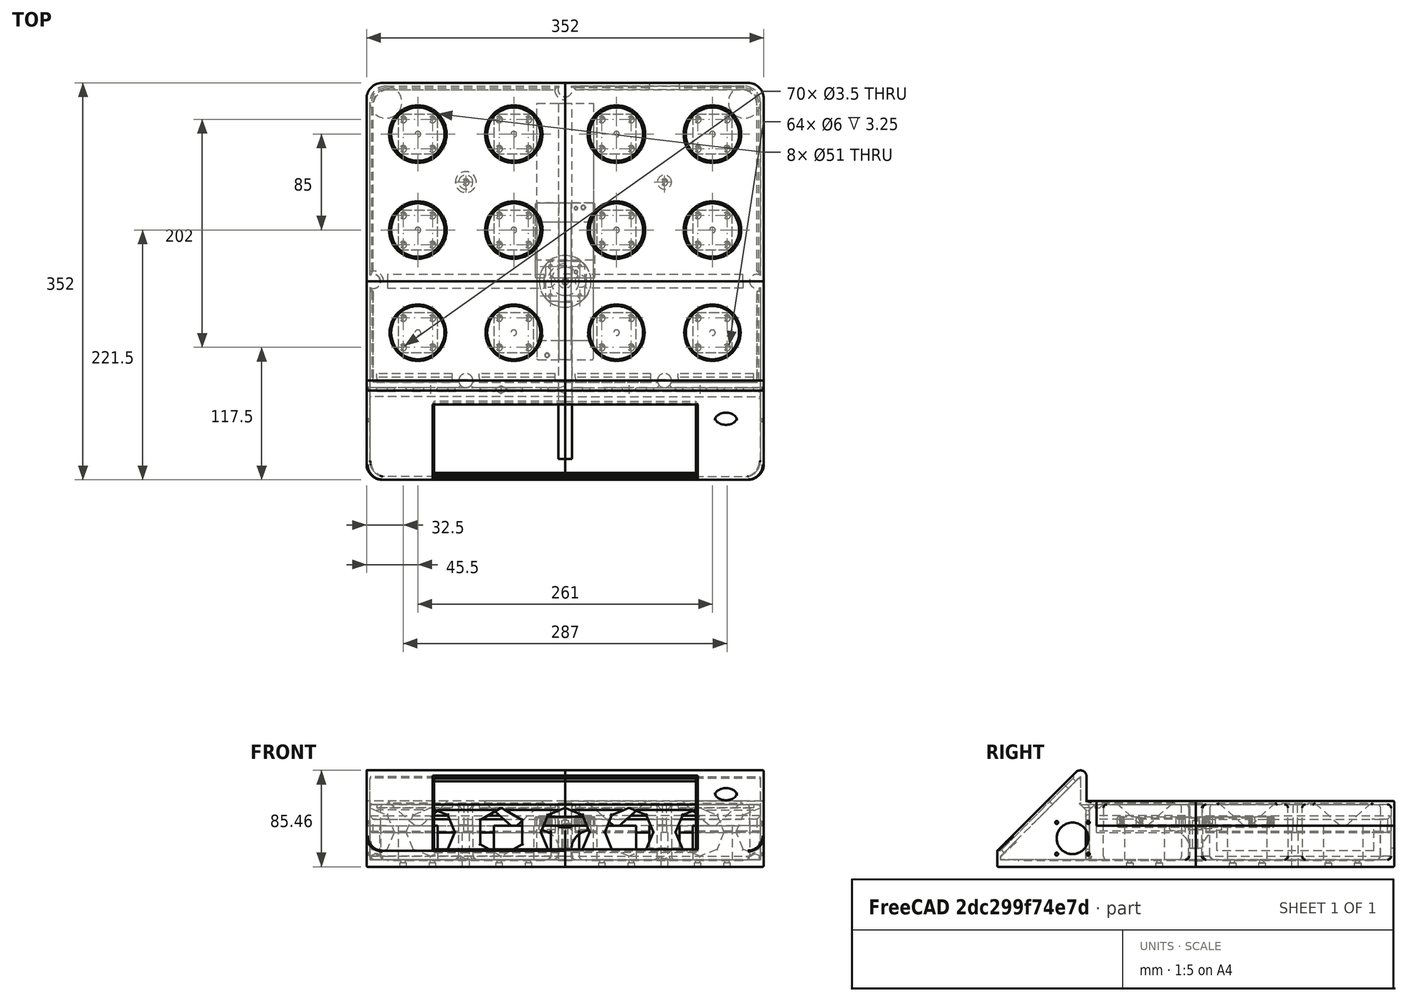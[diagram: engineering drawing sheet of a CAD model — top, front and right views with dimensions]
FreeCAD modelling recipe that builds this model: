
FCSTD DOCUMENT  (FreeCAD 2023.131R26244 +5365 (Git))
Label: Magnetic Stirrer
License: All rights reserved
LicenseURL: http://en.wikipedia.org/wiki/All_rights_reserved
objects: Sketcher::SketchObject×111, PartDesign::Pocket×58, PartDesign::Pad×49, PartDesign::Fillet×26, PartDesign::Body×19, PartDesign::Chamfer×13, PartDesign::Hole×3, Spreadsheet::Sheet×1, PartDesign::Revolution×1
note: 691 computed .brp shape members not serialized (recipe doc carries the construction recipe); baked Part::Feature solids carry a one-line shape summary decoded from their .brp

FEATURE [Spreadsheet::Sheet] Spreadsheet  label="Parameters"
  PythonMode = false
  ShowCells = 0
  TreeRank = 10
  cells = A1=Thickness; B1(thickness)=3; A2=Clearance; B2(clearance)=0.4; A3=Station Diameter; B3(station_diameter)=85; A4=Stir Bar Length; B4(stir_bar_length)=28; A5=Lap Join Thickness; B5(lap_join_thickness)=1; A7=Screw Shaft Diameter; B7(screw_shaft_diameter)=3.5; D7=M3; A8=Screw Head Diameter; B8(screw_head_diameter)=6; A9=Threaded Insert Hole Diameter; B9(insert_hole_diameter)=3.74; A11=Magnet Diameter; B11(magnet_diameter)=10; A12=Magnet Thickness; B12(magnet_thickness)=3; A14=Motor Shaft Diameter; B14(motor_shaft_diameter)=5; A15=Motor Shaft Flat Diameter; B15(motor_shaft_flat_diameter)=4.5; A16=Motor Shaft Length; B16(motor_shaft_length)=19; A17=Motor Width; B17(motor_width)=35; A18=Motor Height; B18(motor_height)=30; A19=Motor Screw Spacing; B19(motor_screw_spacing)=26; A20=Motor Screw Shaft Diameter; B20(motor_screw_shaft_diameter)=3.5; D20=M3; A21=Motor Screw Head Diameter; B21(motor_screw_head_diameter)=6; A22=Motor Screw Head Height; B22(motor_screw_head_height)=3.25; A23=Motor Shaft Mouth Diameter; B23(motor_shaft_mount_diameter)==stir_bar_length + magnet_diameter + 4 * thickness; A25=Screen Angle; B25(screen_angle)=135; A26=Screen Opening Width; B26(screen_opening_width)=232; A27=Screen Opening Height; B27(screen_opening_height)=89.5; A28=Screen Overall Width; B28(screen_overall_width)=239; A29=Screen Overall Heigth; B29(screen_overall_height)=94; A30=Screen Overall Thickness; B30(screen_overall_thickness)=12; A31=Screen Body Thickness; B31(screen_body_thickness)=5.5; A32=Screen Screen Thickness; B32(screen_screen_thickness)=1.5; A33=Screen Relief Width; B33(screen_relief_width)=1.5; A34=Screen Relief Depth; B34(screen_relief_depth)=2; A35=Screen Position; B35(screen_position)=92; A37=Power Supply Width; B37(psu_width)=50; A38=Power Supply Length; B38(psu_length)=139; A39=Power Supply Height; B39(psu_height)=22.25; A40=PSU Screw x-offset; B40(psu_screw_x_offset)==psu_width - 18; A41=PSU Screw y-offset; B41(psu_screw_y_offset)==psu_length - 8; A42=PSU Screw Length; B42(psu_screw_length)=8; A44=Power Connector Width; B44(power_connector_width)=26.8; A45=Power Connector Height; B45(power_connector_height)=19.9; A46=Power Switch Diameter; B46(power_switch_diameter)=19.5; A48=Fan Width; B48(fan_width)=29.9; A49=Fan Diameter; B49(fan_diameter)=28; A50=Fan Screw Hole Distance; B50(fan_screw_distance)=28; A51=Fan Screw Hole Diameter; B51(fan_screw_hole_diameter)=2.6; A53=PCB Board Width; B53(pcb_width)=105; A54=PCB Board Length; B54(pcb_length)=50; A55=PCB Board H Screw Distance; B55(pcb_h_screw)=97; A56=PCB Board V Screw Distance; B56(pcb_v_screw)=42
FEATURE [Sketcher::SketchObject] Sketch003
  ArcFitTolerance = 1e-06
  AttachmentSupport = -> [XY_Plane001]
  ExternalBSplineMaxDegree = 5
  ExternalBSplineTolerance = 0.0001
  FullyConstrained = true
  InternalTolerance = 1e-06
  InvalidShape = false
  MakeInternals = false
  MapMode = 5
  Support = -> [XY_Plane001]
  TreeRank = 37
  ValidateShape = true
  expr: Constraints[11] = <<Parameters>>.station_diameter
  expr: Constraints[12] = <<Parameters>>.station_diameter
  expr: Constraints[14] = <<Parameters>>.motor_shaft_mount_diameter + 1
  expr: Constraints[25] = <<Parameters>>.station_diameter / 3
  expr: Constraints[26] = <<Parameters>>.station_diameter + <<Parameters>>.thickness
  expr: Constraints[27] = (<<Parameters>>.station_diameter + <<Parameters>>.thickness) * 2
  expr: Constraints[30] = (<<Parameters>>.station_diameter + <<Parameters>>.thickness) * 2
  expr: Constraints[31] = <<Parameters>>.station_diameter + <<Parameters>>.thickness
  expr: Constraints[4] = <<Parameters>>.station_diameter
  sketch-geometry (14):
    g0: LineSegment StartX=88 StartY=88 StartZ=0 EndX=-73.8333 EndY=88 EndZ=0
    g1: LineSegment StartX=-88 StartY=73.8333 StartZ=0 EndX=-88 EndY=-88 EndZ=0
    g2: GeomPoint [constr] X=0 Y=0 Z=0
    g3: Circle [constr] CenterX=-42.5 CenterY=42.5 CenterZ=0 NormalX=0 NormalY=0 NormalZ=1 AngleXU=0 Radius=42.5
    g4: Circle [constr] CenterX=42.5 CenterY=42.5 CenterZ=0 NormalX=0 NormalY=0 NormalZ=1 AngleXU=0 Radius=42.5
    g5: Circle [constr] CenterX=-42.5 CenterY=-42.5 CenterZ=0 NormalX=0 NormalY=0 NormalZ=1 AngleXU=0 Radius=42.5
    g6: Circle [constr] CenterX=42.5 CenterY=-42.5 CenterZ=0 NormalX=0 NormalY=0 NormalZ=1 AngleXU=0 Radius=42.5
    g7: Circle CenterX=-42.5 CenterY=42.5 CenterZ=0 NormalX=0 NormalY=0 NormalZ=1 AngleXU=0 Radius=25.5
    g8: Circle CenterX=42.5 CenterY=42.5 CenterZ=0 NormalX=0 NormalY=0 NormalZ=1 AngleXU=0 Radius=25.5
    g9: Circle CenterX=42.5 CenterY=-42.5 CenterZ=0 NormalX=0 NormalY=0 NormalZ=1 AngleXU=0 Radius=25.5
    g10: Circle CenterX=-42.5 CenterY=-42.5 CenterZ=0 NormalX=0 NormalY=0 NormalZ=1 AngleXU=0 Radius=25.5
    g11: LineSegment StartX=88 StartY=-88 StartZ=0 EndX=88 EndY=88 EndZ=0
    g12: LineSegment StartX=-88 StartY=-88 StartZ=0 EndX=88 EndY=-88 EndZ=0
    g13: ArcOfCircle CenterX=-73.8333 CenterY=73.8333 CenterZ=0 NormalX=0 NormalY=0 NormalZ=1 AngleXU=0 Radius=14.1667 StartAngle=1.5708 EndAngle=3.14159
  constraints (32):
    c: Coincident(g11,g0)
    c: Horizontal(g0)
    c: Vertical(g1)
    c: Coincident(g2,g-1)
    c: Diameter(g3) = 85
    c: Equal(g3,g4)
    c: Equal(g3,g5)
    c: Equal(g3,g6)
    c: Symmetric(g3,g6,g2)
    c: Symmetric(g5,g4,g2)
    c: Symmetric(g3,g5,g-1)
    c: DistanceX(g3,g4) = 85
    c: DistanceY(g5,g3) = 85
    c: Coincident(g7,g3)
    c: Diameter(g7) = 51
    c: Coincident(g8,g4)
    c: Coincident(g9,g6)
    c: Coincident(g10,g5)
    c: Equal(g7,g8)
    c: Equal(g7,g10)
    c: Equal(g7,g9)
    c: Vertical(g11)
    c: Horizontal(g12)
    c: Coincident(g12,g1)
    c: Coincident(g11,g12)
    c: Diameter(g13) = 28.3333
    c: DistanceY(g2,g0) = 88
    c: DistanceY(g11,g0) = 176
    c: Tangent(g0,g13) = -1.5708
    c: Tangent(g1,g13) = -1.5708
    c: DistanceX(g1,g11) = 176
    c: DistanceX(g2,g0) = 88
FEATURE [PartDesign::Pad] Pad001
  AddSubType = 0
  AlongSketchNormal = false
  AutoTaperInnerAngle = true
  CheckUpToFaceLimits = true
  ClaimChildren = false
  Direction = (0,0,1)
  Fit = 0
  FitJoin = 0
  InnerFit = 0
  InnerFitJoin = 0
  InvalidShape = false
  Length = 3
  Length2 = 1
  Linearize = true
  NewSolid = false
  Profile = -> Sketch003
  Suppress = false
  TaperInnerAngle = 0
  TaperInnerAngleRev = 0
  TreeRank = 38
  Type = 0
  ValidateShape = true
  _ProfileBasedVersion = 1
  expr: Length = <<Parameters>>.thickness
  expr: Length2 = <<Parameters>>.lap_join_thickness
FEATURE [Sketcher::SketchObject] Sketch004
  ArcFitTolerance = 1e-06
  ExternalBSplineMaxDegree = 5
  ExternalBSplineTolerance = 0.0001
  FullyConstrained = true
  InternalTolerance = 1e-06
  InvalidShape = false
  MakeInternals = false
  MapMode = 2
  TreeRank = 39
  ValidateShape = true
  expr: Constraints[13] = <<Parameters>>.station_diameter + <<Parameters>>.thickness
  expr: Constraints[19] = <<Parameters>>.motor_shaft_mount_diameter / 4
  expr: Constraints[2] = <<Parameters>>.thickness
  expr: Constraints[32] = <<Parameters>>.motor_shaft_mount_diameter / 4
  expr: Constraints[33] = <<Parameters>>.motor_shaft_mount_diameter / 4
  expr: Constraints[34] = <<Parameters>>.station_diameter + <<Parameters>>.thickness
  expr: Constraints[35] = <<Parameters>>.station_diameter + <<Parameters>>.thickness
  expr: Constraints[3] = <<Parameters>>.station_diameter + <<Parameters>>.thickness
  expr: Constraints[42] = <<Parameters>>.thickness
  expr: Constraints[43] = <<Parameters>>.motor_shaft_mount_diameter / 4
  expr: Constraints[44] = <<Parameters>>.motor_shaft_mount_diameter / 4
  expr: Constraints[4] = <<Parameters>>.station_diameter + <<Parameters>>.thickness
  expr: Constraints[8] = <<Parameters>>.station_diameter / 3
  sketch-geometry (15):
    g0: LineSegment StartX=-88 StartY=-88 StartZ=0 EndX=-88 EndY=73.8333 EndZ=0
    g1: LineSegment StartX=-85 StartY=-82.6615 StartZ=0 EndX=-85 EndY=70.8333 EndZ=0
    g2: LineSegment [constr] StartX=0 StartY=0 StartZ=0 EndX=-83.8507 EndY=83.8507 EndZ=0
    g3: ArcOfCircle CenterX=-73.8333 CenterY=73.8333 CenterZ=0 NormalX=0 NormalY=0 NormalZ=1 AngleXU=0 Radius=14.1667 StartAngle=1.5708 EndAngle=3.14159
    g4: ArcOfCircle CenterX=-70.8333 CenterY=70.8333 CenterZ=0 NormalX=0 NormalY=0 NormalZ=1 AngleXU=0 Radius=14.1667 StartAngle=1.57079 EndAngle=3.14159
    g5: LineSegment StartX=-73.8333 StartY=88 StartZ=0 EndX=88 EndY=88 EndZ=0
    g6: LineSegment StartX=-70.8333 StartY=85 StartZ=0 EndX=82.6615 EndY=85 EndZ=0
    g7: ArcOfCircle CenterX=88 CenterY=81.75 CenterZ=0 NormalX=0 NormalY=0 NormalZ=1 AngleXU=0 Radius=6.25 StartAngle=2.59474 EndAngle=4.71239
    g8: ArcOfCircle CenterX=-81.75 CenterY=-88 CenterZ=0 NormalX=0 NormalY=0 NormalZ=1 AngleXU=0 Radius=6.25 StartAngle=4.1e-15 EndAngle=2.11765
    g9: LineSegment StartX=88 StartY=88 StartZ=0 EndX=88 EndY=75.5 EndZ=0
    g10: LineSegment StartX=-88 StartY=-88 StartZ=0 EndX=-75.5 EndY=-88 EndZ=0
    g11: Circle CenterX=0 CenterY=0 CenterZ=0 NormalX=0 NormalY=0 NormalZ=1 AngleXU=0 Radius=6.25
    g12: ArcOfCircle CenterX=88 CenterY=-88 CenterZ=0 NormalX=0 NormalY=0 NormalZ=1 AngleXU=0 Radius=12.5 StartAngle=1.5708 EndAngle=3.14159
    g13: LineSegment StartX=88 StartY=-88 StartZ=0 EndX=75.5 EndY=-88 EndZ=0
    g14: LineSegment StartX=88 StartY=-88 StartZ=0 EndX=88 EndY=-75.5 EndZ=0
  constraints (45):
    c: Vertical(g0)
    c: Vertical(g1)
    c: DistanceX(g0,g1) = 3
    c: DistanceX(g0,g-1) = 88
    c: DistanceY(g0,g-1) = 88
    c: Coincident(g2,g-1)
    c: Angle(g-2,g2) = 0.785398
    c: PointOnObject(g3,g2)
    c: Diameter(g3) = 28.3333
    c: PointOnObject(g4,g2)
    c: Equal(g3,g4)
    c: Horizontal(g5)
    c: Horizontal(g6)
    c: DistanceX(g2,g5) = 88
    c: PointOnObject(g2,g3)
    c: Coincident(g4,g6)
    c: Tangent(g3,g5) = 1.5708
    c: Tangent(g4,g1) = 1.5708
    c: Tangent(g3,g0) = 1.5708
    c: Diameter(g7) = 12.5
    c: Equal(g7,g8)
    c: Vertical(g9)
    c: PointOnObject(g7,g9)
    c: Horizontal(g10)
    c: PointOnObject(g8,g10)
    c: Coincident(g9,g5)
    c: Coincident(g7,g9)
    c: Coincident(g7,g6)
    c: Coincident(g10,g0)
    c: Coincident(g8,g1)
    c: Coincident(g8,g10)
    c: Coincident(g11,g2)
    c: Diameter(g11) = 12.5
    c: Radius(g12) = 12.5
    c: DistanceY(g12,g11) = 88
    c: DistanceX(g11,g12) = 88
    c: Coincident(g13,g12)
    c: Horizontal(g13)
    c: Coincident(g14,g12)
    c: Vertical(g14)
    c: Coincident(g12,g13)
    c: Coincident(g12,g14)
    c: DistanceY(g4,g3) = 3
    c: DistanceY(g7,g5) = 12.5
    c: DistanceX(g0,g8) = 12.5
FEATURE [PartDesign::Pad] Pad002
  AddSubType = 0
  AlongSketchNormal = false
  AutoTaperInnerAngle = true
  BaseFeature = -> Pad001
  CheckUpToFaceLimits = true
  ClaimChildren = false
  Direction = (0,0,1)
  Fit = 0
  FitJoin = 0
  InnerFit = 0
  InnerFitJoin = 0
  InvalidShape = false
  Length = 19
  Length2 = 100
  Linearize = true
  NewSolid = false
  Profile = -> Sketch004
  Reversed = true
  Suppress = false
  TaperInnerAngle = 0
  TaperInnerAngleRev = 0
  TreeRank = 40
  Type = 0
  ValidateShape = true
  _ProfileBasedVersion = 1
  expr: Length = <<Parameters>>.motor_shaft_length
FEATURE [Sketcher::SketchObject] Sketch005
  ArcFitTolerance = 1e-06
  ExternalBSplineMaxDegree = 5
  ExternalBSplineTolerance = 0.0001
  FullyConstrained = true
  InternalTolerance = 1e-06
  InvalidShape = false
  MakeInternals = false
  MapMode = 2
  Placement = pos=(0,0,-13) rot=(0,0,1;0rad)
  TreeRank = 41
  ValidateShape = true
  expr: Placement.Base.z = -<<Parameters>>.motor_shaft_length + 2 * <<Parameters>>.thickness
  expr: Constraints[11] = <<Parameters>>.station_diameter / 3
  expr: Constraints[20] = <<Parameters>>.station_diameter - 2 * <<Parameters>>.thickness
  expr: Constraints[5] = <<Parameters>>.thickness
  expr: Constraints[6] = <<Parameters>>.station_diameter
  expr: Constraints[7] = <<Parameters>>.station_diameter - 2 * <<Parameters>>.thickness
  sketch-geometry (9):
    g0: LineSegment StartX=-85 StartY=-79 StartZ=0 EndX=-85 EndY=70.8333 EndZ=0
    g1: LineSegment StartX=-82 StartY=-79 StartZ=0 EndX=-82 EndY=67.8333 EndZ=0
    g2: LineSegment StartX=-85 StartY=-79 StartZ=0 EndX=-82 EndY=-79 EndZ=0
    g3: LineSegment [constr] StartX=0 StartY=0 StartZ=0 EndX=-80.8507 EndY=80.8507 EndZ=0
    g4: ArcOfCircle CenterX=-70.8333 CenterY=70.8333 CenterZ=0 NormalX=0 NormalY=0 NormalZ=1 AngleXU=0 Radius=14.1667 StartAngle=1.5708 EndAngle=3.14159
    g5: ArcOfCircle CenterX=-67.8333 CenterY=67.8333 CenterZ=0 NormalX=0 NormalY=0 NormalZ=1 AngleXU=0 Radius=14.1667 StartAngle=1.5708 EndAngle=3.14159
    g6: LineSegment StartX=-70.8333 StartY=85 StartZ=0 EndX=79 EndY=85 EndZ=0
    g7: LineSegment StartX=-67.8334 StartY=82 StartZ=0 EndX=79 EndY=82 EndZ=0
    g8: LineSegment StartX=79 StartY=82 StartZ=0 EndX=79 EndY=85 EndZ=0
  constraints (26):
    c: Vertical(g0)
    c: Vertical(g1)
    c: Coincident(g2,g0)
    c: Coincident(g2,g1)
    c: Horizontal(g2)
    c: DistanceX(g0,g1) = 3
    c: DistanceX(g0,g-1) = 85
    c: DistanceY(g0,g-1) = 79
    c: Coincident(g3,g-1)
    c: Angle(g-2,g3) = 0.785398
    c: PointOnObject(g4,g3)
    c: Diameter(g4) = 28.3333
    c: PointOnObject(g5,g3)
    c: Equal(g4,g5)
    c: Horizontal(g6)
    c: Horizontal(g7)
    c: Coincident(g8,g7)
    c: Coincident(g8,g6)
    c: Vertical(g8)
    c: Equal(g2,g8)
    c: DistanceX(g3,g6) = 79
    c: PointOnObject(g3,g4)
    c: Coincident(g5,g7)
    c: Tangent(g4,g6) = 1.5708
    c: Tangent(g5,g1) = 1.5708
    c: Tangent(g4,g0) = 1.5708
FEATURE [PartDesign::Pad] Pad003
  AddSubType = 0
  AlongSketchNormal = false
  AutoTaperInnerAngle = true
  BaseFeature = -> Pad002
  CheckUpToFaceLimits = true
  ClaimChildren = false
  Direction = (0,0,1)
  Fit = 0
  FitJoin = 0
  InnerFit = 0
  InnerFitJoin = 0
  InvalidShape = false
  Length = 12
  Length2 = 100
  Linearize = true
  NewSolid = false
  Profile = -> Sketch005
  Reversed = true
  Suppress = false
  TaperInnerAngle = 0
  TaperInnerAngleRev = 0
  TreeRank = 42
  Type = 0
  ValidateShape = true
  _ProfileBasedVersion = 1
  expr: Length = <<Parameters>>.thickness * 4
FEATURE [Sketcher::SketchObject] Sketch006
  ArcFitTolerance = 1e-06
  ExternalBSplineMaxDegree = 5
  ExternalBSplineTolerance = 0.0001
  FullyConstrained = true
  InternalTolerance = 1e-06
  InvalidShape = false
  MakeInternals = false
  MapMode = 2
  TreeRank = 46
  ValidateShape = true
  expr: Constraints[14] = <<Parameters>>.thickness * 2
  expr: Constraints[16] = (<<Parameters>>.station_diameter + <<Parameters>>.thickness) * 2 - 4 * <<Parameters>>.thickness - <<Parameters>>.motor_shaft_mount_diameter / 2
  expr: Constraints[20] = <<Parameters>>.station_diameter + <<Parameters>>.thickness
  expr: Constraints[21] = <<Parameters>>.station_diameter + <<Parameters>>.thickness
  sketch-geometry (8):
    g0: LineSegment StartX=88 StartY=69.5 StartZ=0 EndX=82 EndY=69.5 EndZ=0
    g1: LineSegment StartX=82 StartY=69.5 StartZ=0 EndX=82 EndY=-69.5 EndZ=0
    g2: LineSegment StartX=82 StartY=-69.5 StartZ=0 EndX=88 EndY=-69.5 EndZ=0
    g3: LineSegment StartX=88 StartY=-69.5 StartZ=0 EndX=88 EndY=69.5 EndZ=0
    g4: LineSegment StartX=-69.5 StartY=-88 StartZ=0 EndX=69.5 EndY=-88 EndZ=0
    g5: LineSegment StartX=69.5 StartY=-88 StartZ=0 EndX=69.5 EndY=-82 EndZ=0
    g6: LineSegment StartX=69.5 StartY=-82 StartZ=0 EndX=-69.5 EndY=-82 EndZ=0
    g7: LineSegment StartX=-69.5 StartY=-82 StartZ=0 EndX=-69.5 EndY=-88 EndZ=0
  constraints (22):
    c: Coincident(g0,g1)
    c: Coincident(g1,g2)
    c: Coincident(g2,g3)
    c: Coincident(g3,g0)
    c: Horizontal(g0)
    c: Horizontal(g2)
    c: Vertical(g1)
    c: Coincident(g4,g5)
    c: Coincident(g5,g6)
    c: Coincident(g6,g7)
    c: Coincident(g7,g4)
    c: Horizontal(g6)
    c: Vertical(g5)
    c: Vertical(g7)
    c: DistanceX(g0,g0) = 6
    c: Equal(g0,g5)
    c: DistanceY(g2,g0) = 139
    c: Symmetric(g0,g2,g-1)
    c: Symmetric(g4,g4,g-2)
    c: Equal(g3,g4)
    c: DistanceX(g-1,g0) = 88
    c: DistanceY(g4,g-1) = 88
FEATURE [PartDesign::Pocket] Pocket001
  AddSubType = 1
  AutoTaperInnerAngle = true
  BaseFeature = -> Pad003
  CheckUpToFaceLimits = true
  ClaimChildren = false
  Fit = 0
  FitJoin = 0
  InnerFit = 0
  InnerFitJoin = 0
  InvalidShape = false
  Length = 1
  Length2 = 100
  Linearize = true
  NewSolid = false
  Profile = -> Sketch006
  Reversed = true
  Suppress = false
  TaperInnerAngle = 0
  TaperInnerAngleRev = 0
  TreeRank = 47
  Type = 0
  ValidateShape = true
  _ProfileBasedVersion = 1
  _Version = 1
  expr: Length = <<Parameters>>.lap_join_thickness
FEATURE [PartDesign::Chamfer] Chamfer
  AddSubType = 0
  Angle = 45
  Base = -> Pocket001 [Edge89]
  BaseFeature = -> Pocket001
  ChamferType = 0
  FlipDirection = false
  InvalidShape = false
  NewSolid = false
  Size = 2.99
  Size2 = 1
  SupportTransform = false
  Suppress = false
  TreeRank = 50
  ValidateShape = true
  expr: Size = <<Parameters>>.thickness - 0.01
FEATURE [Sketcher::SketchObject] Sketch008
  ArcFitTolerance = 1e-06
  AttachmentSupport = -> [XY_Plane002]
  ExternalBSplineMaxDegree = 5
  ExternalBSplineTolerance = 0.0001
  FullyConstrained = true
  InternalTolerance = 1e-06
  InvalidShape = false
  MakeInternals = false
  MapMode = 5
  Support = -> [XY_Plane002]
  TreeRank = 63
  ValidateShape = true
  expr: Constraints[11] = <<Parameters>>.station_diameter
  expr: Constraints[12] = <<Parameters>>.station_diameter
  expr: Constraints[17] = <<Parameters>>.station_diameter / 3
  expr: Constraints[18] = <<Parameters>>.station_diameter + <<Parameters>>.thickness
  expr: Constraints[19] = (<<Parameters>>.station_diameter + <<Parameters>>.thickness) * 2
  expr: Constraints[22] = (<<Parameters>>.station_diameter + <<Parameters>>.thickness) * 2
  expr: Constraints[23] = <<Parameters>>.station_diameter + <<Parameters>>.thickness
  expr: Constraints[4] = <<Parameters>>.station_diameter
  sketch-geometry (10):
    g0: LineSegment StartX=88 StartY=88 StartZ=0 EndX=-73.8333 EndY=88 EndZ=0
    g1: LineSegment StartX=-88 StartY=73.8333 StartZ=0 EndX=-88 EndY=-88 EndZ=0
    g2: GeomPoint [constr] X=0 Y=0 Z=0
    g3: Circle [constr] CenterX=-42.5 CenterY=42.5 CenterZ=0 NormalX=0 NormalY=0 NormalZ=1 AngleXU=0 Radius=42.5
    g4: Circle [constr] CenterX=42.5 CenterY=42.5 CenterZ=0 NormalX=0 NormalY=0 NormalZ=1 AngleXU=0 Radius=42.5
    g5: Circle [constr] CenterX=-42.5 CenterY=-42.5 CenterZ=0 NormalX=0 NormalY=0 NormalZ=1 AngleXU=0 Radius=42.5
    g6: Circle [constr] CenterX=42.5 CenterY=-42.5 CenterZ=0 NormalX=0 NormalY=0 NormalZ=1 AngleXU=0 Radius=42.5
    g7: LineSegment StartX=88 StartY=-88 StartZ=0 EndX=88 EndY=88 EndZ=0
    g8: LineSegment StartX=-88 StartY=-88 StartZ=0 EndX=88 EndY=-88 EndZ=0
    g9: ArcOfCircle CenterX=-73.8333 CenterY=73.8333 CenterZ=0 NormalX=0 NormalY=0 NormalZ=1 AngleXU=0 Radius=14.1667 StartAngle=1.5708 EndAngle=3.14159
  constraints (24):
    c: Coincident(g7,g0)
    c: Horizontal(g0)
    c: Vertical(g1)
    c: Coincident(g2,g-1)
    c: Diameter(g3) = 85
    c: Equal(g3,g4)
    c: Equal(g3,g5)
    c: Equal(g3,g6)
    c: Symmetric(g3,g6,g2)
    c: Symmetric(g5,g4,g2)
    c: Symmetric(g3,g5,g-1)
    c: DistanceX(g3,g4) = 85
    c: DistanceY(g5,g3) = 85
    c: Vertical(g7)
    c: Horizontal(g8)
    c: Coincident(g8,g1)
    c: Coincident(g7,g8)
    c: Diameter(g9) = 28.3333
    c: DistanceY(g2,g0) = 88
    c: DistanceY(g7,g0) = 176
    c: Tangent(g0,g9) = -1.5708
    c: Tangent(g1,g9) = -1.5708
    c: DistanceX(g1,g7) = 176
    c: DistanceX(g2,g0) = 88
FEATURE [PartDesign::Pad] Pad005
  AddSubType = 0
  AlongSketchNormal = false
  AutoTaperInnerAngle = true
  CheckUpToFaceLimits = true
  ClaimChildren = false
  Direction = (0,0,1)
  Fit = 0
  FitJoin = 0
  InnerFit = 0
  InnerFitJoin = 0
  InvalidShape = false
  Length = 6.25
  Length2 = 100
  Linearize = true
  NewSolid = false
  Profile = -> Sketch008
  Reversed = true
  Suppress = false
  TaperInnerAngle = 0
  TaperInnerAngleRev = 0
  TreeRank = 64
  Type = 0
  ValidateShape = true
  _ProfileBasedVersion = 1
  expr: Length = <<Parameters>>.thickness + <<Parameters>>.motor_screw_head_height
FEATURE [Sketcher::SketchObject] Sketch009
  ArcFitTolerance = 1e-06
  ExternalBSplineMaxDegree = 5
  ExternalBSplineTolerance = 0.0001
  FullyConstrained = false
  InternalTolerance = 1e-06
  InvalidShape = false
  MakeInternals = false
  MapMode = 2
  TreeRank = 65
  ValidateShape = true
  expr: Constraints[13] = <<Parameters>>.station_diameter + <<Parameters>>.thickness
  expr: Constraints[20] = <<Parameters>>.motor_shaft_mount_diameter / 4
  expr: Constraints[27] = <<Parameters>>.station_diameter + <<Parameters>>.thickness
  expr: Constraints[28] = <<Parameters>>.station_diameter + <<Parameters>>.thickness
  expr: Constraints[29] = <<Parameters>>.motor_shaft_mount_diameter / 4
  expr: Constraints[2] = <<Parameters>>.thickness
  expr: Constraints[3] = <<Parameters>>.station_diameter + <<Parameters>>.thickness
  expr: Constraints[4] = <<Parameters>>.station_diameter + <<Parameters>>.thickness
  expr: Constraints[8] = <<Parameters>>.station_diameter / 3
  sketch-geometry (15):
    g0: LineSegment StartX=-88 StartY=-88 StartZ=0 EndX=-88 EndY=73.8333 EndZ=0
    g1: LineSegment StartX=-85 StartY=-82.4087 StartZ=0 EndX=-85 EndY=70.8333 EndZ=0
    g2: LineSegment [constr] StartX=0 StartY=0 StartZ=0 EndX=-83.8507 EndY=83.8507 EndZ=0
    g3: ArcOfCircle CenterX=-73.8333 CenterY=73.8333 CenterZ=0 NormalX=0 NormalY=0 NormalZ=1 AngleXU=0 Radius=14.1667 StartAngle=1.5708 EndAngle=3.14159
    g4: ArcOfCircle CenterX=-70.8333 CenterY=70.8333 CenterZ=0 NormalX=0 NormalY=0 NormalZ=1 AngleXU=0 Radius=14.1667 StartAngle=1.57076 EndAngle=3.14159
    g5: LineSegment StartX=-73.8333 StartY=88 StartZ=0 EndX=88 EndY=88 EndZ=0
    g6: LineSegment StartX=-70.8328 StartY=85 StartZ=0 EndX=82.4428 EndY=85 EndZ=0
    g7: Circle CenterX=0 CenterY=0 CenterZ=0 NormalX=0 NormalY=0 NormalZ=1 AngleXU=0 Radius=6.25
    g8: ArcOfCircle CenterX=88 CenterY=-88 CenterZ=0 NormalX=0 NormalY=0 NormalZ=1 AngleXU=0 Radius=12.5 StartAngle=1.5708 EndAngle=3.14159
    g9: LineSegment StartX=88 StartY=-88 StartZ=0 EndX=75.5 EndY=-88 EndZ=0
    g10: LineSegment StartX=88 StartY=-88 StartZ=0 EndX=88 EndY=-75.5 EndZ=0
    g11: ArcOfCircle CenterX=88 CenterY=82.14 CenterZ=0 NormalX=0 NormalY=0 NormalZ=1 AngleXU=0 Radius=6.25 StartAngle=2.6663 EndAngle=4.71239
    g12: LineSegment StartX=88 StartY=88 StartZ=0 EndX=88 EndY=75.89 EndZ=0
    g13: ArcOfCircle CenterX=-82.2072 CenterY=-88 CenterZ=0 NormalX=0 NormalY=0 NormalZ=1 AngleXU=0 Radius=6.25 StartAngle=2.4e-15 EndAngle=2.03403
    g14: LineSegment StartX=-88 StartY=-88 StartZ=0 EndX=-75.9572 EndY=-88 EndZ=0
  constraints (42):
    c: Vertical(g0)
    c: Vertical(g1)
    c: DistanceX(g0,g1) = 3
    c: DistanceX(g0,g-1) = 88
    c: DistanceY(g0,g-1) = 88
    c: Coincident(g2,g-1)
    c: Angle(g-2,g2) = 0.785398
    c: PointOnObject(g3,g2)
    c: Diameter(g3) = 28.3333
    c: PointOnObject(g4,g2)
    c: Equal(g3,g4)
    c: Horizontal(g5)
    c: Horizontal(g6)
    c: DistanceX(g2,g5) = 88
    c: PointOnObject(g2,g3)
    c: Coincident(g4,g6)
    c: Tangent(g3,g5) = 1.5708
    c: Tangent(g4,g1) = 1.5708
    c: Tangent(g3,g0) = 1.5708
    c: Coincident(g7,g2)
    c: Diameter(g7) = 12.5
    c: Coincident(g9,g8)
    c: Coincident(g10,g8)
    c: Vertical(g10)
    c: Horizontal(g9)
    c: Coincident(g8,g9)
    c: Coincident(g8,g10)
    c: DistanceX(g7,g8) = 88
    c: DistanceY(g8,g7) = 88
    c: Radius(g8) = 12.5
    c: Equal(g7,g11)
    c: Vertical(g12)
    c: PointOnObject(g11,g12)
    c: Coincident(g12,g5)
    c: Coincident(g11,g12)
    c: Coincident(g11,g6)
    c: Equal(g7,g13)
    c: Horizontal(g14)
    c: PointOnObject(g13,g14)
    c: Coincident(g14,g0)
    c: Coincident(g13,g14)
    c: Coincident(g13,g1)
FEATURE [PartDesign::Pad] Pad006
  AddSubType = 0
  AlongSketchNormal = false
  AutoTaperInnerAngle = true
  BaseFeature = -> Pad005
  CheckUpToFaceLimits = true
  ClaimChildren = false
  Direction = (0,0,1)
  Fit = 0
  FitJoin = 0
  InnerFit = 0
  InnerFitJoin = 0
  InvalidShape = false
  Length = 30
  Length2 = 100
  Linearize = true
  NewSolid = false
  Profile = -> Sketch009
  Suppress = false
  TaperInnerAngle = 0
  TaperInnerAngleRev = 0
  TreeRank = 66
  Type = 0
  ValidateShape = true
  _ProfileBasedVersion = 1
  expr: Length = <<Parameters>>.motor_height
FEATURE [Sketcher::SketchObject] Sketch010
  ArcFitTolerance = 1e-06
  ExternalBSplineMaxDegree = 5
  ExternalBSplineTolerance = 0.0001
  FullyConstrained = true
  InternalTolerance = 1e-06
  InvalidShape = false
  MakeInternals = false
  MapMode = 2
  TreeRank = 67
  ValidateShape = true
  expr: Constraints[0] = <<Parameters>>.station_diameter
  expr: Constraints[19] = <<Parameters>>.motor_screw_spacing
  expr: Constraints[58] = <<Parameters>>.motor_screw_shaft_diameter
  expr: Constraints[7] = <<Parameters>>.station_diameter
  expr: Constraints[8] = <<Parameters>>.station_diameter
  sketch-geometry (40):
    g0: Circle [constr] CenterX=-42.5 CenterY=42.5 CenterZ=0 NormalX=0 NormalY=0 NormalZ=1 AngleXU=0 Radius=42.5
    g1: Circle [constr] CenterX=42.5 CenterY=42.5 CenterZ=0 NormalX=0 NormalY=0 NormalZ=1 AngleXU=0 Radius=42.5
    g2: Circle [constr] CenterX=-42.5 CenterY=-42.5 CenterZ=0 NormalX=0 NormalY=0 NormalZ=1 AngleXU=0 Radius=42.5
    g3: Circle [constr] CenterX=42.5 CenterY=-42.5 CenterZ=0 NormalX=0 NormalY=0 NormalZ=1 AngleXU=0 Radius=42.5
    g4: LineSegment [constr] StartX=-29.5 StartY=29.5 StartZ=0 EndX=-29.5 EndY=55.5 EndZ=0
    g5: LineSegment [constr] StartX=-29.5 StartY=55.5 StartZ=0 EndX=-55.5 EndY=55.5 EndZ=0
    g6: LineSegment [constr] StartX=-55.5 StartY=55.5 StartZ=0 EndX=-55.5 EndY=29.5 EndZ=0
    g7: LineSegment [constr] StartX=-55.5 StartY=29.5 StartZ=0 EndX=-29.5 EndY=29.5 EndZ=0
    g8: GeomPoint [constr] X=-42.5 Y=42.5 Z=0
    g9: LineSegment [constr] StartX=55.5 StartY=29.5 StartZ=0 EndX=55.5 EndY=55.5 EndZ=0
    g10: LineSegment [constr] StartX=55.5 StartY=55.5 StartZ=0 EndX=29.5 EndY=55.5 EndZ=0
    g11: LineSegment [constr] StartX=29.5 StartY=55.5 StartZ=0 EndX=29.5 EndY=29.5 EndZ=0
    g12: LineSegment [constr] StartX=29.5 StartY=29.5 StartZ=0 EndX=55.5 EndY=29.5 EndZ=0
    g13: GeomPoint [constr] X=42.5 Y=42.5 Z=0
    g14: LineSegment [constr] StartX=-29.5 StartY=-55.5 StartZ=0 EndX=-29.5 EndY=-29.5 EndZ=0
    g15: LineSegment [constr] StartX=-29.5 StartY=-29.5 StartZ=0 EndX=-55.5 EndY=-29.5 EndZ=0
    g16: LineSegment [constr] StartX=-55.5 StartY=-29.5 StartZ=0 EndX=-55.5 EndY=-55.5 EndZ=0
    g17: LineSegment [constr] StartX=-55.5 StartY=-55.5 StartZ=0 EndX=-29.5 EndY=-55.5 EndZ=0
    g18: GeomPoint [constr] X=-42.5 Y=-42.5 Z=0
    g19: LineSegment [constr] StartX=55.5 StartY=-55.5 StartZ=0 EndX=55.5 EndY=-29.5 EndZ=0
    g20: LineSegment [constr] StartX=55.5 StartY=-29.5 StartZ=0 EndX=29.5 EndY=-29.5 EndZ=0
    g21: LineSegment [constr] StartX=29.5 StartY=-29.5 StartZ=0 EndX=29.5 EndY=-55.5 EndZ=0
    g22: LineSegment [constr] StartX=29.5 StartY=-55.5 StartZ=0 EndX=55.5 EndY=-55.5 EndZ=0
    g23: GeomPoint [constr] X=42.5 Y=-42.5 Z=0
    g24: Circle CenterX=-55.5 CenterY=55.5 CenterZ=0 NormalX=0 NormalY=0 NormalZ=1 AngleXU=0 Radius=1.75
    g25: Circle CenterX=-29.5 CenterY=55.5 CenterZ=0 NormalX=0 NormalY=0 NormalZ=1 AngleXU=0 Radius=1.75
    g26: Circle CenterX=-29.5 CenterY=29.5 CenterZ=0 NormalX=0 NormalY=0 NormalZ=1 AngleXU=0 Radius=1.75
    g27: Circle CenterX=-55.5 CenterY=29.5 CenterZ=0 NormalX=0 NormalY=0 NormalZ=1 AngleXU=0 Radius=1.75
    g28: Circle CenterX=29.5 CenterY=55.5 CenterZ=0 NormalX=0 NormalY=0 NormalZ=1 AngleXU=0 Radius=1.75
    g29: Circle CenterX=55.5 CenterY=55.5 CenterZ=0 NormalX=0 NormalY=0 NormalZ=1 AngleXU=0 Radius=1.75
    g30: Circle CenterX=55.5 CenterY=29.5 CenterZ=0 NormalX=0 NormalY=0 NormalZ=1 AngleXU=0 Radius=1.75
    g31: Circle CenterX=29.5 CenterY=29.5 CenterZ=0 NormalX=0 NormalY=0 NormalZ=1 AngleXU=0 Radius=1.75
    g32: Circle CenterX=29.5 CenterY=-29.5 CenterZ=0 NormalX=0 NormalY=0 NormalZ=1 AngleXU=0 Radius=1.75
    g33: Circle CenterX=55.5 CenterY=-29.5 CenterZ=0 NormalX=0 NormalY=0 NormalZ=1 AngleXU=0 Radius=1.75
    g34: Circle CenterX=55.5 CenterY=-55.5 CenterZ=0 NormalX=0 NormalY=0 NormalZ=1 AngleXU=0 Radius=1.75
    g35: Circle CenterX=29.5 CenterY=-55.5 CenterZ=0 NormalX=0 NormalY=0 NormalZ=1 AngleXU=0 Radius=1.75
    g36: Circle CenterX=-55.5 CenterY=-29.5 CenterZ=0 NormalX=0 NormalY=0 NormalZ=1 AngleXU=0 Radius=1.75
    g37: Circle CenterX=-29.5 CenterY=-29.5 CenterZ=0 NormalX=0 NormalY=0 NormalZ=1 AngleXU=0 Radius=1.75
    g38: Circle CenterX=-29.5 CenterY=-55.5 CenterZ=0 NormalX=0 NormalY=0 NormalZ=1 AngleXU=0 Radius=1.75
    g39: Circle CenterX=-55.5 CenterY=-55.5 CenterZ=0 NormalX=0 NormalY=0 NormalZ=1 AngleXU=0 Radius=1.75
  constraints (89):
    c: Diameter(g0) = 85
    c: Equal(g0,g1)
    c: Equal(g0,g2)
    c: Equal(g0,g3)
    c: Symmetric(g0,g3,g-1)
    c: Symmetric(g1,g2,g-1)
    c: Symmetric(g0,g1,g-2)
    c: DistanceX(g0,g1) = 85
    c: DistanceY(g3,g1) = 85
    c: Coincident(g4,g5)
    c: Coincident(g5,g6)
    c: Coincident(g6,g7)
    c: Coincident(g7,g4)
    c: Horizontal(g5)
    c: Horizontal(g7)
    c: Vertical(g4)
    c: Vertical(g6)
    c: Symmetric(g5,g4,g8)
    c: Coincident(g8,g0)
    c: DistanceX(g5,g4) = 26
    c: Equal(g5,g6)
    c: Coincident(g9,g10)
    c: Coincident(g10,g11)
    c: Coincident(g11,g12)
    c: Coincident(g12,g9)
    c: Horizontal(g10)
    c: Horizontal(g12)
    c: Vertical(g9)
    c: Vertical(g11)
    c: Symmetric(g10,g9,g13)
    c: Coincident(g13,g1)
    c: Coincident(g14,g15)
    c: Coincident(g15,g16)
    c: Coincident(g16,g17)
    c: Coincident(g17,g14)
    c: Horizontal(g15)
    c: Horizontal(g17)
    c: Vertical(g14)
    c: Vertical(g16)
    c: Symmetric(g15,g14,g18)
    c: Coincident(g18,g2)
    c: Coincident(g19,g20)
    c: Coincident(g20,g21)
    c: Coincident(g21,g22)
    c: Coincident(g22,g19)
    c: Horizontal(g20)
    c: Horizontal(g22)
    c: Vertical(g19)
    c: Vertical(g21)
    c: Symmetric(g20,g19,g23)
    c: Coincident(g23,g3)
    c: Equal(g5,g10)
    c: Equal(g5,g11)
    c: Equal(g5,g20)
    c: Equal(g5,g21)
    c: Equal(g5,g15)
    c: Equal(g5,g16)
    c: Coincident(g24,g5)
    c: Diameter(g24) = 3.5
    c: Coincident(g25,g4)
    c: Coincident(g26,g4)
    c: Coincident(g27,g6)
    c: Coincident(g28,g10)
    c: Coincident(g29,g9)
    c: Coincident(g30,g9)
    c: Coincident(g31,g11)
    c: Coincident(g32,g20)
    c: Coincident(g33,g19)
    c: Coincident(g34,g19)
    c: Coincident(g35,g21)
    c: Coincident(g36,g15)
    c: Coincident(g37,g14)
    c: Coincident(g38,g14)
    c: Coincident(g39,g16)
    c: Equal(g24,g25)
    c: Equal(g24,g27)
    c: Equal(g24,g26)
    c: Equal(g24,g28)
    c: Equal(g24,g36)
    c: Equal(g24,g32)
    c: Equal(g28,g29)
    c: Equal(g28,g31)
    c: Equal(g28,g30)
    c: Equal(g32,g33)
    c: Equal(g32,g35)
    c: Equal(g32,g34)
    c: Equal(g36,g37)
    c: Equal(g36,g39)
    c: Equal(g36,g38)
FEATURE [PartDesign::Pocket] Pocket002
  AddSubType = 1
  AutoTaperInnerAngle = true
  BaseFeature = -> Pad006
  CheckUpToFaceLimits = true
  ClaimChildren = false
  Fit = 0
  FitJoin = 0
  InnerFit = 0
  InnerFitJoin = 0
  InvalidShape = false
  Length = 100
  Length2 = 100
  Linearize = true
  NewSolid = false
  Profile = -> Sketch010
  Suppress = false
  TaperInnerAngle = 0
  TaperInnerAngleRev = 0
  TreeRank = 68
  Type = 4
  ValidateShape = true
  _ProfileBasedVersion = 1
  _Version = 1
FEATURE [Sketcher::SketchObject] Sketch011
  ArcFitTolerance = 1e-06
  ExternalBSplineMaxDegree = 5
  ExternalBSplineTolerance = 0.0001
  FullyConstrained = true
  InternalTolerance = 1e-06
  InvalidShape = false
  MakeInternals = false
  MapMode = 2
  Placement = pos=(0,0,-6.25) rot=(0,0,1;0rad)
  TreeRank = 69
  ValidateShape = true
  expr: Placement.Base.z = -(<<Parameters>>.thickness + <<Parameters>>.motor_screw_head_height)
  expr: Constraints[0] = <<Parameters>>.station_diameter
  expr: Constraints[19] = <<Parameters>>.motor_screw_spacing
  expr: Constraints[58] = <<Parameters>>.motor_screw_head_diameter
  expr: Constraints[7] = <<Parameters>>.station_diameter
  expr: Constraints[8] = <<Parameters>>.station_diameter
  sketch-geometry (40):
    g0: Circle [constr] CenterX=-42.5 CenterY=42.5 CenterZ=0 NormalX=0 NormalY=0 NormalZ=1 AngleXU=0 Radius=42.5
    g1: Circle [constr] CenterX=42.5 CenterY=42.5 CenterZ=0 NormalX=0 NormalY=0 NormalZ=1 AngleXU=0 Radius=42.5
    g2: Circle [constr] CenterX=-42.5 CenterY=-42.5 CenterZ=0 NormalX=0 NormalY=0 NormalZ=1 AngleXU=0 Radius=42.5
    g3: Circle [constr] CenterX=42.5 CenterY=-42.5 CenterZ=0 NormalX=0 NormalY=0 NormalZ=1 AngleXU=0 Radius=42.5
    g4: LineSegment [constr] StartX=-29.5 StartY=29.5 StartZ=0 EndX=-29.5 EndY=55.5 EndZ=0
    g5: LineSegment [constr] StartX=-29.5 StartY=55.5 StartZ=0 EndX=-55.5 EndY=55.5 EndZ=0
    g6: LineSegment [constr] StartX=-55.5 StartY=55.5 StartZ=0 EndX=-55.5 EndY=29.5 EndZ=0
    g7: LineSegment [constr] StartX=-55.5 StartY=29.5 StartZ=0 EndX=-29.5 EndY=29.5 EndZ=0
    g8: GeomPoint [constr] X=-42.5 Y=42.5 Z=0
    g9: LineSegment [constr] StartX=55.5 StartY=29.5 StartZ=0 EndX=55.5 EndY=55.5 EndZ=0
    g10: LineSegment [constr] StartX=55.5 StartY=55.5 StartZ=0 EndX=29.5 EndY=55.5 EndZ=0
    g11: LineSegment [constr] StartX=29.5 StartY=55.5 StartZ=0 EndX=29.5 EndY=29.5 EndZ=0
    g12: LineSegment [constr] StartX=29.5 StartY=29.5 StartZ=0 EndX=55.5 EndY=29.5 EndZ=0
    g13: GeomPoint [constr] X=42.5 Y=42.5 Z=0
    g14: LineSegment [constr] StartX=-29.5 StartY=-55.5 StartZ=0 EndX=-29.5 EndY=-29.5 EndZ=0
    g15: LineSegment [constr] StartX=-29.5 StartY=-29.5 StartZ=0 EndX=-55.5 EndY=-29.5 EndZ=0
    g16: LineSegment [constr] StartX=-55.5 StartY=-29.5 StartZ=0 EndX=-55.5 EndY=-55.5 EndZ=0
    g17: LineSegment [constr] StartX=-55.5 StartY=-55.5 StartZ=0 EndX=-29.5 EndY=-55.5 EndZ=0
    g18: GeomPoint [constr] X=-42.5 Y=-42.5 Z=0
    g19: LineSegment [constr] StartX=55.5 StartY=-55.5 StartZ=0 EndX=55.5 EndY=-29.5 EndZ=0
    g20: LineSegment [constr] StartX=55.5 StartY=-29.5 StartZ=0 EndX=29.5 EndY=-29.5 EndZ=0
    g21: LineSegment [constr] StartX=29.5 StartY=-29.5 StartZ=0 EndX=29.5 EndY=-55.5 EndZ=0
    g22: LineSegment [constr] StartX=29.5 StartY=-55.5 StartZ=0 EndX=55.5 EndY=-55.5 EndZ=0
    g23: GeomPoint [constr] X=42.5 Y=-42.5 Z=0
    g24: Circle CenterX=-55.5 CenterY=55.5 CenterZ=0 NormalX=0 NormalY=0 NormalZ=1 AngleXU=0 Radius=3
    g25: Circle CenterX=-29.5 CenterY=55.5 CenterZ=0 NormalX=0 NormalY=0 NormalZ=1 AngleXU=0 Radius=3
    g26: Circle CenterX=-29.5 CenterY=29.5 CenterZ=0 NormalX=0 NormalY=0 NormalZ=1 AngleXU=0 Radius=3
    g27: Circle CenterX=-55.5 CenterY=29.5 CenterZ=0 NormalX=0 NormalY=0 NormalZ=1 AngleXU=0 Radius=3
    g28: Circle CenterX=29.5 CenterY=55.5 CenterZ=0 NormalX=0 NormalY=0 NormalZ=1 AngleXU=0 Radius=3
    g29: Circle CenterX=55.5 CenterY=55.5 CenterZ=0 NormalX=0 NormalY=0 NormalZ=1 AngleXU=0 Radius=3
    g30: Circle CenterX=55.5 CenterY=29.5 CenterZ=0 NormalX=0 NormalY=0 NormalZ=1 AngleXU=0 Radius=3
    g31: Circle CenterX=29.5 CenterY=29.5 CenterZ=0 NormalX=0 NormalY=0 NormalZ=1 AngleXU=0 Radius=3
    g32: Circle CenterX=29.5 CenterY=-29.5 CenterZ=0 NormalX=0 NormalY=0 NormalZ=1 AngleXU=0 Radius=3
    g33: Circle CenterX=55.5 CenterY=-29.5 CenterZ=0 NormalX=0 NormalY=0 NormalZ=1 AngleXU=0 Radius=3
    g34: Circle CenterX=55.5 CenterY=-55.5 CenterZ=0 NormalX=0 NormalY=0 NormalZ=1 AngleXU=0 Radius=3
    g35: Circle CenterX=29.5 CenterY=-55.5 CenterZ=0 NormalX=0 NormalY=0 NormalZ=1 AngleXU=0 Radius=3
    g36: Circle CenterX=-55.5 CenterY=-29.5 CenterZ=0 NormalX=0 NormalY=0 NormalZ=1 AngleXU=0 Radius=3
    g37: Circle CenterX=-29.5 CenterY=-29.5 CenterZ=0 NormalX=0 NormalY=0 NormalZ=1 AngleXU=0 Radius=3
    g38: Circle CenterX=-29.5 CenterY=-55.5 CenterZ=0 NormalX=0 NormalY=0 NormalZ=1 AngleXU=0 Radius=3
    g39: Circle CenterX=-55.5 CenterY=-55.5 CenterZ=0 NormalX=0 NormalY=0 NormalZ=1 AngleXU=0 Radius=3
  constraints (89):
    c: Diameter(g0) = 85
    c: Equal(g0,g1)
    c: Equal(g0,g2)
    c: Equal(g0,g3)
    c: Symmetric(g0,g3,g-1)
    c: Symmetric(g1,g2,g-1)
    c: Symmetric(g0,g1,g-2)
    c: DistanceX(g0,g1) = 85
    c: DistanceY(g3,g1) = 85
    c: Coincident(g4,g5)
    c: Coincident(g5,g6)
    c: Coincident(g6,g7)
    c: Coincident(g7,g4)
    c: Horizontal(g5)
    c: Horizontal(g7)
    c: Vertical(g4)
    c: Vertical(g6)
    c: Symmetric(g5,g4,g8)
    c: Coincident(g8,g0)
    c: DistanceX(g5,g4) = 26
    c: Equal(g5,g6)
    c: Coincident(g9,g10)
    c: Coincident(g10,g11)
    c: Coincident(g11,g12)
    c: Coincident(g12,g9)
    c: Horizontal(g10)
    c: Horizontal(g12)
    c: Vertical(g9)
    c: Vertical(g11)
    c: Symmetric(g10,g9,g13)
    c: Coincident(g13,g1)
    c: Coincident(g14,g15)
    c: Coincident(g15,g16)
    c: Coincident(g16,g17)
    c: Coincident(g17,g14)
    c: Horizontal(g15)
    c: Horizontal(g17)
    c: Vertical(g14)
    c: Vertical(g16)
    c: Symmetric(g15,g14,g18)
    c: Coincident(g18,g2)
    c: Coincident(g19,g20)
    c: Coincident(g20,g21)
    c: Coincident(g21,g22)
    c: Coincident(g22,g19)
    c: Horizontal(g20)
    c: Horizontal(g22)
    c: Vertical(g19)
    c: Vertical(g21)
    c: Symmetric(g20,g19,g23)
    c: Coincident(g23,g3)
    c: Equal(g5,g10)
    c: Equal(g5,g11)
    c: Equal(g5,g20)
    c: Equal(g5,g21)
    c: Equal(g5,g15)
    c: Equal(g5,g16)
    c: Coincident(g24,g5)
    c: Diameter(g24) = 6
    c: Coincident(g25,g4)
    c: Coincident(g26,g4)
    c: Coincident(g27,g6)
    c: Coincident(g28,g10)
    c: Coincident(g29,g9)
    c: Coincident(g30,g9)
    c: Coincident(g31,g11)
    c: Coincident(g32,g20)
    c: Coincident(g33,g19)
    c: Coincident(g34,g19)
    c: Coincident(g35,g21)
    c: Coincident(g36,g15)
    c: Coincident(g37,g14)
    c: Coincident(g38,g14)
    c: Coincident(g39,g16)
    c: Equal(g24,g25)
    c: Equal(g24,g27)
    c: Equal(g24,g26)
    c: Equal(g24,g28)
    c: Equal(g24,g36)
    c: Equal(g24,g32)
    c: Equal(g28,g29)
    c: Equal(g28,g31)
    c: Equal(g28,g30)
    c: Equal(g32,g33)
    c: Equal(g32,g35)
    c: Equal(g32,g34)
    c: Equal(g36,g37)
    c: Equal(g36,g39)
    c: Equal(g36,g38)
FEATURE [PartDesign::Pocket] Pocket003
  AddSubType = 1
  AutoTaperInnerAngle = true
  BaseFeature = -> Pocket002
  CheckUpToFaceLimits = true
  ClaimChildren = false
  Fit = 0
  FitJoin = 0
  InnerFit = 0
  InnerFitJoin = 0
  InvalidShape = false
  Length = 3.25
  Length2 = 100
  Linearize = true
  NewSolid = false
  Profile = -> Sketch011
  Reversed = true
  Suppress = false
  TaperInnerAngle = 0
  TaperInnerAngleRev = 0
  TreeRank = 70
  Type = 0
  ValidateShape = true
  _ProfileBasedVersion = 1
  _Version = 1
  expr: Length = <<Parameters>>.motor_screw_head_height
FEATURE [PartDesign::Chamfer] Chamfer003
  AddSubType = 0
  Angle = 45
  Base = -> Pocket003 [Edge59,Edge41,Edge42,Edge44,Edge43]
  BaseFeature = -> Pocket003
  ChamferType = 0
  FlipDirection = false
  InvalidShape = false
  NewSolid = false
  Size = 3
  Size2 = 1
  SupportTransform = false
  Suppress = false
  TreeRank = 71
  ValidateShape = true
  expr: Size = <<Parameters>>.thickness
FEATURE [PartDesign::Fillet] Fillet003
  AddSubType = 0
  Base = -> Chamfer003 [Edge51]
  BaseFeature = -> Chamfer003
  InvalidShape = false
  NewSolid = false
  Radius = 1
  SupportTransform = false
  Suppress = false
  TreeRank = 72
  ValidateShape = true
FEATURE [Sketcher::SketchObject] Sketch012
  ArcFitTolerance = 1e-06
  ExternalBSplineMaxDegree = 5
  ExternalBSplineTolerance = 0.0001
  FullyConstrained = true
  InternalTolerance = 1e-06
  InvalidShape = false
  MakeInternals = false
  MapMode = 2
  TreeRank = 75
  ValidateShape = true
  expr: Constraints[14] = <<Parameters>>.thickness * 2
  expr: Constraints[16] = (<<Parameters>>.station_diameter + <<Parameters>>.thickness) * 2 - 4 * <<Parameters>>.thickness - <<Parameters>>.motor_shaft_mount_diameter / 2
  expr: Constraints[20] = <<Parameters>>.station_diameter + <<Parameters>>.thickness
  expr: Constraints[21] = <<Parameters>>.station_diameter + <<Parameters>>.thickness
  sketch-geometry (8):
    g0: LineSegment StartX=88 StartY=69.5 StartZ=0 EndX=82 EndY=69.5 EndZ=0
    g1: LineSegment StartX=82 StartY=69.5 StartZ=0 EndX=82 EndY=-69.5 EndZ=0
    g2: LineSegment StartX=82 StartY=-69.5 StartZ=0 EndX=88 EndY=-69.5 EndZ=0
    g3: LineSegment StartX=88 StartY=-69.5 StartZ=0 EndX=88 EndY=69.5 EndZ=0
    g4: LineSegment StartX=-69.5 StartY=-88 StartZ=0 EndX=69.5 EndY=-88 EndZ=0
    g5: LineSegment StartX=69.5 StartY=-88 StartZ=0 EndX=69.5 EndY=-82 EndZ=0
    g6: LineSegment StartX=69.5 StartY=-82 StartZ=0 EndX=-69.5 EndY=-82 EndZ=0
    g7: LineSegment StartX=-69.5 StartY=-82 StartZ=0 EndX=-69.5 EndY=-88 EndZ=0
  constraints (22):
    c: Coincident(g0,g1)
    c: Coincident(g1,g2)
    c: Coincident(g2,g3)
    c: Coincident(g3,g0)
    c: Horizontal(g0)
    c: Horizontal(g2)
    c: Vertical(g1)
    c: Coincident(g4,g5)
    c: Coincident(g5,g6)
    c: Coincident(g6,g7)
    c: Coincident(g7,g4)
    c: Horizontal(g6)
    c: Vertical(g5)
    c: Vertical(g7)
    c: DistanceX(g0,g0) = 6
    c: Equal(g0,g5)
    c: DistanceY(g2,g0) = 139
    c: Symmetric(g0,g2,g-1)
    c: Symmetric(g4,g4,g-2)
    c: Equal(g3,g4)
    c: DistanceX(g-1,g0) = 88
    c: DistanceY(g4,g-1) = 88
FEATURE [PartDesign::Pocket] Pocket004
  AddSubType = 1
  AutoTaperInnerAngle = true
  BaseFeature = -> Fillet003
  CheckUpToFaceLimits = true
  ClaimChildren = false
  Fit = 0
  FitJoin = 0
  InnerFit = 0
  InnerFitJoin = 0
  InvalidShape = false
  Length = 1
  Length2 = 100
  Linearize = true
  NewSolid = false
  Profile = -> Sketch012
  Suppress = false
  TaperInnerAngle = 0
  TaperInnerAngleRev = 0
  TreeRank = 76
  Type = 0
  ValidateShape = true
  _ProfileBasedVersion = 1
  _Version = 1
  expr: Length = <<Parameters>>.lap_join_thickness
FEATURE [Sketcher::SketchObject] Sketch013
  ArcFitTolerance = 1e-06
  AttachmentSupport = -> [XY_Plane003]
  ExternalBSplineMaxDegree = 5
  ExternalBSplineTolerance = 0.0001
  FullyConstrained = true
  InternalTolerance = 1e-06
  InvalidShape = false
  MakeInternals = false
  MapMode = 5
  Support = -> [XY_Plane003]
  TreeRank = 91
  ValidateShape = true
  expr: Constraints[10] = <<Parameters>>.station_diameter
  expr: Constraints[11] = <<Parameters>>.station_diameter
  expr: Constraints[13] = <<Parameters>>.motor_shaft_mount_diameter + 1
  expr: Constraints[24] = (<<Parameters>>.station_diameter + <<Parameters>>.thickness) * 2
  expr: Constraints[26] = <<Parameters>>.station_diameter + <<Parameters>>.thickness
  expr: Constraints[27] = <<Parameters>>.station_diameter + <<Parameters>>.thickness
  expr: Constraints[28] = <<Parameters>>.station_diameter + <<Parameters>>.thickness
  expr: Constraints[29] = <<Parameters>>.station_diameter / 3
  expr: Constraints[3] = <<Parameters>>.station_diameter
  sketch-geometry (14):
    g0: LineSegment StartX=73.8333 StartY=88 StartZ=0 EndX=-88 EndY=88 EndZ=0
    g1: LineSegment StartX=-88 StartY=88 StartZ=0 EndX=-88 EndY=-88 EndZ=0
    g2: GeomPoint [constr] X=0 Y=0 Z=0
    g3: Circle [constr] CenterX=-42.5 CenterY=42.5 CenterZ=0 NormalX=0 NormalY=0 NormalZ=1 AngleXU=0 Radius=42.5
    g4: Circle [constr] CenterX=42.5 CenterY=42.5 CenterZ=0 NormalX=0 NormalY=0 NormalZ=1 AngleXU=0 Radius=42.5
    g5: Circle [constr] CenterX=-42.5 CenterY=-42.5 CenterZ=0 NormalX=0 NormalY=0 NormalZ=1 AngleXU=0 Radius=42.5
    g6: Circle [constr] CenterX=42.5 CenterY=-42.5 CenterZ=0 NormalX=0 NormalY=0 NormalZ=1 AngleXU=0 Radius=42.5
    g7: Circle CenterX=-42.5 CenterY=42.5 CenterZ=0 NormalX=0 NormalY=0 NormalZ=1 AngleXU=0 Radius=25.5
    g8: Circle CenterX=42.5 CenterY=42.5 CenterZ=0 NormalX=0 NormalY=0 NormalZ=1 AngleXU=0 Radius=25.5
    g9: Circle CenterX=42.5 CenterY=-42.5 CenterZ=0 NormalX=0 NormalY=0 NormalZ=1 AngleXU=0 Radius=25.5
    g10: Circle CenterX=-42.5 CenterY=-42.5 CenterZ=0 NormalX=0 NormalY=0 NormalZ=1 AngleXU=0 Radius=25.5
    g11: LineSegment StartX=88 StartY=-88 StartZ=0 EndX=88 EndY=73.8333 EndZ=0
    g12: LineSegment StartX=-88 StartY=-88 StartZ=0 EndX=88 EndY=-88 EndZ=0
    g13: ArcOfCircle CenterX=73.8333 CenterY=73.8333 CenterZ=0 NormalX=0 NormalY=0 NormalZ=1 AngleXU=0 Radius=14.1667 StartAngle=0 EndAngle=1.5708
  constraints (32):
    c: Horizontal(g0)
    c: Vertical(g1)
    c: Coincident(g2,g-1)
    c: Diameter(g3) = 85
    c: Equal(g3,g4)
    c: Equal(g3,g5)
    c: Equal(g3,g6)
    c: Symmetric(g3,g6,g2)
    c: Symmetric(g5,g4,g2)
    c: Symmetric(g3,g5,g-1)
    c: DistanceX(g3,g4) = 85
    c: DistanceY(g5,g3) = 85
    c: Coincident(g7,g3)
    c: Diameter(g7) = 51
    c: Coincident(g8,g4)
    c: Coincident(g9,g6)
    c: Coincident(g10,g5)
    c: Equal(g7,g8)
    c: Equal(g7,g10)
    c: Equal(g7,g9)
    c: Vertical(g11)
    c: Horizontal(g12)
    c: Coincident(g12,g1)
    c: Coincident(g11,g12)
    c: DistanceX(g1,g11) = 176
    c: Coincident(g0,g1)
    c: DistanceY(g2,g0) = 88
    c: DistanceX(g2,g11) = 88
    c: DistanceY(g11,g2) = 88
    c: Diameter(g13) = 28.3333
    c: Tangent(g13,g11) = -1.5708
    c: Tangent(g13,g0) = -1.5708
FEATURE [PartDesign::Pad] Pad007
  AddSubType = 0
  AlongSketchNormal = false
  AutoTaperInnerAngle = true
  CheckUpToFaceLimits = true
  ClaimChildren = false
  Direction = (0,0,1)
  Fit = 0
  FitJoin = 0
  InnerFit = 0
  InnerFitJoin = 0
  InvalidShape = false
  Length = 3
  Length2 = 100
  Linearize = true
  NewSolid = false
  Profile = -> Sketch013
  Suppress = false
  TaperInnerAngle = 0
  TaperInnerAngleRev = 0
  TreeRank = 92
  Type = 0
  ValidateShape = true
  _ProfileBasedVersion = 1
  expr: Length = <<Parameters>>.thickness
FEATURE [Sketcher::SketchObject] Sketch014
  ArcFitTolerance = 1e-06
  BaseAttacherType = Attacher::AttachEngine3D
  BaseMapMode = 2
  BaseMapPathParameter = 0
  BaseMapReversed = true
  ExternalBSplineMaxDegree = 5
  ExternalBSplineTolerance = 0.0001
  FullyConstrained = true
  InternalTolerance = 1e-06
  InvalidShape = false
  MakeInternals = false
  MapMode = 2
  TreeRank = 93
  ValidateShape = true
  expr: Constraints[10] = <<Parameters>>.station_diameter + <<Parameters>>.thickness
  expr: Constraints[11] = <<Parameters>>.motor_shaft_mount_diameter / 4
  expr: Constraints[18] = <<Parameters>>.motor_shaft_mount_diameter / 4
  expr: Constraints[21] = <<Parameters>>.station_diameter + <<Parameters>>.thickness
  expr: Constraints[22] = <<Parameters>>.station_diameter + <<Parameters>>.thickness
  expr: Constraints[26] = <<Parameters>>.thickness
  expr: Constraints[29] = <<Parameters>>.motor_shaft_mount_diameter / 4
  expr: Constraints[35] = <<Parameters>>.motor_shaft_mount_diameter / 4
  expr: Constraints[36] = <<Parameters>>.motor_shaft_mount_diameter / 4
  expr: Constraints[43] = <<Parameters>>.station_diameter + <<Parameters>>.thickness
  expr: Constraints[44] = <<Parameters>>.station_diameter + <<Parameters>>.thickness
  expr: Constraints[5] = <<Parameters>>.station_diameter / 3
  expr: Constraints[8] = <<Parameters>>.thickness
  expr: Constraints[9] = <<Parameters>>.station_diameter + <<Parameters>>.thickness
  sketch-geometry (15):
    g0: ArcOfCircle CenterX=73.8333 CenterY=73.8333 CenterZ=0 NormalX=0 NormalY=0 NormalZ=1 AngleXU=0 Radius=14.1667 StartAngle=6.28318 EndAngle=7.85398
    g1: ArcOfCircle CenterX=70.8333 CenterY=70.8333 CenterZ=0 NormalX=0 NormalY=0 NormalZ=1 AngleXU=0 Radius=14.1667 StartAngle=0 EndAngle=1.5708
    g2: LineSegment [constr] StartX=0 StartY=0 StartZ=0 EndX=73.8333 EndY=73.8333 EndZ=0
    g3: LineSegment StartX=73.8333 StartY=88 StartZ=0 EndX=-88 EndY=88 EndZ=0
    g4: LineSegment StartX=-82.6615 StartY=85 StartZ=0 EndX=70.8333 EndY=85 EndZ=0
    g5: ArcOfCircle CenterX=-88 CenterY=81.75 CenterZ=0 NormalX=0 NormalY=0 NormalZ=1 AngleXU=0 Radius=6.25 StartAngle=4.71239 EndAngle=6.83004
    g6: ArcOfCircle CenterX=81.75 CenterY=-88 CenterZ=0 NormalX=0 NormalY=0 NormalZ=1 AngleXU=0 Radius=6.25 StartAngle=1.02395 EndAngle=3.14159
    g7: LineSegment StartX=-88 StartY=88 StartZ=0 EndX=-88 EndY=75.5 EndZ=0
    g8: LineSegment StartX=75.5 StartY=-88 StartZ=0 EndX=88 EndY=-88 EndZ=0
    g9: LineSegment StartX=88 StartY=-88 StartZ=0 EndX=88 EndY=73.8333 EndZ=0
    g10: LineSegment StartX=85 StartY=-82.6615 StartZ=0 EndX=85 EndY=70.8333 EndZ=0
    g11: Circle CenterX=0 CenterY=0 CenterZ=0 NormalX=0 NormalY=0 NormalZ=1 AngleXU=0 Radius=6.25
    g12: ArcOfCircle CenterX=-88 CenterY=-88 CenterZ=0 NormalX=0 NormalY=0 NormalZ=1 AngleXU=0 Radius=12.5 StartAngle=0 EndAngle=1.5708
    g13: LineSegment StartX=-88 StartY=-88 StartZ=0 EndX=-88 EndY=-75.5 EndZ=0
    g14: LineSegment StartX=-88 StartY=-88 StartZ=0 EndX=-75.5 EndY=-88 EndZ=0
  constraints (45):
    c: Equal(g1,g0)
    c: Coincident(g2,g-1)
    c: Coincident(g2,g0)
    c: PointOnObject(g1,g2)
    c: Angle(g-1,g2) = 0.785398
    c: Diameter(g0) = 28.3333
    c: Horizontal(g3)
    c: Horizontal(g4)
    c: DistanceY(g4,g3) = 3
    c: DistanceX(g3,g2) = 88
    c: DistanceY(g2,g3) = 88
    c: Diameter(g5) = 12.5
    c: Equal(g5,g6)
    c: Vertical(g7)
    c: PointOnObject(g5,g7)
    c: Coincident(g7,g3)
    c: Coincident(g5,g4)
    c: Coincident(g5,g7)
    c: DistanceY(g5,g3) = 12.5
    c: Horizontal(g8)
    c: PointOnObject(g6,g8)
    c: DistanceX(g2,g8) = 88
    c: DistanceY(g8,g2) = 88
    c: Coincident(g9,g8)
    c: Vertical(g9)
    c: Vertical(g10)
    c: DistanceX(g10,g8) = 3
    c: Coincident(g6,g8)
    c: Coincident(g6,g10)
    c: DistanceX(g6,g8) = 12.5
    c: Coincident(g0,g9)
    c: Coincident(g1,g4)
    c: Tangent(g0,g3) = -1.5708
    c: Tangent(g1,g10) = -1.5708
    c: Coincident(g11,g2)
    c: Diameter(g11) = 12.5
    c: Radius(g12) = 12.5
    c: Coincident(g13,g12)
    c: Vertical(g13)
    c: Coincident(g14,g12)
    c: Horizontal(g14)
    c: Coincident(g12,g13)
    c: Coincident(g12,g14)
    c: DistanceY(g12,g11) = 88
    c: DistanceX(g12,g11) = 88
FEATURE [PartDesign::Pad] Pad008
  AddSubType = 0
  AlongSketchNormal = false
  AutoTaperInnerAngle = true
  BaseFeature = -> Pad007
  CheckUpToFaceLimits = true
  ClaimChildren = false
  Direction = (0,0,1)
  Fit = 0
  FitJoin = 0
  InnerFit = 0
  InnerFitJoin = 0
  InvalidShape = false
  Length = 19
  Length2 = 100
  Linearize = true
  NewSolid = false
  Profile = -> Sketch014
  Reversed = true
  Suppress = false
  TaperInnerAngle = 0
  TaperInnerAngleRev = 0
  TreeRank = 94
  Type = 0
  ValidateShape = true
  _ProfileBasedVersion = 1
  expr: Length = <<Parameters>>.motor_shaft_length
FEATURE [Sketcher::SketchObject] Sketch015
  ArcFitTolerance = 1e-06
  BaseAttacherType = Attacher::AttachEngine3D
  BaseMapMode = 2
  BaseMapPathParameter = 0
  BaseMapReversed = true
  ExternalBSplineMaxDegree = 5
  ExternalBSplineTolerance = 0.0001
  FullyConstrained = true
  InternalTolerance = 1e-06
  InvalidShape = false
  MakeInternals = false
  MapMode = 2
  Placement = pos=(0,0,-13) rot=(0,0,1;0rad)
  TreeRank = 95
  ValidateShape = true
  expr: Placement.Base.z = -<<Parameters>>.motor_shaft_length + 2 * <<Parameters>>.thickness
  expr: Constraints[10] = <<Parameters>>.station_diameter
  expr: Constraints[11] = <<Parameters>>.station_diameter
  expr: Constraints[14] = <<Parameters>>.thickness
  expr: Constraints[22] = <<Parameters>>.station_diameter - 2 * <<Parameters>>.thickness
  expr: Constraints[5] = <<Parameters>>.station_diameter / 3
  expr: Constraints[8] = <<Parameters>>.thickness
  expr: Constraints[9] = <<Parameters>>.station_diameter - 2 * <<Parameters>>.thickness
  sketch-geometry (9):
    g0: ArcOfCircle CenterX=70.8333 CenterY=70.8333 CenterZ=0 NormalX=0 NormalY=0 NormalZ=1 AngleXU=0 Radius=14.1667 StartAngle=1.28227e-08 EndAngle=1.5708
    g1: ArcOfCircle CenterX=67.8333 CenterY=67.8333 CenterZ=0 NormalX=0 NormalY=0 NormalZ=1 AngleXU=0 Radius=14.1667 StartAngle=0 EndAngle=1.5708
    g2: LineSegment [constr] StartX=0 StartY=0 StartZ=0 EndX=70.8333 EndY=70.8333 EndZ=0
    g3: LineSegment StartX=70.8333 StartY=85 StartZ=0 EndX=-79 EndY=85 EndZ=0
    g4: LineSegment StartX=-79 StartY=82 StartZ=0 EndX=67.8333 EndY=82 EndZ=0
    g5: LineSegment StartX=85 StartY=-79 StartZ=0 EndX=85 EndY=70.8333 EndZ=0
    g6: LineSegment StartX=82 StartY=-79 StartZ=0 EndX=82 EndY=67.8333 EndZ=0
    g7: LineSegment StartX=82 StartY=-79 StartZ=0 EndX=85 EndY=-79 EndZ=0
    g8: LineSegment StartX=-79 StartY=85 StartZ=0 EndX=-79 EndY=82 EndZ=0
  constraints (26):
    c: Equal(g1,g0)
    c: Coincident(g2,g-1)
    c: Coincident(g2,g0)
    c: PointOnObject(g1,g2)
    c: Angle(g-1,g2) = 0.785398
    c: Diameter(g0) = 28.3333
    c: Horizontal(g3)
    c: Horizontal(g4)
    c: DistanceY(g4,g3) = 3
    c: DistanceX(g3,g2) = 79
    c: DistanceY(g2,g3) = 85
    c: DistanceX(g2,g5) = 85
    c: Vertical(g5)
    c: Vertical(g6)
    c: DistanceX(g6,g5) = 3
    c: Coincident(g0,g5)
    c: Coincident(g1,g4)
    c: Tangent(g0,g3) = -1.5708
    c: Tangent(g1,g6) = -1.5708
    c: Coincident(g7,g6)
    c: Coincident(g7,g5)
    c: Horizontal(g7)
    c: DistanceY(g5,g2) = 79
    c: Coincident(g8,g3)
    c: Coincident(g8,g4)
    c: Vertical(g8)
FEATURE [PartDesign::Pad] Pad009
  AddSubType = 0
  AlongSketchNormal = false
  AutoTaperInnerAngle = true
  BaseFeature = -> Pad008
  CheckUpToFaceLimits = true
  ClaimChildren = false
  Direction = (0,0,1)
  Fit = 0
  FitJoin = 0
  InnerFit = 0
  InnerFitJoin = 0
  InvalidShape = false
  Length = 12
  Length2 = 100
  Linearize = true
  NewSolid = false
  Profile = -> Sketch015
  Reversed = true
  Suppress = false
  TaperInnerAngle = 0
  TaperInnerAngleRev = 0
  TreeRank = 96
  Type = 0
  ValidateShape = true
  _ProfileBasedVersion = 1
  expr: Length = <<Parameters>>.thickness * 4
FEATURE [Sketcher::SketchObject] Sketch016
  ArcFitTolerance = 1e-06
  ExternalBSplineMaxDegree = 5
  ExternalBSplineTolerance = 0.0001
  FullyConstrained = true
  InternalTolerance = 1e-06
  InvalidShape = false
  MakeInternals = false
  MapMode = 2
  TreeRank = 97
  ValidateShape = true
  expr: Constraints[14] = <<Parameters>>.thickness * 2
  expr: Constraints[16] = (<<Parameters>>.station_diameter + <<Parameters>>.thickness) * 2 - 4 * <<Parameters>>.thickness - <<Parameters>>.motor_shaft_mount_diameter / 2
  expr: Constraints[20] = <<Parameters>>.station_diameter + <<Parameters>>.thickness
  expr: Constraints[21] = <<Parameters>>.station_diameter + <<Parameters>>.thickness
  sketch-geometry (8):
    g0: LineSegment StartX=-82 StartY=69.5 StartZ=0 EndX=-88 EndY=69.5 EndZ=0
    g1: LineSegment StartX=-88 StartY=69.5 StartZ=0 EndX=-88 EndY=-69.5 EndZ=0
    g2: LineSegment StartX=-88 StartY=-69.5 StartZ=0 EndX=-82 EndY=-69.5 EndZ=0
    g3: LineSegment StartX=-82 StartY=-69.5 StartZ=0 EndX=-82 EndY=69.5 EndZ=0
    g4: LineSegment StartX=-69.5 StartY=-88 StartZ=0 EndX=69.5 EndY=-88 EndZ=0
    g5: LineSegment StartX=69.5 StartY=-88 StartZ=0 EndX=69.5 EndY=-82 EndZ=0
    g6: LineSegment StartX=69.5 StartY=-82 StartZ=0 EndX=-69.5 EndY=-82 EndZ=0
    g7: LineSegment StartX=-69.5 StartY=-82 StartZ=0 EndX=-69.5 EndY=-88 EndZ=0
  constraints (22):
    c: Coincident(g0,g1)
    c: Coincident(g1,g2)
    c: Coincident(g2,g3)
    c: Coincident(g3,g0)
    c: Horizontal(g0)
    c: Horizontal(g2)
    c: Vertical(g1)
    c: Coincident(g4,g5)
    c: Coincident(g5,g6)
    c: Coincident(g6,g7)
    c: Coincident(g7,g4)
    c: Horizontal(g6)
    c: Vertical(g5)
    c: Vertical(g7)
    c: DistanceX(g0,g0) = 6
    c: Equal(g0,g5)
    c: DistanceY(g2,g0) = 139
    c: Symmetric(g0,g2,g-1)
    c: Symmetric(g4,g4,g-2)
    c: Equal(g3,g4)
    c: DistanceY(g4,g-1) = 88
    c: DistanceX(g0,g-1) = 88
FEATURE [PartDesign::Pocket] Pocket005
  AddSubType = 1
  AutoTaperInnerAngle = true
  BaseFeature = -> Pad009
  CheckUpToFaceLimits = true
  ClaimChildren = false
  Fit = 0
  FitJoin = 0
  InnerFit = 0
  InnerFitJoin = 0
  InvalidShape = false
  Length = 1
  Length2 = 100
  Linearize = true
  NewSolid = false
  Profile = -> Sketch016
  Reversed = true
  Suppress = false
  TaperInnerAngle = 0
  TaperInnerAngleRev = 0
  TreeRank = 98
  Type = 0
  ValidateShape = true
  _ProfileBasedVersion = 1
  _Version = 1
  expr: Length = <<Parameters>>.lap_join_thickness
FEATURE [PartDesign::Chamfer] Chamfer004
  AddSubType = 0
  Angle = 45
  Base = -> Pocket005 [Edge87]
  BaseFeature = -> Pocket005
  ChamferType = 0
  FlipDirection = false
  InvalidShape = false
  NewSolid = false
  Size = 2.99
  Size2 = 1
  SupportTransform = false
  Suppress = false
  TreeRank = 99
  ValidateShape = true
  expr: Size = <<Parameters>>.thickness - 0.01
FEATURE [PartDesign::Chamfer] Chamfer005
  AddSubType = 0
  Angle = 45
  Base = -> Chamfer [Edge102]
  BaseFeature = -> Chamfer
  ChamferType = 0
  FlipDirection = false
  InvalidShape = false
  NewSolid = false
  Size = 1.5
  Size2 = 1
  SupportTransform = false
  Suppress = false
  TreeRank = 100
  ValidateShape = true
  expr: Size = <<Parameters>>.thickness / 2
FEATURE [PartDesign::Chamfer] Chamfer006
  AddSubType = 0
  Angle = 45
  Base = -> Chamfer004 [Edge103]
  BaseFeature = -> Chamfer004
  ChamferType = 0
  FlipDirection = false
  InvalidShape = false
  NewSolid = false
  Size = 1.5
  Size2 = 1
  SupportTransform = false
  Suppress = false
  TreeRank = 101
  ValidateShape = true
  expr: Size = <<Parameters>>.thickness / 2
FEATURE [PartDesign::Fillet] Fillet004
  AddSubType = 0
  Base = -> Chamfer006 [Edge77,Edge63,Edge69,Edge61,Edge31]
  BaseFeature = -> Chamfer006
  InvalidShape = false
  NewSolid = false
  Radius = 3
  SupportTransform = false
  Suppress = false
  TreeRank = 102
  ValidateShape = true
  expr: Radius = <<Parameters>>.thickness
FEATURE [PartDesign::Fillet] Fillet005
  AddSubType = 0
  Base = -> Chamfer005 [Edge76,Edge67,Edge61,Edge69,Edge68]
  BaseFeature = -> Chamfer005
  InvalidShape = false
  NewSolid = false
  Radius = 3
  SupportTransform = false
  Suppress = false
  TreeRank = 103
  ValidateShape = true
  expr: Radius = <<Parameters>>.thickness
FEATURE [PartDesign::Fillet] Fillet006
  AddSubType = 0
  Base = -> Fillet005 [Face40,Face39,Face42,Face41,Edge147]
  BaseFeature = -> Fillet005
  InvalidShape = false
  NewSolid = false
  Radius = 1
  SupportTransform = false
  Suppress = false
  TreeRank = 104
  ValidateShape = true
FEATURE [PartDesign::Fillet] Fillet007
  AddSubType = 0
  Base = -> Fillet004 [Face42,Face41,Face39,Face40,Edge145]
  BaseFeature = -> Fillet004
  InvalidShape = false
  NewSolid = false
  Radius = 1
  SupportTransform = false
  Suppress = false
  TreeRank = 105
  ValidateShape = true
FEATURE [Sketcher::SketchObject] Sketch017
  ArcFitTolerance = 1e-06
  ExternalBSplineMaxDegree = 5
  ExternalBSplineTolerance = 0.0001
  FullyConstrained = true
  InternalTolerance = 1e-06
  InvalidShape = false
  MakeInternals = false
  MapMode = 2
  Placement = pos=(0,0,-19) rot=(0,0,1;0rad)
  TreeRank = 106
  ValidateShape = true
  expr: Placement.Base.z = -<<Parameters>>.motor_shaft_length
  expr: Constraints[1] = <<Parameters>>.insert_hole_diameter
  sketch-geometry (1):
    g0: Circle CenterX=0 CenterY=0 CenterZ=0 NormalX=0 NormalY=0 NormalZ=1 AngleXU=0 Radius=1.87
  constraints (2):
    c: Coincident(g0,g-1)
    c: Diameter(g0) = 3.74
FEATURE [PartDesign::Pocket] Pocket006
  AddSubType = 1
  AutoTaperInnerAngle = true
  BaseFeature = -> Fillet006
  CheckUpToFaceLimits = true
  ClaimChildren = false
  Fit = 0
  FitJoin = 0
  InnerFit = 0
  InnerFitJoin = 0
  InvalidShape = false
  Length = 19
  Length2 = 100
  Linearize = true
  NewSolid = false
  Profile = -> Sketch017
  Reversed = true
  Suppress = false
  TaperInnerAngle = 0
  TaperInnerAngleRev = 0
  TreeRank = 107
  Type = 0
  ValidateShape = true
  _ProfileBasedVersion = 1
  _Version = 1
  expr: Length = <<Parameters>>.motor_shaft_length
FEATURE [PartDesign::Body] Body001  label="Top-Back-Left"
  AutoGroupSolids = false
  ClaimAllChildren = false
  ExportMode = 0
  Group = -> [Sketch003,Pad001,Sketch004,Pad002,Sketch005,Pad003,Pocket001,Chamfer,Chamfer005,Fillet005,Fillet006,Sketch006,Sketch017,Pocket006]
  InvalidShape = false
  Origin = -> Origin001
  Placement = pos=(-88,88,19) rot=(0.57735,0.57735,0.57735;0rad)
  Tip = -> Pocket006
  TreeRank = 36
  ValidateShape = true
  _ExportChildren = -> [Pad001,Pad002,Pad003,Pocket001,Chamfer,Chamfer005,Fillet005,Fillet006,Pocket006]
  _GroupVersion = 1
  expr: Placement.Base.x = -(<<Parameters>>.station_diameter + <<Parameters>>.thickness)
  expr: Placement.Base.y = <<Parameters>>.station_diameter + <<Parameters>>.thickness
  expr: Placement.Base.z = <<Parameters>>.motor_shaft_length
FEATURE [Sketcher::SketchObject] Sketch018
  ArcFitTolerance = 1e-06
  ExternalBSplineMaxDegree = 5
  ExternalBSplineTolerance = 0.0001
  FullyConstrained = true
  InternalTolerance = 1e-06
  InvalidShape = false
  MakeInternals = false
  MapMode = 2
  Placement = pos=(0,0,-19) rot=(0,0,1;0rad)
  TreeRank = 106
  ValidateShape = true
  expr: Placement.Base.z = -<<Parameters>>.motor_shaft_length
  expr: Constraints[1] = <<Parameters>>.insert_hole_diameter
  sketch-geometry (1):
    g0: Circle CenterX=0 CenterY=0 CenterZ=0 NormalX=0 NormalY=0 NormalZ=1 AngleXU=0 Radius=1.87
  constraints (2):
    c: Coincident(g0,g-1)
    c: Diameter(g0) = 3.74
FEATURE [PartDesign::Pocket] Pocket007
  AddSubType = 1
  AutoTaperInnerAngle = true
  BaseFeature = -> Fillet007
  CheckUpToFaceLimits = true
  ClaimChildren = false
  Fit = 0
  FitJoin = 0
  InnerFit = 0
  InnerFitJoin = 0
  InvalidShape = false
  Length = 19
  Length2 = 100
  Linearize = true
  NewSolid = false
  Profile = -> Sketch018
  Reversed = true
  Suppress = false
  TaperInnerAngle = 0
  TaperInnerAngleRev = 0
  TreeRank = 107
  Type = 0
  ValidateShape = true
  _ProfileBasedVersion = 1
  _Version = 1
  expr: Length = <<Parameters>>.motor_shaft_length
FEATURE [Sketcher::SketchObject] Sketch019
  ArcFitTolerance = 1e-06
  ExternalBSplineMaxDegree = 5
  ExternalBSplineTolerance = 0.0001
  FullyConstrained = true
  InternalTolerance = 1e-06
  InvalidShape = false
  MakeInternals = false
  MapMode = 2
  TreeRank = 108
  ValidateShape = true
  expr: Constraints[1] = <<Parameters>>.screw_head_diameter
  sketch-geometry (1):
    g0: Circle CenterX=0 CenterY=0 CenterZ=0 NormalX=0 NormalY=0 NormalZ=1 AngleXU=0 Radius=3
  constraints (2):
    c: Coincident(g0,g-1)
    c: Diameter(g0) = 6
FEATURE [PartDesign::Pocket] Pocket008
  AddSubType = 1
  AutoTaperInnerAngle = true
  BaseFeature = -> Pocket004
  CheckUpToFaceLimits = true
  ClaimChildren = false
  Fit = 0
  FitJoin = 0
  InnerFit = 0
  InnerFitJoin = 0
  InvalidShape = false
  Length = 100
  Length2 = 24
  Linearize = true
  NewSolid = false
  Profile = -> Sketch019
  Suppress = false
  TaperInnerAngle = 0
  TaperInnerAngleRev = 0
  TreeRank = 109
  Type = 4
  ValidateShape = true
  _ProfileBasedVersion = 1
  _Version = 1
  expr: Length2 = <<Parameters>>.motor_height - 2 * <<Parameters>>.thickness
FEATURE [Sketcher::SketchObject] Sketch020
  ArcFitTolerance = 1e-06
  ExternalBSplineMaxDegree = 5
  ExternalBSplineTolerance = 0.0001
  FullyConstrained = true
  InternalTolerance = 1e-06
  InvalidShape = false
  MakeInternals = false
  MapMode = 2
  TreeRank = 110
  ValidateShape = true
  expr: Constraints[1] = <<Parameters>>.screw_shaft_diameter
  sketch-geometry (1):
    g0: Circle CenterX=0 CenterY=0 CenterZ=0 NormalX=0 NormalY=0 NormalZ=1 AngleXU=0 Radius=1.75
  constraints (2):
    c: Coincident(g0,g-1)
    c: Diameter(g0) = 3.5
FEATURE [PartDesign::Pocket] Pocket009
  AddSubType = 1
  AutoTaperInnerAngle = true
  BaseFeature = -> Pocket008
  CheckUpToFaceLimits = true
  ClaimChildren = false
  Fit = 0
  FitJoin = 0
  InnerFit = 0
  InnerFitJoin = 0
  InvalidShape = false
  Length = 100
  Length2 = 100
  Linearize = true
  NewSolid = false
  Profile = -> Sketch020
  Suppress = false
  TaperInnerAngle = 0
  TaperInnerAngleRev = 0
  TreeRank = 111
  Type = 4
  ValidateShape = true
  _ProfileBasedVersion = 1
  _Version = 1
FEATURE [PartDesign::Body] Body002  label="Bottom-Back-Left"
  AutoGroupSolids = false
  ClaimAllChildren = false
  ExportMode = 0
  FixShape = 1
  Group = -> [Sketch008,Pad005,Sketch009,Pad006,Sketch010,Pocket002,Sketch011,Pocket003,Chamfer003,Fillet003,Sketch012,Pocket004,Sketch019,Pocket008,Sketch020,Pocket009]
  InvalidShape = false
  Origin = -> Origin002
  Placement = pos=(-88,88,-30) rot=(0.57735,0.57735,0.57735;0rad)
  Tip = -> Pocket009
  TreeRank = 89
  ValidateShape = true
  _ExportChildren = -> [Pad005,Pad006,Pocket002,Pocket003,Chamfer003,Fillet003,Pocket004,Pocket008,Pocket009]
  _GroupVersion = 1
  expr: Placement.Base.x = -(<<Parameters>>.station_diameter + <<Parameters>>.thickness)
  expr: Placement.Base.y = <<Parameters>>.station_diameter + <<Parameters>>.thickness
  expr: Placement.Base.z = -<<Parameters>>.motor_height
FEATURE [Sketcher::SketchObject] Sketch021
  ArcFitTolerance = 1e-06
  AttachmentSupport = -> [XY_Plane004]
  ExternalBSplineMaxDegree = 5
  ExternalBSplineTolerance = 0.0001
  FullyConstrained = true
  InternalTolerance = 1e-06
  InvalidShape = false
  MakeInternals = false
  MapMode = 5
  Support = -> [XY_Plane004]
  TreeRank = 122
  ValidateShape = true
  expr: Constraints[10] = <<Parameters>>.station_diameter
  expr: Constraints[11] = <<Parameters>>.station_diameter
  expr: Constraints[16] = (<<Parameters>>.station_diameter + <<Parameters>>.thickness) * 2
  expr: Constraints[18] = <<Parameters>>.station_diameter + <<Parameters>>.thickness
  expr: Constraints[19] = <<Parameters>>.station_diameter + <<Parameters>>.thickness
  expr: Constraints[20] = <<Parameters>>.station_diameter + <<Parameters>>.thickness
  expr: Constraints[21] = <<Parameters>>.station_diameter / 3
  expr: Constraints[3] = <<Parameters>>.station_diameter
  sketch-geometry (10):
    g0: LineSegment StartX=73.8333 StartY=88 StartZ=0 EndX=-88 EndY=88 EndZ=0
    g1: LineSegment StartX=-88 StartY=88 StartZ=0 EndX=-88 EndY=-88 EndZ=0
    g2: GeomPoint [constr] X=0 Y=0 Z=0
    g3: Circle [constr] CenterX=-42.5 CenterY=42.5 CenterZ=0 NormalX=0 NormalY=0 NormalZ=1 AngleXU=0 Radius=42.5
    g4: Circle [constr] CenterX=42.5 CenterY=42.5 CenterZ=0 NormalX=0 NormalY=0 NormalZ=1 AngleXU=0 Radius=42.5
    g5: Circle [constr] CenterX=-42.5 CenterY=-42.5 CenterZ=0 NormalX=0 NormalY=0 NormalZ=1 AngleXU=0 Radius=42.5
    g6: Circle [constr] CenterX=42.5 CenterY=-42.5 CenterZ=0 NormalX=0 NormalY=0 NormalZ=1 AngleXU=0 Radius=42.5
    g7: LineSegment StartX=88 StartY=-88 StartZ=0 EndX=88 EndY=73.8333 EndZ=0
    g8: LineSegment StartX=-88 StartY=-88 StartZ=0 EndX=88 EndY=-88 EndZ=0
    g9: ArcOfCircle CenterX=73.8333 CenterY=73.8333 CenterZ=0 NormalX=0 NormalY=0 NormalZ=1 AngleXU=0 Radius=14.1667 StartAngle=0 EndAngle=1.5708
  constraints (24):
    c: Horizontal(g0)
    c: Vertical(g1)
    c: Coincident(g2,g-1)
    c: Diameter(g3) = 85
    c: Equal(g3,g4)
    c: Equal(g3,g5)
    c: Equal(g3,g6)
    c: Symmetric(g3,g6,g2)
    c: Symmetric(g5,g4,g2)
    c: Symmetric(g3,g5,g-1)
    c: DistanceX(g3,g4) = 85
    c: DistanceY(g5,g3) = 85
    c: Vertical(g7)
    c: Horizontal(g8)
    c: Coincident(g8,g1)
    c: Coincident(g7,g8)
    c: DistanceX(g1,g7) = 176
    c: Coincident(g0,g1)
    c: DistanceY(g2,g0) = 88
    c: DistanceX(g2,g7) = 88
    c: DistanceY(g7,g2) = 88
    c: Diameter(g9) = 28.3333
    c: Tangent(g9,g7) = -1.5708
    c: Tangent(g9,g0) = -1.5708
FEATURE [PartDesign::Pad] Pad010
  AddSubType = 0
  AlongSketchNormal = false
  AutoTaperInnerAngle = true
  CheckUpToFaceLimits = true
  ClaimChildren = false
  Direction = (0,0,1)
  Fit = 0
  FitJoin = 0
  InnerFit = 0
  InnerFitJoin = 0
  InvalidShape = false
  Length = 6.25
  Length2 = 100
  Linearize = true
  NewSolid = false
  Profile = -> Sketch021
  Reversed = true
  Suppress = false
  TaperInnerAngle = 0
  TaperInnerAngleRev = 0
  TreeRank = 123
  Type = 0
  ValidateShape = true
  _ProfileBasedVersion = 1
  expr: Length = <<Parameters>>.thickness + <<Parameters>>.motor_screw_head_height
FEATURE [Sketcher::SketchObject] Sketch022
  ArcFitTolerance = 1e-06
  BaseAttacherType = Attacher::AttachEngine3D
  BaseMapMode = 2
  BaseMapPathParameter = 0
  BaseMapReversed = true
  ExternalBSplineMaxDegree = 5
  ExternalBSplineTolerance = 0.0001
  FullyConstrained = true
  InternalTolerance = 1e-06
  InvalidShape = false
  MakeInternals = false
  MapMode = 2
  TreeRank = 124
  ValidateShape = true
  expr: Constraints[10] = <<Parameters>>.station_diameter + <<Parameters>>.thickness
  expr: Constraints[11] = <<Parameters>>.motor_shaft_mount_diameter / 4
  expr: Constraints[18] = <<Parameters>>.motor_shaft_mount_diameter / 4
  expr: Constraints[21] = <<Parameters>>.station_diameter + <<Parameters>>.thickness
  expr: Constraints[22] = <<Parameters>>.station_diameter + <<Parameters>>.thickness
  expr: Constraints[26] = <<Parameters>>.thickness
  expr: Constraints[29] = <<Parameters>>.motor_shaft_mount_diameter / 4
  expr: Constraints[35] = <<Parameters>>.motor_shaft_mount_diameter / 4
  expr: Constraints[36] = <<Parameters>>.motor_shaft_mount_diameter / 4
  expr: Constraints[43] = <<Parameters>>.station_diameter + <<Parameters>>.thickness
  expr: Constraints[44] = <<Parameters>>.station_diameter + <<Parameters>>.thickness
  expr: Constraints[5] = <<Parameters>>.station_diameter / 3
  expr: Constraints[8] = <<Parameters>>.thickness
  expr: Constraints[9] = <<Parameters>>.station_diameter + <<Parameters>>.thickness
  sketch-geometry (15):
    g0: ArcOfCircle CenterX=73.8333 CenterY=73.8333 CenterZ=0 NormalX=0 NormalY=0 NormalZ=1 AngleXU=0 Radius=14.1667 StartAngle=6.28318 EndAngle=7.85398
    g1: ArcOfCircle CenterX=70.8333 CenterY=70.8333 CenterZ=0 NormalX=0 NormalY=0 NormalZ=1 AngleXU=0 Radius=14.1667 StartAngle=0 EndAngle=1.5708
    g2: LineSegment [constr] StartX=0 StartY=0 StartZ=0 EndX=73.8333 EndY=73.8333 EndZ=0
    g3: LineSegment StartX=73.8333 StartY=88 StartZ=0 EndX=-88 EndY=88 EndZ=0
    g4: LineSegment StartX=-82.6615 StartY=85 StartZ=0 EndX=70.8333 EndY=85 EndZ=0
    g5: ArcOfCircle CenterX=-88 CenterY=81.75 CenterZ=0 NormalX=0 NormalY=0 NormalZ=1 AngleXU=0 Radius=6.25 StartAngle=4.71239 EndAngle=6.83004
    g6: ArcOfCircle CenterX=81.75 CenterY=-88 CenterZ=0 NormalX=0 NormalY=0 NormalZ=1 AngleXU=0 Radius=6.25 StartAngle=1.02395 EndAngle=3.14159
    g7: LineSegment StartX=-88 StartY=88 StartZ=0 EndX=-88 EndY=75.5 EndZ=0
    g8: LineSegment StartX=75.5 StartY=-88 StartZ=0 EndX=88 EndY=-88 EndZ=0
    g9: LineSegment StartX=88 StartY=-88 StartZ=0 EndX=88 EndY=73.8333 EndZ=0
    g10: LineSegment StartX=85 StartY=-82.6615 StartZ=0 EndX=85 EndY=70.8333 EndZ=0
    g11: Circle CenterX=0 CenterY=0 CenterZ=0 NormalX=0 NormalY=0 NormalZ=1 AngleXU=0 Radius=6.25
    g12: ArcOfCircle CenterX=-88 CenterY=-88 CenterZ=0 NormalX=0 NormalY=0 NormalZ=1 AngleXU=0 Radius=12.5 StartAngle=0 EndAngle=1.5708
    g13: LineSegment StartX=-88 StartY=-88 StartZ=0 EndX=-88 EndY=-75.5 EndZ=0
    g14: LineSegment StartX=-88 StartY=-88 StartZ=0 EndX=-75.5 EndY=-88 EndZ=0
  constraints (45):
    c: Equal(g1,g0)
    c: Coincident(g2,g-1)
    c: Coincident(g2,g0)
    c: PointOnObject(g1,g2)
    c: Angle(g-1,g2) = 0.785398
    c: Diameter(g0) = 28.3333
    c: Horizontal(g3)
    c: Horizontal(g4)
    c: DistanceY(g4,g3) = 3
    c: DistanceX(g3,g2) = 88
    c: DistanceY(g2,g3) = 88
    c: Diameter(g5) = 12.5
    c: Equal(g5,g6)
    c: Vertical(g7)
    c: PointOnObject(g5,g7)
    c: Coincident(g7,g3)
    c: Coincident(g5,g4)
    c: Coincident(g5,g7)
    c: DistanceY(g5,g3) = 12.5
    c: Horizontal(g8)
    c: PointOnObject(g6,g8)
    c: DistanceX(g2,g8) = 88
    c: DistanceY(g8,g2) = 88
    c: Coincident(g9,g8)
    c: Vertical(g9)
    c: Vertical(g10)
    c: DistanceX(g10,g8) = 3
    c: Coincident(g6,g8)
    c: Coincident(g6,g10)
    c: DistanceX(g6,g8) = 12.5
    c: Coincident(g0,g9)
    c: Coincident(g1,g4)
    c: Tangent(g0,g3) = -1.5708
    c: Tangent(g1,g10) = -1.5708
    c: Coincident(g11,g2)
    c: Diameter(g11) = 12.5
    c: Radius(g12) = 12.5
    c: Coincident(g13,g12)
    c: Vertical(g13)
    c: Coincident(g14,g12)
    c: Horizontal(g14)
    c: Coincident(g12,g13)
    c: Coincident(g12,g14)
    c: DistanceY(g12,g11) = 88
    c: DistanceX(g12,g11) = 88
FEATURE [PartDesign::Pad] Pad011
  AddSubType = 0
  AlongSketchNormal = false
  AutoTaperInnerAngle = true
  BaseFeature = -> Pad010
  CheckUpToFaceLimits = true
  ClaimChildren = false
  Direction = (0,0,1)
  Fit = 0
  FitJoin = 0
  InnerFit = 0
  InnerFitJoin = 0
  InvalidShape = false
  Length = 30
  Length2 = 100
  Linearize = true
  NewSolid = false
  Profile = -> Sketch022
  Suppress = false
  TaperInnerAngle = 0
  TaperInnerAngleRev = 0
  TreeRank = 125
  Type = 0
  ValidateShape = true
  _ProfileBasedVersion = 1
  expr: Length = <<Parameters>>.motor_height
FEATURE [Sketcher::SketchObject] Sketch023
  ArcFitTolerance = 1e-06
  ExternalBSplineMaxDegree = 5
  ExternalBSplineTolerance = 0.0001
  FullyConstrained = true
  InternalTolerance = 1e-06
  InvalidShape = false
  MakeInternals = false
  MapMode = 2
  TreeRank = 126
  ValidateShape = true
  expr: Constraints[0] = <<Parameters>>.station_diameter
  expr: Constraints[19] = <<Parameters>>.motor_screw_spacing
  expr: Constraints[58] = <<Parameters>>.motor_screw_shaft_diameter
  expr: Constraints[7] = <<Parameters>>.station_diameter
  expr: Constraints[8] = <<Parameters>>.station_diameter
  sketch-geometry (40):
    g0: Circle [constr] CenterX=-42.5 CenterY=42.5 CenterZ=0 NormalX=0 NormalY=0 NormalZ=1 AngleXU=0 Radius=42.5
    g1: Circle [constr] CenterX=42.5 CenterY=42.5 CenterZ=0 NormalX=0 NormalY=0 NormalZ=1 AngleXU=0 Radius=42.5
    g2: Circle [constr] CenterX=-42.5 CenterY=-42.5 CenterZ=0 NormalX=0 NormalY=0 NormalZ=1 AngleXU=0 Radius=42.5
    g3: Circle [constr] CenterX=42.5 CenterY=-42.5 CenterZ=0 NormalX=0 NormalY=0 NormalZ=1 AngleXU=0 Radius=42.5
    g4: LineSegment [constr] StartX=-29.5 StartY=29.5 StartZ=0 EndX=-29.5 EndY=55.5 EndZ=0
    g5: LineSegment [constr] StartX=-29.5 StartY=55.5 StartZ=0 EndX=-55.5 EndY=55.5 EndZ=0
    g6: LineSegment [constr] StartX=-55.5 StartY=55.5 StartZ=0 EndX=-55.5 EndY=29.5 EndZ=0
    g7: LineSegment [constr] StartX=-55.5 StartY=29.5 StartZ=0 EndX=-29.5 EndY=29.5 EndZ=0
    g8: GeomPoint [constr] X=-42.5 Y=42.5 Z=0
    g9: LineSegment [constr] StartX=55.5 StartY=29.5 StartZ=0 EndX=55.5 EndY=55.5 EndZ=0
    g10: LineSegment [constr] StartX=55.5 StartY=55.5 StartZ=0 EndX=29.5 EndY=55.5 EndZ=0
    g11: LineSegment [constr] StartX=29.5 StartY=55.5 StartZ=0 EndX=29.5 EndY=29.5 EndZ=0
    g12: LineSegment [constr] StartX=29.5 StartY=29.5 StartZ=0 EndX=55.5 EndY=29.5 EndZ=0
    g13: GeomPoint [constr] X=42.5 Y=42.5 Z=0
    g14: LineSegment [constr] StartX=-29.5 StartY=-55.5 StartZ=0 EndX=-29.5 EndY=-29.5 EndZ=0
    g15: LineSegment [constr] StartX=-29.5 StartY=-29.5 StartZ=0 EndX=-55.5 EndY=-29.5 EndZ=0
    g16: LineSegment [constr] StartX=-55.5 StartY=-29.5 StartZ=0 EndX=-55.5 EndY=-55.5 EndZ=0
    g17: LineSegment [constr] StartX=-55.5 StartY=-55.5 StartZ=0 EndX=-29.5 EndY=-55.5 EndZ=0
    g18: GeomPoint [constr] X=-42.5 Y=-42.5 Z=0
    g19: LineSegment [constr] StartX=55.5 StartY=-55.5 StartZ=0 EndX=55.5 EndY=-29.5 EndZ=0
    g20: LineSegment [constr] StartX=55.5 StartY=-29.5 StartZ=0 EndX=29.5 EndY=-29.5 EndZ=0
    g21: LineSegment [constr] StartX=29.5 StartY=-29.5 StartZ=0 EndX=29.5 EndY=-55.5 EndZ=0
    g22: LineSegment [constr] StartX=29.5 StartY=-55.5 StartZ=0 EndX=55.5 EndY=-55.5 EndZ=0
    g23: GeomPoint [constr] X=42.5 Y=-42.5 Z=0
    g24: Circle CenterX=-55.5 CenterY=55.5 CenterZ=0 NormalX=0 NormalY=0 NormalZ=1 AngleXU=0 Radius=1.75
    g25: Circle CenterX=-29.5 CenterY=55.5 CenterZ=0 NormalX=0 NormalY=0 NormalZ=1 AngleXU=0 Radius=1.75
    g26: Circle CenterX=-29.5 CenterY=29.5 CenterZ=0 NormalX=0 NormalY=0 NormalZ=1 AngleXU=0 Radius=1.75
    g27: Circle CenterX=-55.5 CenterY=29.5 CenterZ=0 NormalX=0 NormalY=0 NormalZ=1 AngleXU=0 Radius=1.75
    g28: Circle CenterX=29.5 CenterY=55.5 CenterZ=0 NormalX=0 NormalY=0 NormalZ=1 AngleXU=0 Radius=1.75
    g29: Circle CenterX=55.5 CenterY=55.5 CenterZ=0 NormalX=0 NormalY=0 NormalZ=1 AngleXU=0 Radius=1.75
    g30: Circle CenterX=55.5 CenterY=29.5 CenterZ=0 NormalX=0 NormalY=0 NormalZ=1 AngleXU=0 Radius=1.75
    g31: Circle CenterX=29.5 CenterY=29.5 CenterZ=0 NormalX=0 NormalY=0 NormalZ=1 AngleXU=0 Radius=1.75
    g32: Circle CenterX=29.5 CenterY=-29.5 CenterZ=0 NormalX=0 NormalY=0 NormalZ=1 AngleXU=0 Radius=1.75
    g33: Circle CenterX=55.5 CenterY=-29.5 CenterZ=0 NormalX=0 NormalY=0 NormalZ=1 AngleXU=0 Radius=1.75
    g34: Circle CenterX=55.5 CenterY=-55.5 CenterZ=0 NormalX=0 NormalY=0 NormalZ=1 AngleXU=0 Radius=1.75
    g35: Circle CenterX=29.5 CenterY=-55.5 CenterZ=0 NormalX=0 NormalY=0 NormalZ=1 AngleXU=0 Radius=1.75
    g36: Circle CenterX=-55.5 CenterY=-29.5 CenterZ=0 NormalX=0 NormalY=0 NormalZ=1 AngleXU=0 Radius=1.75
    g37: Circle CenterX=-29.5 CenterY=-29.5 CenterZ=0 NormalX=0 NormalY=0 NormalZ=1 AngleXU=0 Radius=1.75
    g38: Circle CenterX=-29.5 CenterY=-55.5 CenterZ=0 NormalX=0 NormalY=0 NormalZ=1 AngleXU=0 Radius=1.75
    g39: Circle CenterX=-55.5 CenterY=-55.5 CenterZ=0 NormalX=0 NormalY=0 NormalZ=1 AngleXU=0 Radius=1.75
  constraints (89):
    c: Diameter(g0) = 85
    c: Equal(g0,g1)
    c: Equal(g0,g2)
    c: Equal(g0,g3)
    c: Symmetric(g0,g3,g-1)
    c: Symmetric(g1,g2,g-1)
    c: Symmetric(g0,g1,g-2)
    c: DistanceX(g0,g1) = 85
    c: DistanceY(g3,g1) = 85
    c: Coincident(g4,g5)
    c: Coincident(g5,g6)
    c: Coincident(g6,g7)
    c: Coincident(g7,g4)
    c: Horizontal(g5)
    c: Horizontal(g7)
    c: Vertical(g4)
    c: Vertical(g6)
    c: Symmetric(g5,g4,g8)
    c: Coincident(g8,g0)
    c: DistanceX(g5,g4) = 26
    c: Equal(g5,g6)
    c: Coincident(g9,g10)
    c: Coincident(g10,g11)
    c: Coincident(g11,g12)
    c: Coincident(g12,g9)
    c: Horizontal(g10)
    c: Horizontal(g12)
    c: Vertical(g9)
    c: Vertical(g11)
    c: Symmetric(g10,g9,g13)
    c: Coincident(g13,g1)
    c: Coincident(g14,g15)
    c: Coincident(g15,g16)
    c: Coincident(g16,g17)
    c: Coincident(g17,g14)
    c: Horizontal(g15)
    c: Horizontal(g17)
    c: Vertical(g14)
    c: Vertical(g16)
    c: Symmetric(g15,g14,g18)
    c: Coincident(g18,g2)
    c: Coincident(g19,g20)
    c: Coincident(g20,g21)
    c: Coincident(g21,g22)
    c: Coincident(g22,g19)
    c: Horizontal(g20)
    c: Horizontal(g22)
    c: Vertical(g19)
    c: Vertical(g21)
    c: Symmetric(g20,g19,g23)
    c: Coincident(g23,g3)
    c: Equal(g5,g10)
    c: Equal(g5,g11)
    c: Equal(g5,g20)
    c: Equal(g5,g21)
    c: Equal(g5,g15)
    c: Equal(g5,g16)
    c: Coincident(g24,g5)
    c: Diameter(g24) = 3.5
    c: Coincident(g25,g4)
    c: Coincident(g26,g4)
    c: Coincident(g27,g6)
    c: Coincident(g28,g10)
    c: Coincident(g29,g9)
    c: Coincident(g30,g9)
    c: Coincident(g31,g11)
    c: Coincident(g32,g20)
    c: Coincident(g33,g19)
    c: Coincident(g34,g19)
    c: Coincident(g35,g21)
    c: Coincident(g36,g15)
    c: Coincident(g37,g14)
    c: Coincident(g38,g14)
    c: Coincident(g39,g16)
    c: Equal(g24,g25)
    c: Equal(g24,g27)
    c: Equal(g24,g26)
    c: Equal(g24,g28)
    c: Equal(g24,g36)
    c: Equal(g24,g32)
    c: Equal(g28,g29)
    c: Equal(g28,g31)
    c: Equal(g28,g30)
    c: Equal(g32,g33)
    c: Equal(g32,g35)
    c: Equal(g32,g34)
    c: Equal(g36,g37)
    c: Equal(g36,g39)
    c: Equal(g36,g38)
FEATURE [PartDesign::Pocket] Pocket010
  AddSubType = 1
  AutoTaperInnerAngle = true
  BaseFeature = -> Pad011
  CheckUpToFaceLimits = true
  ClaimChildren = false
  Fit = 0
  FitJoin = 0
  InnerFit = 0
  InnerFitJoin = 0
  InvalidShape = false
  Length = 100
  Length2 = 100
  Linearize = true
  NewSolid = false
  Profile = -> Sketch023
  Suppress = false
  TaperInnerAngle = 0
  TaperInnerAngleRev = 0
  TreeRank = 127
  Type = 4
  ValidateShape = true
  _ProfileBasedVersion = 1
  _Version = 1
FEATURE [Sketcher::SketchObject] Sketch024
  ArcFitTolerance = 1e-06
  ExternalBSplineMaxDegree = 5
  ExternalBSplineTolerance = 0.0001
  FullyConstrained = true
  InternalTolerance = 1e-06
  InvalidShape = false
  MakeInternals = false
  MapMode = 2
  Placement = pos=(0,0,-6.25) rot=(0,0,1;0rad)
  TreeRank = 128
  ValidateShape = true
  expr: Placement.Base.z = -(<<Parameters>>.thickness + <<Parameters>>.motor_screw_head_height)
  expr: Constraints[0] = <<Parameters>>.station_diameter
  expr: Constraints[19] = <<Parameters>>.motor_screw_spacing
  expr: Constraints[58] = <<Parameters>>.motor_screw_head_diameter
  expr: Constraints[7] = <<Parameters>>.station_diameter
  expr: Constraints[8] = <<Parameters>>.station_diameter
  sketch-geometry (40):
    g0: Circle [constr] CenterX=-42.5 CenterY=42.5 CenterZ=0 NormalX=0 NormalY=0 NormalZ=1 AngleXU=0 Radius=42.5
    g1: Circle [constr] CenterX=42.5 CenterY=42.5 CenterZ=0 NormalX=0 NormalY=0 NormalZ=1 AngleXU=0 Radius=42.5
    g2: Circle [constr] CenterX=-42.5 CenterY=-42.5 CenterZ=0 NormalX=0 NormalY=0 NormalZ=1 AngleXU=0 Radius=42.5
    g3: Circle [constr] CenterX=42.5 CenterY=-42.5 CenterZ=0 NormalX=0 NormalY=0 NormalZ=1 AngleXU=0 Radius=42.5
    g4: LineSegment [constr] StartX=-29.5 StartY=29.5 StartZ=0 EndX=-29.5 EndY=55.5 EndZ=0
    g5: LineSegment [constr] StartX=-29.5 StartY=55.5 StartZ=0 EndX=-55.5 EndY=55.5 EndZ=0
    g6: LineSegment [constr] StartX=-55.5 StartY=55.5 StartZ=0 EndX=-55.5 EndY=29.5 EndZ=0
    g7: LineSegment [constr] StartX=-55.5 StartY=29.5 StartZ=0 EndX=-29.5 EndY=29.5 EndZ=0
    g8: GeomPoint [constr] X=-42.5 Y=42.5 Z=0
    g9: LineSegment [constr] StartX=55.5 StartY=29.5 StartZ=0 EndX=55.5 EndY=55.5 EndZ=0
    g10: LineSegment [constr] StartX=55.5 StartY=55.5 StartZ=0 EndX=29.5 EndY=55.5 EndZ=0
    g11: LineSegment [constr] StartX=29.5 StartY=55.5 StartZ=0 EndX=29.5 EndY=29.5 EndZ=0
    g12: LineSegment [constr] StartX=29.5 StartY=29.5 StartZ=0 EndX=55.5 EndY=29.5 EndZ=0
    g13: GeomPoint [constr] X=42.5 Y=42.5 Z=0
    g14: LineSegment [constr] StartX=-29.5 StartY=-55.5 StartZ=0 EndX=-29.5 EndY=-29.5 EndZ=0
    g15: LineSegment [constr] StartX=-29.5 StartY=-29.5 StartZ=0 EndX=-55.5 EndY=-29.5 EndZ=0
    g16: LineSegment [constr] StartX=-55.5 StartY=-29.5 StartZ=0 EndX=-55.5 EndY=-55.5 EndZ=0
    g17: LineSegment [constr] StartX=-55.5 StartY=-55.5 StartZ=0 EndX=-29.5 EndY=-55.5 EndZ=0
    g18: GeomPoint [constr] X=-42.5 Y=-42.5 Z=0
    g19: LineSegment [constr] StartX=55.5 StartY=-55.5 StartZ=0 EndX=55.5 EndY=-29.5 EndZ=0
    g20: LineSegment [constr] StartX=55.5 StartY=-29.5 StartZ=0 EndX=29.5 EndY=-29.5 EndZ=0
    g21: LineSegment [constr] StartX=29.5 StartY=-29.5 StartZ=0 EndX=29.5 EndY=-55.5 EndZ=0
    g22: LineSegment [constr] StartX=29.5 StartY=-55.5 StartZ=0 EndX=55.5 EndY=-55.5 EndZ=0
    g23: GeomPoint [constr] X=42.5 Y=-42.5 Z=0
    g24: Circle CenterX=-55.5 CenterY=55.5 CenterZ=0 NormalX=0 NormalY=0 NormalZ=1 AngleXU=0 Radius=3
    g25: Circle CenterX=-29.5 CenterY=55.5 CenterZ=0 NormalX=0 NormalY=0 NormalZ=1 AngleXU=0 Radius=3
    g26: Circle CenterX=-29.5 CenterY=29.5 CenterZ=0 NormalX=0 NormalY=0 NormalZ=1 AngleXU=0 Radius=3
    g27: Circle CenterX=-55.5 CenterY=29.5 CenterZ=0 NormalX=0 NormalY=0 NormalZ=1 AngleXU=0 Radius=3
    g28: Circle CenterX=29.5 CenterY=55.5 CenterZ=0 NormalX=0 NormalY=0 NormalZ=1 AngleXU=0 Radius=3
    g29: Circle CenterX=55.5 CenterY=55.5 CenterZ=0 NormalX=0 NormalY=0 NormalZ=1 AngleXU=0 Radius=3
    g30: Circle CenterX=55.5 CenterY=29.5 CenterZ=0 NormalX=0 NormalY=0 NormalZ=1 AngleXU=0 Radius=3
    g31: Circle CenterX=29.5 CenterY=29.5 CenterZ=0 NormalX=0 NormalY=0 NormalZ=1 AngleXU=0 Radius=3
    g32: Circle CenterX=29.5 CenterY=-29.5 CenterZ=0 NormalX=0 NormalY=0 NormalZ=1 AngleXU=0 Radius=3
    g33: Circle CenterX=55.5 CenterY=-29.5 CenterZ=0 NormalX=0 NormalY=0 NormalZ=1 AngleXU=0 Radius=3
    g34: Circle CenterX=55.5 CenterY=-55.5 CenterZ=0 NormalX=0 NormalY=0 NormalZ=1 AngleXU=0 Radius=3
    g35: Circle CenterX=29.5 CenterY=-55.5 CenterZ=0 NormalX=0 NormalY=0 NormalZ=1 AngleXU=0 Radius=3
    g36: Circle CenterX=-55.5 CenterY=-29.5 CenterZ=0 NormalX=0 NormalY=0 NormalZ=1 AngleXU=0 Radius=3
    g37: Circle CenterX=-29.5 CenterY=-29.5 CenterZ=0 NormalX=0 NormalY=0 NormalZ=1 AngleXU=0 Radius=3
    g38: Circle CenterX=-29.5 CenterY=-55.5 CenterZ=0 NormalX=0 NormalY=0 NormalZ=1 AngleXU=0 Radius=3
    g39: Circle CenterX=-55.5 CenterY=-55.5 CenterZ=0 NormalX=0 NormalY=0 NormalZ=1 AngleXU=0 Radius=3
  constraints (89):
    c: Diameter(g0) = 85
    c: Equal(g0,g1)
    c: Equal(g0,g2)
    c: Equal(g0,g3)
    c: Symmetric(g0,g3,g-1)
    c: Symmetric(g1,g2,g-1)
    c: Symmetric(g0,g1,g-2)
    c: DistanceX(g0,g1) = 85
    c: DistanceY(g3,g1) = 85
    c: Coincident(g4,g5)
    c: Coincident(g5,g6)
    c: Coincident(g6,g7)
    c: Coincident(g7,g4)
    c: Horizontal(g5)
    c: Horizontal(g7)
    c: Vertical(g4)
    c: Vertical(g6)
    c: Symmetric(g5,g4,g8)
    c: Coincident(g8,g0)
    c: DistanceX(g5,g4) = 26
    c: Equal(g5,g6)
    c: Coincident(g9,g10)
    c: Coincident(g10,g11)
    c: Coincident(g11,g12)
    c: Coincident(g12,g9)
    c: Horizontal(g10)
    c: Horizontal(g12)
    c: Vertical(g9)
    c: Vertical(g11)
    c: Symmetric(g10,g9,g13)
    c: Coincident(g13,g1)
    c: Coincident(g14,g15)
    c: Coincident(g15,g16)
    c: Coincident(g16,g17)
    c: Coincident(g17,g14)
    c: Horizontal(g15)
    c: Horizontal(g17)
    c: Vertical(g14)
    c: Vertical(g16)
    c: Symmetric(g15,g14,g18)
    c: Coincident(g18,g2)
    c: Coincident(g19,g20)
    c: Coincident(g20,g21)
    c: Coincident(g21,g22)
    c: Coincident(g22,g19)
    c: Horizontal(g20)
    c: Horizontal(g22)
    c: Vertical(g19)
    c: Vertical(g21)
    c: Symmetric(g20,g19,g23)
    c: Coincident(g23,g3)
    c: Equal(g5,g10)
    c: Equal(g5,g11)
    c: Equal(g5,g20)
    c: Equal(g5,g21)
    c: Equal(g5,g15)
    c: Equal(g5,g16)
    c: Coincident(g24,g5)
    c: Diameter(g24) = 6
    c: Coincident(g25,g4)
    c: Coincident(g26,g4)
    c: Coincident(g27,g6)
    c: Coincident(g28,g10)
    c: Coincident(g29,g9)
    c: Coincident(g30,g9)
    c: Coincident(g31,g11)
    c: Coincident(g32,g20)
    c: Coincident(g33,g19)
    c: Coincident(g34,g19)
    c: Coincident(g35,g21)
    c: Coincident(g36,g15)
    c: Coincident(g37,g14)
    c: Coincident(g38,g14)
    c: Coincident(g39,g16)
    c: Equal(g24,g25)
    c: Equal(g24,g27)
    c: Equal(g24,g26)
    c: Equal(g24,g28)
    c: Equal(g24,g36)
    c: Equal(g24,g32)
    c: Equal(g28,g29)
    c: Equal(g28,g31)
    c: Equal(g28,g30)
    c: Equal(g32,g33)
    c: Equal(g32,g35)
    c: Equal(g32,g34)
    c: Equal(g36,g37)
    c: Equal(g36,g39)
    c: Equal(g36,g38)
FEATURE [PartDesign::Pocket] Pocket011
  AddSubType = 1
  AutoTaperInnerAngle = true
  BaseFeature = -> Pocket010
  CheckUpToFaceLimits = true
  ClaimChildren = false
  Fit = 0
  FitJoin = 0
  InnerFit = 0
  InnerFitJoin = 0
  InvalidShape = false
  Length = 3.25
  Length2 = 100
  Linearize = true
  NewSolid = false
  Profile = -> Sketch024
  Reversed = true
  Suppress = false
  TaperInnerAngle = 0
  TaperInnerAngleRev = 0
  TreeRank = 129
  Type = 0
  ValidateShape = true
  _ProfileBasedVersion = 1
  _Version = 1
  expr: Length = <<Parameters>>.motor_screw_head_height
FEATURE [PartDesign::Fillet] Fillet008
  AddSubType = 0
  Base = -> Pocket011 [Edge62,Edge44,Edge49,Edge46,Edge45]
  BaseFeature = -> Pocket011
  InvalidShape = false
  NewSolid = false
  Radius = 3
  SupportTransform = false
  Suppress = false
  TreeRank = 130
  ValidateShape = true
  expr: Radius = <<Parameters>>.thickness
FEATURE [PartDesign::Fillet] Fillet009
  AddSubType = 0
  Base = -> Fillet008 [Edge43]
  BaseFeature = -> Fillet008
  InvalidShape = false
  NewSolid = false
  Radius = 1
  SupportTransform = false
  Suppress = false
  TreeRank = 131
  ValidateShape = true
FEATURE [Sketcher::SketchObject] Sketch025
  ArcFitTolerance = 1e-06
  ExternalBSplineMaxDegree = 5
  ExternalBSplineTolerance = 0.0001
  FullyConstrained = true
  InternalTolerance = 1e-06
  InvalidShape = false
  MakeInternals = false
  MapMode = 2
  TreeRank = 75
  ValidateShape = true
  expr: Constraints[14] = <<Parameters>>.thickness * 2
  expr: Constraints[16] = (<<Parameters>>.station_diameter + <<Parameters>>.thickness) * 2 - 4 * <<Parameters>>.thickness - <<Parameters>>.motor_shaft_mount_diameter / 2
  expr: Constraints[20] = <<Parameters>>.station_diameter + <<Parameters>>.thickness
  expr: Constraints[21] = <<Parameters>>.station_diameter + <<Parameters>>.thickness
  sketch-geometry (8):
    g0: LineSegment StartX=-82 StartY=69.5 StartZ=0 EndX=-88 EndY=69.5 EndZ=0
    g1: LineSegment StartX=-88 StartY=69.5 StartZ=0 EndX=-88 EndY=-69.5 EndZ=0
    g2: LineSegment StartX=-88 StartY=-69.5 StartZ=0 EndX=-82 EndY=-69.5 EndZ=0
    g3: LineSegment StartX=-82 StartY=-69.5 StartZ=0 EndX=-82 EndY=69.5 EndZ=0
    g4: LineSegment StartX=-69.5 StartY=-88 StartZ=0 EndX=69.5 EndY=-88 EndZ=0
    g5: LineSegment StartX=69.5 StartY=-88 StartZ=0 EndX=69.5 EndY=-82 EndZ=0
    g6: LineSegment StartX=69.5 StartY=-82 StartZ=0 EndX=-69.5 EndY=-82 EndZ=0
    g7: LineSegment StartX=-69.5 StartY=-82 StartZ=0 EndX=-69.5 EndY=-88 EndZ=0
  constraints (22):
    c: Coincident(g0,g1)
    c: Coincident(g1,g2)
    c: Coincident(g2,g3)
    c: Coincident(g3,g0)
    c: Horizontal(g0)
    c: Horizontal(g2)
    c: Vertical(g1)
    c: Coincident(g4,g5)
    c: Coincident(g5,g6)
    c: Coincident(g6,g7)
    c: Coincident(g7,g4)
    c: Horizontal(g6)
    c: Vertical(g5)
    c: Vertical(g7)
    c: DistanceX(g0,g0) = 6
    c: Equal(g0,g5)
    c: DistanceY(g2,g0) = 139
    c: Symmetric(g0,g2,g-1)
    c: Symmetric(g4,g4,g-2)
    c: Equal(g3,g4)
    c: DistanceY(g4,g-1) = 88
    c: DistanceX(g0,g-1) = 88
FEATURE [PartDesign::Pocket] Pocket012
  AddSubType = 1
  AutoTaperInnerAngle = true
  BaseFeature = -> Fillet009
  CheckUpToFaceLimits = true
  ClaimChildren = false
  Fit = 0
  FitJoin = 0
  InnerFit = 0
  InnerFitJoin = 0
  InvalidShape = false
  Length = 1
  Length2 = 100
  Linearize = true
  NewSolid = false
  Profile = -> Sketch025
  Suppress = false
  TaperInnerAngle = 0
  TaperInnerAngleRev = 0
  TreeRank = 132
  Type = 0
  ValidateShape = true
  _ProfileBasedVersion = 1
  _Version = 1
  expr: Length = <<Parameters>>.lap_join_thickness
FEATURE [Sketcher::SketchObject] Sketch026
  ArcFitTolerance = 1e-06
  ExternalBSplineMaxDegree = 5
  ExternalBSplineTolerance = 0.0001
  FullyConstrained = true
  InternalTolerance = 1e-06
  InvalidShape = false
  MakeInternals = false
  MapMode = 2
  TreeRank = 108
  ValidateShape = true
  expr: Constraints[1] = <<Parameters>>.screw_head_diameter
  sketch-geometry (1):
    g0: Circle CenterX=0 CenterY=0 CenterZ=0 NormalX=0 NormalY=0 NormalZ=1 AngleXU=0 Radius=3
  constraints (2):
    c: Coincident(g0,g-1)
    c: Diameter(g0) = 6
FEATURE [PartDesign::Pocket] Pocket013
  AddSubType = 1
  AutoTaperInnerAngle = true
  BaseFeature = -> Pocket012
  CheckUpToFaceLimits = true
  ClaimChildren = false
  Fit = 0
  FitJoin = 0
  InnerFit = 0
  InnerFitJoin = 0
  InvalidShape = false
  Length = 100
  Length2 = 24
  Linearize = true
  NewSolid = false
  Profile = -> Sketch026
  Suppress = false
  TaperInnerAngle = 0
  TaperInnerAngleRev = 0
  TreeRank = 133
  Type = 4
  ValidateShape = true
  _ProfileBasedVersion = 1
  _Version = 1
  expr: Length2 = <<Parameters>>.motor_height - 2 * <<Parameters>>.thickness
FEATURE [Sketcher::SketchObject] Sketch027
  ArcFitTolerance = 1e-06
  ExternalBSplineMaxDegree = 5
  ExternalBSplineTolerance = 0.0001
  FullyConstrained = true
  InternalTolerance = 1e-06
  InvalidShape = false
  MakeInternals = false
  MapMode = 2
  TreeRank = 110
  ValidateShape = true
  expr: Constraints[1] = <<Parameters>>.screw_shaft_diameter
  sketch-geometry (1):
    g0: Circle CenterX=0 CenterY=0 CenterZ=0 NormalX=0 NormalY=0 NormalZ=1 AngleXU=0 Radius=1.75
  constraints (2):
    c: Coincident(g0,g-1)
    c: Diameter(g0) = 3.5
FEATURE [PartDesign::Pocket] Pocket014
  AddSubType = 1
  AutoTaperInnerAngle = true
  BaseFeature = -> Pocket013
  CheckUpToFaceLimits = true
  ClaimChildren = false
  Fit = 0
  FitJoin = 0
  InnerFit = 0
  InnerFitJoin = 0
  InvalidShape = false
  Length = 100
  Length2 = 100
  Linearize = true
  NewSolid = false
  Profile = -> Sketch027
  Suppress = false
  TaperInnerAngle = 0
  TaperInnerAngleRev = 0
  TreeRank = 134
  Type = 4
  ValidateShape = true
  _ProfileBasedVersion = 1
  _Version = 1
FEATURE [Sketcher::SketchObject] Sketch028
  ArcFitTolerance = 1e-06
  AttachmentSupport = -> [YZ_Plane005]
  ExternalBSplineMaxDegree = 5
  ExternalBSplineTolerance = 0.0001
  FullyConstrained = true
  InternalTolerance = 1e-06
  InvalidShape = false
  MakeInternals = false
  MapMode = 5
  Placement = pos=(0,0,0) rot=(0.57735,0.57735,0.57735;2.0944rad)
  Support = -> [YZ_Plane005]
  TreeRank = 144
  ValidateShape = true
  expr: Constraints[2] = <<Parameters>>.station_diameter + <<Parameters>>.thickness
  expr: Constraints[3] = <<Parameters>>.motor_shaft_length
  expr: Constraints[8] = <<Parameters>>.thickness
  sketch-geometry (4):
    g0: LineSegment StartX=0 StartY=19 StartZ=0 EndX=-88 EndY=19 EndZ=0
    g1: LineSegment StartX=0 StartY=22 StartZ=0 EndX=-88 EndY=22 EndZ=0
    g2: LineSegment StartX=0 StartY=22 StartZ=0 EndX=0 EndY=19 EndZ=0
    g3: LineSegment StartX=-88 StartY=22 StartZ=0 EndX=-88 EndY=19 EndZ=0
  constraints (12):
    c: PointOnObject(g0,g-2)
    c: Horizontal(g0)
    c: DistanceX(g0,g0) = 88
    c: DistanceY(g-1,g0) = 19
    c: PointOnObject(g1,g-2)
    c: Horizontal(g1)
    c: Coincident(g2,g1)
    c: Coincident(g2,g0)
    c: DistanceY(g0,g1) = 3
    c: Coincident(g3,g1)
    c: Coincident(g3,g0)
    c: Vertical(g3)
FEATURE [PartDesign::Pad] Pad012
  AddSubType = 0
  AlongSketchNormal = false
  AutoTaperInnerAngle = true
  CheckUpToFaceLimits = true
  ClaimChildren = false
  Direction = (1,-2e-16,3e-16)
  Fit = 0
  FitJoin = 0
  InnerFit = 0
  InnerFitJoin = 0
  InvalidShape = false
  Length = 176
  Length2 = 100
  Linearize = true
  NewSolid = false
  Profile = -> Sketch028
  Reversed = true
  Suppress = false
  TaperInnerAngle = 0
  TaperInnerAngleRev = 0
  TreeRank = 145
  Type = 0
  ValidateShape = true
  _ProfileBasedVersion = 1
  expr: Length = 2 * (<<Parameters>>.station_diameter + <<Parameters>>.thickness)
FEATURE [Sketcher::SketchObject] Sketch029
  ArcFitTolerance = 1e-06
  AttachmentSupport = -> [XY_Plane005]
  ExternalBSplineMaxDegree = 5
  ExternalBSplineTolerance = 0.0001
  FullyConstrained = true
  InternalTolerance = 1e-06
  InvalidShape = false
  MakeInternals = false
  MapMode = 5
  Support = -> [XY_Plane005]
  TreeRank = 146
  ValidateShape = true
  expr: Constraints[0] = <<Parameters>>.station_diameter
  expr: Constraints[2] = <<Parameters>>.station_diameter
  expr: Constraints[3] = <<Parameters>>.station_diameter / 2 + <<Parameters>>.thickness
  expr: Constraints[4] = <<Parameters>>.station_diameter / 2 + <<Parameters>>.thickness
  expr: Constraints[8] = <<Parameters>>.motor_shaft_mount_diameter
  sketch-geometry (4):
    g0: Circle [constr] CenterX=-130.5 CenterY=-45.5 CenterZ=0 NormalX=0 NormalY=0 NormalZ=1 AngleXU=0 Radius=42.5
    g1: Circle [constr] CenterX=-45.5 CenterY=-45.5 CenterZ=0 NormalX=0 NormalY=0 NormalZ=1 AngleXU=0 Radius=42.5
    g2: Circle CenterX=-130.5 CenterY=-45.5 CenterZ=0 NormalX=0 NormalY=0 NormalZ=1 AngleXU=0 Radius=25
    g3: Circle CenterX=-45.5 CenterY=-45.5 CenterZ=0 NormalX=0 NormalY=0 NormalZ=1 AngleXU=0 Radius=25
  constraints (10):
    c: Diameter(g0) = 85
    c: Equal(g0,g1)
    c: DistanceX(g0,g1) = 85
    c: DistanceY(g1,g-1) = 45.5
    c: DistanceX(g1,g-1) = 45.5
    c: DistanceY(g1,g0) = 0
    c: Coincident(g2,g0)
    c: Coincident(g3,g1)
    c: Diameter(g2) = 50
    c: Equal(g2,g3)
FEATURE [PartDesign::Pocket] Pocket015
  AddSubType = 1
  AutoTaperInnerAngle = true
  BaseFeature = -> Pad012
  CheckUpToFaceLimits = true
  ClaimChildren = false
  Fit = 0
  FitJoin = 0
  InnerFit = 0
  InnerFitJoin = 0
  InvalidShape = false
  Length = 100
  Length2 = 100
  Linearize = true
  NewSolid = false
  Profile = -> Sketch029
  Suppress = false
  TaperInnerAngle = 0
  TaperInnerAngleRev = 0
  TreeRank = 147
  Type = 4
  ValidateShape = true
  _ProfileBasedVersion = 1
  _Version = 1
FEATURE [Sketcher::SketchObject] Sketch030
  ArcFitTolerance = 1e-06
  AttachmentSupport = -> [XY_Plane006]
  ExternalBSplineMaxDegree = 5
  ExternalBSplineTolerance = 0.0001
  FullyConstrained = true
  InternalTolerance = 1e-06
  InvalidShape = false
  MakeInternals = false
  MapMode = 5
  Support = -> [XY_Plane006]
  TreeRank = 157
  ValidateShape = true
  expr: Constraints[10] = (<<Parameters>>.station_diameter + <<Parameters>>.thickness) * 2 - 4 * <<Parameters>>.thickness - <<Parameters>>.motor_shaft_mount_diameter / 2 - 2 * <<Parameters>>.clearance
  expr: Constraints[11] = <<Parameters>>.thickness * 4 - 2 * <<Parameters>>.clearance
  sketch-geometry (5):
    g0: LineSegment StartX=5.6 StartY=-69.1 StartZ=0 EndX=5.6 EndY=69.1 EndZ=0
    g1: LineSegment StartX=5.6 StartY=69.1 StartZ=0 EndX=-5.6 EndY=69.1 EndZ=0
    g2: LineSegment StartX=-5.6 StartY=69.1 StartZ=0 EndX=-5.6 EndY=-69.1 EndZ=0
    g3: LineSegment StartX=-5.6 StartY=-69.1 StartZ=0 EndX=5.6 EndY=-69.1 EndZ=0
    g4: GeomPoint [constr] X=0 Y=0 Z=0
  constraints (12):
    c: Coincident(g0,g1)
    c: Coincident(g1,g2)
    c: Coincident(g2,g3)
    c: Coincident(g3,g0)
    c: Horizontal(g1)
    c: Horizontal(g3)
    c: Vertical(g0)
    c: Vertical(g2)
    c: Symmetric(g1,g0,g4)
    c: Coincident(g4,g-1)
    c: DistanceY(g0,g0) = 138.2
    c: DistanceX(g1,g0) = 11.2
FEATURE [PartDesign::Pad] Pad013
  AddSubType = 0
  AlongSketchNormal = false
  AutoTaperInnerAngle = true
  CheckUpToFaceLimits = true
  ClaimChildren = false
  Direction = (0,0,1)
  Fit = 0
  FitJoin = 0
  InnerFit = 0
  InnerFitJoin = 0
  InvalidShape = false
  Length = 1
  Length2 = 100
  Linearize = true
  NewSolid = false
  Profile = -> Sketch030
  Suppress = false
  TaperInnerAngle = 0
  TaperInnerAngleRev = 0
  TreeRank = 158
  Type = 0
  ValidateShape = true
  _ProfileBasedVersion = 1
  expr: Length = <<Parameters>>.lap_join_thickness
FEATURE [PartDesign::Fillet] Fillet010
  AddSubType = 0
  Base = -> Pad013 [Edge5,Edge2,Edge8,Edge1]
  BaseFeature = -> Pad013
  InvalidShape = false
  NewSolid = false
  Radius = 1
  SupportTransform = false
  Suppress = false
  TreeRank = 159
  ValidateShape = true
FEATURE [PartDesign::Body] Body006  label="Glue-in Support"
  AutoGroupSolids = false
  ClaimAllChildren = false
  ExportMode = 0
  Group = -> [Sketch030,Pad013,Fillet010]
  InvalidShape = false
  Origin = -> Origin006
  Tip = -> Fillet010
  TreeRank = 31
  ValidateShape = true
  _ExportChildren = -> [Pad013,Fillet010]
  _GroupVersion = 1
FEATURE [Sketcher::SketchObject] Sketch031
  ArcFitTolerance = 1e-06
  AttachmentSupport = -> [XY_Plane005]
  ExternalBSplineMaxDegree = 5
  ExternalBSplineTolerance = 0.0001
  FullyConstrained = true
  InternalTolerance = 1e-06
  InvalidShape = false
  MakeInternals = false
  MapMode = 5
  Support = -> [XY_Plane005]
  TreeRank = 160
  ValidateShape = true
  expr: Constraints[13] = (<<Parameters>>.station_diameter + <<Parameters>>.thickness) * 2
  expr: Constraints[16] = <<Parameters>>.station_diameter + <<Parameters>>.thickness
  expr: Constraints[17] = <<Parameters>>.station_diameter + <<Parameters>>.thickness
  expr: Constraints[6] = <<Parameters>>.motor_shaft_mount_diameter / 4
  expr: Constraints[8] = <<Parameters>>.motor_shaft_mount_diameter / 4
  sketch-geometry (7):
    g0: ArcOfCircle CenterX=0 CenterY=0 CenterZ=0 NormalX=0 NormalY=0 NormalZ=1 AngleXU=0 Radius=12.5 StartAngle=3.14159 EndAngle=4.71239
    g1: LineSegment StartX=-12.5 StartY=0 StartZ=0 EndX=0 EndY=0 EndZ=0
    g2: LineSegment StartX=0 StartY=0 StartZ=0 EndX=0 EndY=-12.5 EndZ=0
    g3: ArcOfCircle CenterX=-169.75 CenterY=0 CenterZ=0 NormalX=0 NormalY=0 NormalZ=1 AngleXU=0 Radius=6.25 StartAngle=3.14159 EndAngle=6.28319
    g4: LineSegment StartX=-176 StartY=0 StartZ=0 EndX=-163.5 EndY=0 EndZ=0
    g5: ArcOfCircle CenterX=-88 CenterY=-88 CenterZ=0 NormalX=0 NormalY=0 NormalZ=1 AngleXU=0 Radius=6.25 StartAngle=-2.93e-14 EndAngle=3.14159
    g6: LineSegment StartX=-94.25 StartY=-88 StartZ=0 EndX=-81.75 EndY=-88 EndZ=0
  constraints (22):
    c: Coincident(g0,g-1)
    c: Coincident(g1,g0)
    c: Horizontal(g1)
    c: Coincident(g2,g0)
    c: Coincident(g0,g2)
    c: Coincident(g0,g1)
    c: Radius(g0) = 12.5
    c: PointOnObject(g3,g-1)
    c: Diameter(g3) = 12.5
    c: Horizontal(g4)
    c: PointOnObject(g3,g4)
    c: Coincident(g3,g4)
    c: Coincident(g3,g4)
    c: DistanceX(g3,g0) = 176
    c: Vertical(g2)
    c: Equal(g3,g5)
    c: DistanceY(g5,g0) = 88
    c: DistanceX(g5,g0) = 88
    c: Horizontal(g6)
    c: PointOnObject(g5,g6)
    c: Coincident(g5,g6)
    c: Coincident(g5,g6)
FEATURE [PartDesign::Pad] Pad014
  AddSubType = 0
  AlongSketchNormal = false
  AutoTaperInnerAngle = true
  BaseFeature = -> Pocket015
  CheckUpToFaceLimits = true
  ClaimChildren = false
  Direction = (0,0,1)
  Fit = 0
  FitJoin = 0
  InnerFit = 0
  InnerFitJoin = 0
  InvalidShape = false
  Length = 19
  Length2 = 100
  Linearize = true
  NewSolid = false
  Profile = -> Sketch031
  Suppress = false
  TaperInnerAngle = 0
  TaperInnerAngleRev = 0
  TreeRank = 161
  Type = 0
  ValidateShape = true
  _ProfileBasedVersion = 1
  expr: Length = <<Parameters>>.motor_shaft_length
FEATURE [Sketcher::SketchObject] Sketch032
  ArcFitTolerance = 1e-06
  AttachmentSupport = -> [XY_Plane005]
  ExternalBSplineMaxDegree = 5
  ExternalBSplineTolerance = 0.0001
  FullyConstrained = true
  InternalTolerance = 1e-06
  InvalidShape = false
  MakeInternals = false
  MapMode = 5
  Support = -> [XY_Plane005]
  TreeRank = 162
  ValidateShape = true
  expr: Constraints[10] = (<<Parameters>>.station_diameter + <<Parameters>>.thickness) * 2 - 4 * <<Parameters>>.thickness - <<Parameters>>.motor_shaft_mount_diameter / 2
  expr: Constraints[11] = (2 * (<<Parameters>>.station_diameter + <<Parameters>>.thickness) - ((<<Parameters>>.station_diameter + <<Parameters>>.thickness) * 2 - 4 * <<Parameters>>.thickness - <<Parameters>>.motor_shaft_mount_diameter / 2)) / 2
  expr: Constraints[21] = (2 * (<<Parameters>>.station_diameter + <<Parameters>>.thickness) - ((<<Parameters>>.station_diameter + <<Parameters>>.thickness) * 2 - 4 * <<Parameters>>.thickness - <<Parameters>>.motor_shaft_mount_diameter / 2)) / 2
  expr: Constraints[22] = <<Parameters>>.thickness * 2
  expr: Constraints[23] = <<Parameters>>.station_diameter + <<Parameters>>.thickness - 2 * <<Parameters>>.thickness - <<Parameters>>.motor_shaft_mount_diameter / 4
  expr: Constraints[9] = <<Parameters>>.thickness * 2
  sketch-geometry (8):
    g0: LineSegment StartX=-18.5 StartY=0 StartZ=0 EndX=-157.5 EndY=0 EndZ=0
    g1: LineSegment StartX=-157.5 StartY=0 StartZ=0 EndX=-157.5 EndY=-6 EndZ=0
    g2: LineSegment StartX=-157.5 StartY=-6 StartZ=0 EndX=-18.5 EndY=-6 EndZ=0
    g3: LineSegment StartX=-18.5 StartY=-6 StartZ=0 EndX=-18.5 EndY=0 EndZ=0
    g4: LineSegment StartX=-6 StartY=-18.5 StartZ=0 EndX=0 EndY=-18.5 EndZ=0
    g5: LineSegment StartX=0 StartY=-18.5 StartZ=0 EndX=0 EndY=-88 EndZ=0
    g6: LineSegment StartX=0 StartY=-88 StartZ=0 EndX=-6 EndY=-88 EndZ=0
    g7: LineSegment StartX=-6 StartY=-88 StartZ=0 EndX=-6 EndY=-18.5 EndZ=0
  constraints (24):
    c: Coincident(g0,g1)
    c: Coincident(g1,g2)
    c: Coincident(g2,g3)
    c: Coincident(g3,g0)
    c: Horizontal(g0)
    c: Horizontal(g2)
    c: Vertical(g1)
    c: Vertical(g3)
    c: PointOnObject(g0,g-1)
    c: DistanceY(g2,g0) = 6
    c: DistanceX(g1,g2) = 139
    c: DistanceX(g0,g-1) = 18.5
    c: Coincident(g4,g5)
    c: Coincident(g5,g6)
    c: Coincident(g6,g7)
    c: Coincident(g7,g4)
    c: Horizontal(g4)
    c: Horizontal(g6)
    c: Vertical(g5)
    c: Vertical(g7)
    c: PointOnObject(g5,g-2)
    c: DistanceY(g4,g-1) = 18.5
    c: DistanceX(g4,g4) = 6
    c: DistanceY(g6,g4) = 69.5
FEATURE [PartDesign::Pocket] Pocket016
  AddSubType = 1
  AutoTaperInnerAngle = true
  BaseFeature = -> Pad014
  CheckUpToFaceLimits = true
  ClaimChildren = false
  Fit = 0
  FitJoin = 0
  InnerFit = 0
  InnerFitJoin = 0
  InvalidShape = false
  Length = 20
  Length2 = 100
  Linearize = true
  NewSolid = false
  Profile = -> Sketch032
  Reversed = true
  Suppress = false
  TaperInnerAngle = 0
  TaperInnerAngleRev = 0
  TreeRank = 163
  Type = 0
  ValidateShape = true
  _ProfileBasedVersion = 1
  _Version = 1
  expr: Length = <<Parameters>>.motor_shaft_length + <<Parameters>>.lap_join_thickness
FEATURE [Sketcher::SketchObject] Sketch034
  ArcFitTolerance = 1e-06
  AttachmentSupport = -> [YZ_Plane007]
  ExternalBSplineMaxDegree = 5
  ExternalBSplineTolerance = 0.0001
  FullyConstrained = false
  InternalTolerance = 1e-06
  InvalidShape = false
  MakeInternals = false
  MapMode = 5
  Placement = pos=(0,0,0) rot=(0.57735,0.57735,0.57735;2.0944rad)
  Support = -> [YZ_Plane007]
  TreeRank = 176
  ValidateShape = true
  expr: Constraints[12] = <<Parameters>>.thickness + <<Parameters>>.motor_screw_head_height
  expr: Constraints[13] = <<Parameters>>.motor_height
  expr: Constraints[14] = <<Parameters>>.thickness
  expr: Constraints[18] = <<Parameters>>.screen_body_thickness
  expr: Constraints[19] = (<<Parameters>>.station_diameter + <<Parameters>>.thickness) * 2
  expr: Constraints[20] = <<Parameters>>.screen_angle
  expr: Constraints[21] = <<Parameters>>.thickness
  expr: Constraints[25] = <<Parameters>>.thickness
  expr: Constraints[26] = <<Parameters>>.motor_shaft_length
  expr: Constraints[27] = <<Parameters>>.station_diameter + <<Parameters>>.thickness
  expr: Constraints[31] = <<Parameters>>.screen_overall_height + 2 * <<Parameters>>.thickness
  sketch-geometry (14):
    g0: LineSegment StartX=0 StartY=-36.25 StartZ=0 EndX=-176 EndY=-36.25 EndZ=0
    g1: LineSegment StartX=0 StartY=-36.25 StartZ=0 EndX=0 EndY=-30 EndZ=0
    g2: LineSegment StartX=0 StartY=-30 StartZ=0 EndX=-173 EndY=-30 EndZ=0
    g3: LineSegment StartX=-176 StartY=-36.25 StartZ=0 EndX=-176 EndY=-22.2218 EndZ=0
    g4: LineSegment StartX=-176 StartY=-22.2218 StartZ=0 EndX=-106.178 EndY=47.5998 EndZ=0
    g5: LineSegment StartX=-173 StartY=-30 StartZ=0 EndX=-173 EndY=-27 EndZ=0
    g6: LineSegment StartX=-173 StartY=-27 StartZ=0 EndX=-102.289 EndY=43.7107 EndZ=0
    g7: LineSegment [constr] StartX=-145.835 StartY=0.164981 StartZ=0 EndX=-149.724 EndY=4.05407 EndZ=0
    g8: LineSegment StartX=-88 StartY=22 StartZ=0 EndX=-96.7893 EndY=22 EndZ=0
    g9: LineSegment StartX=-88 StartY=22 StartZ=0 EndX=-88 EndY=19 EndZ=0
    g10: LineSegment StartX=-102.289 StartY=19 StartZ=0 EndX=-88 EndY=19 EndZ=0
    g11: LineSegment StartX=-102.289 StartY=43.7107 StartZ=0 EndX=-102.289 EndY=19 EndZ=0
    g12: LineSegment StartX=-96.7893 StartY=43.7107 StartZ=0 EndX=-96.7893 EndY=22 EndZ=0
    g13: ArcOfCircle CenterX=-102.289 CenterY=43.7107 CenterZ=0 NormalX=0 NormalY=0 NormalZ=1 AngleXU=0 Radius=5.5 StartAngle=-7.319e-13 EndAngle=2.35619
  constraints (40):
    c: PointOnObject(g0,g-2)
    c: Horizontal(g0)
    c: Coincident(g1,g0)
    c: PointOnObject(g1,g-2)
    c: Coincident(g2,g1)
    c: Horizontal(g2)
    c: Coincident(g3,g0)
    c: Vertical(g3)
    c: Coincident(g4,g3)
    c: Coincident(g5,g2)
    c: Vertical(g5)
    c: Coincident(g6,g5)
    c: DistanceY(g0,g1) = 6.25
    c: DistanceY(g1,g-1) = 30
    c: DistanceX(g0,g2) = 3
    c: Parallel(g6,g4)
    c: PointOnObject(g7,g6)
    c: Perpendicular(g4,g7)
    c: Distance(g7,g7) = 5.5
    c: DistanceX(g0,g-1) = 176
    c: Angle(g5,g6) = 2.35619
    c: DistanceY(g2,g5) = 3
    c: Horizontal(g8)
    c: Coincident(g9,g8)
    c: Vertical(g9)
    c: DistanceY(g9,g8) = 3
    c: DistanceY(g-1,g9) = 19
    c: DistanceX(g9,g-1) = 88
    c: PointOnObject(g7,g4)
    c: Coincident(g10,g9)
    c: Horizontal(g10)
    c: Distance(g6,g5) = 100
    c: Coincident(g11,g6)
    c: Coincident(g11,g10)
    c: Vertical(g11)
    c: Coincident(g12,g8)
    c: Vertical(g12)
    c: Tangent(g4,g13) = 1.5708
    c: Tangent(g12,g13) = 1.5708
    c: Coincident(g13,g6)
FEATURE [PartDesign::Pad] Pad015
  AddSubType = 0
  AlongSketchNormal = false
  AutoTaperInnerAngle = true
  CheckUpToFaceLimits = true
  ClaimChildren = false
  Direction = (1,-2e-16,3e-16)
  Fit = 0
  FitJoin = 0
  InnerFit = 0
  InnerFitJoin = 0
  InvalidShape = false
  Length = 176
  Length2 = 100
  Linearize = true
  NewSolid = false
  Profile = -> Sketch034
  Reversed = true
  Suppress = false
  TaperInnerAngle = 0
  TaperInnerAngleRev = 0
  TreeRank = 177
  Type = 0
  ValidateShape = true
  _ProfileBasedVersion = 1
  expr: Length = (<<Parameters>>.station_diameter + <<Parameters>>.thickness) * 2
FEATURE [Sketcher::SketchObject] Sketch035
  ArcFitTolerance = 1e-06
  AttachmentSupport = -> [XY_Plane007]
  ExternalBSplineMaxDegree = 5
  ExternalBSplineTolerance = 0.0001
  FullyConstrained = true
  InternalTolerance = 1e-06
  InvalidShape = false
  MakeInternals = false
  MapMode = 5
  Support = -> [XY_Plane007]
  TreeRank = 178
  ValidateShape = true
  expr: Constraints[15] = (<<Parameters>>.station_diameter + <<Parameters>>.thickness) * 2
  expr: Constraints[1] = <<Parameters>>.motor_shaft_mount_diameter / 4
  expr: Constraints[21] = (<<Parameters>>.station_diameter + <<Parameters>>.thickness) * 2
  expr: Constraints[22] = <<Parameters>>.station_diameter / 3
  expr: Constraints[26] = <<Parameters>>.thickness
  expr: Constraints[2] = <<Parameters>>.motor_shaft_mount_diameter / 4
  expr: Constraints[30] = <<Parameters>>.thickness
  expr: Constraints[31] = <<Parameters>>.station_diameter / 3 / 2
  expr: Constraints[32] = <<Parameters>>.motor_shaft_mount_diameter / 4
  expr: Constraints[4] = <<Parameters>>.station_diameter + <<Parameters>>.thickness
  expr: Constraints[5] = <<Parameters>>.station_diameter + <<Parameters>>.thickness
  sketch-geometry (11):
    g0: Circle CenterX=-88 CenterY=-88 CenterZ=0 NormalX=0 NormalY=0 NormalZ=1 AngleXU=0 Radius=6.25
    g1: ArcOfCircle CenterX=-169.75 CenterY=0 CenterZ=0 NormalX=0 NormalY=0 NormalZ=1 AngleXU=0 Radius=6.25 StartAngle=4.16554 EndAngle=6.28319
    g2: ArcOfCircle CenterX=0 CenterY=0 CenterZ=0 NormalX=0 NormalY=0 NormalZ=1 AngleXU=0 Radius=12.5 StartAngle=3.14159 EndAngle=4.71239
    g3: LineSegment StartX=-12.5 StartY=0 StartZ=0 EndX=0 EndY=0 EndZ=0
    g4: LineSegment StartX=0 StartY=0 StartZ=0 EndX=0 EndY=-12.5 EndZ=0
    g5: LineSegment StartX=-176 StartY=0 StartZ=0 EndX=-163.5 EndY=0 EndZ=0
    g6: LineSegment StartX=-176 StartY=0 StartZ=0 EndX=-176 EndY=-176 EndZ=0
    g7: LineSegment StartX=-173 StartY=-5.33854 StartZ=0 EndX=-173 EndY=-159.155 EndZ=0
    g8: ArcOfCircle CenterX=-158.833 CenterY=-159.155 CenterZ=0 NormalX=0 NormalY=0 NormalZ=1 AngleXU=0 Radius=14.1667 StartAngle=3.14159 EndAngle=4.49901
    g9: LineSegment StartX=-176 StartY=-176 StartZ=0 EndX=-161.833 EndY=-176 EndZ=0
    g10: LineSegment StartX=-161.833 StartY=-176 StartZ=0 EndX=-161.833 EndY=-173 EndZ=0
  constraints (33):
    c: Coincident(g2,g-1)
    c: Diameter(g1) = 12.5
    c: Radius(g2) = 12.5
    c: Equal(g1,g0)
    c: DistanceX(g0,g2) = 88
    c: DistanceY(g0,g2) = 88
    c: PointOnObject(g1,g-1)
    c: Coincident(g3,g2)
    c: Coincident(g4,g2)
    c: Vertical(g4)
    c: Horizontal(g3)
    c: Coincident(g2,g4)
    c: Coincident(g2,g3)
    c: Horizontal(g5)
    c: PointOnObject(g1,g5)
    c: DistanceX(g5,g2) = 176
    c: Coincident(g1,g5)
    c: Coincident(g6,g5)
    c: Vertical(g6)
    c: Vertical(g7)
    c: Coincident(g1,g7)
    c: DistanceY(g6,g2) = 176
    c: Diameter(g8) = 28.3333
    c: Coincident(g9,g6)
    c: Horizontal(g9)
    c: Tangent(g7,g8) = -1.5708
    c: DistanceX(g6,g7) = 3
    c: Coincident(g10,g9)
    c: Coincident(g10,g8)
    c: Vertical(g10)
    c: DistanceY(g9,g8) = 3
    c: DistanceX(g6,g9) = 14.1667
    c: DistanceX(g5,g1) = 12.5
FEATURE [PartDesign::Pad] Pad016
  AddSubType = 0
  AlongSketchNormal = false
  AutoTaperInnerAngle = true
  BaseFeature = -> Pad015
  CheckUpToFaceLimits = true
  ClaimChildren = false
  Direction = (0,0,1)
  Fit = 0
  FitJoin = 0
  InnerFit = 0
  InnerFitJoin = 0
  InvalidShape = false
  Length = 30
  Length2 = 100
  Linearize = true
  NewSolid = false
  Profile = -> Sketch035
  Reversed = true
  Suppress = false
  TaperInnerAngle = 0
  TaperInnerAngleRev = 0
  TreeRank = 179
  Type = 0
  ValidateShape = true
  _ProfileBasedVersion = 1
  expr: Length = <<Parameters>>.motor_height
FEATURE [Sketcher::SketchObject] Sketch036
  ArcFitTolerance = 1e-06
  AttachmentSupport = -> [XY_Plane007]
  ExternalBSplineMaxDegree = 5
  ExternalBSplineTolerance = 0.0001
  FullyConstrained = true
  InternalTolerance = 1e-06
  InvalidShape = false
  MakeInternals = false
  MapMode = 5
  Support = -> [XY_Plane007]
  TreeRank = 180
  ValidateShape = true
  expr: Constraints[0] = <<Parameters>>.station_diameter + <<Parameters>>.thickness
  expr: Constraints[1] = <<Parameters>>.station_diameter + <<Parameters>>.thickness
  expr: Constraints[2] = <<Parameters>>.motor_shaft_mount_diameter / 4
  sketch-geometry (2):
    g0: ArcOfCircle CenterX=-88 CenterY=-88 CenterZ=0 NormalX=0 NormalY=0 NormalZ=1 AngleXU=0 Radius=6.25 StartAngle=3.14159 EndAngle=6.28319
    g1: LineSegment StartX=-94.25 StartY=-88 StartZ=0 EndX=-81.75 EndY=-88 EndZ=0
  constraints (7):
    c: DistanceX(g0,g-1) = 88
    c: DistanceY(g0,g-1) = 88
    c: Diameter(g0) = 12.5
    c: Horizontal(g1)
    c: PointOnObject(g0,g1)
    c: Coincident(g0,g1)
    c: Coincident(g0,g1)
FEATURE [PartDesign::Pad] Pad017
  AddSubType = 0
  AlongSketchNormal = false
  AutoTaperInnerAngle = true
  BaseFeature = -> Pad016
  CheckUpToFaceLimits = true
  ClaimChildren = false
  Direction = (0,0,1)
  Fit = 0
  FitJoin = 0
  InnerFit = 0
  InnerFitJoin = 0
  InvalidShape = false
  Length = 19
  Length2 = 100
  Linearize = true
  NewSolid = false
  Profile = -> Sketch036
  Suppress = false
  TaperInnerAngle = 0
  TaperInnerAngleRev = 0
  TreeRank = 181
  Type = 0
  ValidateShape = true
  _ProfileBasedVersion = 1
  expr: Length = <<Parameters>>.motor_shaft_length
FEATURE [Sketcher::SketchObject] Sketch037
  ArcFitTolerance = 1e-06
  AttachmentOffset = pos=(0,0,-176) rot=(0,0,1;0rad)
  AttachmentSupport = -> [YZ_Plane007]
  ExternalBSplineMaxDegree = 5
  ExternalBSplineTolerance = 0.0001
  FullyConstrained = false
  InternalTolerance = 1e-06
  InvalidShape = false
  MakeInternals = false
  MapMode = 5
  Placement = pos=(-176,3.91e-14,-3.91e-14) rot=(0.57735,0.57735,0.57735;2.0944rad)
  Support = -> [YZ_Plane007]
  TreeRank = 182
  ValidateShape = true
  expr: AttachmentOffset.Base.z = -(<<Parameters>>.station_diameter + <<Parameters>>.thickness) * 2
  expr: Constraints[12] = <<Parameters>>.thickness + <<Parameters>>.motor_screw_head_height
  expr: Constraints[13] = <<Parameters>>.motor_height
  expr: Constraints[14] = <<Parameters>>.thickness
  expr: Constraints[15] = <<Parameters>>.thickness
  expr: Constraints[16] = (<<Parameters>>.station_diameter + <<Parameters>>.thickness) * 2
  expr: Constraints[17] = <<Parameters>>.thickness
  expr: Constraints[21] = <<Parameters>>.thickness
  expr: Constraints[22] = <<Parameters>>.motor_shaft_length
  expr: Constraints[23] = <<Parameters>>.station_diameter + <<Parameters>>.thickness
  expr: Constraints[26] = <<Parameters>>.screen_overall_height + 2 * <<Parameters>>.thickness
  expr: Constraints[47] = 180 - <<Parameters>>.screen_angle
  sketch-geometry (19):
    g0: LineSegment [constr] StartX=0 StartY=-36.25 StartZ=0 EndX=-176 EndY=-36.25 EndZ=0
    g1: LineSegment [constr] StartX=0 StartY=-36.25 StartZ=0 EndX=0 EndY=-30 EndZ=0
    g2: LineSegment [constr] StartX=0 StartY=-30 StartZ=0 EndX=-173 EndY=-30 EndZ=0
    g3: LineSegment [constr] StartX=-176 StartY=-36.25 StartZ=0 EndX=-176 EndY=-25.7574 EndZ=0
    g4: LineSegment [constr] StartX=-173 StartY=-30 StartZ=0 EndX=-173 EndY=-27 EndZ=0
    g5: LineSegment [constr] StartX=-145.194 StartY=0.805848 StartZ=0 EndX=-147.315 EndY=2.92717 EndZ=0
    g6: LineSegment StartX=-88 StartY=22 StartZ=0 EndX=-99.2893 EndY=22 EndZ=0
    g7: LineSegment StartX=-88 StartY=22 StartZ=0 EndX=-88 EndY=19 EndZ=0
    g8: LineSegment [constr] StartX=-102.289 StartY=19 StartZ=0 EndX=-88 EndY=19 EndZ=0
    g9: LineSegment [constr] StartX=-102.289 StartY=43.7107 StartZ=0 EndX=-102.289 EndY=19 EndZ=0
    g10: LineSegment StartX=-99.2893 StartY=43.7107 StartZ=0 EndX=-99.2893 EndY=22 EndZ=0
    g11: ArcOfCircle CenterX=-102.289 CenterY=43.7107 CenterZ=0 NormalX=0 NormalY=0 NormalZ=1 AngleXU=0 Radius=3 StartAngle=1e-16 EndAngle=2.35619
    g12: LineSegment [constr] StartX=-176 StartY=-25.7574 StartZ=0 EndX=-150.243 EndY=0 EndZ=0
    g13: LineSegment StartX=-150.243 StartY=0 StartZ=0 EndX=-104.411 EndY=45.832 EndZ=0
    g14: LineSegment [constr] StartX=-173 StartY=-27 StartZ=0 EndX=-146 EndY=0 EndZ=0
    g15: LineSegment [constr] StartX=-146 StartY=0 StartZ=0 EndX=-102.289 EndY=43.7107 EndZ=0
    g16: LineSegment StartX=-150.243 StartY=0 StartZ=0 EndX=-146 EndY=0 EndZ=0
    g17: LineSegment StartX=-146 StartY=0 StartZ=0 EndX=-88 EndY=0 EndZ=0
    g18: LineSegment StartX=-88 StartY=0 StartZ=0 EndX=-88 EndY=19 EndZ=0
  constraints (53):
    c: PointOnObject(g0,g-2)
    c: Horizontal(g0)
    c: Coincident(g1,g0)
    c: PointOnObject(g1,g-2)
    c: Coincident(g2,g1)
    c: Horizontal(g2)
    c: Coincident(g3,g0)
    c: Vertical(g3)
    c: Coincident(g12,g3)
    c: Coincident(g4,g2)
    c: Vertical(g4)
    c: Coincident(g14,g4)
    c: DistanceY(g0,g1) = 6.25
    c: DistanceY(g1,g-1) = 30
    c: DistanceX(g0,g2) = 3
    c: Distance(g5,g5) = 3
    c: DistanceX(g0,g-1) = 176
    c: DistanceY(g2,g4) = 3
    c: Horizontal(g6)
    c: Coincident(g7,g6)
    c: Vertical(g7)
    c: DistanceY(g7,g6) = 3
    c: DistanceY(g-1,g7) = 19
    c: DistanceX(g7,g-1) = 88
    c: Coincident(g8,g7)
    c: Horizontal(g8)
    c: Distance(g15,g4) = 100
    c: Coincident(g9,g15)
    c: Coincident(g9,g8)
    c: Vertical(g9)
    c: Coincident(g10,g6)
    c: Vertical(g10)
    c: Tangent(g13,g11) = 1.5708
    c: Tangent(g10,g11) = 1.5708
    c: Coincident(g11,g15)
    c: Coincident(g12,g13)
    c: Perpendicular(g12,g5)
    c: PointOnObject(g5,g13)
    c: Coincident(g14,g15)
    c: PointOnObject(g5,g14)
    c: Parallel(g14,g12)
    c: Parallel(g15,g12)
    c: Parallel(g14,g13)
    c: Coincident(g16,g12)
    c: Coincident(g16,g14)
    c: Horizontal(g16)
    c: PointOnObject(g12,g-1)
    c: Angle(g-1,g13) = 0.785398
    c: Coincident(g17,g15)
    c: PointOnObject(g17,g-1)
    c: Coincident(g18,g17)
    c: Coincident(g18,g7)
    c: Vertical(g18)
FEATURE [PartDesign::Pad] Pad018
  AddSubType = 0
  AlongSketchNormal = false
  AutoTaperInnerAngle = true
  BaseFeature = -> Pad017
  CheckUpToFaceLimits = true
  ClaimChildren = false
  Direction = (1,-3e-16,3e-16)
  Fit = 0
  FitJoin = 0
  InnerFit = 0
  InnerFitJoin = 0
  InvalidShape = false
  Length = 3
  Length2 = 100
  Linearize = true
  NewSolid = false
  Profile = -> Sketch037
  Suppress = false
  TaperInnerAngle = 0
  TaperInnerAngleRev = 0
  TreeRank = 183
  Type = 0
  ValidateShape = true
  _ProfileBasedVersion = 1
  expr: Length = <<Parameters>>.thickness
FEATURE [Sketcher::SketchObject] Sketch038
  ArcFitTolerance = 1e-06
  ExternalBSplineMaxDegree = 5
  ExternalBSplineTolerance = 0.0001
  FullyConstrained = false
  InternalTolerance = 1e-06
  InvalidShape = false
  MakeInternals = false
  MapMode = 2
  Placement = pos=(-88,-88,0) rot=(0.57735,0.57735,0.57735;0rad)
  TreeRank = 184
  ValidateShape = true
  expr: Placement.Base.x = -(<<Parameters>>.station_diameter + <<Parameters>>.thickness)
  expr: Placement.Base.y = -(<<Parameters>>.station_diameter + <<Parameters>>.thickness)
  expr: Constraints[0] = <<Parameters>>.station_diameter
  expr: Constraints[14] = <<Parameters>>.motor_screw_spacing
  expr: Constraints[29] = <<Parameters>>.motor_screw_shaft_diameter
  expr: Constraints[3] = <<Parameters>>.station_diameter
  sketch-geometry (20):
    g0: Circle [constr] CenterX=-42.5 CenterY=42.5 CenterZ=0 NormalX=0 NormalY=0 NormalZ=1 AngleXU=0 Radius=42.5
    g1: Circle [constr] CenterX=42.5 CenterY=42.5 CenterZ=0 NormalX=0 NormalY=0 NormalZ=1 AngleXU=0 Radius=42.5
    g2: LineSegment [constr] StartX=-29.5 StartY=29.5 StartZ=0 EndX=-29.5 EndY=55.5 EndZ=0
    g3: LineSegment [constr] StartX=-29.5 StartY=55.5 StartZ=0 EndX=-55.5 EndY=55.5 EndZ=0
    g4: LineSegment [constr] StartX=-55.5 StartY=55.5 StartZ=0 EndX=-55.5 EndY=29.5 EndZ=0
    g5: LineSegment [constr] StartX=-55.5 StartY=29.5 StartZ=0 EndX=-29.5 EndY=29.5 EndZ=0
    g6: GeomPoint [constr] X=-42.5 Y=42.5 Z=0
    g7: LineSegment [constr] StartX=55.5 StartY=29.5 StartZ=0 EndX=55.5 EndY=55.5 EndZ=0
    g8: LineSegment [constr] StartX=55.5 StartY=55.5 StartZ=0 EndX=29.5 EndY=55.5 EndZ=0
    g9: LineSegment [constr] StartX=29.5 StartY=55.5 StartZ=0 EndX=29.5 EndY=29.5 EndZ=0
    g10: LineSegment [constr] StartX=29.5 StartY=29.5 StartZ=0 EndX=55.5 EndY=29.5 EndZ=0
    g11: GeomPoint [constr] X=42.5 Y=42.5 Z=0
    g12: Circle CenterX=-55.5 CenterY=55.5 CenterZ=0 NormalX=0 NormalY=0 NormalZ=1 AngleXU=0 Radius=1.75
    g13: Circle CenterX=-29.5 CenterY=55.5 CenterZ=0 NormalX=0 NormalY=0 NormalZ=1 AngleXU=0 Radius=1.75
    g14: Circle CenterX=-29.5 CenterY=29.5 CenterZ=0 NormalX=0 NormalY=0 NormalZ=1 AngleXU=0 Radius=1.75
    g15: Circle CenterX=-55.5 CenterY=29.5 CenterZ=0 NormalX=0 NormalY=0 NormalZ=1 AngleXU=0 Radius=1.75
    g16: Circle CenterX=29.5 CenterY=55.5 CenterZ=0 NormalX=0 NormalY=0 NormalZ=1 AngleXU=0 Radius=1.75
    g17: Circle CenterX=55.5 CenterY=55.5 CenterZ=0 NormalX=0 NormalY=0 NormalZ=1 AngleXU=0 Radius=1.75
    g18: Circle CenterX=55.5 CenterY=29.5 CenterZ=0 NormalX=0 NormalY=0 NormalZ=1 AngleXU=0 Radius=1.75
    g19: Circle CenterX=29.5 CenterY=29.5 CenterZ=0 NormalX=0 NormalY=0 NormalZ=1 AngleXU=0 Radius=1.75
  constraints (44):
    c: Diameter(g0) = 85
    c: Equal(g0,g1)
    c: Symmetric(g0,g1,g-2)
    c: DistanceX(g0,g1) = 85
    c: Coincident(g2,g3)
    c: Coincident(g3,g4)
    c: Coincident(g4,g5)
    c: Coincident(g5,g2)
    c: Horizontal(g3)
    c: Horizontal(g5)
    c: Vertical(g2)
    c: Vertical(g4)
    c: Symmetric(g3,g2,g6)
    c: Coincident(g6,g0)
    c: DistanceX(g3,g2) = 26
    c: Equal(g3,g4)
    c: Coincident(g7,g8)
    c: Coincident(g8,g9)
    c: Coincident(g9,g10)
    c: Coincident(g10,g7)
    c: Horizontal(g8)
    c: Horizontal(g10)
    c: Vertical(g7)
    c: Vertical(g9)
    c: Symmetric(g8,g7,g11)
    c: Coincident(g11,g1)
    c: Equal(g3,g8)
    c: Equal(g3,g9)
    c: Coincident(g12,g3)
    c: Diameter(g12) = 3.5
    c: Coincident(g13,g2)
    c: Coincident(g14,g2)
    c: Coincident(g15,g4)
    c: Coincident(g16,g8)
    c: Coincident(g17,g7)
    c: Coincident(g18,g7)
    c: Coincident(g19,g9)
    c: Equal(g12,g13)
    c: Equal(g12,g15)
    c: Equal(g12,g14)
    c: Equal(g12,g16)
    c: Equal(g16,g17)
    c: Equal(g16,g19)
    c: Equal(g16,g18)
FEATURE [PartDesign::Pocket] Pocket018
  AddSubType = 1
  AutoTaperInnerAngle = true
  BaseFeature = -> Pad018
  CheckUpToFaceLimits = true
  ClaimChildren = false
  Fit = 0
  FitJoin = 0
  InnerFit = 0
  InnerFitJoin = 0
  InvalidShape = false
  Length = 100
  Length2 = 100
  Linearize = true
  NewSolid = false
  Profile = -> Sketch038
  Suppress = false
  TaperInnerAngle = 0
  TaperInnerAngleRev = 0
  TreeRank = 185
  Type = 0
  ValidateShape = true
  _ProfileBasedVersion = 1
  _Version = 1
FEATURE [Sketcher::SketchObject] Sketch039
  ArcFitTolerance = 1e-06
  ExternalBSplineMaxDegree = 5
  ExternalBSplineTolerance = 0.0001
  FullyConstrained = false
  InternalTolerance = 1e-06
  InvalidShape = false
  MakeInternals = false
  MapMode = 2
  Placement = pos=(-88,-88,-36.25) rot=(0.57735,0.57735,0.57735;0rad)
  TreeRank = 186
  ValidateShape = true
  expr: Placement.Base.x = -(<<Parameters>>.station_diameter + <<Parameters>>.thickness)
  expr: Placement.Base.y = -(<<Parameters>>.station_diameter + <<Parameters>>.thickness)
  expr: Placement.Base.z = -(<<Parameters>>.motor_height + <<Parameters>>.thickness + <<Parameters>>.motor_screw_head_height)
  expr: Constraints[0] = <<Parameters>>.station_diameter
  expr: Constraints[14] = <<Parameters>>.motor_screw_spacing
  expr: Constraints[29] = <<Parameters>>.motor_screw_head_diameter
  expr: Constraints[3] = <<Parameters>>.station_diameter
  sketch-geometry (20):
    g0: Circle [constr] CenterX=-42.5 CenterY=42.5 CenterZ=0 NormalX=0 NormalY=0 NormalZ=1 AngleXU=0 Radius=42.5
    g1: Circle [constr] CenterX=42.5 CenterY=42.5 CenterZ=0 NormalX=0 NormalY=0 NormalZ=1 AngleXU=0 Radius=42.5
    g2: LineSegment [constr] StartX=-29.5 StartY=29.5 StartZ=0 EndX=-29.5 EndY=55.5 EndZ=0
    g3: LineSegment [constr] StartX=-29.5 StartY=55.5 StartZ=0 EndX=-55.5 EndY=55.5 EndZ=0
    g4: LineSegment [constr] StartX=-55.5 StartY=55.5 StartZ=0 EndX=-55.5 EndY=29.5 EndZ=0
    g5: LineSegment [constr] StartX=-55.5 StartY=29.5 StartZ=0 EndX=-29.5 EndY=29.5 EndZ=0
    g6: GeomPoint [constr] X=-42.5 Y=42.5 Z=0
    g7: LineSegment [constr] StartX=55.5 StartY=29.5 StartZ=0 EndX=55.5 EndY=55.5 EndZ=0
    g8: LineSegment [constr] StartX=55.5 StartY=55.5 StartZ=0 EndX=29.5 EndY=55.5 EndZ=0
    g9: LineSegment [constr] StartX=29.5 StartY=55.5 StartZ=0 EndX=29.5 EndY=29.5 EndZ=0
    g10: LineSegment [constr] StartX=29.5 StartY=29.5 StartZ=0 EndX=55.5 EndY=29.5 EndZ=0
    g11: GeomPoint [constr] X=42.5 Y=42.5 Z=0
    g12: Circle CenterX=-55.5 CenterY=55.5 CenterZ=0 NormalX=0 NormalY=0 NormalZ=1 AngleXU=0 Radius=3
    g13: Circle CenterX=-29.5 CenterY=55.5 CenterZ=0 NormalX=0 NormalY=0 NormalZ=1 AngleXU=0 Radius=3
    g14: Circle CenterX=-29.5 CenterY=29.5 CenterZ=0 NormalX=0 NormalY=0 NormalZ=1 AngleXU=0 Radius=3
    g15: Circle CenterX=-55.5 CenterY=29.5 CenterZ=0 NormalX=0 NormalY=0 NormalZ=1 AngleXU=0 Radius=3
    g16: Circle CenterX=29.5 CenterY=55.5 CenterZ=0 NormalX=0 NormalY=0 NormalZ=1 AngleXU=0 Radius=3
    g17: Circle CenterX=55.5 CenterY=55.5 CenterZ=0 NormalX=0 NormalY=0 NormalZ=1 AngleXU=0 Radius=3
    g18: Circle CenterX=55.5 CenterY=29.5 CenterZ=0 NormalX=0 NormalY=0 NormalZ=1 AngleXU=0 Radius=3
    g19: Circle CenterX=29.5 CenterY=29.5 CenterZ=0 NormalX=0 NormalY=0 NormalZ=1 AngleXU=0 Radius=3
  constraints (44):
    c: Diameter(g0) = 85
    c: Equal(g0,g1)
    c: Symmetric(g0,g1,g-2)
    c: DistanceX(g0,g1) = 85
    c: Coincident(g2,g3)
    c: Coincident(g3,g4)
    c: Coincident(g4,g5)
    c: Coincident(g5,g2)
    c: Horizontal(g3)
    c: Horizontal(g5)
    c: Vertical(g2)
    c: Vertical(g4)
    c: Symmetric(g3,g2,g6)
    c: Coincident(g6,g0)
    c: DistanceX(g3,g2) = 26
    c: Equal(g3,g4)
    c: Coincident(g7,g8)
    c: Coincident(g8,g9)
    c: Coincident(g9,g10)
    c: Coincident(g10,g7)
    c: Horizontal(g8)
    c: Horizontal(g10)
    c: Vertical(g7)
    c: Vertical(g9)
    c: Symmetric(g8,g7,g11)
    c: Coincident(g11,g1)
    c: Equal(g3,g8)
    c: Equal(g3,g9)
    c: Coincident(g12,g3)
    c: Diameter(g12) = 6
    c: Coincident(g13,g2)
    c: Coincident(g14,g2)
    c: Coincident(g15,g4)
    c: Coincident(g16,g8)
    c: Coincident(g17,g7)
    c: Coincident(g18,g7)
    c: Coincident(g19,g9)
    c: Equal(g12,g13)
    c: Equal(g12,g15)
    c: Equal(g12,g14)
    c: Equal(g12,g16)
    c: Equal(g16,g17)
    c: Equal(g16,g19)
    c: Equal(g16,g18)
FEATURE [PartDesign::Pocket] Pocket019
  AddSubType = 1
  AutoTaperInnerAngle = true
  BaseFeature = -> Pocket018
  CheckUpToFaceLimits = true
  ClaimChildren = false
  Fit = 0
  FitJoin = 0
  InnerFit = 0
  InnerFitJoin = 0
  InvalidShape = false
  Length = 3.25
  Length2 = 100
  Linearize = true
  NewSolid = false
  Profile = -> Sketch039
  Reversed = true
  Suppress = false
  TaperInnerAngle = 0
  TaperInnerAngleRev = 0
  TreeRank = 187
  Type = 0
  ValidateShape = true
  _ProfileBasedVersion = 1
  _Version = 1
  expr: Length = <<Parameters>>.motor_screw_head_height
FEATURE [Sketcher::SketchObject] Sketch040
  ArcFitTolerance = 1e-06
  ExternalBSplineMaxDegree = 5
  ExternalBSplineTolerance = 0.0001
  FullyConstrained = true
  InternalTolerance = 1e-06
  InvalidShape = false
  MakeInternals = false
  MapMode = 2
  Placement = pos=(-88,-88,-30) rot=(0.57735,0.57735,0.57735;0rad)
  TreeRank = 188
  ValidateShape = true
  expr: Placement.Base.x = -(<<Parameters>>.station_diameter + <<Parameters>>.thickness)
  expr: Placement.Base.y = -(<<Parameters>>.station_diameter + <<Parameters>>.thickness)
  expr: Placement.Base.z = -<<Parameters>>.motor_height
  expr: Constraints[14] = <<Parameters>>.thickness * 2
  expr: Constraints[17] = <<Parameters>>.station_diameter + <<Parameters>>.thickness
  expr: Constraints[18] = <<Parameters>>.station_diameter + <<Parameters>>.thickness
  expr: Constraints[19] = (<<Parameters>>.station_diameter + <<Parameters>>.thickness) * 2 - 4 * <<Parameters>>.thickness - <<Parameters>>.motor_shaft_mount_diameter / 2
  sketch-geometry (8):
    g0: LineSegment StartX=88 StartY=69.5 StartZ=0 EndX=82 EndY=69.5 EndZ=0
    g1: LineSegment StartX=82 StartY=69.5 StartZ=0 EndX=82 EndY=-69.5 EndZ=0
    g2: LineSegment StartX=82 StartY=-69.5 StartZ=0 EndX=88 EndY=-69.5 EndZ=0
    g3: LineSegment StartX=88 StartY=-69.5 StartZ=0 EndX=88 EndY=69.5 EndZ=0
    g4: LineSegment StartX=-69.5 StartY=82 StartZ=0 EndX=69.5 EndY=82 EndZ=0
    g5: LineSegment StartX=69.5 StartY=82 StartZ=0 EndX=69.5 EndY=88 EndZ=0
    g6: LineSegment StartX=69.5 StartY=88 StartZ=0 EndX=-69.5 EndY=88 EndZ=0
    g7: LineSegment StartX=-69.5 StartY=88 StartZ=0 EndX=-69.5 EndY=82 EndZ=0
  constraints (22):
    c: Coincident(g0,g1)
    c: Coincident(g1,g2)
    c: Coincident(g2,g3)
    c: Coincident(g3,g0)
    c: Horizontal(g0)
    c: Horizontal(g2)
    c: Vertical(g1)
    c: Coincident(g4,g5)
    c: Coincident(g5,g6)
    c: Coincident(g6,g7)
    c: Coincident(g7,g4)
    c: Horizontal(g6)
    c: Vertical(g5)
    c: Vertical(g7)
    c: DistanceX(g0,g0) = 6
    c: Equal(g0,g5)
    c: Symmetric(g4,g4,g-2)
    c: DistanceX(g-1,g0) = 88
    c: DistanceY(g-1,g6) = 88
    c: DistanceX(g6,g5) = 139
    c: Equal(g6,g3)
    c: Symmetric(g0,g2,g-1)
FEATURE [PartDesign::Pocket] Pocket020
  AddSubType = 1
  AutoTaperInnerAngle = true
  BaseFeature = -> Pocket019
  CheckUpToFaceLimits = true
  ClaimChildren = false
  Fit = 0
  FitJoin = 0
  InnerFit = 0
  InnerFitJoin = 0
  InvalidShape = false
  Length = 1
  Length2 = 100
  Linearize = true
  NewSolid = false
  Profile = -> Sketch040
  Suppress = false
  TaperInnerAngle = 0
  TaperInnerAngleRev = 0
  TreeRank = 189
  Type = 0
  ValidateShape = true
  _ProfileBasedVersion = 1
  _Version = 1
  expr: Length = <<Parameters>>.lap_join_thickness
FEATURE [Sketcher::SketchObject] Sketch041
  ArcFitTolerance = 1e-06
  AttachmentSupport = -> [XY_Plane007]
  ExternalBSplineMaxDegree = 5
  ExternalBSplineTolerance = 0.0001
  FullyConstrained = true
  InternalTolerance = 1e-06
  InvalidShape = false
  MakeInternals = false
  MapMode = 5
  Support = -> [XY_Plane007]
  TreeRank = 190
  ValidateShape = true
  expr: Constraints[15] = <<Parameters>>.station_diameter / 3
  expr: Constraints[16] = (<<Parameters>>.station_diameter + <<Parameters>>.thickness) * 2
  expr: Constraints[21] = (<<Parameters>>.station_diameter + <<Parameters>>.thickness) * 2 * 2
  sketch-geometry (10):
    g0: LineSegment StartX=0 StartY=-176 StartZ=0 EndX=-161.833 EndY=-176 EndZ=0
    g1: LineSegment StartX=-176 StartY=-161.833 StartZ=0 EndX=-176 EndY=0 EndZ=0
    g2: LineSegment StartX=-176 StartY=0 StartZ=0 EndX=0 EndY=0 EndZ=0
    g3: LineSegment StartX=0 StartY=0 StartZ=0 EndX=0 EndY=-176 EndZ=0
    g4: LineSegment StartX=-264 StartY=88 StartZ=0 EndX=88 EndY=88 EndZ=0
    g5: LineSegment StartX=88 StartY=88 StartZ=0 EndX=88 EndY=-264 EndZ=0
    g6: LineSegment StartX=88 StartY=-264 StartZ=0 EndX=-264 EndY=-264 EndZ=0
    g7: LineSegment StartX=-264 StartY=-264 StartZ=0 EndX=-264 EndY=88 EndZ=0
    g8: ArcOfCircle CenterX=-161.833 CenterY=-161.833 CenterZ=0 NormalX=0 NormalY=0 NormalZ=1 AngleXU=0 Radius=14.1667 StartAngle=3.14159 EndAngle=4.71239
    g9: GeomPoint [constr] X=-88 Y=-88 Z=0
  constraints (25):
    c: Coincident(g1,g2)
    c: Coincident(g2,g3)
    c: Coincident(g3,g0)
    c: Horizontal(g0)
    c: Horizontal(g2)
    c: Vertical(g1)
    c: Vertical(g3)
    c: Coincident(g4,g5)
    c: Coincident(g5,g6)
    c: Coincident(g6,g7)
    c: Coincident(g7,g4)
    c: Horizontal(g4)
    c: Horizontal(g6)
    c: Vertical(g5)
    c: Vertical(g7)
    c: Diameter(g8) = 28.3333
    c: DistanceX(g1,g2) = 176
    c: Equal(g2,g3)
    c: Coincident(g2,g-1)
    c: Tangent(g8,g0) = 1.5708
    c: Tangent(g8,g1) = 1.5708
    c: DistanceX(g4,g4) = 352
    c: Equal(g4,g5)
    c: Symmetric(g1,g0,g9)
    c: Symmetric(g5,g4,g9)
FEATURE [PartDesign::Pocket] Pocket021
  AddSubType = 1
  AutoTaperInnerAngle = true
  BaseFeature = -> Pocket020
  CheckUpToFaceLimits = true
  ClaimChildren = false
  Fit = 0
  FitJoin = 0
  InnerFit = 0
  InnerFitJoin = 0
  InvalidShape = false
  Length = 100
  Length2 = 100
  Linearize = true
  NewSolid = false
  Profile = -> Sketch041
  Suppress = false
  TaperInnerAngle = 0
  TaperInnerAngleRev = 0
  TreeRank = 191
  Type = 4
  ValidateShape = true
  _ProfileBasedVersion = 1
  _Version = 1
FEATURE [Sketcher::SketchObject] Sketch042
  ArcFitTolerance = 1e-06
  AttachmentSupport = -> [YZ_Plane007]
  ExternalBSplineMaxDegree = 5
  ExternalBSplineTolerance = 0.0001
  FullyConstrained = false
  InternalTolerance = 1e-06
  InvalidShape = false
  MakeInternals = false
  MapMode = 5
  Placement = pos=(0,0,0) rot=(0.57735,0.57735,0.57735;2.0944rad)
  Support = -> [YZ_Plane007]
  TreeRank = 192
  ValidateShape = true
  expr: Constraints[12] = <<Parameters>>.thickness + <<Parameters>>.motor_screw_head_height
  expr: Constraints[13] = <<Parameters>>.motor_height
  expr: Constraints[14] = <<Parameters>>.thickness
  expr: Constraints[18] = <<Parameters>>.screen_body_thickness
  expr: Constraints[19] = (<<Parameters>>.station_diameter + <<Parameters>>.thickness) * 2
  expr: Constraints[20] = <<Parameters>>.screen_angle
  expr: Constraints[21] = <<Parameters>>.thickness
  expr: Constraints[25] = <<Parameters>>.thickness
  expr: Constraints[26] = <<Parameters>>.motor_shaft_length
  expr: Constraints[27] = <<Parameters>>.station_diameter + <<Parameters>>.thickness
  expr: Constraints[31] = <<Parameters>>.screen_overall_height + 2 * <<Parameters>>.thickness
  expr: Constraints[47] = 10 * <<Parameters>>.thickness
  sketch-geometry (17):
    g0: LineSegment [constr] StartX=0 StartY=-36.25 StartZ=0 EndX=-176 EndY=-36.25 EndZ=0
    g1: LineSegment [constr] StartX=0 StartY=-36.25 StartZ=0 EndX=0 EndY=-30 EndZ=0
    g2: LineSegment [constr] StartX=0 StartY=-30 StartZ=0 EndX=-173 EndY=-30 EndZ=0
    g3: LineSegment [constr] StartX=-176 StartY=-36.25 StartZ=0 EndX=-176 EndY=-22.2218 EndZ=0
    g4: LineSegment StartX=-176 StartY=-22.2218 StartZ=0 EndX=-106.178 EndY=47.5998 EndZ=0
    g5: LineSegment [constr] StartX=-173 StartY=-30 StartZ=0 EndX=-173 EndY=-27 EndZ=0
    g6: LineSegment [constr] StartX=-173 StartY=-27 StartZ=0 EndX=-102.289 EndY=43.7107 EndZ=0
    g7: LineSegment [constr] StartX=-145.874 StartY=0.12624 StartZ=0 EndX=-149.763 EndY=4.01533 EndZ=0
    g8: LineSegment [constr] StartX=-88 StartY=22 StartZ=0 EndX=-96.7893 EndY=22 EndZ=0
    g9: LineSegment [constr] StartX=-88 StartY=22 StartZ=0 EndX=-88 EndY=19 EndZ=0
    g10: LineSegment [constr] StartX=-102.289 StartY=19 StartZ=0 EndX=-88 EndY=19 EndZ=0
    g11: LineSegment [constr] StartX=-102.289 StartY=43.7107 StartZ=0 EndX=-102.289 EndY=19 EndZ=0
    g12: LineSegment [constr] StartX=-96.7893 StartY=43.7107 StartZ=0 EndX=-96.7893 EndY=22 EndZ=0
    g13: ArcOfCircle [constr] CenterX=-102.289 CenterY=43.7107 CenterZ=0 NormalX=0 NormalY=0 NormalZ=1 AngleXU=0 Radius=5.5 StartAngle=-1.4149e-12 EndAngle=2.35619
    g14: LineSegment StartX=-176 StartY=-22.2218 StartZ=0 EndX=-197.213 EndY=-1.00862 EndZ=0
    g15: LineSegment StartX=-106.178 StartY=47.5998 StartZ=0 EndX=-127.392 EndY=68.813 EndZ=0
    g16: LineSegment StartX=-127.392 StartY=68.813 StartZ=0 EndX=-197.213 EndY=-1.00862 EndZ=0
  constraints (48):
    c: PointOnObject(g0,g-2)
    c: Horizontal(g0)
    c: Coincident(g1,g0)
    c: PointOnObject(g1,g-2)
    c: Coincident(g2,g1)
    c: Horizontal(g2)
    c: Coincident(g3,g0)
    c: Vertical(g3)
    c: Coincident(g4,g3)
    c: Coincident(g5,g2)
    c: Vertical(g5)
    c: Coincident(g6,g5)
    c: DistanceY(g0,g1) = 6.25
    c: DistanceY(g1,g-1) = 30
    c: DistanceX(g0,g2) = 3
    c: Parallel(g6,g4)
    c: PointOnObject(g7,g6)
    c: Perpendicular(g4,g7)
    c: Distance(g7,g7) = 5.5
    c: DistanceX(g0,g-1) = 176
    c: Angle(g5,g6) = 2.35619
    c: DistanceY(g2,g5) = 3
    c: Horizontal(g8)
    c: Coincident(g9,g8)
    c: Vertical(g9)
    c: DistanceY(g9,g8) = 3
    c: DistanceY(g-1,g9) = 19
    c: DistanceX(g9,g-1) = 88
    c: PointOnObject(g7,g4)
    c: Coincident(g10,g9)
    c: Horizontal(g10)
    c: Distance(g6,g5) = 100
    c: Coincident(g11,g6)
    c: Coincident(g11,g10)
    c: Vertical(g11)
    c: Coincident(g12,g8)
    c: Vertical(g12)
    c: Tangent(g4,g13) = 1.5708
    c: Tangent(g12,g13) = 1.5708
    c: Coincident(g13,g6)
    c: Coincident(g14,g3)
    c: Coincident(g15,g4)
    c: Coincident(g16,g14)
    c: Parallel(g15,g14)
    c: Parallel(g4,g16)
    c: Coincident(g15,g16)
    c: Perpendicular(g14,g4)
    c: Distance(g4,g14) = 30
FEATURE [PartDesign::Pocket] Pocket022
  AddSubType = 1
  AutoTaperInnerAngle = true
  BaseFeature = -> Pocket021
  CheckUpToFaceLimits = true
  ClaimChildren = false
  Fit = 0
  FitJoin = 0
  InnerFit = 0
  InnerFitJoin = 0
  InvalidShape = false
  Length = 500
  Length2 = 100
  Linearize = true
  NewSolid = false
  Profile = -> Sketch042
  Suppress = false
  TaperInnerAngle = 0
  TaperInnerAngleRev = 0
  TreeRank = 193
  Type = 0
  ValidateShape = true
  _ProfileBasedVersion = 1
  _Version = 1
FEATURE [PartDesign::Fillet] Fillet011
  AddSubType = 0
  Base = -> Pocket022 [Edge40,Edge34,Edge54,Edge23]
  BaseFeature = -> Pocket022
  InvalidShape = false
  NewSolid = false
  Radius = 3
  SupportTransform = false
  Suppress = false
  TreeRank = 194
  ValidateShape = true
  expr: Radius = <<Parameters>>.thickness
FEATURE [Sketcher::SketchObject] Sketch043
  ArcFitTolerance = 1e-06
  AttachmentSupport = -> [XY_Plane005]
  ExternalBSplineMaxDegree = 5
  ExternalBSplineTolerance = 0.0001
  FullyConstrained = true
  InternalTolerance = 1e-06
  InvalidShape = false
  MakeInternals = false
  MapMode = 5
  Support = -> [XY_Plane005]
  TreeRank = 195
  ValidateShape = true
  expr: Constraints[11] = 2 * (<<Parameters>>.station_diameter + <<Parameters>>.thickness)
  expr: Constraints[8] = <<Parameters>>.thickness
  expr: Constraints[9] = <<Parameters>>.station_diameter + <<Parameters>>.thickness
  sketch-geometry (4):
    g0: LineSegment StartX=-176 StartY=0 StartZ=0 EndX=-173 EndY=0 EndZ=0
    g1: LineSegment StartX=-173 StartY=0 StartZ=0 EndX=-173 EndY=-88 EndZ=0
    g2: LineSegment StartX=-173 StartY=-88 StartZ=0 EndX=-176 EndY=-88 EndZ=0
    g3: LineSegment StartX=-176 StartY=-88 StartZ=0 EndX=-176 EndY=0 EndZ=0
  constraints (12):
    c: Coincident(g0,g1)
    c: Coincident(g1,g2)
    c: Coincident(g2,g3)
    c: Coincident(g3,g0)
    c: Horizontal(g0)
    c: Horizontal(g2)
    c: Vertical(g1)
    c: Vertical(g3)
    c: DistanceX(g2,g1) = 3
    c: DistanceY(g2,g-1) = 88
    c: PointOnObject(g0,g-1)
    c: DistanceX(g0,g-1) = 176
FEATURE [PartDesign::Pad] Pad019
  AddSubType = 0
  AlongSketchNormal = false
  AutoTaperInnerAngle = true
  BaseFeature = -> Pocket016
  CheckUpToFaceLimits = true
  ClaimChildren = false
  Direction = (0,0,1)
  Fit = 0
  FitJoin = 0
  InnerFit = 0
  InnerFitJoin = 0
  InvalidShape = false
  Length = 19
  Length2 = 100
  Linearize = true
  NewSolid = false
  Profile = -> Sketch043
  Suppress = false
  TaperInnerAngle = 0
  TaperInnerAngleRev = 0
  TreeRank = 196
  Type = 0
  ValidateShape = true
  _ProfileBasedVersion = 1
  expr: Length = <<Parameters>>.motor_shaft_length
FEATURE [Sketcher::SketchObject] Sketch044
  ArcFitTolerance = 1e-06
  AttachmentSupport = -> [XY_Plane005]
  ExternalBSplineMaxDegree = 5
  ExternalBSplineTolerance = 0.0001
  FullyConstrained = true
  InternalTolerance = 1e-06
  InvalidShape = false
  MakeInternals = false
  MapMode = 5
  Support = -> [XY_Plane005]
  TreeRank = 197
  ValidateShape = true
  expr: Constraints[10] = 2 * <<Parameters>>.station_diameter + <<Parameters>>.thickness
  expr: Constraints[11] = <<Parameters>>.station_diameter - 2 * <<Parameters>>.thickness
  expr: Constraints[8] = <<Parameters>>.thickness
  expr: Constraints[9] = <<Parameters>>.station_diameter + <<Parameters>>.thickness
  sketch-geometry (4):
    g0: LineSegment StartX=-173 StartY=-88 StartZ=0 EndX=-170 EndY=-88 EndZ=0
    g1: LineSegment StartX=-170 StartY=-88 StartZ=0 EndX=-170 EndY=-9 EndZ=0
    g2: LineSegment StartX=-170 StartY=-9 StartZ=0 EndX=-173 EndY=-9 EndZ=0
    g3: LineSegment StartX=-173 StartY=-9 StartZ=0 EndX=-173 EndY=-88 EndZ=0
  constraints (12):
    c: Coincident(g0,g1)
    c: Coincident(g1,g2)
    c: Coincident(g2,g3)
    c: Coincident(g3,g0)
    c: Horizontal(g0)
    c: Horizontal(g2)
    c: Vertical(g1)
    c: Vertical(g3)
    c: DistanceX(g0,g0) = 3
    c: DistanceY(g0,g-1) = 88
    c: DistanceX(g2,g-1) = 173
    c: DistanceY(g0,g2) = 79
FEATURE [PartDesign::Pad] Pad020
  AddSubType = 0
  AlongSketchNormal = false
  AutoTaperInnerAngle = true
  BaseFeature = -> Pad019
  CheckUpToFaceLimits = true
  ClaimChildren = false
  Direction = (0,0,1)
  Fit = 0
  FitJoin = 0
  InnerFit = 0
  InnerFitJoin = 0
  InvalidShape = false
  Length = 6
  Length2 = 6
  Linearize = true
  NewSolid = false
  Profile = -> Sketch044
  Suppress = false
  TaperInnerAngle = 0
  TaperInnerAngleRev = 0
  TreeRank = 198
  Type = 4
  ValidateShape = true
  _ProfileBasedVersion = 1
  expr: Length = <<Parameters>>.thickness * 2
  expr: Length2 = <<Parameters>>.thickness * 2
FEATURE [PartDesign::Chamfer] Chamfer007
  AddSubType = 0
  Angle = 45
  Base = -> Pad020 [Edge65]
  BaseFeature = -> Pad020
  ChamferType = 0
  FlipDirection = false
  InvalidShape = false
  NewSolid = false
  Size = 2.99
  Size2 = 1
  SupportTransform = false
  Suppress = false
  TreeRank = 199
  ValidateShape = true
  expr: Size = <<Parameters>>.thickness - 0.01
FEATURE [PartDesign::Chamfer] Chamfer008
  AddSubType = 0
  Angle = 45
  Base = -> Chamfer007 [Edge85]
  BaseFeature = -> Chamfer007
  ChamferType = 0
  FlipDirection = false
  InvalidShape = false
  NewSolid = false
  Size = 1.5
  Size2 = 1
  SupportTransform = false
  Suppress = false
  TreeRank = 200
  ValidateShape = true
  expr: Size = <<Parameters>>.thickness / 2
FEATURE [PartDesign::Fillet] Fillet012
  AddSubType = 0
  Base = -> Chamfer008 [Edge40,Edge38,Edge33,Edge22]
  BaseFeature = -> Chamfer008
  InvalidShape = false
  NewSolid = false
  Radius = 3
  SupportTransform = false
  Suppress = false
  TreeRank = 201
  ValidateShape = true
  expr: Radius = <<Parameters>>.thickness
FEATURE [PartDesign::Fillet] Fillet013
  AddSubType = 0
  Base = -> Fillet012 [Face35,Face36,Edge87]
  BaseFeature = -> Fillet012
  InvalidShape = false
  NewSolid = false
  Radius = 1
  SupportTransform = false
  Suppress = false
  TreeRank = 202
  ValidateShape = true
FEATURE [Sketcher::SketchObject] Sketch045
  ArcFitTolerance = 1e-06
  AttachmentSupport = -> [XY_Plane008]
  ExternalBSplineMaxDegree = 5
  ExternalBSplineTolerance = 0.0001
  FullyConstrained = true
  InternalTolerance = 1e-06
  InvalidShape = false
  MakeInternals = false
  MapMode = 5
  Support = -> [XY_Plane008]
  TreeRank = 216
  ValidateShape = true
  expr: Constraints[0] = <<Parameters>>.station_diameter
  expr: Constraints[12] = <<Parameters>>.station_diameter + 2 * <<Parameters>>.thickness
  expr: Constraints[13] = <<Parameters>>.station_diameter
  expr: Constraints[14] = <<Parameters>>.station_diameter
  expr: Constraints[15] = <<Parameters>>.station_diameter
  expr: Constraints[16] = <<Parameters>>.station_diameter + 2 * <<Parameters>>.thickness
  expr: Constraints[17] = <<Parameters>>.station_diameter
  expr: Constraints[18] = <<Parameters>>.station_diameter
  expr: Constraints[19] = <<Parameters>>.station_diameter + 2 * <<Parameters>>.thickness
  expr: Constraints[20] = <<Parameters>>.station_diameter
  expr: Constraints[21] = <<Parameters>>.station_diameter
  expr: Constraints[22] = <<Parameters>>.station_diameter + 2 * <<Parameters>>.thickness
  expr: Constraints[51] = <<Parameters>>.motor_width
  sketch-geometry (75):
    g0: Circle [constr] CenterX=-130.5 CenterY=130.5 CenterZ=0 NormalX=0 NormalY=0 NormalZ=1 AngleXU=0 Radius=42.5
    g1: Circle [constr] CenterX=-130.5 CenterY=45.5 CenterZ=0 NormalX=0 NormalY=0 NormalZ=1 AngleXU=0 Radius=42.5
    g2: Circle [constr] CenterX=-45.5 CenterY=45.5 CenterZ=0 NormalX=0 NormalY=0 NormalZ=1 AngleXU=0 Radius=42.5
    g3: Circle [constr] CenterX=-45.5 CenterY=130.5 CenterZ=0 NormalX=0 NormalY=0 NormalZ=1 AngleXU=0 Radius=42.5
    g4: Circle [constr] CenterX=45.5 CenterY=130.5 CenterZ=0 NormalX=0 NormalY=0 NormalZ=1 AngleXU=0 Radius=42.5
    g5: Circle [constr] CenterX=130.5 CenterY=130.5 CenterZ=0 NormalX=0 NormalY=0 NormalZ=1 AngleXU=0 Radius=42.5
    g6: Circle [constr] CenterX=45.5 CenterY=45.5 CenterZ=0 NormalX=0 NormalY=0 NormalZ=1 AngleXU=0 Radius=42.5
    g7: Circle [constr] CenterX=130.5 CenterY=45.5 CenterZ=0 NormalX=0 NormalY=0 NormalZ=1 AngleXU=0 Radius=42.5
    g8: Circle [constr] CenterX=-130.5 CenterY=-45.5 CenterZ=0 NormalX=0 NormalY=0 NormalZ=1 AngleXU=0 Radius=42.5
    g9: Circle [constr] CenterX=-45.5 CenterY=-45.5 CenterZ=0 NormalX=0 NormalY=0 NormalZ=1 AngleXU=0 Radius=42.5
    g10: Circle [constr] CenterX=45.5 CenterY=-45.5 CenterZ=0 NormalX=0 NormalY=0 NormalZ=1 AngleXU=0 Radius=42.5
    g11: Circle [constr] CenterX=130.5 CenterY=-45.5 CenterZ=0 NormalX=0 NormalY=0 NormalZ=1 AngleXU=0 Radius=42.5
    g12: LineSegment [constr] StartX=-130.5 StartY=130.5 StartZ=0 EndX=130.5 EndY=130.5 EndZ=0
    g13: LineSegment [constr] StartX=-130.5 StartY=45.5 StartZ=0 EndX=130.5 EndY=45.5 EndZ=0
    g14: LineSegment [constr] StartX=-130.5 StartY=-45.5 StartZ=0 EndX=130.5 EndY=-45.5 EndZ=0
    g15: LineSegment StartX=-113 StartY=113 StartZ=0 EndX=-113 EndY=148 EndZ=0
    g16: LineSegment StartX=-113 StartY=148 StartZ=0 EndX=-148 EndY=148 EndZ=0
    g17: LineSegment StartX=-148 StartY=148 StartZ=0 EndX=-148 EndY=113 EndZ=0
    g18: LineSegment StartX=-148 StartY=113 StartZ=0 EndX=-113 EndY=113 EndZ=0
    g19: GeomPoint [constr] X=-130.5 Y=130.5 Z=0
    g20: LineSegment StartX=-28 StartY=113 StartZ=0 EndX=-28 EndY=148 EndZ=0
    g21: LineSegment StartX=-28 StartY=148 StartZ=0 EndX=-63 EndY=148 EndZ=0
    g22: LineSegment StartX=-63 StartY=148 StartZ=0 EndX=-63 EndY=113 EndZ=0
    g23: LineSegment StartX=-63 StartY=113 StartZ=0 EndX=-28 EndY=113 EndZ=0
    g24: GeomPoint [constr] X=-45.5 Y=130.5 Z=0
    g25: LineSegment StartX=63 StartY=113 StartZ=0 EndX=63 EndY=148 EndZ=0
    g26: LineSegment StartX=63 StartY=148 StartZ=0 EndX=28 EndY=148 EndZ=0
    g27: LineSegment StartX=28 StartY=148 StartZ=0 EndX=28 EndY=113 EndZ=0
    g28: LineSegment StartX=28 StartY=113 StartZ=0 EndX=63 EndY=113 EndZ=0
    g29: GeomPoint [constr] X=45.5 Y=130.5 Z=0
    g30: LineSegment StartX=148 StartY=113 StartZ=0 EndX=148 EndY=148 EndZ=0
    g31: LineSegment StartX=148 StartY=148 StartZ=0 EndX=113 EndY=148 EndZ=0
    g32: LineSegment StartX=113 StartY=148 StartZ=0 EndX=113 EndY=113 EndZ=0
    g33: LineSegment StartX=113 StartY=113 StartZ=0 EndX=148 EndY=113 EndZ=0
    g34: GeomPoint [constr] X=130.5 Y=130.5 Z=0
    g35: LineSegment StartX=-113 StartY=28 StartZ=0 EndX=-113 EndY=63 EndZ=0
    g36: LineSegment StartX=-113 StartY=63 StartZ=0 EndX=-148 EndY=63 EndZ=0
    g37: LineSegment StartX=-148 StartY=63 StartZ=0 EndX=-148 EndY=28 EndZ=0
    g38: LineSegment StartX=-148 StartY=28 StartZ=0 EndX=-113 EndY=28 EndZ=0
    g39: GeomPoint [constr] X=-130.5 Y=45.5 Z=0
    g40: LineSegment StartX=-28 StartY=28 StartZ=0 EndX=-28 EndY=63 EndZ=0
    g41: LineSegment StartX=-28 StartY=63 StartZ=0 EndX=-63 EndY=63 EndZ=0
    g42: LineSegment StartX=-63 StartY=63 StartZ=0 EndX=-63 EndY=28 EndZ=0
    g43: LineSegment StartX=-63 StartY=28 StartZ=0 EndX=-28 EndY=28 EndZ=0
    g44: GeomPoint [constr] X=-45.5 Y=45.5 Z=0
    g45: LineSegment StartX=63 StartY=28 StartZ=0 EndX=63 EndY=63 EndZ=0
    g46: LineSegment StartX=63 StartY=63 StartZ=0 EndX=28 EndY=63 EndZ=0
    g47: LineSegment StartX=28 StartY=63 StartZ=0 EndX=28 EndY=28 EndZ=0
    g48: LineSegment StartX=28 StartY=28 StartZ=0 EndX=63 EndY=28 EndZ=0
    g49: GeomPoint [constr] X=45.5 Y=45.5 Z=0
    g50: LineSegment StartX=148 StartY=28 StartZ=0 EndX=148 EndY=63 EndZ=0
    g51: LineSegment StartX=148 StartY=63 StartZ=0 EndX=113 EndY=63 EndZ=0
    g52: LineSegment StartX=113 StartY=63 StartZ=0 EndX=113 EndY=28 EndZ=0
    g53: LineSegment StartX=113 StartY=28 StartZ=0 EndX=148 EndY=28 EndZ=0
    g54: GeomPoint [constr] X=130.5 Y=45.5 Z=0
    g55: LineSegment StartX=-113 StartY=-63 StartZ=0 EndX=-113 EndY=-28 EndZ=0
    g56: LineSegment StartX=-113 StartY=-28 StartZ=0 EndX=-148 EndY=-28 EndZ=0
    g57: LineSegment StartX=-148 StartY=-28 StartZ=0 EndX=-148 EndY=-63 EndZ=0
    g58: LineSegment StartX=-148 StartY=-63 StartZ=0 EndX=-113 EndY=-63 EndZ=0
    g59: GeomPoint [constr] X=-130.5 Y=-45.5 Z=0
    g60: LineSegment StartX=-28 StartY=-63 StartZ=0 EndX=-28 EndY=-28 EndZ=0
    g61: LineSegment StartX=-28 StartY=-28 StartZ=0 EndX=-63 EndY=-28 EndZ=0
    g62: LineSegment StartX=-63 StartY=-28 StartZ=0 EndX=-63 EndY=-63 EndZ=0
    g63: LineSegment StartX=-63 StartY=-63 StartZ=0 EndX=-28 EndY=-63 EndZ=0
    g64: GeomPoint [constr] X=-45.5 Y=-45.5 Z=0
    g65: LineSegment StartX=63 StartY=-63 StartZ=0 EndX=63 EndY=-28 EndZ=0
    g66: LineSegment StartX=63 StartY=-28 StartZ=0 EndX=28 EndY=-28 EndZ=0
    g67: LineSegment StartX=28 StartY=-28 StartZ=0 EndX=28 EndY=-63 EndZ=0
    g68: LineSegment StartX=28 StartY=-63 StartZ=0 EndX=63 EndY=-63 EndZ=0
    g69: GeomPoint [constr] X=45.5 Y=-45.5 Z=0
    g70: LineSegment StartX=148 StartY=-63 StartZ=0 EndX=148 EndY=-28 EndZ=0
    g71: LineSegment StartX=148 StartY=-28 StartZ=0 EndX=113 EndY=-28 EndZ=0
    g72: LineSegment StartX=113 StartY=-28 StartZ=0 EndX=113 EndY=-63 EndZ=0
    g73: LineSegment StartX=113 StartY=-63 StartZ=0 EndX=148 EndY=-63 EndZ=0
    g74: GeomPoint [constr] X=130.5 Y=-45.5 Z=0
  constraints (180):
    c: Diameter(g0) = 85
    c: Equal(g0,g3)
    c: Equal(g0,g4)
    c: Equal(g0,g5)
    c: Equal(g0,g1)
    c: Equal(g0,g2)
    c: Equal(g0, g6-g11) x6
    c: DistanceX(g3,g4) = 91
    c: DistanceX(g0,g3) = 85
    c: DistanceX(g4,g5) = 85
    c: DistanceX(g1,g2) = 85
    c: DistanceX(g2,g6) = 91
    c: DistanceX(g6,g7) = 85
    c: DistanceX(g8,g9) = 85
    c: DistanceX(g9,g10) = 91
    c: DistanceX(g10,g11) = 85
    c: DistanceY(g1,g0) = 85
    c: DistanceY(g8,g1) = 91
    c: Coincident(g12,g0)
    c: Coincident(g12,g5)
    c: Horizontal(g12)
    c: PointOnObject(g3,g12)
    c: PointOnObject(g4,g12)
    c: Coincident(g13,g1)
    c: Coincident(g13,g7)
    c: Horizontal(g13)
    c: PointOnObject(g2,g13)
    c: PointOnObject(g6,g13)
    c: Coincident(g14,g8)
    c: Coincident(g14,g11)
    c: PointOnObject(g9,g14)
    c: PointOnObject(g10,g14)
    c: Horizontal(g14)
    c: DistanceX(g1,g0) = 0
    c: DistanceX(g1,g8) = 0
    c: Symmetric(g2,g10,g-1)
    c: Coincident(g15,g16)
    c: Coincident(g16,g17)
    c: Coincident(g17,g18)
    c: Coincident(g18,g15)
    c: Horizontal(g16)
    c: Horizontal(g18)
    c: Vertical(g15)
    c: Vertical(g17)
    c: Symmetric(g16,g15,g19)
    c: Coincident(g19,g0)
    c: DistanceX(g16,g15) = 35
    c: Equal(g16,g15)
    c: Coincident(g20,g21)
    c: Coincident(g21,g22)
    c: Coincident(g22,g23)
    c: Coincident(g23,g20)
    c: Horizontal(g21)
    c: Horizontal(g23)
    c: Vertical(g20)
    c: Vertical(g22)
    c: Symmetric(g21,g20,g24)
    c: Coincident(g24,g3)
    c: Coincident(g25,g26)
    c: Coincident(g26,g27)
    c: Coincident(g27,g28)
    c: Coincident(g28,g25)
    c: Horizontal(g26)
    c: Horizontal(g28)
    c: Vertical(g25)
    c: Vertical(g27)
    c: Symmetric(g26,g25,g29)
    c: Coincident(g29,g4)
    c: Coincident(g30,g31)
    c: Coincident(g31,g32)
    c: Coincident(g32,g33)
    c: Coincident(g33,g30)
    c: Horizontal(g31)
    c: Horizontal(g33)
    c: Vertical(g30)
    c: Vertical(g32)
    c: Symmetric(g31,g30,g34)
    c: Coincident(g34,g5)
    c: Coincident(g35,g36)
    c: Coincident(g36,g37)
    c: Coincident(g37,g38)
    c: Coincident(g38,g35)
    c: Horizontal(g36)
    c: Horizontal(g38)
    c: Vertical(g35)
    c: Vertical(g37)
    c: Symmetric(g36,g35,g39)
    c: Coincident(g39,g1)
    c: Coincident(g40,g41)
    c: Coincident(g41,g42)
    c: Coincident(g42,g43)
    c: Coincident(g43,g40)
    c: Horizontal(g41)
    c: Horizontal(g43)
    c: Vertical(g40)
    c: Vertical(g42)
    c: Symmetric(g41,g40,g44)
    c: Coincident(g44,g2)
    c: Coincident(g45,g46)
    c: Coincident(g46,g47)
    c: Coincident(g47,g48)
    c: Coincident(g48,g45)
    c: Horizontal(g46)
    c: Horizontal(g48)
    c: Vertical(g45)
    c: Vertical(g47)
    c: Symmetric(g46,g45,g49)
    c: Coincident(g49,g6)
    c: Coincident(g50,g51)
    c: Coincident(g51,g52)
    c: Coincident(g52,g53)
    c: Coincident(g53,g50)
    c: Horizontal(g51)
    c: Horizontal(g53)
    c: Vertical(g50)
    c: Vertical(g52)
    c: Symmetric(g51,g50,g54)
    c: Coincident(g54,g7)
    c: Coincident(g55,g56)
    c: Coincident(g56,g57)
    c: Coincident(g57,g58)
    c: Coincident(g58,g55)
    c: Horizontal(g56)
    c: Horizontal(g58)
    c: Vertical(g55)
    c: Vertical(g57)
    c: Symmetric(g56,g55,g59)
    c: Coincident(g59,g8)
    c: Coincident(g60,g61)
    c: Coincident(g61,g62)
    c: Coincident(g62,g63)
    c: Coincident(g63,g60)
    c: Horizontal(g61)
    c: Horizontal(g63)
    c: Vertical(g60)
    c: Vertical(g62)
    c: Symmetric(g61,g60,g64)
    c: Coincident(g64,g9)
    c: Coincident(g65,g66)
    c: Coincident(g66,g67)
    c: Coincident(g67,g68)
    c: Coincident(g68,g65)
    c: Horizontal(g66)
    c: Horizontal(g68)
    c: Vertical(g65)
    c: Vertical(g67)
    c: Symmetric(g66,g65,g69)
    c: Coincident(g69,g10)
    c: Coincident(g70,g71)
    c: Coincident(g71,g72)
    c: Coincident(g72,g73)
    c: Coincident(g73,g70)
    c: Horizontal(g71)
    c: Horizontal(g73)
    c: Vertical(g70)
    c: Vertical(g72)
    c: Symmetric(g71,g70,g74)
    c: Coincident(g74,g11)
    c: Equal(g16,g21)
    c: Equal(g16,g20)
    c: Equal(g16,g26)
    c: Equal(g16,g25)
    c: Equal(g16,g31)
    c: Equal(g16,g30)
    c: Equal(g16,g36)
    c: Equal(g16,g35)
    c: Equal(g16,g41)
    c: Equal(g16,g40)
    c: Equal(g16,g46)
    c: Equal(g16,g45)
    c: Equal(g16,g51)
    c: Equal(g16,g50)
    c: Equal(g16,g56)
    c: Equal(g16,g55)
    c: Equal(g16,g61)
    c: Equal(g16,g60)
    c: Equal(g16,g66)
    c: Equal(g16,g65)
    c: Equal(g16,g71)
    c: Equal(g16,g70)
FEATURE [PartDesign::Pad] Pad021
  AddSubType = 0
  AlongSketchNormal = false
  AutoTaperInnerAngle = true
  CheckUpToFaceLimits = true
  ClaimChildren = false
  Direction = (0,0,1)
  Fit = 0
  FitJoin = 0
  InnerFit = 0
  InnerFitJoin = 0
  InvalidShape = false
  Length = 30
  Length2 = 100
  Linearize = true
  NewSolid = false
  Profile = -> Sketch045
  Reversed = true
  Suppress = false
  TaperInnerAngle = 0
  TaperInnerAngleRev = 0
  TreeRank = 217
  Type = 0
  ValidateShape = true
  _ProfileBasedVersion = 1
  expr: Length = <<Parameters>>.motor_height
FEATURE [Sketcher::SketchObject] Sketch046
  ArcFitTolerance = 1e-06
  AttachmentSupport = -> [XY_Plane008]
  ExternalBSplineMaxDegree = 5
  ExternalBSplineTolerance = 0.0001
  FullyConstrained = true
  InternalTolerance = 1e-06
  InvalidShape = false
  MakeInternals = false
  MapMode = 5
  Support = -> [XY_Plane008]
  TreeRank = 218
  ValidateShape = true
  expr: Constraints[0] = <<Parameters>>.station_diameter
  expr: Constraints[12] = <<Parameters>>.station_diameter + 2 * <<Parameters>>.thickness
  expr: Constraints[13] = <<Parameters>>.station_diameter
  expr: Constraints[14] = <<Parameters>>.station_diameter
  expr: Constraints[15] = <<Parameters>>.station_diameter
  expr: Constraints[16] = <<Parameters>>.station_diameter + 2 * <<Parameters>>.thickness
  expr: Constraints[17] = <<Parameters>>.station_diameter
  expr: Constraints[18] = <<Parameters>>.station_diameter
  expr: Constraints[19] = <<Parameters>>.station_diameter + 2 * <<Parameters>>.thickness
  expr: Constraints[20] = <<Parameters>>.station_diameter
  expr: Constraints[21] = <<Parameters>>.station_diameter
  expr: Constraints[22] = <<Parameters>>.station_diameter + 2 * <<Parameters>>.thickness
  expr: Constraints[64] = <<Parameters>>.motor_shaft_diameter
  sketch-geometry (27):
    g0: Circle [constr] CenterX=-130.5 CenterY=130.5 CenterZ=0 NormalX=0 NormalY=0 NormalZ=1 AngleXU=0 Radius=42.5
    g1: Circle [constr] CenterX=-130.5 CenterY=45.5 CenterZ=0 NormalX=0 NormalY=0 NormalZ=1 AngleXU=0 Radius=42.5
    g2: Circle [constr] CenterX=-45.5 CenterY=45.5 CenterZ=0 NormalX=0 NormalY=0 NormalZ=1 AngleXU=0 Radius=42.5
    g3: Circle [constr] CenterX=-45.5 CenterY=130.5 CenterZ=0 NormalX=0 NormalY=0 NormalZ=1 AngleXU=0 Radius=42.5
    g4: Circle [constr] CenterX=45.5 CenterY=130.5 CenterZ=0 NormalX=0 NormalY=0 NormalZ=1 AngleXU=0 Radius=42.5
    g5: Circle [constr] CenterX=130.5 CenterY=130.5 CenterZ=0 NormalX=0 NormalY=0 NormalZ=1 AngleXU=0 Radius=42.5
    g6: Circle [constr] CenterX=45.5 CenterY=45.5 CenterZ=0 NormalX=0 NormalY=0 NormalZ=1 AngleXU=0 Radius=42.5
    g7: Circle [constr] CenterX=130.5 CenterY=45.5 CenterZ=0 NormalX=0 NormalY=0 NormalZ=1 AngleXU=0 Radius=42.5
    g8: Circle [constr] CenterX=-130.5 CenterY=-45.5 CenterZ=0 NormalX=0 NormalY=0 NormalZ=1 AngleXU=0 Radius=42.5
    g9: Circle [constr] CenterX=-45.5 CenterY=-45.5 CenterZ=0 NormalX=0 NormalY=0 NormalZ=1 AngleXU=0 Radius=42.5
    g10: Circle [constr] CenterX=45.5 CenterY=-45.5 CenterZ=0 NormalX=0 NormalY=0 NormalZ=1 AngleXU=0 Radius=42.5
    g11: Circle [constr] CenterX=130.5 CenterY=-45.5 CenterZ=0 NormalX=0 NormalY=0 NormalZ=1 AngleXU=0 Radius=42.5
    g12: LineSegment [constr] StartX=-130.5 StartY=130.5 StartZ=0 EndX=130.5 EndY=130.5 EndZ=0
    g13: LineSegment [constr] StartX=-130.5 StartY=45.5 StartZ=0 EndX=130.5 EndY=45.5 EndZ=0
    g14: LineSegment [constr] StartX=-130.5 StartY=-45.5 StartZ=0 EndX=130.5 EndY=-45.5 EndZ=0
    g15: Circle CenterX=-130.5 CenterY=130.5 CenterZ=0 NormalX=0 NormalY=0 NormalZ=1 AngleXU=0 Radius=2.5
    g16: Circle CenterX=-45.5 CenterY=130.5 CenterZ=0 NormalX=0 NormalY=0 NormalZ=1 AngleXU=0 Radius=2.5
    g17: Circle CenterX=45.5 CenterY=130.5 CenterZ=0 NormalX=0 NormalY=0 NormalZ=1 AngleXU=0 Radius=2.5
    g18: Circle CenterX=130.5 CenterY=130.5 CenterZ=0 NormalX=0 NormalY=0 NormalZ=1 AngleXU=0 Radius=2.5
    g19: Circle CenterX=-130.5 CenterY=45.5 CenterZ=0 NormalX=0 NormalY=0 NormalZ=1 AngleXU=0 Radius=2.5
    g20: Circle CenterX=-45.5 CenterY=45.5 CenterZ=0 NormalX=0 NormalY=0 NormalZ=1 AngleXU=0 Radius=2.5
    g21: Circle CenterX=45.5 CenterY=45.5 CenterZ=0 NormalX=0 NormalY=0 NormalZ=1 AngleXU=0 Radius=2.5
    g22: Circle CenterX=130.5 CenterY=45.5 CenterZ=0 NormalX=0 NormalY=0 NormalZ=1 AngleXU=0 Radius=2.5
    g23: Circle CenterX=-130.5 CenterY=-45.5 CenterZ=0 NormalX=0 NormalY=0 NormalZ=1 AngleXU=0 Radius=2.5
    g24: Circle CenterX=-45.5 CenterY=-45.5 CenterZ=0 NormalX=0 NormalY=0 NormalZ=1 AngleXU=0 Radius=2.5
    g25: Circle CenterX=45.5 CenterY=-45.5 CenterZ=0 NormalX=0 NormalY=0 NormalZ=1 AngleXU=0 Radius=2.5
    g26: Circle CenterX=130.5 CenterY=-45.5 CenterZ=0 NormalX=0 NormalY=0 NormalZ=1 AngleXU=0 Radius=2.5
  constraints (50):
    c: Diameter(g0) = 85
    c: Equal(g0,g3)
    c: Equal(g0,g4)
    c: Equal(g0,g5)
    c: Equal(g0,g1)
    c: Equal(g0,g2)
    c: Equal(g0, g6-g11) x6
    c: DistanceX(g3,g4) = 91
    c: DistanceX(g0,g3) = 85
    c: DistanceX(g4,g5) = 85
    c: DistanceX(g1,g2) = 85
    c: DistanceX(g2,g6) = 91
    c: DistanceX(g6,g7) = 85
    c: DistanceX(g8,g9) = 85
    c: DistanceX(g9,g10) = 91
    c: DistanceX(g10,g11) = 85
    c: DistanceY(g1,g0) = 85
    c: DistanceY(g8,g1) = 91
    c: Coincident(g12,g0)
    c: Coincident(g12,g5)
    c: Horizontal(g12)
    c: PointOnObject(g3,g12)
    c: PointOnObject(g4,g12)
    c: Coincident(g13,g1)
    c: Coincident(g13,g7)
    c: Horizontal(g13)
    c: PointOnObject(g2,g13)
    c: PointOnObject(g6,g13)
    c: Coincident(g14,g8)
    c: Coincident(g14,g11)
    c: PointOnObject(g9,g14)
    c: PointOnObject(g10,g14)
    c: Horizontal(g14)
    c: DistanceX(g1,g0) = 0
    c: DistanceX(g1,g8) = 0
    c: Symmetric(g2,g10,g-1)
    c: Coincident(g15,g0)
    c: Coincident(g16,g3)
    c: Coincident(g17,g4)
    c: Coincident(g18,g5)
    c: Coincident(g19,g1)
    c: Coincident(g20,g2)
    c: Coincident(g21,g6)
    c: Coincident(g22,g7)
    c: Coincident(g23,g8)
    c: Coincident(g24,g9)
    c: Coincident(g25,g10)
    c: Coincident(g26,g11)
    c: Equal(g15, g16-g26) x11
    c: Diameter(g15) = 5
FEATURE [PartDesign::Pad] Pad022
  AddSubType = 0
  AlongSketchNormal = false
  AutoTaperInnerAngle = true
  BaseFeature = -> Pad021
  CheckUpToFaceLimits = true
  ClaimChildren = false
  Direction = (0,0,1)
  Fit = 0
  FitJoin = 0
  InnerFit = 0
  InnerFitJoin = 0
  InvalidShape = false
  Length = 19
  Length2 = 100
  Linearize = true
  NewSolid = false
  Profile = -> Sketch046
  Suppress = false
  TaperAngle = 48
  TaperInnerAngle = -48
  TaperInnerAngleRev = 0
  TreeRank = 219
  Type = 0
  ValidateShape = true
  _ProfileBasedVersion = 1
  expr: Length = <<Parameters>>.motor_shaft_length
FEATURE [PartDesign::Body] Body008  label="Motors"
  AutoGroupSolids = false
  ClaimAllChildren = false
  ExportMode = 0
  Group = -> [Sketch045,Pad021,Sketch046,Pad022]
  InvalidShape = false
  Origin = -> Origin008
  Tip = -> Pad022
  TreeRank = 215
  ValidateShape = true
  _ExportChildren = -> [Pad021,Pad022]
  _GroupVersion = 1
FEATURE [Sketcher::SketchObject] Sketch047
  ArcFitTolerance = 1e-06
  AttachmentOffset = pos=(0,0,-22) rot=(0,0,1;0rad)
  AttachmentSupport = -> [XY_Plane009]
  ExternalBSplineMaxDegree = 5
  ExternalBSplineTolerance = 0.0001
  FullyConstrained = false
  InternalTolerance = 1e-06
  InvalidShape = false
  MakeInternals = false
  MapMode = 5
  Placement = pos=(0,0,-22) rot=(0,0,1;0rad)
  Support = -> [XY_Plane009]
  TreeRank = 230
  ValidateShape = true
  expr: AttachmentOffset.Base.z = -<<Parameters>>.motor_height + <<Parameters>>.psu_screw_length
  expr: Constraints[7] = <<Parameters>>.psu_width
  expr: Constraints[8] = <<Parameters>>.psu_length
  sketch-geometry (4):
    g0: LineSegment StartX=-25 StartY=157.687 StartZ=0 EndX=25 EndY=157.687 EndZ=0
    g1: LineSegment StartX=25 StartY=157.687 StartZ=0 EndX=25 EndY=18.6867 EndZ=0
    g2: LineSegment StartX=25 StartY=18.6867 StartZ=0 EndX=-25 EndY=18.6867 EndZ=0
    g3: LineSegment StartX=-25 StartY=18.6867 StartZ=0 EndX=-25 EndY=157.687 EndZ=0
  constraints (10):
    c: Coincident(g0,g1)
    c: Coincident(g1,g2)
    c: Coincident(g2,g3)
    c: Coincident(g3,g0)
    c: Horizontal(g2)
    c: Vertical(g1)
    c: Vertical(g3)
    c: DistanceX(g0,g0) = 50
    c: DistanceY(g1,g0) = 139
    c: Symmetric(g0,g0,g-2)
FEATURE [PartDesign::Pad] Pad023
  AddSubType = 0
  AlongSketchNormal = false
  AutoTaperInnerAngle = true
  CheckUpToFaceLimits = true
  ClaimChildren = false
  Direction = (0,0,1)
  Fit = 0
  FitJoin = 0
  InnerFit = 0
  InnerFitJoin = 0
  InvalidShape = false
  Length = 22.25
  Length2 = 100
  Linearize = true
  NewSolid = false
  Profile = -> Sketch047
  Suppress = false
  TaperInnerAngle = 0
  TaperInnerAngleRev = 0
  TreeRank = 231
  Type = 0
  ValidateShape = true
  _ProfileBasedVersion = 1
  expr: Length = <<Parameters>>.psu_height
FEATURE [PartDesign::Body] Body009  label="Power Supply"
  AutoGroupSolids = false
  ClaimAllChildren = false
  ExportMode = 0
  Group = -> [Sketch047,Pad023]
  InvalidShape = false
  Origin = -> Origin009
  Tip = -> Pad023
  TreeRank = 229
  ValidateShape = true
  _ExportChildren = -> [Pad023]
  _GroupVersion = 1
FEATURE [Sketcher::SketchObject] Sketch048
  ArcFitTolerance = 1e-06
  AttachmentSupport = -> [XY_Plane010]
  ExternalBSplineMaxDegree = 5
  ExternalBSplineTolerance = 0.0001
  FullyConstrained = true
  InternalTolerance = 1e-06
  InvalidShape = false
  MakeInternals = false
  MapMode = 5
  Support = -> [XY_Plane010]
  TreeRank = 157
  ValidateShape = true
  expr: Constraints[10] = <same value as first occurrence — deduplicated (x4 in doc)>
  expr: Constraints[11] = <<Parameters>>.thickness * 4 - 2 * <<Parameters>>.clearance
  sketch-geometry (5):
    g0: LineSegment StartX=5.6 StartY=-69.1 StartZ=0 EndX=5.6 EndY=69.1 EndZ=0
    g1: LineSegment StartX=5.6 StartY=69.1 StartZ=0 EndX=-5.6 EndY=69.1 EndZ=0
    g2: LineSegment StartX=-5.6 StartY=69.1 StartZ=0 EndX=-5.6 EndY=-69.1 EndZ=0
    g3: LineSegment StartX=-5.6 StartY=-69.1 StartZ=0 EndX=5.6 EndY=-69.1 EndZ=0
    g4: GeomPoint [constr] X=0 Y=0 Z=0
  constraints (12):
    c: Coincident(g0,g1)
    c: Coincident(g1,g2)
    c: Coincident(g2,g3)
    c: Coincident(g3,g0)
    c: Horizontal(g1)
    c: Horizontal(g3)
    c: Vertical(g0)
    c: Vertical(g2)
    c: Symmetric(g1,g0,g4)
    c: Coincident(g4,g-1)
    c: DistanceY(g0,g0) = 138.2
    c: DistanceX(g1,g0) = 11.2
FEATURE [PartDesign::Pad] Pad024
  AddSubType = 0
  AlongSketchNormal = false
  AutoTaperInnerAngle = true
  CheckUpToFaceLimits = true
  ClaimChildren = false
  Direction = (0,0,1)
  Fit = 0
  FitJoin = 0
  InnerFit = 0
  InnerFitJoin = 0
  InvalidShape = false
  Length = 1
  Length2 = 100
  Linearize = true
  NewSolid = false
  Profile = -> Sketch048
  Reversed = true
  Suppress = false
  TaperInnerAngle = 0
  TaperInnerAngleRev = 0
  TreeRank = 242
  Type = 0
  ValidateShape = true
  _ProfileBasedVersion = 1
  expr: Length = <<Parameters>>.lap_join_thickness
FEATURE [PartDesign::Fillet] Fillet014
  AddSubType = 0
  Base = -> Pad024 [Edge5,Edge2,Edge8,Edge1]
  BaseFeature = -> Pad024
  InvalidShape = false
  NewSolid = false
  Radius = 1
  SupportTransform = false
  Suppress = false
  TreeRank = 241
  ValidateShape = true
FEATURE [Sketcher::SketchObject] Sketch049
  ArcFitTolerance = 1e-06
  AttachmentSupport = -> [XY_Plane010]
  ExternalBSplineMaxDegree = 5
  ExternalBSplineTolerance = 0.0001
  FullyConstrained = true
  InternalTolerance = 1e-06
  InvalidShape = false
  MakeInternals = false
  MapMode = 5
  Support = -> [XY_Plane010]
  TreeRank = 243
  ValidateShape = true
  expr: Constraints[10] = <<Parameters>>.psu_width
  expr: Constraints[11] = <<Parameters>>.psu_length
  sketch-geometry (5):
    g0: LineSegment StartX=25 StartY=-69.5 StartZ=0 EndX=25 EndY=69.5 EndZ=0
    g1: LineSegment StartX=25 StartY=69.5 StartZ=0 EndX=-25 EndY=69.5 EndZ=0
    g2: LineSegment StartX=-25 StartY=69.5 StartZ=0 EndX=-25 EndY=-69.5 EndZ=0
    g3: LineSegment StartX=-25 StartY=-69.5 StartZ=0 EndX=25 EndY=-69.5 EndZ=0
    g4: GeomPoint [constr] X=0 Y=0 Z=0
  constraints (12):
    c: Coincident(g0,g1)
    c: Coincident(g1,g2)
    c: Coincident(g2,g3)
    c: Coincident(g3,g0)
    c: Horizontal(g1)
    c: Horizontal(g3)
    c: Vertical(g0)
    c: Vertical(g2)
    c: Symmetric(g1,g0,g4)
    c: Coincident(g4,g-1)
    c: DistanceX(g1,g0) = 50
    c: DistanceY(g0,g0) = 139
FEATURE [PartDesign::Pad] Pad025
  AddSubType = 0
  AlongSketchNormal = false
  AutoTaperInnerAngle = true
  BaseFeature = -> Fillet014
  CheckUpToFaceLimits = true
  ClaimChildren = false
  Direction = (0,0,1)
  Fit = 0
  FitJoin = 0
  InnerFit = 0
  InnerFitJoin = 0
  InvalidShape = false
  Length = 8
  Length2 = 100
  Linearize = true
  NewSolid = false
  Profile = -> Sketch049
  Suppress = false
  TaperInnerAngle = 0
  TaperInnerAngleRev = 0
  TreeRank = 244
  Type = 0
  ValidateShape = true
  _ProfileBasedVersion = 1
  expr: Length = <<Parameters>>.psu_screw_length
FEATURE [Sketcher::SketchObject] Sketch050
  ArcFitTolerance = 1e-06
  AttachmentSupport = -> [XY_Plane010]
  ExternalBSplineMaxDegree = 5
  ExternalBSplineTolerance = 0.0001
  FullyConstrained = true
  InternalTolerance = 1e-06
  InvalidShape = false
  MakeInternals = false
  MapMode = 5
  Support = -> [XY_Plane010]
  TreeRank = 245
  ValidateShape = true
  expr: Constraints[0] = <<Parameters>>.psu_screw_x_offset
  expr: Constraints[1] = <<Parameters>>.psu_screw_y_offset
  sketch-geometry (3):
    g0: Circle CenterX=16 CenterY=65.5 CenterZ=0 NormalX=0 NormalY=0 NormalZ=1 AngleXU=0 Radius=2
    g1: Circle CenterX=-16 CenterY=-65.5 CenterZ=0 NormalX=0 NormalY=0 NormalZ=1 AngleXU=0 Radius=2
    g2: LineSegment [constr] StartX=16 StartY=65.5 StartZ=0 EndX=-16 EndY=-65.5 EndZ=0
  constraints (7):
    c: DistanceX(g1,g0) = 32
    c: DistanceY(g1,g0) = 131
    c: Coincident(g2,g0)
    c: Coincident(g2,g1)
    c: Symmetric(g0,g1,g-1)
    c: Equal(g0,g1)
    c: Diameter(g0) = 4
FEATURE [PartDesign::Hole] Hole
  AddSubType = 1
  BaseFeature = -> Pad025
  ClaimChildren = false
  CustomThreadClearance = 0
  Depth = 8
  DepthType = 0
  Diameter = 3.322
  DrillForDepth = false
  DrillPoint = 0
  DrillPointAngle = 118
  Fit = 0
  FitJoin = 0
  HoleCutCountersinkAngle = 90
  HoleCutCustomValues = false
  HoleCutDepth = 0
  HoleCutDiameter = 6.1
  HoleCutType = 0
  InnerFit = 0
  InnerFitJoin = 0
  InvalidShape = false
  Linearize = true
  ModelThread = true
  NewSolid = false
  Profile = -> Sketch050
  Reversed = true
  Suppress = false
  Tapered = false
  TaperedAngle = 90
  ThreadClass = 0
  ThreadDepth = 8
  ThreadDepthType = 0
  ThreadDirection = 0
  ThreadFit = 0
  ThreadSize = 11
  ThreadType = 1
  Threaded = true
  TreeRank = 246
  UseCustomThreadClearance = false
  ValidateShape = true
  _ProfileBasedVersion = 1
  expr: Depth = <<Parameters>>.psu_screw_length
FEATURE [PartDesign::Fillet] Fillet015
  AddSubType = 0
  Base = -> Hole [Edge38,Edge35,Edge36,Edge40,Edge41,Edge42,Edge37,Edge39]
  BaseFeature = -> Hole
  InvalidShape = false
  NewSolid = false
  Radius = 1
  SupportTransform = false
  Suppress = false
  TreeRank = 247
  ValidateShape = true
FEATURE [PartDesign::Body] Body010  label="Power Supply Glue-in Mount"
  AutoGroupSolids = false
  ClaimAllChildren = false
  ExportMode = 0
  Group = -> [Pad024,Fillet014,Sketch048,Sketch049,Pad025,Sketch050,Hole,Fillet015]
  InvalidShape = false
  Origin = -> Origin010
  Tip = -> Fillet015
  TreeRank = 32
  ValidateShape = true
  _ExportChildren = -> [Pad024,Fillet014,Pad025,Hole,Fillet015]
  _GroupVersion = 1
FEATURE [Sketcher::SketchObject] Sketch052
  ArcFitTolerance = 1e-06
  AttachmentSupport = -> [YZ_Plane011]
  ExternalBSplineMaxDegree = 5
  ExternalBSplineTolerance = 0.0001
  FullyConstrained = false
  InternalTolerance = 1e-06
  InvalidShape = false
  MakeInternals = false
  MapMode = 5
  Placement = pos=(0,0,0) rot=(0.57735,0.57735,0.57735;2.0944rad)
  Support = -> [YZ_Plane011]
  TreeRank = 176
  ValidateShape = true
  expr: Constraints[12] = <<Parameters>>.thickness + <<Parameters>>.motor_screw_head_height
  expr: Constraints[13] = <<Parameters>>.motor_height
  expr: Constraints[14] = <<Parameters>>.thickness
  expr: Constraints[18] = <<Parameters>>.screen_body_thickness
  expr: Constraints[19] = (<<Parameters>>.station_diameter + <<Parameters>>.thickness) * 2
  expr: Constraints[20] = <<Parameters>>.screen_angle
  expr: Constraints[21] = <<Parameters>>.thickness
  expr: Constraints[25] = <<Parameters>>.thickness
  expr: Constraints[26] = <<Parameters>>.motor_shaft_length
  expr: Constraints[27] = <<Parameters>>.station_diameter + <<Parameters>>.thickness
  expr: Constraints[31] = <<Parameters>>.screen_overall_height + 2 * <<Parameters>>.thickness
  sketch-geometry (14):
    g0: LineSegment StartX=0 StartY=-36.25 StartZ=0 EndX=-176 EndY=-36.25 EndZ=0
    g1: LineSegment StartX=0 StartY=-36.25 StartZ=0 EndX=0 EndY=-30 EndZ=0
    g2: LineSegment StartX=0 StartY=-30 StartZ=0 EndX=-173 EndY=-30 EndZ=0
    g3: LineSegment StartX=-176 StartY=-36.25 StartZ=0 EndX=-176 EndY=-22.2218 EndZ=0
    g4: LineSegment StartX=-176 StartY=-22.2218 StartZ=0 EndX=-106.178 EndY=47.5998 EndZ=0
    g5: LineSegment StartX=-173 StartY=-30 StartZ=0 EndX=-173 EndY=-27 EndZ=0
    g6: LineSegment StartX=-173 StartY=-27 StartZ=0 EndX=-102.289 EndY=43.7107 EndZ=0
    g7: LineSegment [constr] StartX=-145.835 StartY=0.164789 StartZ=0 EndX=-149.724 EndY=4.05388 EndZ=0
    g8: LineSegment StartX=-88 StartY=22 StartZ=0 EndX=-96.7893 EndY=22 EndZ=0
    g9: LineSegment StartX=-88 StartY=22 StartZ=0 EndX=-88 EndY=19 EndZ=0
    g10: LineSegment StartX=-102.289 StartY=19 StartZ=0 EndX=-88 EndY=19 EndZ=0
    g11: LineSegment StartX=-102.289 StartY=43.7107 StartZ=0 EndX=-102.289 EndY=19 EndZ=0
    g12: LineSegment StartX=-96.7893 StartY=43.7107 StartZ=0 EndX=-96.7893 EndY=22 EndZ=0
    g13: ArcOfCircle CenterX=-102.289 CenterY=43.7107 CenterZ=0 NormalX=0 NormalY=0 NormalZ=1 AngleXU=0 Radius=5.5 StartAngle=-7.327e-13 EndAngle=2.35619
  constraints (40):
    c: PointOnObject(g0,g-2)
    c: Horizontal(g0)
    c: Coincident(g1,g0)
    c: PointOnObject(g1,g-2)
    c: Coincident(g2,g1)
    c: Horizontal(g2)
    c: Coincident(g3,g0)
    c: Vertical(g3)
    c: Coincident(g4,g3)
    c: Coincident(g5,g2)
    c: Vertical(g5)
    c: Coincident(g6,g5)
    c: DistanceY(g0,g1) = 6.25
    c: DistanceY(g1,g-1) = 30
    c: DistanceX(g0,g2) = 3
    c: Parallel(g6,g4)
    c: PointOnObject(g7,g6)
    c: Perpendicular(g4,g7)
    c: Distance(g7,g7) = 5.5
    c: DistanceX(g0,g-1) = 176
    c: Angle(g5,g6) = 2.35619
    c: DistanceY(g2,g5) = 3
    c: Horizontal(g8)
    c: Coincident(g9,g8)
    c: Vertical(g9)
    c: DistanceY(g9,g8) = 3
    c: DistanceY(g-1,g9) = 19
    c: DistanceX(g9,g-1) = 88
    c: PointOnObject(g7,g4)
    c: Coincident(g10,g9)
    c: Horizontal(g10)
    c: Distance(g6,g5) = 100
    c: Coincident(g11,g6)
    c: Coincident(g11,g10)
    c: Vertical(g11)
    c: Coincident(g12,g8)
    c: Vertical(g12)
    c: Tangent(g4,g13) = 1.5708
    c: Tangent(g12,g13) = 1.5708
    c: Coincident(g13,g6)
FEATURE [PartDesign::Pad] Pad026
  AddSubType = 0
  AlongSketchNormal = false
  AutoTaperInnerAngle = true
  CheckUpToFaceLimits = true
  ClaimChildren = false
  Direction = (1,-2e-16,3e-16)
  Fit = 0
  FitJoin = 0
  InnerFit = 0
  InnerFitJoin = 0
  InvalidShape = false
  Length = 176
  Length2 = 100
  Linearize = true
  NewSolid = false
  Profile = -> Sketch052
  Suppress = false
  TaperInnerAngle = 0
  TaperInnerAngleRev = 0
  TreeRank = 259
  Type = 0
  ValidateShape = true
  _ProfileBasedVersion = 1
  expr: Length = (<<Parameters>>.station_diameter + <<Parameters>>.thickness) * 2
FEATURE [Sketcher::SketchObject] Sketch053
  ArcFitTolerance = 1e-06
  AttachmentSupport = -> [XY_Plane011]
  ExternalBSplineMaxDegree = 5
  ExternalBSplineTolerance = 0.0001
  FullyConstrained = true
  InternalTolerance = 1e-06
  InvalidShape = false
  MakeInternals = false
  MapMode = 5
  Support = -> [XY_Plane011]
  TreeRank = 178
  ValidateShape = true
  expr: Constraints[12] = <<Parameters>>.motor_shaft_mount_diameter / 4
  expr: Constraints[19] = <<Parameters>>.motor_shaft_mount_diameter / 4
  expr: Constraints[1] = <<Parameters>>.motor_shaft_mount_diameter / 4
  expr: Constraints[20] = <<Parameters>>.thickness
  expr: Constraints[21] = (<<Parameters>>.station_diameter + <<Parameters>>.thickness) * 2
  expr: Constraints[22] = <<Parameters>>.station_diameter / 3
  expr: Constraints[23] = (<<Parameters>>.station_diameter + <<Parameters>>.thickness) * 2
  expr: Constraints[28] = <<Parameters>>.thickness
  expr: Constraints[29] = <<Parameters>>.station_diameter / 3 / 2
  expr: Constraints[2] = <<Parameters>>.station_diameter + <<Parameters>>.thickness
  expr: Constraints[32] = <<Parameters>>.motor_shaft_mount_diameter / 4
  expr: Constraints[7] = <<Parameters>>.station_diameter + <<Parameters>>.thickness
  sketch-geometry (11):
    g0: Circle CenterX=88 CenterY=-88 CenterZ=0 NormalX=0 NormalY=0 NormalZ=1 AngleXU=0 Radius=6.25
    g1: ArcOfCircle CenterX=0 CenterY=0 CenterZ=0 NormalX=0 NormalY=0 NormalZ=1 AngleXU=0 Radius=12.5 StartAngle=4.71239 EndAngle=6.28319
    g2: LineSegment StartX=0 StartY=-12.5 StartZ=0 EndX=0 EndY=0 EndZ=0
    g3: LineSegment StartX=0 StartY=0 StartZ=0 EndX=12.5 EndY=0 EndZ=0
    g4: LineSegment StartX=176 StartY=0 StartZ=0 EndX=176 EndY=-176 EndZ=0
    g5: ArcOfCircle CenterX=169.75 CenterY=0 CenterZ=0 NormalX=0 NormalY=0 NormalZ=1 AngleXU=0 Radius=6.25 StartAngle=3.14159 EndAngle=5.25924
    g6: LineSegment StartX=163.5 StartY=0 StartZ=0 EndX=176 EndY=0 EndZ=0
    g7: LineSegment StartX=173 StartY=-5.33854 StartZ=0 EndX=173 EndY=-159.155 EndZ=0
    g8: ArcOfCircle CenterX=158.833 CenterY=-159.155 CenterZ=0 NormalX=0 NormalY=0 NormalZ=1 AngleXU=0 Radius=14.1667 StartAngle=4.92577 EndAngle=6.28319
    g9: LineSegment StartX=176 StartY=-176 StartZ=0 EndX=161.833 EndY=-176 EndZ=0
    g10: LineSegment StartX=161.833 StartY=-176 StartZ=0 EndX=161.833 EndY=-173 EndZ=0
  constraints (33):
    c: Coincident(g1,g-1)
    c: Radius(g1) = 12.5
    c: DistanceY(g0,g1) = 88
    c: Coincident(g2,g1)
    c: Coincident(g3,g1)
    c: Coincident(g1,g3)
    c: Coincident(g1,g2)
    c: DistanceX(g1,g0) = 88
    c: PointOnObject(g1,g-1)
    c: Vertical(g2)
    c: PointOnObject(g4,g-1)
    c: Vertical(g4)
    c: Diameter(g5) = 12.5
    c: Horizontal(g6)
    c: PointOnObject(g5,g6)
    c: Coincident(g6,g4)
    c: Coincident(g5,g6)
    c: Vertical(g7)
    c: Coincident(g5,g7)
    c: DistanceX(g5,g4) = 12.5
    c: DistanceX(g5,g4) = 3
    c: DistanceX(g1,g4) = 176
    c: Diameter(g8) = 28.3333
    c: DistanceY(g4,g4) = 176
    c: Coincident(g9,g4)
    c: Horizontal(g9)
    c: Coincident(g10,g9)
    c: Vertical(g10)
    c: DistanceY(g9,g10) = 3
    c: DistanceX(g9,g4) = 14.1667
    c: Tangent(g8,g7) = 1.5708
    c: Coincident(g8,g10)
    c: Diameter(g0) = 12.5
FEATURE [PartDesign::Pad] Pad027
  AddSubType = 0
  AlongSketchNormal = false
  AutoTaperInnerAngle = true
  BaseFeature = -> Pad026
  CheckUpToFaceLimits = true
  ClaimChildren = false
  Direction = (0,0,1)
  Fit = 0
  FitJoin = 0
  InnerFit = 0
  InnerFitJoin = 0
  InvalidShape = false
  Length = 30
  Length2 = 100
  Linearize = true
  NewSolid = false
  Profile = -> Sketch053
  Reversed = true
  Suppress = false
  TaperInnerAngle = 0
  TaperInnerAngleRev = 0
  TreeRank = 260
  Type = 0
  ValidateShape = true
  _ProfileBasedVersion = 1
  expr: Length = <<Parameters>>.motor_height
FEATURE [Sketcher::SketchObject] Sketch054
  ArcFitTolerance = 1e-06
  AttachmentSupport = -> [XY_Plane011]
  ExternalBSplineMaxDegree = 5
  ExternalBSplineTolerance = 0.0001
  FullyConstrained = true
  InternalTolerance = 1e-06
  InvalidShape = false
  MakeInternals = false
  MapMode = 5
  Support = -> [XY_Plane011]
  TreeRank = 180
  ValidateShape = true
  expr: Constraints[0] = <<Parameters>>.station_diameter + <<Parameters>>.thickness
  expr: Constraints[1] = <<Parameters>>.motor_shaft_mount_diameter / 4
  expr: Constraints[6] = <<Parameters>>.station_diameter + <<Parameters>>.thickness
  sketch-geometry (2):
    g0: ArcOfCircle CenterX=88 CenterY=-88 CenterZ=0 NormalX=0 NormalY=0 NormalZ=1 AngleXU=0 Radius=6.25 StartAngle=3.14159 EndAngle=6.28319
    g1: LineSegment StartX=81.75 StartY=-88 StartZ=0 EndX=94.25 EndY=-88 EndZ=0
  constraints (7):
    c: DistanceY(g0,g-1) = 88
    c: Diameter(g0) = 12.5
    c: Horizontal(g1)
    c: PointOnObject(g0,g1)
    c: Coincident(g0,g1)
    c: Coincident(g0,g1)
    c: DistanceX(g-1,g0) = 88
FEATURE [PartDesign::Pad] Pad028
  AddSubType = 0
  AlongSketchNormal = false
  AutoTaperInnerAngle = true
  BaseFeature = -> Pad027
  CheckUpToFaceLimits = true
  ClaimChildren = false
  Direction = (0,0,1)
  Fit = 0
  FitJoin = 0
  InnerFit = 0
  InnerFitJoin = 0
  InvalidShape = false
  Length = 19
  Length2 = 100
  Linearize = true
  NewSolid = false
  Profile = -> Sketch054
  Suppress = false
  TaperInnerAngle = 0
  TaperInnerAngleRev = 0
  TreeRank = 261
  Type = 0
  ValidateShape = true
  _ProfileBasedVersion = 1
  expr: Length = <<Parameters>>.motor_shaft_length
FEATURE [Sketcher::SketchObject] Sketch055
  ArcFitTolerance = 1e-06
  AttachmentOffset = pos=(0,0,176) rot=(0,0,1;0rad)
  AttachmentSupport = -> [YZ_Plane011]
  ExternalBSplineMaxDegree = 5
  ExternalBSplineTolerance = 0.0001
  FullyConstrained = false
  InternalTolerance = 1e-06
  InvalidShape = false
  MakeInternals = false
  MapMode = 5
  Placement = pos=(176,-3.91e-14,3.91e-14) rot=(0.57735,0.57735,0.57735;2.0944rad)
  Support = -> [YZ_Plane011]
  TreeRank = 182
  ValidateShape = true
  expr: AttachmentOffset.Base.z = (<<Parameters>>.station_diameter + <<Parameters>>.thickness) * 2
  expr: Constraints[12] = <<Parameters>>.thickness + <<Parameters>>.motor_screw_head_height
  expr: Constraints[13] = <<Parameters>>.motor_height
  expr: Constraints[14] = <<Parameters>>.thickness
  expr: Constraints[15] = <<Parameters>>.thickness
  expr: Constraints[16] = (<<Parameters>>.station_diameter + <<Parameters>>.thickness) * 2
  expr: Constraints[17] = <<Parameters>>.thickness
  expr: Constraints[21] = <<Parameters>>.thickness
  expr: Constraints[22] = <<Parameters>>.motor_shaft_length
  expr: Constraints[23] = <<Parameters>>.station_diameter + <<Parameters>>.thickness
  expr: Constraints[26] = <<Parameters>>.screen_overall_height + 2 * <<Parameters>>.thickness
  expr: Constraints[47] = 180 - <<Parameters>>.screen_angle
  sketch-geometry (19):
    g0: LineSegment [constr] StartX=0 StartY=-36.25 StartZ=0 EndX=-176 EndY=-36.25 EndZ=0
    g1: LineSegment [constr] StartX=0 StartY=-36.25 StartZ=0 EndX=0 EndY=-30 EndZ=0
    g2: LineSegment [constr] StartX=0 StartY=-30 StartZ=0 EndX=-173 EndY=-30 EndZ=0
    g3: LineSegment [constr] StartX=-176 StartY=-36.25 StartZ=0 EndX=-176 EndY=-25.7574 EndZ=0
    g4: LineSegment [constr] StartX=-173 StartY=-30 StartZ=0 EndX=-173 EndY=-27 EndZ=0
    g5: LineSegment [constr] StartX=-145.194 StartY=0.805848 StartZ=0 EndX=-147.315 EndY=2.92717 EndZ=0
    g6: LineSegment StartX=-88 StartY=22 StartZ=0 EndX=-99.2893 EndY=22 EndZ=0
    g7: LineSegment StartX=-88 StartY=22 StartZ=0 EndX=-88 EndY=19 EndZ=0
    g8: LineSegment [constr] StartX=-102.289 StartY=19 StartZ=0 EndX=-88 EndY=19 EndZ=0
    g9: LineSegment [constr] StartX=-102.289 StartY=43.7107 StartZ=0 EndX=-102.289 EndY=19 EndZ=0
    g10: LineSegment StartX=-99.2893 StartY=43.7107 StartZ=0 EndX=-99.2893 EndY=22 EndZ=0
    g11: ArcOfCircle CenterX=-102.289 CenterY=43.7107 CenterZ=0 NormalX=0 NormalY=0 NormalZ=1 AngleXU=0 Radius=3 StartAngle=1e-16 EndAngle=2.35619
    g12: LineSegment [constr] StartX=-176 StartY=-25.7574 StartZ=0 EndX=-150.243 EndY=0 EndZ=0
    g13: LineSegment StartX=-150.243 StartY=0 StartZ=0 EndX=-104.411 EndY=45.832 EndZ=0
    g14: LineSegment [constr] StartX=-173 StartY=-27 StartZ=0 EndX=-146 EndY=0 EndZ=0
    g15: LineSegment [constr] StartX=-146 StartY=0 StartZ=0 EndX=-102.289 EndY=43.7107 EndZ=0
    g16: LineSegment StartX=-150.243 StartY=0 StartZ=0 EndX=-146 EndY=0 EndZ=0
    g17: LineSegment StartX=-146 StartY=0 StartZ=0 EndX=-88 EndY=0 EndZ=0
    g18: LineSegment StartX=-88 StartY=0 StartZ=0 EndX=-88 EndY=19 EndZ=0
  constraints (53):
    c: PointOnObject(g0,g-2)
    c: Horizontal(g0)
    c: Coincident(g1,g0)
    c: PointOnObject(g1,g-2)
    c: Coincident(g2,g1)
    c: Horizontal(g2)
    c: Coincident(g3,g0)
    c: Vertical(g3)
    c: Coincident(g12,g3)
    c: Coincident(g4,g2)
    c: Vertical(g4)
    c: Coincident(g14,g4)
    c: DistanceY(g0,g1) = 6.25
    c: DistanceY(g1,g-1) = 30
    c: DistanceX(g0,g2) = 3
    c: Distance(g5,g5) = 3
    c: DistanceX(g0,g-1) = 176
    c: DistanceY(g2,g4) = 3
    c: Horizontal(g6)
    c: Coincident(g7,g6)
    c: Vertical(g7)
    c: DistanceY(g7,g6) = 3
    c: DistanceY(g-1,g7) = 19
    c: DistanceX(g7,g-1) = 88
    c: Coincident(g8,g7)
    c: Horizontal(g8)
    c: Distance(g15,g4) = 100
    c: Coincident(g9,g15)
    c: Coincident(g9,g8)
    c: Vertical(g9)
    c: Coincident(g10,g6)
    c: Vertical(g10)
    c: Tangent(g13,g11) = 1.5708
    c: Tangent(g10,g11) = 1.5708
    c: Coincident(g11,g15)
    c: Coincident(g12,g13)
    c: Perpendicular(g12,g5)
    c: PointOnObject(g5,g13)
    c: Coincident(g14,g15)
    c: PointOnObject(g5,g14)
    c: Parallel(g14,g12)
    c: Parallel(g15,g12)
    c: Parallel(g14,g13)
    c: Coincident(g16,g12)
    c: Coincident(g16,g14)
    c: Horizontal(g16)
    c: PointOnObject(g12,g-1)
    c: Angle(g-1,g13) = 0.785398
    c: Coincident(g17,g15)
    c: PointOnObject(g17,g-1)
    c: Coincident(g18,g17)
    c: Coincident(g18,g7)
    c: Vertical(g18)
FEATURE [PartDesign::Pad] Pad029
  AddSubType = 0
  AlongSketchNormal = false
  AutoTaperInnerAngle = true
  BaseFeature = -> Pad028
  CheckUpToFaceLimits = true
  ClaimChildren = false
  Direction = (1,-3e-16,3e-16)
  Fit = 0
  FitJoin = 0
  InnerFit = 0
  InnerFitJoin = 0
  InvalidShape = false
  Length = 3
  Length2 = 100
  Linearize = true
  NewSolid = false
  Profile = -> Sketch055
  Reversed = true
  Suppress = false
  TaperInnerAngle = 0
  TaperInnerAngleRev = 0
  TreeRank = 262
  Type = 0
  ValidateShape = true
  _ProfileBasedVersion = 1
  expr: Length = <<Parameters>>.thickness
FEATURE [Sketcher::SketchObject] Sketch057
  ArcFitTolerance = 1e-06
  ExternalBSplineMaxDegree = 5
  ExternalBSplineTolerance = 0.0001
  FullyConstrained = false
  InternalTolerance = 1e-06
  InvalidShape = false
  MakeInternals = false
  MapMode = 2
  Placement = pos=(88,-88,0) rot=(0.57735,0.57735,0.57735;0rad)
  TreeRank = 184
  ValidateShape = true
  expr: Placement.Base.x = <<Parameters>>.station_diameter + <<Parameters>>.thickness
  expr: Placement.Base.y = -(<<Parameters>>.station_diameter + <<Parameters>>.thickness)
  expr: Constraints[0] = <<Parameters>>.station_diameter
  expr: Constraints[14] = <<Parameters>>.motor_screw_spacing
  expr: Constraints[29] = <<Parameters>>.motor_screw_shaft_diameter
  expr: Constraints[3] = <<Parameters>>.station_diameter
  sketch-geometry (20):
    g0: Circle [constr] CenterX=-42.5 CenterY=42.5 CenterZ=0 NormalX=0 NormalY=0 NormalZ=1 AngleXU=0 Radius=42.5
    g1: Circle [constr] CenterX=42.5 CenterY=42.5 CenterZ=0 NormalX=0 NormalY=0 NormalZ=1 AngleXU=0 Radius=42.5
    g2: LineSegment [constr] StartX=-29.5 StartY=29.5 StartZ=0 EndX=-29.5 EndY=55.5 EndZ=0
    g3: LineSegment [constr] StartX=-29.5 StartY=55.5 StartZ=0 EndX=-55.5 EndY=55.5 EndZ=0
    g4: LineSegment [constr] StartX=-55.5 StartY=55.5 StartZ=0 EndX=-55.5 EndY=29.5 EndZ=0
    g5: LineSegment [constr] StartX=-55.5 StartY=29.5 StartZ=0 EndX=-29.5 EndY=29.5 EndZ=0
    g6: GeomPoint [constr] X=-42.5 Y=42.5 Z=0
    g7: LineSegment [constr] StartX=55.5 StartY=29.5 StartZ=0 EndX=55.5 EndY=55.5 EndZ=0
    g8: LineSegment [constr] StartX=55.5 StartY=55.5 StartZ=0 EndX=29.5 EndY=55.5 EndZ=0
    g9: LineSegment [constr] StartX=29.5 StartY=55.5 StartZ=0 EndX=29.5 EndY=29.5 EndZ=0
    g10: LineSegment [constr] StartX=29.5 StartY=29.5 StartZ=0 EndX=55.5 EndY=29.5 EndZ=0
    g11: GeomPoint [constr] X=42.5 Y=42.5 Z=0
    g12: Circle CenterX=-55.5 CenterY=55.5 CenterZ=0 NormalX=0 NormalY=0 NormalZ=1 AngleXU=0 Radius=1.75
    g13: Circle CenterX=-29.5 CenterY=55.5 CenterZ=0 NormalX=0 NormalY=0 NormalZ=1 AngleXU=0 Radius=1.75
    g14: Circle CenterX=-29.5 CenterY=29.5 CenterZ=0 NormalX=0 NormalY=0 NormalZ=1 AngleXU=0 Radius=1.75
    g15: Circle CenterX=-55.5 CenterY=29.5 CenterZ=0 NormalX=0 NormalY=0 NormalZ=1 AngleXU=0 Radius=1.75
    g16: Circle CenterX=29.5 CenterY=55.5 CenterZ=0 NormalX=0 NormalY=0 NormalZ=1 AngleXU=0 Radius=1.75
    g17: Circle CenterX=55.5 CenterY=55.5 CenterZ=0 NormalX=0 NormalY=0 NormalZ=1 AngleXU=0 Radius=1.75
    g18: Circle CenterX=55.5 CenterY=29.5 CenterZ=0 NormalX=0 NormalY=0 NormalZ=1 AngleXU=0 Radius=1.75
    g19: Circle CenterX=29.5 CenterY=29.5 CenterZ=0 NormalX=0 NormalY=0 NormalZ=1 AngleXU=0 Radius=1.75
  constraints (44):
    c: Diameter(g0) = 85
    c: Equal(g0,g1)
    c: Symmetric(g0,g1,g-2)
    c: DistanceX(g0,g1) = 85
    c: Coincident(g2,g3)
    c: Coincident(g3,g4)
    c: Coincident(g4,g5)
    c: Coincident(g5,g2)
    c: Horizontal(g3)
    c: Horizontal(g5)
    c: Vertical(g2)
    c: Vertical(g4)
    c: Symmetric(g3,g2,g6)
    c: Coincident(g6,g0)
    c: DistanceX(g3,g2) = 26
    c: Equal(g3,g4)
    c: Coincident(g7,g8)
    c: Coincident(g8,g9)
    c: Coincident(g9,g10)
    c: Coincident(g10,g7)
    c: Horizontal(g8)
    c: Horizontal(g10)
    c: Vertical(g7)
    c: Vertical(g9)
    c: Symmetric(g8,g7,g11)
    c: Coincident(g11,g1)
    c: Equal(g3,g8)
    c: Equal(g3,g9)
    c: Coincident(g12,g3)
    c: Diameter(g12) = 3.5
    c: Coincident(g13,g2)
    c: Coincident(g14,g2)
    c: Coincident(g15,g4)
    c: Coincident(g16,g8)
    c: Coincident(g17,g7)
    c: Coincident(g18,g7)
    c: Coincident(g19,g9)
    c: Equal(g12,g13)
    c: Equal(g12,g15)
    c: Equal(g12,g14)
    c: Equal(g12,g16)
    c: Equal(g16,g17)
    c: Equal(g16,g19)
    c: Equal(g16,g18)
FEATURE [PartDesign::Pocket] Pocket024
  AddSubType = 1
  AutoTaperInnerAngle = true
  BaseFeature = -> Pad029
  CheckUpToFaceLimits = true
  ClaimChildren = false
  Fit = 0
  FitJoin = 0
  InnerFit = 0
  InnerFitJoin = 0
  InvalidShape = false
  Length = 100
  Length2 = 100
  Linearize = true
  NewSolid = false
  Profile = -> Sketch057
  Suppress = false
  TaperInnerAngle = 0
  TaperInnerAngleRev = 0
  TreeRank = 264
  Type = 0
  ValidateShape = true
  _ProfileBasedVersion = 1
  _Version = 1
FEATURE [Sketcher::SketchObject] Sketch058
  ArcFitTolerance = 1e-06
  ExternalBSplineMaxDegree = 5
  ExternalBSplineTolerance = 0.0001
  FullyConstrained = false
  InternalTolerance = 1e-06
  InvalidShape = false
  MakeInternals = false
  MapMode = 2
  Placement = pos=(88,-88,-36.25) rot=(0.57735,0.57735,0.57735;0rad)
  TreeRank = 186
  ValidateShape = true
  expr: Placement.Base.x = <<Parameters>>.station_diameter + <<Parameters>>.thickness
  expr: Placement.Base.y = -(<<Parameters>>.station_diameter + <<Parameters>>.thickness)
  expr: Placement.Base.z = -(<<Parameters>>.motor_height + <<Parameters>>.thickness + <<Parameters>>.motor_screw_head_height)
  expr: Constraints[0] = <<Parameters>>.station_diameter
  expr: Constraints[14] = <<Parameters>>.motor_screw_spacing
  expr: Constraints[29] = <<Parameters>>.motor_screw_head_diameter
  expr: Constraints[3] = <<Parameters>>.station_diameter
  sketch-geometry (20):
    g0: Circle [constr] CenterX=-42.5 CenterY=42.5 CenterZ=0 NormalX=0 NormalY=0 NormalZ=1 AngleXU=0 Radius=42.5
    g1: Circle [constr] CenterX=42.5 CenterY=42.5 CenterZ=0 NormalX=0 NormalY=0 NormalZ=1 AngleXU=0 Radius=42.5
    g2: LineSegment [constr] StartX=-29.5 StartY=29.5 StartZ=0 EndX=-29.5 EndY=55.5 EndZ=0
    g3: LineSegment [constr] StartX=-29.5 StartY=55.5 StartZ=0 EndX=-55.5 EndY=55.5 EndZ=0
    g4: LineSegment [constr] StartX=-55.5 StartY=55.5 StartZ=0 EndX=-55.5 EndY=29.5 EndZ=0
    g5: LineSegment [constr] StartX=-55.5 StartY=29.5 StartZ=0 EndX=-29.5 EndY=29.5 EndZ=0
    g6: GeomPoint [constr] X=-42.5 Y=42.5 Z=0
    g7: LineSegment [constr] StartX=55.5 StartY=29.5 StartZ=0 EndX=55.5 EndY=55.5 EndZ=0
    g8: LineSegment [constr] StartX=55.5 StartY=55.5 StartZ=0 EndX=29.5 EndY=55.5 EndZ=0
    g9: LineSegment [constr] StartX=29.5 StartY=55.5 StartZ=0 EndX=29.5 EndY=29.5 EndZ=0
    g10: LineSegment [constr] StartX=29.5 StartY=29.5 StartZ=0 EndX=55.5 EndY=29.5 EndZ=0
    g11: GeomPoint [constr] X=42.5 Y=42.5 Z=0
    g12: Circle CenterX=-55.5 CenterY=55.5 CenterZ=0 NormalX=0 NormalY=0 NormalZ=1 AngleXU=0 Radius=3
    g13: Circle CenterX=-29.5 CenterY=55.5 CenterZ=0 NormalX=0 NormalY=0 NormalZ=1 AngleXU=0 Radius=3
    g14: Circle CenterX=-29.5 CenterY=29.5 CenterZ=0 NormalX=0 NormalY=0 NormalZ=1 AngleXU=0 Radius=3
    g15: Circle CenterX=-55.5 CenterY=29.5 CenterZ=0 NormalX=0 NormalY=0 NormalZ=1 AngleXU=0 Radius=3
    g16: Circle CenterX=29.5 CenterY=55.5 CenterZ=0 NormalX=0 NormalY=0 NormalZ=1 AngleXU=0 Radius=3
    g17: Circle CenterX=55.5 CenterY=55.5 CenterZ=0 NormalX=0 NormalY=0 NormalZ=1 AngleXU=0 Radius=3
    g18: Circle CenterX=55.5 CenterY=29.5 CenterZ=0 NormalX=0 NormalY=0 NormalZ=1 AngleXU=0 Radius=3
    g19: Circle CenterX=29.5 CenterY=29.5 CenterZ=0 NormalX=0 NormalY=0 NormalZ=1 AngleXU=0 Radius=3
  constraints (44):
    c: Diameter(g0) = 85
    c: Equal(g0,g1)
    c: Symmetric(g0,g1,g-2)
    c: DistanceX(g0,g1) = 85
    c: Coincident(g2,g3)
    c: Coincident(g3,g4)
    c: Coincident(g4,g5)
    c: Coincident(g5,g2)
    c: Horizontal(g3)
    c: Horizontal(g5)
    c: Vertical(g2)
    c: Vertical(g4)
    c: Symmetric(g3,g2,g6)
    c: Coincident(g6,g0)
    c: DistanceX(g3,g2) = 26
    c: Equal(g3,g4)
    c: Coincident(g7,g8)
    c: Coincident(g8,g9)
    c: Coincident(g9,g10)
    c: Coincident(g10,g7)
    c: Horizontal(g8)
    c: Horizontal(g10)
    c: Vertical(g7)
    c: Vertical(g9)
    c: Symmetric(g8,g7,g11)
    c: Coincident(g11,g1)
    c: Equal(g3,g8)
    c: Equal(g3,g9)
    c: Coincident(g12,g3)
    c: Diameter(g12) = 6
    c: Coincident(g13,g2)
    c: Coincident(g14,g2)
    c: Coincident(g15,g4)
    c: Coincident(g16,g8)
    c: Coincident(g17,g7)
    c: Coincident(g18,g7)
    c: Coincident(g19,g9)
    c: Equal(g12,g13)
    c: Equal(g12,g15)
    c: Equal(g12,g14)
    c: Equal(g12,g16)
    c: Equal(g16,g17)
    c: Equal(g16,g19)
    c: Equal(g16,g18)
FEATURE [PartDesign::Pocket] Pocket025
  AddSubType = 1
  AutoTaperInnerAngle = true
  BaseFeature = -> Pocket024
  CheckUpToFaceLimits = true
  ClaimChildren = false
  Fit = 0
  FitJoin = 0
  InnerFit = 0
  InnerFitJoin = 0
  InvalidShape = false
  Length = 3.25
  Length2 = 100
  Linearize = true
  NewSolid = false
  Profile = -> Sketch058
  Reversed = true
  Suppress = false
  TaperInnerAngle = 0
  TaperInnerAngleRev = 0
  TreeRank = 265
  Type = 0
  ValidateShape = true
  _ProfileBasedVersion = 1
  _Version = 1
  expr: Length = <<Parameters>>.motor_screw_head_height
FEATURE [Sketcher::SketchObject] Sketch059
  ArcFitTolerance = 1e-06
  ExternalBSplineMaxDegree = 5
  ExternalBSplineTolerance = 0.0001
  FullyConstrained = true
  InternalTolerance = 1e-06
  InvalidShape = false
  MakeInternals = false
  MapMode = 2
  Placement = pos=(88,-88,-30) rot=(0.57735,0.57735,0.57735;0rad)
  TreeRank = 188
  ValidateShape = true
  expr: Placement.Base.x = <<Parameters>>.station_diameter + <<Parameters>>.thickness
  expr: Placement.Base.y = -(<<Parameters>>.station_diameter + <<Parameters>>.thickness)
  expr: Placement.Base.z = -<<Parameters>>.motor_height
  expr: Constraints[14] = <<Parameters>>.thickness * 2
  expr: Constraints[17] = <<Parameters>>.station_diameter + <<Parameters>>.thickness
  expr: Constraints[18] = (<<Parameters>>.station_diameter + <<Parameters>>.thickness) * 2 - 4 * <<Parameters>>.thickness - <<Parameters>>.motor_shaft_mount_diameter / 2
  expr: Constraints[21] = <<Parameters>>.station_diameter + <<Parameters>>.thickness
  sketch-geometry (8):
    g0: LineSegment StartX=-82 StartY=69.5 StartZ=0 EndX=-88 EndY=69.5 EndZ=0
    g1: LineSegment StartX=-88 StartY=69.5 StartZ=0 EndX=-88 EndY=-69.5 EndZ=0
    g2: LineSegment StartX=-88 StartY=-69.5 StartZ=0 EndX=-82 EndY=-69.5 EndZ=0
    g3: LineSegment StartX=-82 StartY=-69.5 StartZ=0 EndX=-82 EndY=69.5 EndZ=0
    g4: LineSegment StartX=-69.5 StartY=82 StartZ=0 EndX=69.5 EndY=82 EndZ=0
    g5: LineSegment StartX=69.5 StartY=82 StartZ=0 EndX=69.5 EndY=88 EndZ=0
    g6: LineSegment StartX=69.5 StartY=88 StartZ=0 EndX=-69.5 EndY=88 EndZ=0
    g7: LineSegment StartX=-69.5 StartY=88 StartZ=0 EndX=-69.5 EndY=82 EndZ=0
  constraints (22):
    c: Coincident(g0,g1)
    c: Coincident(g1,g2)
    c: Coincident(g2,g3)
    c: Coincident(g3,g0)
    c: Horizontal(g0)
    c: Horizontal(g2)
    c: Vertical(g1)
    c: Coincident(g4,g5)
    c: Coincident(g5,g6)
    c: Coincident(g6,g7)
    c: Coincident(g7,g4)
    c: Horizontal(g6)
    c: Vertical(g5)
    c: Vertical(g7)
    c: DistanceX(g0,g0) = 6
    c: Equal(g0,g5)
    c: Symmetric(g4,g4,g-2)
    c: DistanceY(g-1,g6) = 88
    c: DistanceX(g6,g5) = 139
    c: Equal(g6,g3)
    c: Symmetric(g0,g2,g-1)
    c: DistanceX(g0,g-1) = 88
FEATURE [PartDesign::Pocket] Pocket026
  AddSubType = 1
  AutoTaperInnerAngle = true
  BaseFeature = -> Pocket025
  CheckUpToFaceLimits = true
  ClaimChildren = false
  Fit = 0
  FitJoin = 0
  InnerFit = 0
  InnerFitJoin = 0
  InvalidShape = false
  Length = 1
  Length2 = 100
  Linearize = true
  NewSolid = false
  Profile = -> Sketch059
  Suppress = false
  TaperInnerAngle = 0
  TaperInnerAngleRev = 0
  TreeRank = 266
  Type = 0
  ValidateShape = true
  _ProfileBasedVersion = 1
  _Version = 1
  expr: Length = <<Parameters>>.lap_join_thickness
FEATURE [Sketcher::SketchObject] Sketch060
  ArcFitTolerance = 1e-06
  AttachmentSupport = -> [XY_Plane011]
  ExternalBSplineMaxDegree = 5
  ExternalBSplineTolerance = 0.0001
  FullyConstrained = true
  InternalTolerance = 1e-06
  InvalidShape = false
  MakeInternals = false
  MapMode = 5
  Support = -> [XY_Plane011]
  TreeRank = 190
  ValidateShape = true
  expr: Constraints[18] = <<Parameters>>.station_diameter / 3
  expr: Constraints[21] = (<<Parameters>>.station_diameter + <<Parameters>>.thickness) * 2
  expr: Constraints[8] = (<<Parameters>>.station_diameter + <<Parameters>>.thickness) * 2 * 2
  sketch-geometry (10):
    g0: LineSegment StartX=-88 StartY=88 StartZ=0 EndX=264 EndY=88 EndZ=0
    g1: LineSegment StartX=264 StartY=88 StartZ=0 EndX=264 EndY=-264 EndZ=0
    g2: LineSegment StartX=264 StartY=-264 StartZ=0 EndX=-88 EndY=-264 EndZ=0
    g3: LineSegment StartX=-88 StartY=-264 StartZ=0 EndX=-88 EndY=88 EndZ=0
    g4: LineSegment StartX=176 StartY=-161.833 StartZ=0 EndX=176 EndY=0 EndZ=0
    g5: LineSegment StartX=176 StartY=0 StartZ=0 EndX=0 EndY=0 EndZ=0
    g6: LineSegment StartX=0 StartY=0 StartZ=0 EndX=0 EndY=-176 EndZ=0
    g7: LineSegment StartX=0 StartY=-176 StartZ=0 EndX=161.833 EndY=-176 EndZ=0
    g8: GeomPoint [constr] X=88 Y=-88 Z=0
    g9: ArcOfCircle CenterX=161.833 CenterY=-161.833 CenterZ=0 NormalX=0 NormalY=0 NormalZ=1 AngleXU=0 Radius=14.1667 StartAngle=4.71239 EndAngle=6.28319
  constraints (25):
    c: Coincident(g0,g1)
    c: Coincident(g1,g2)
    c: Coincident(g2,g3)
    c: Coincident(g3,g0)
    c: Horizontal(g0)
    c: Horizontal(g2)
    c: Vertical(g1)
    c: Vertical(g3)
    c: DistanceX(g0,g0) = 352
    c: Equal(g0,g1)
    c: Coincident(g4,g5)
    c: Coincident(g5,g6)
    c: Coincident(g6,g7)
    c: Horizontal(g5)
    c: Horizontal(g7)
    c: Vertical(g4)
    c: Vertical(g6)
    c: Equal(g5,g6)
    c: Diameter(g9) = 28.3333
    c: Symmetric(g0,g1,g8)
    c: Coincident(g5,g-1)
    c: DistanceX(g5,g4) = 176
    c: Symmetric(g6,g4,g8)
    c: Tangent(g9,g4) = -1.5708
    c: Tangent(g9,g7) = -1.5708
FEATURE [Sketcher::SketchObject] Sketch061
  ArcFitTolerance = 1e-06
  AttachmentSupport = -> [YZ_Plane011]
  ExternalBSplineMaxDegree = 5
  ExternalBSplineTolerance = 0.0001
  FullyConstrained = false
  InternalTolerance = 1e-06
  InvalidShape = false
  MakeInternals = false
  MapMode = 5
  Placement = pos=(0,0,0) rot=(0.57735,0.57735,0.57735;2.0944rad)
  Support = -> [YZ_Plane011]
  TreeRank = 192
  ValidateShape = true
  expr: Constraints[12] = <<Parameters>>.thickness + <<Parameters>>.motor_screw_head_height
  expr: Constraints[13] = <<Parameters>>.motor_height
  expr: Constraints[14] = <<Parameters>>.thickness
  expr: Constraints[18] = <<Parameters>>.screen_body_thickness
  expr: Constraints[19] = (<<Parameters>>.station_diameter + <<Parameters>>.thickness) * 2
  expr: Constraints[20] = <<Parameters>>.screen_angle
  expr: Constraints[21] = <<Parameters>>.thickness
  expr: Constraints[25] = <<Parameters>>.thickness
  expr: Constraints[26] = <<Parameters>>.motor_shaft_length
  expr: Constraints[27] = <<Parameters>>.station_diameter + <<Parameters>>.thickness
  expr: Constraints[31] = <<Parameters>>.screen_overall_height + 2 * <<Parameters>>.thickness
  expr: Constraints[47] = 10 * <<Parameters>>.thickness
  sketch-geometry (17):
    g0: LineSegment [constr] StartX=0 StartY=-36.25 StartZ=0 EndX=-176 EndY=-36.25 EndZ=0
    g1: LineSegment [constr] StartX=0 StartY=-36.25 StartZ=0 EndX=0 EndY=-30 EndZ=0
    g2: LineSegment [constr] StartX=0 StartY=-30 StartZ=0 EndX=-173 EndY=-30 EndZ=0
    g3: LineSegment [constr] StartX=-176 StartY=-36.25 StartZ=0 EndX=-176 EndY=-22.2218 EndZ=0
    g4: LineSegment StartX=-176 StartY=-22.2218 StartZ=0 EndX=-106.178 EndY=47.5998 EndZ=0
    g5: LineSegment [constr] StartX=-173 StartY=-30 StartZ=0 EndX=-173 EndY=-27 EndZ=0
    g6: LineSegment [constr] StartX=-173 StartY=-27 StartZ=0 EndX=-102.289 EndY=43.7107 EndZ=0
    g7: LineSegment [constr] StartX=-145.874 StartY=0.12624 StartZ=0 EndX=-149.763 EndY=4.01533 EndZ=0
    g8: LineSegment [constr] StartX=-88 StartY=22 StartZ=0 EndX=-96.7893 EndY=22 EndZ=0
    g9: LineSegment [constr] StartX=-88 StartY=22 StartZ=0 EndX=-88 EndY=19 EndZ=0
    g10: LineSegment [constr] StartX=-102.289 StartY=19 StartZ=0 EndX=-88 EndY=19 EndZ=0
    g11: LineSegment [constr] StartX=-102.289 StartY=43.7107 StartZ=0 EndX=-102.289 EndY=19 EndZ=0
    g12: LineSegment [constr] StartX=-96.7893 StartY=43.7107 StartZ=0 EndX=-96.7893 EndY=22 EndZ=0
    g13: ArcOfCircle [constr] CenterX=-102.289 CenterY=43.7107 CenterZ=0 NormalX=0 NormalY=0 NormalZ=1 AngleXU=0 Radius=5.5 StartAngle=-1.4149e-12 EndAngle=2.35619
    g14: LineSegment StartX=-176 StartY=-22.2218 StartZ=0 EndX=-197.213 EndY=-1.00862 EndZ=0
    g15: LineSegment StartX=-106.178 StartY=47.5998 StartZ=0 EndX=-127.392 EndY=68.813 EndZ=0
    g16: LineSegment StartX=-127.392 StartY=68.813 StartZ=0 EndX=-197.213 EndY=-1.00862 EndZ=0
  constraints (48):
    c: PointOnObject(g0,g-2)
    c: Horizontal(g0)
    c: Coincident(g1,g0)
    c: PointOnObject(g1,g-2)
    c: Coincident(g2,g1)
    c: Horizontal(g2)
    c: Coincident(g3,g0)
    c: Vertical(g3)
    c: Coincident(g4,g3)
    c: Coincident(g5,g2)
    c: Vertical(g5)
    c: Coincident(g6,g5)
    c: DistanceY(g0,g1) = 6.25
    c: DistanceY(g1,g-1) = 30
    c: DistanceX(g0,g2) = 3
    c: Parallel(g6,g4)
    c: PointOnObject(g7,g6)
    c: Perpendicular(g4,g7)
    c: Distance(g7,g7) = 5.5
    c: DistanceX(g0,g-1) = 176
    c: Angle(g5,g6) = 2.35619
    c: DistanceY(g2,g5) = 3
    c: Horizontal(g8)
    c: Coincident(g9,g8)
    c: Vertical(g9)
    c: DistanceY(g9,g8) = 3
    c: DistanceY(g-1,g9) = 19
    c: DistanceX(g9,g-1) = 88
    c: PointOnObject(g7,g4)
    c: Coincident(g10,g9)
    c: Horizontal(g10)
    c: Distance(g6,g5) = 100
    c: Coincident(g11,g6)
    c: Coincident(g11,g10)
    c: Vertical(g11)
    c: Coincident(g12,g8)
    c: Vertical(g12)
    c: Tangent(g4,g13) = 1.5708
    c: Tangent(g12,g13) = 1.5708
    c: Coincident(g13,g6)
    c: Coincident(g14,g3)
    c: Coincident(g15,g4)
    c: Coincident(g16,g14)
    c: Parallel(g15,g14)
    c: Parallel(g4,g16)
    c: Coincident(g15,g16)
    c: Perpendicular(g14,g4)
    c: Distance(g4,g14) = 30
FEATURE [PartDesign::Pocket] Pocket027
  AddSubType = 1
  AutoTaperInnerAngle = true
  BaseFeature = -> Pocket026
  CheckUpToFaceLimits = true
  ClaimChildren = false
  Fit = 0
  FitJoin = 0
  InnerFit = 0
  InnerFitJoin = 0
  InvalidShape = false
  Length = 100
  Length2 = 100
  Linearize = true
  NewSolid = false
  Profile = -> Sketch060
  Suppress = false
  TaperInnerAngle = 0
  TaperInnerAngleRev = 0
  TreeRank = 269
  Type = 4
  ValidateShape = true
  _ProfileBasedVersion = 1
  _Version = 1
FEATURE [PartDesign::Pocket] Pocket028
  AddSubType = 1
  AutoTaperInnerAngle = true
  BaseFeature = -> Pocket027
  CheckUpToFaceLimits = true
  ClaimChildren = false
  Fit = 0
  FitJoin = 0
  InnerFit = 0
  InnerFitJoin = 0
  InvalidShape = false
  Length = 500
  Length2 = 100
  Linearize = true
  NewSolid = false
  Profile = -> Sketch061
  Reversed = true
  Suppress = false
  TaperInnerAngle = 0
  TaperInnerAngleRev = 0
  TreeRank = 268
  Type = 0
  ValidateShape = true
  _ProfileBasedVersion = 1
  _Version = 1
FEATURE [Sketcher::SketchObject] Sketch063
  ArcFitTolerance = 1e-06
  AttachmentSupport = -> [YZ_Plane012]
  ExternalBSplineMaxDegree = 5
  ExternalBSplineTolerance = 0.0001
  FullyConstrained = true
  InternalTolerance = 1e-06
  InvalidShape = false
  MakeInternals = false
  MapMode = 5
  Placement = pos=(0,0,0) rot=(0.57735,0.57735,0.57735;2.0944rad)
  Support = -> [YZ_Plane012]
  TreeRank = 144
  ValidateShape = true
  expr: Constraints[2] = <<Parameters>>.station_diameter + <<Parameters>>.thickness
  expr: Constraints[3] = <<Parameters>>.motor_shaft_length
  expr: Constraints[8] = <<Parameters>>.thickness
  sketch-geometry (4):
    g0: LineSegment StartX=0 StartY=19 StartZ=0 EndX=-88 EndY=19 EndZ=0
    g1: LineSegment StartX=0 StartY=22 StartZ=0 EndX=-88 EndY=22 EndZ=0
    g2: LineSegment StartX=0 StartY=22 StartZ=0 EndX=0 EndY=19 EndZ=0
    g3: LineSegment StartX=-88 StartY=22 StartZ=0 EndX=-88 EndY=19 EndZ=0
  constraints (12):
    c: PointOnObject(g0,g-2)
    c: Horizontal(g0)
    c: DistanceX(g0,g0) = 88
    c: DistanceY(g-1,g0) = 19
    c: PointOnObject(g1,g-2)
    c: Horizontal(g1)
    c: Coincident(g2,g1)
    c: Coincident(g2,g0)
    c: DistanceY(g0,g1) = 3
    c: Coincident(g3,g1)
    c: Coincident(g3,g0)
    c: Vertical(g3)
FEATURE [PartDesign::Pad] Pad030
  AddSubType = 0
  AlongSketchNormal = false
  AutoTaperInnerAngle = true
  CheckUpToFaceLimits = true
  ClaimChildren = false
  Direction = (1,-2e-16,3e-16)
  Fit = 0
  FitJoin = 0
  InnerFit = 0
  InnerFitJoin = 0
  InvalidShape = false
  Length = 176
  Length2 = 100
  Linearize = true
  NewSolid = false
  Profile = -> Sketch063
  Suppress = false
  TaperInnerAngle = 0
  TaperInnerAngleRev = 0
  TreeRank = 281
  Type = 0
  ValidateShape = true
  _ProfileBasedVersion = 1
  expr: Length = 2 * (<<Parameters>>.station_diameter + <<Parameters>>.thickness)
FEATURE [Sketcher::SketchObject] Sketch064
  ArcFitTolerance = 1e-06
  AttachmentSupport = -> [XY_Plane012]
  ExternalBSplineMaxDegree = 5
  ExternalBSplineTolerance = 0.0001
  FullyConstrained = true
  InternalTolerance = 1e-06
  InvalidShape = false
  MakeInternals = false
  MapMode = 5
  Support = -> [XY_Plane012]
  TreeRank = 146
  ValidateShape = true
  expr: Constraints[0] = <<Parameters>>.station_diameter
  expr: Constraints[2] = <<Parameters>>.station_diameter
  expr: Constraints[3] = <<Parameters>>.station_diameter / 2 + <<Parameters>>.thickness
  expr: Constraints[7] = <<Parameters>>.motor_shaft_mount_diameter
  expr: Constraints[9] = <<Parameters>>.station_diameter / 2 + <<Parameters>>.thickness
  sketch-geometry (4):
    g0: Circle [constr] CenterX=45.5 CenterY=-45.5 CenterZ=0 NormalX=0 NormalY=0 NormalZ=1 AngleXU=0 Radius=42.5
    g1: Circle [constr] CenterX=130.5 CenterY=-45.5 CenterZ=0 NormalX=0 NormalY=0 NormalZ=1 AngleXU=0 Radius=42.5
    g2: Circle CenterX=45.5 CenterY=-45.5 CenterZ=0 NormalX=0 NormalY=0 NormalZ=1 AngleXU=0 Radius=25
    g3: Circle CenterX=130.5 CenterY=-45.5 CenterZ=0 NormalX=0 NormalY=0 NormalZ=1 AngleXU=0 Radius=25
  constraints (10):
    c: Diameter(g0) = 85
    c: Equal(g0,g1)
    c: DistanceX(g0,g1) = 85
    c: DistanceY(g1,g-1) = 45.5
    c: DistanceY(g1,g0) = 0
    c: Coincident(g2,g0)
    c: Coincident(g3,g1)
    c: Diameter(g2) = 50
    c: Equal(g2,g3)
    c: DistanceX(g-1,g2) = 45.5
FEATURE [PartDesign::Pocket] Pocket030
  AddSubType = 1
  AutoTaperInnerAngle = true
  BaseFeature = -> Pad030
  CheckUpToFaceLimits = true
  ClaimChildren = false
  Fit = 0
  FitJoin = 0
  InnerFit = 0
  InnerFitJoin = 0
  InvalidShape = false
  Length = 100
  Length2 = 100
  Linearize = true
  NewSolid = false
  Profile = -> Sketch064
  Suppress = false
  TaperInnerAngle = 0
  TaperInnerAngleRev = 0
  TreeRank = 282
  Type = 4
  ValidateShape = true
  _ProfileBasedVersion = 1
  _Version = 1
FEATURE [Sketcher::SketchObject] Sketch065
  ArcFitTolerance = 1e-06
  AttachmentSupport = -> [XY_Plane012]
  ExternalBSplineMaxDegree = 5
  ExternalBSplineTolerance = 0.0001
  FullyConstrained = true
  InternalTolerance = 1e-06
  InvalidShape = false
  MakeInternals = false
  MapMode = 5
  Support = -> [XY_Plane012]
  TreeRank = 160
  ValidateShape = true
  expr: Constraints[13] = <<Parameters>>.station_diameter + <<Parameters>>.thickness
  expr: Constraints[20] = <<Parameters>>.station_diameter + <<Parameters>>.thickness
  expr: Constraints[21] = (<<Parameters>>.station_diameter + <<Parameters>>.thickness) * 2
  expr: Constraints[5] = <<Parameters>>.motor_shaft_mount_diameter / 4
  expr: Constraints[7] = <<Parameters>>.motor_shaft_mount_diameter / 4
  sketch-geometry (7):
    g0: ArcOfCircle CenterX=0 CenterY=0 CenterZ=0 NormalX=0 NormalY=0 NormalZ=1 AngleXU=0 Radius=12.5 StartAngle=4.71239 EndAngle=6.28319
    g1: LineSegment StartX=0 StartY=-12.5 StartZ=0 EndX=0 EndY=0 EndZ=0
    g2: LineSegment StartX=0 StartY=0 StartZ=0 EndX=12.5 EndY=0 EndZ=0
    g3: ArcOfCircle CenterX=169.75 CenterY=0 CenterZ=0 NormalX=0 NormalY=0 NormalZ=1 AngleXU=0 Radius=6.25 StartAngle=3.14159 EndAngle=6.28319
    g4: LineSegment StartX=163.5 StartY=0 StartZ=0 EndX=176 EndY=0 EndZ=0
    g5: ArcOfCircle CenterX=88 CenterY=-88 CenterZ=0 NormalX=0 NormalY=0 NormalZ=1 AngleXU=0 Radius=6.25 StartAngle=4e-16 EndAngle=3.14159
    g6: LineSegment StartX=81.75 StartY=-88 StartZ=0 EndX=94.25 EndY=-88 EndZ=0
  constraints (22):
    c: Coincident(g0,g-1)
    c: Coincident(g1,g0)
    c: Coincident(g2,g0)
    c: Coincident(g0,g2)
    c: Coincident(g0,g1)
    c: Radius(g0) = 12.5
    c: PointOnObject(g3,g-1)
    c: Diameter(g3) = 12.5
    c: Horizontal(g4)
    c: PointOnObject(g3,g4)
    c: Coincident(g3,g4)
    c: Coincident(g3,g4)
    c: Equal(g3,g5)
    c: DistanceY(g5,g0) = 88
    c: Horizontal(g6)
    c: PointOnObject(g5,g6)
    c: Coincident(g5,g6)
    c: Coincident(g5,g6)
    c: Vertical(g1)
    c: Horizontal(g2)
    c: DistanceX(g0,g5) = 88
    c: DistanceX(g0,g3) = 176
FEATURE [PartDesign::Pad] Pad031
  AddSubType = 0
  AlongSketchNormal = false
  AutoTaperInnerAngle = true
  BaseFeature = -> Pocket030
  CheckUpToFaceLimits = true
  ClaimChildren = false
  Direction = (0,0,1)
  Fit = 0
  FitJoin = 0
  InnerFit = 0
  InnerFitJoin = 0
  InvalidShape = false
  Length = 19
  Length2 = 100
  Linearize = true
  NewSolid = false
  Profile = -> Sketch065
  Suppress = false
  TaperInnerAngle = 0
  TaperInnerAngleRev = 0
  TreeRank = 283
  Type = 0
  ValidateShape = true
  _ProfileBasedVersion = 1
  expr: Length = <<Parameters>>.motor_shaft_length
FEATURE [Sketcher::SketchObject] Sketch066
  ArcFitTolerance = 1e-06
  AttachmentSupport = -> [XY_Plane012]
  ExternalBSplineMaxDegree = 5
  ExternalBSplineTolerance = 0.0001
  FullyConstrained = true
  InternalTolerance = 1e-06
  InvalidShape = false
  MakeInternals = false
  MapMode = 5
  Support = -> [XY_Plane012]
  TreeRank = 162
  ValidateShape = true
  expr: Constraints[10] = (<<Parameters>>.station_diameter + <<Parameters>>.thickness) * 2 - 4 * <<Parameters>>.thickness - <<Parameters>>.motor_shaft_mount_diameter / 2
  expr: Constraints[19] = (2 * (<<Parameters>>.station_diameter + <<Parameters>>.thickness) - ((<<Parameters>>.station_diameter + <<Parameters>>.thickness) * 2 - 4 * <<Parameters>>.thickness - <<Parameters>>.motor_shaft_mount_diameter / 2)) / 2
  expr: Constraints[20] = <<Parameters>>.thickness * 2
  expr: Constraints[21] = <<Parameters>>.station_diameter + <<Parameters>>.thickness - 2 * <<Parameters>>.thickness - <<Parameters>>.motor_shaft_mount_diameter / 4
  expr: Constraints[23] = (2 * (<<Parameters>>.station_diameter + <<Parameters>>.thickness) - ((<<Parameters>>.station_diameter + <<Parameters>>.thickness) * 2 - 4 * <<Parameters>>.thickness - <<Parameters>>.motor_shaft_mount_diameter / 2)) / 2
  expr: Constraints[9] = <<Parameters>>.thickness * 2
  sketch-geometry (8):
    g0: LineSegment StartX=157.5 StartY=0 StartZ=0 EndX=18.5 EndY=0 EndZ=0
    g1: LineSegment StartX=18.5 StartY=0 StartZ=0 EndX=18.5 EndY=-6 EndZ=0
    g2: LineSegment StartX=18.5 StartY=-6 StartZ=0 EndX=157.5 EndY=-6 EndZ=0
    g3: LineSegment StartX=157.5 StartY=-6 StartZ=0 EndX=157.5 EndY=0 EndZ=0
    g4: LineSegment StartX=0 StartY=-18.5 StartZ=0 EndX=6 EndY=-18.5 EndZ=0
    g5: LineSegment StartX=6 StartY=-18.5 StartZ=0 EndX=6 EndY=-88 EndZ=0
    g6: LineSegment StartX=6 StartY=-88 StartZ=0 EndX=0 EndY=-88 EndZ=0
    g7: LineSegment StartX=0 StartY=-88 StartZ=0 EndX=0 EndY=-18.5 EndZ=0
  constraints (24):
    c: Coincident(g0,g1)
    c: Coincident(g1,g2)
    c: Coincident(g2,g3)
    c: Coincident(g3,g0)
    c: Horizontal(g0)
    c: Horizontal(g2)
    c: Vertical(g1)
    c: Vertical(g3)
    c: PointOnObject(g0,g-1)
    c: DistanceY(g2,g0) = 6
    c: DistanceX(g1,g2) = 139
    c: Coincident(g4,g5)
    c: Coincident(g5,g6)
    c: Coincident(g6,g7)
    c: Coincident(g7,g4)
    c: Horizontal(g4)
    c: Horizontal(g6)
    c: Vertical(g5)
    c: Vertical(g7)
    c: DistanceY(g4,g-1) = 18.5
    c: DistanceX(g4,g4) = 6
    c: DistanceY(g6,g4) = 69.5
    c: PointOnObject(g6,g-2)
    c: DistanceX(g-1,g0) = 18.5
FEATURE [PartDesign::Pocket] Pocket031
  AddSubType = 1
  AutoTaperInnerAngle = true
  BaseFeature = -> Pad031
  CheckUpToFaceLimits = true
  ClaimChildren = false
  Fit = 0
  FitJoin = 0
  InnerFit = 0
  InnerFitJoin = 0
  InvalidShape = false
  Length = 20
  Length2 = 100
  Linearize = true
  NewSolid = false
  Profile = -> Sketch066
  Reversed = true
  Suppress = false
  TaperInnerAngle = 0
  TaperInnerAngleRev = 0
  TreeRank = 284
  Type = 0
  ValidateShape = true
  _ProfileBasedVersion = 1
  _Version = 1
  expr: Length = <<Parameters>>.motor_shaft_length + <<Parameters>>.lap_join_thickness
FEATURE [Sketcher::SketchObject] Sketch067
  ArcFitTolerance = 1e-06
  AttachmentSupport = -> [XY_Plane012]
  ExternalBSplineMaxDegree = 5
  ExternalBSplineTolerance = 0.0001
  FullyConstrained = true
  InternalTolerance = 1e-06
  InvalidShape = false
  MakeInternals = false
  MapMode = 5
  Support = -> [XY_Plane012]
  TreeRank = 195
  ValidateShape = true
  expr: Constraints[11] = 2 * (<<Parameters>>.station_diameter + <<Parameters>>.thickness)
  expr: Constraints[8] = <<Parameters>>.thickness
  expr: Constraints[9] = <<Parameters>>.station_diameter + <<Parameters>>.thickness
  sketch-geometry (4):
    g0: LineSegment StartX=173 StartY=0 StartZ=0 EndX=176 EndY=0 EndZ=0
    g1: LineSegment StartX=176 StartY=0 StartZ=0 EndX=176 EndY=-88 EndZ=0
    g2: LineSegment StartX=176 StartY=-88 StartZ=0 EndX=173 EndY=-88 EndZ=0
    g3: LineSegment StartX=173 StartY=-88 StartZ=0 EndX=173 EndY=0 EndZ=0
  constraints (12):
    c: Coincident(g0,g1)
    c: Coincident(g1,g2)
    c: Coincident(g2,g3)
    c: Coincident(g3,g0)
    c: Horizontal(g0)
    c: Horizontal(g2)
    c: Vertical(g1)
    c: Vertical(g3)
    c: DistanceX(g2,g1) = 3
    c: DistanceY(g2,g-1) = 88
    c: PointOnObject(g0,g-1)
    c: DistanceX(g-1,g0) = 176
FEATURE [PartDesign::Pad] Pad032
  AddSubType = 0
  AlongSketchNormal = false
  AutoTaperInnerAngle = true
  BaseFeature = -> Pocket031
  CheckUpToFaceLimits = true
  ClaimChildren = false
  Direction = (0,0,1)
  Fit = 0
  FitJoin = 0
  InnerFit = 0
  InnerFitJoin = 0
  InvalidShape = false
  Length = 19
  Length2 = 100
  Linearize = true
  NewSolid = false
  Profile = -> Sketch067
  Suppress = false
  TaperInnerAngle = 0
  TaperInnerAngleRev = 0
  TreeRank = 285
  Type = 0
  ValidateShape = true
  _ProfileBasedVersion = 1
  expr: Length = <<Parameters>>.motor_shaft_length
FEATURE [Sketcher::SketchObject] Sketch068
  ArcFitTolerance = 1e-06
  AttachmentSupport = -> [XY_Plane012]
  ExternalBSplineMaxDegree = 5
  ExternalBSplineTolerance = 0.0001
  FullyConstrained = true
  InternalTolerance = 1e-06
  InvalidShape = false
  MakeInternals = false
  MapMode = 5
  Support = -> [XY_Plane012]
  TreeRank = 197
  ValidateShape = true
  expr: Constraints[10] = <<Parameters>>.station_diameter - 2 * <<Parameters>>.thickness
  expr: Constraints[11] = 2 * <<Parameters>>.station_diameter + <<Parameters>>.thickness
  expr: Constraints[8] = <<Parameters>>.thickness
  expr: Constraints[9] = <<Parameters>>.station_diameter + <<Parameters>>.thickness
  sketch-geometry (4):
    g0: LineSegment StartX=170 StartY=-88 StartZ=0 EndX=173 EndY=-88 EndZ=0
    g1: LineSegment StartX=173 StartY=-88 StartZ=0 EndX=173 EndY=-9 EndZ=0
    g2: LineSegment StartX=173 StartY=-9 StartZ=0 EndX=170 EndY=-9 EndZ=0
    g3: LineSegment StartX=170 StartY=-9 StartZ=0 EndX=170 EndY=-88 EndZ=0
  constraints (12):
    c: Coincident(g0,g1)
    c: Coincident(g1,g2)
    c: Coincident(g2,g3)
    c: Coincident(g3,g0)
    c: Horizontal(g0)
    c: Horizontal(g2)
    c: Vertical(g1)
    c: Vertical(g3)
    c: DistanceX(g0,g0) = 3
    c: DistanceY(g0,g-1) = 88
    c: DistanceY(g0,g2) = 79
    c: DistanceX(g-1,g1) = 173
FEATURE [PartDesign::Pad] Pad033
  AddSubType = 0
  AlongSketchNormal = false
  AutoTaperInnerAngle = true
  BaseFeature = -> Pad032
  CheckUpToFaceLimits = true
  ClaimChildren = false
  Direction = (0,0,1)
  Fit = 0
  FitJoin = 0
  InnerFit = 0
  InnerFitJoin = 0
  InvalidShape = false
  Length = 6
  Length2 = 6
  Linearize = true
  NewSolid = false
  Profile = -> Sketch068
  Suppress = false
  TaperInnerAngle = 0
  TaperInnerAngleRev = 0
  TreeRank = 286
  Type = 4
  ValidateShape = true
  _ProfileBasedVersion = 1
  expr: Length = <<Parameters>>.thickness * 2
  expr: Length2 = <<Parameters>>.thickness * 2
FEATURE [PartDesign::Chamfer] Chamfer009
  AddSubType = 0
  Angle = 45
  Base = -> Pad033 [Edge66]
  BaseFeature = -> Pad033
  ChamferType = 0
  FlipDirection = false
  InvalidShape = false
  NewSolid = false
  Size = 2.99
  Size2 = 1
  SupportTransform = false
  Suppress = false
  TreeRank = 287
  ValidateShape = true
  expr: Size = <<Parameters>>.thickness - 0.01
FEATURE [PartDesign::Chamfer] Chamfer010
  AddSubType = 0
  Angle = 45
  Base = -> Chamfer009 [Edge85]
  BaseFeature = -> Chamfer009
  ChamferType = 0
  FlipDirection = false
  InvalidShape = false
  NewSolid = false
  Size = 1.5
  Size2 = 1
  SupportTransform = false
  Suppress = false
  TreeRank = 288
  ValidateShape = true
  expr: Size = <<Parameters>>.thickness / 2
FEATURE [PartDesign::Fillet] Fillet017
  AddSubType = 0
  Base = -> Chamfer010 [Edge39,Edge37,Edge45]
  BaseFeature = -> Chamfer010
  InvalidShape = false
  NewSolid = false
  Radius = 2.99
  SupportTransform = false
  Suppress = false
  TreeRank = 289
  ValidateShape = true
  expr: Radius = <<Parameters>>.thickness - 0.01
FEATURE [Sketcher::SketchObject] Sketch069
  ArcFitTolerance = 1e-06
  ExternalBSplineMaxDegree = 5
  ExternalBSplineTolerance = 0.0001
  FullyConstrained = true
  InternalTolerance = 1e-06
  InvalidShape = false
  MakeInternals = false
  MapMode = 2
  Placement = pos=(0,0,30) rot=(0,0,1;0rad)
  TreeRank = 290
  ValidateShape = true
  expr: Placement.Base.z = <<Parameters>>.motor_height
  expr: Constraints[10] = <<Parameters>>.power_connector_width
  expr: Constraints[12] = <<Parameters>>.station_diameter + <<Parameters>>.thickness
  sketch-geometry (5):
    g0: LineSegment StartX=13.4 StartY=74.6 StartZ=0 EndX=13.4 EndY=101.4 EndZ=0
    g1: LineSegment StartX=13.4 StartY=101.4 StartZ=0 EndX=-13.4 EndY=101.4 EndZ=0
    g2: LineSegment StartX=-13.4 StartY=101.4 StartZ=0 EndX=-13.4 EndY=74.6 EndZ=0
    g3: LineSegment StartX=-13.4 StartY=74.6 StartZ=0 EndX=13.4 EndY=74.6 EndZ=0
    g4: GeomPoint [constr] X=0 Y=88 Z=0
  constraints (13):
    c: Coincident(g0,g1)
    c: Coincident(g1,g2)
    c: Coincident(g2,g3)
    c: Coincident(g3,g0)
    c: Horizontal(g1)
    c: Horizontal(g3)
    c: Vertical(g0)
    c: Vertical(g2)
    c: Symmetric(g1,g0,g4)
    c: PointOnObject(g4,g-2)
    c: DistanceX(g1,g0) = 26.8
    c: Equal(g1,g0)
    c: DistanceY(g-1,g4) = 88
FEATURE [PartDesign::Pocket] Pocket032
  AddSubType = 1
  AutoTaperInnerAngle = true
  BaseFeature = -> Pocket014
  CheckUpToFaceLimits = true
  ClaimChildren = false
  Fit = 0
  FitJoin = 0
  InnerFit = 0
  InnerFitJoin = 0
  InvalidShape = false
  Length = 19.9
  Length2 = 100
  Linearize = true
  NewSolid = false
  Profile = -> Sketch069
  Suppress = false
  TaperInnerAngle = 0
  TaperInnerAngleRev = 0
  TreeRank = 291
  Type = 0
  ValidateShape = true
  _ProfileBasedVersion = 1
  _Version = 1
  expr: Length = <<Parameters>>.power_connector_height
FEATURE [PartDesign::Body] Body004  label="Bottom-Back-Right"
  AutoGroupSolids = false
  ClaimAllChildren = false
  ExportMode = 0
  Group = -> [Sketch021,Pad010,Sketch022,Pad011,Sketch023,Pocket010,Sketch024,Pocket011,Fillet008,Fillet009,Pocket012,Sketch025,Pocket013,Pocket014,Sketch026,Sketch027,Sketch069,Pocket032]
  InvalidShape = false
  Origin = -> Origin004
  Placement = pos=(88,88,-30) rot=(0.57735,0.57735,0.57735;0rad)
  Tip = -> Pocket032
  TreeRank = 121
  ValidateShape = true
  _ExportChildren = -> [Pad010,Pad011,Pocket010,Pocket011,Fillet008,Fillet009,Pocket012,Pocket013,Pocket014,Pocket032]
  _GroupVersion = 1
  expr: Placement.Base.x = <<Parameters>>.station_diameter + <<Parameters>>.thickness
  expr: Placement.Base.y = <<Parameters>>.station_diameter + <<Parameters>>.thickness
  expr: Placement.Base.z = -<<Parameters>>.motor_height
FEATURE [Sketcher::SketchObject] Sketch070
  ArcFitTolerance = 1e-06
  ExternalBSplineMaxDegree = 5
  ExternalBSplineTolerance = 0.0001
  FullyConstrained = true
  InternalTolerance = 1e-06
  InvalidShape = false
  MakeInternals = false
  MapMode = 2
  Placement = pos=(0,0,-19) rot=(0,0,1;0rad)
  TreeRank = 292
  ValidateShape = true
  expr: Placement.Base.z = -<<Parameters>>.motor_shaft_length
  expr: Constraints[10] = <<Parameters>>.station_diameter + <<Parameters>>.thickness
  expr: Constraints[12] = <<Parameters>>.power_connector_width
  sketch-geometry (5):
    g0: LineSegment StartX=13.4 StartY=101.4 StartZ=0 EndX=13.4 EndY=74.6 EndZ=0
    g1: LineSegment StartX=13.4 StartY=74.6 StartZ=0 EndX=-13.4 EndY=74.6 EndZ=0
    g2: LineSegment StartX=-13.4 StartY=74.6 StartZ=0 EndX=-13.4 EndY=101.4 EndZ=0
    g3: LineSegment StartX=-13.4 StartY=101.4 StartZ=0 EndX=13.4 EndY=101.4 EndZ=0
    g4: GeomPoint [constr] X=-1e-16 Y=88 Z=0
  constraints (13):
    c: Coincident(g0,g1)
    c: Coincident(g1,g2)
    c: Coincident(g2,g3)
    c: Coincident(g3,g0)
    c: Horizontal(g1)
    c: Horizontal(g3)
    c: Vertical(g0)
    c: Vertical(g2)
    c: Symmetric(g1,g0,g4)
    c: PointOnObject(g4,g-2)
    c: DistanceY(g-1,g4) = 88
    c: Equal(g3,g0)
    c: DistanceX(g2,g0) = 26.8
FEATURE [PartDesign::Pocket] Pocket033
  AddSubType = 1
  AutoTaperInnerAngle = true
  BaseFeature = -> Pocket007
  CheckUpToFaceLimits = true
  ClaimChildren = false
  Fit = 0
  FitJoin = 0
  InnerFit = 0
  InnerFitJoin = 0
  InvalidShape = false
  Length = 19.9
  Length2 = 100
  Linearize = true
  NewSolid = false
  Profile = -> Sketch070
  Suppress = false
  TaperInnerAngle = 0
  TaperInnerAngleRev = 0
  TreeRank = 293
  Type = 0
  ValidateShape = true
  _ProfileBasedVersion = 1
  _Version = 1
  expr: Length = <<Parameters>>.power_connector_height
FEATURE [PartDesign::Body] Body003  label="Top-Back-Right"
  AutoGroupSolids = false
  ClaimAllChildren = false
  ExportMode = 0
  Group = -> [Sketch013,Pad007,Sketch014,Pad008,Sketch015,Pad009,Sketch016,Pocket005,Chamfer004,Chamfer006,Fillet004,Fillet007,Pocket007,Sketch018,Sketch070,Pocket033]
  InvalidShape = false
  Origin = -> Origin003
  Placement = pos=(88,88,19) rot=(0.57735,0.57735,0.57735;0rad)
  Tip = -> Pocket033
  TreeRank = 86
  ValidateShape = true
  _ExportChildren = -> [Pad007,Pad008,Pad009,Pocket005,Chamfer004,Chamfer006,Fillet004,Fillet007,Pocket007,Pocket033]
  _GroupVersion = 1
  expr: Placement.Base.x = <<Parameters>>.station_diameter + <<Parameters>>.thickness
  expr: Placement.Base.y = <<Parameters>>.station_diameter + <<Parameters>>.thickness
  expr: Placement.Base.z = <<Parameters>>.motor_shaft_length
FEATURE [Sketcher::SketchObject] Sketch071
  ArcFitTolerance = 1e-06
  ExternalBSplineMaxDegree = 5
  ExternalBSplineTolerance = 0.0001
  FullyConstrained = true
  InternalTolerance = 1e-06
  InvalidShape = false
  MakeInternals = false
  MapMode = 5
  Placement = pos=(-176,0,0) rot=(0.57735,-0.57735,-0.57735;2.0944rad)
  TreeRank = 294
  ValidateShape = true
  expr: Constraints[0] = <<Parameters>>.fan_screw_hole_diameter
  expr: Constraints[12] = <<Parameters>>.fan_diameter
  expr: Constraints[13] = <<Parameters>>.station_diameter * 1.25 + <<Parameters>>.thickness
  expr: Constraints[14] = <<Parameters>>.fan_diameter / 2 - <<Parameters>>.thickness
  expr: Constraints[4] = <<Parameters>>.fan_screw_distance
  expr: Constraints[6] = <<Parameters>>.fan_screw_distance
  expr: Constraints[9] = 0
  sketch-geometry (6):
    g0: GeomPoint [constr] X=109.25 Y=-11 Z=0
    g1: Circle CenterX=95.25 CenterY=3 CenterZ=0 NormalX=0 NormalY=0 NormalZ=1 AngleXU=0 Radius=1.3
    g2: Circle CenterX=123.25 CenterY=3 CenterZ=0 NormalX=0 NormalY=0 NormalZ=1 AngleXU=0 Radius=1.3
    g3: Circle CenterX=95.25 CenterY=-25 CenterZ=0 NormalX=0 NormalY=0 NormalZ=1 AngleXU=0 Radius=1.3
    g4: Circle CenterX=123.25 CenterY=-25 CenterZ=0 NormalX=0 NormalY=0 NormalZ=1 AngleXU=0 Radius=1.3
    g5: Circle CenterX=109.25 CenterY=-11 CenterZ=0 NormalX=0 NormalY=0 NormalZ=1 AngleXU=0 Radius=14
  constraints (15):
    c: Diameter(g1) = 2.6
    c: Equal(g1,g2)
    c: Equal(g1,g3)
    c: Equal(g1,g4)
    c: DistanceY(g4,g2) = 28
    c: DistanceX(g2,g4) = 0
    c: DistanceX(g3,g4) = 28
    c: DistanceX(g3,g1) = 0
    c: DistanceY(g3,g4) = 0
    c: DistanceY(g1,g2) = 0
    c: Symmetric(g2,g3,g0)
    c: Coincident(g5,g0)
    c: Diameter(g5) = 28
    c: DistanceX(g-1,g5) = 109.25
    c: DistanceY(g5,g-1) = 11
FEATURE [PartDesign::Pocket] Pocket034
  AddSubType = 1
  AutoTaperInnerAngle = true
  BaseFeature = -> Fillet011
  CheckUpToFaceLimits = true
  ClaimChildren = false
  Fit = 0
  FitJoin = 0
  InnerFit = 0
  InnerFitJoin = 0
  InvalidShape = false
  Length = 3
  Length2 = 100
  Linearize = true
  NewSolid = false
  Profile = -> Sketch071
  Suppress = false
  TaperInnerAngle = 0
  TaperInnerAngleRev = 0
  TreeRank = 295
  Type = 0
  ValidateShape = true
  _ProfileBasedVersion = 1
  _Version = 1
  expr: Length = <<Parameters>>.thickness
FEATURE [Sketcher::SketchObject] Sketch072
  ArcFitTolerance = 1e-06
  ExternalBSplineMaxDegree = 5
  ExternalBSplineTolerance = 0.0001
  FullyConstrained = true
  InternalTolerance = 1e-06
  InvalidShape = false
  MakeInternals = false
  MapMode = 5
  Placement = pos=(176,0,0) rot=(0.57735,0.57735,0.57735;2.0944rad)
  TreeRank = 296
  ValidateShape = true
  expr: Constraints[0] = <<Parameters>>.fan_screw_hole_diameter
  expr: Constraints[12] = <<Parameters>>.fan_diameter
  expr: Constraints[13] = <<Parameters>>.fan_diameter / 2 - <<Parameters>>.thickness
  expr: Constraints[14] = <<Parameters>>.station_diameter * 1.25 + <<Parameters>>.thickness
  expr: Constraints[4] = <<Parameters>>.fan_screw_distance
  expr: Constraints[6] = <<Parameters>>.fan_screw_distance
  expr: Constraints[9] = 0
  sketch-geometry (6):
    g0: GeomPoint [constr] X=-109.25 Y=-11 Z=0
    g1: Circle CenterX=-123.25 CenterY=3 CenterZ=0 NormalX=0 NormalY=0 NormalZ=1 AngleXU=0 Radius=1.3
    g2: Circle CenterX=-95.25 CenterY=3 CenterZ=0 NormalX=0 NormalY=0 NormalZ=1 AngleXU=0 Radius=1.3
    g3: Circle CenterX=-123.25 CenterY=-25 CenterZ=0 NormalX=0 NormalY=0 NormalZ=1 AngleXU=0 Radius=1.3
    g4: Circle CenterX=-95.25 CenterY=-25 CenterZ=0 NormalX=0 NormalY=0 NormalZ=1 AngleXU=0 Radius=1.3
    g5: Circle CenterX=-109.25 CenterY=-11 CenterZ=0 NormalX=0 NormalY=0 NormalZ=1 AngleXU=0 Radius=14
  constraints (15):
    c: Diameter(g1) = 2.6
    c: Equal(g1,g2)
    c: Equal(g1,g3)
    c: Equal(g1,g4)
    c: DistanceY(g4,g2) = 28
    c: DistanceX(g2,g4) = 0
    c: DistanceX(g3,g4) = 28
    c: DistanceX(g3,g1) = 0
    c: DistanceY(g3,g4) = 0
    c: DistanceY(g1,g2) = 0
    c: Symmetric(g2,g3,g0)
    c: Coincident(g5,g0)
    c: Diameter(g5) = 28
    c: DistanceY(g5,g-1) = 11
    c: DistanceX(g5,g-1) = 109.25
FEATURE [PartDesign::Pocket] Pocket035
  AddSubType = 1
  AutoTaperInnerAngle = true
  BaseFeature = -> Pocket028
  CheckUpToFaceLimits = true
  ClaimChildren = false
  Fit = 0
  FitJoin = 0
  InnerFit = 0
  InnerFitJoin = 0
  InvalidShape = false
  Length = 3
  Length2 = 100
  Linearize = true
  NewSolid = false
  Profile = -> Sketch072
  Suppress = false
  TaperInnerAngle = 0
  TaperInnerAngleRev = 0
  TreeRank = 297
  Type = 0
  ValidateShape = true
  _ProfileBasedVersion = 1
  _Version = 1
  expr: Length = <<Parameters>>.thickness
FEATURE [Sketcher::SketchObject] Sketch078
  ArcFitTolerance = 1e-06
  AttachmentSupport = -> [Pocket034]
  ExternalBSplineMaxDegree = 5
  ExternalBSplineTolerance = 0.0001
  FullyConstrained = true
  InternalTolerance = 1e-06
  InvalidShape = false
  MakeInternals = false
  MapMode = 5
  Placement = pos=(-3.81e-14,-76.8891,76.8891) rot=(1,0,0;0.785398rad)
  Support = -> [Pocket034]
  TreeRank = 320
  ValidateShape = true
  expr: Constraints[10] = <<Parameters>>.screen_position
  expr: Constraints[11] = Spreadsheet.screen_opening_width
  expr: Constraints[12] = Spreadsheet.screen_opening_height
  sketch-geometry (5):
    g0: LineSegment StartX=116 StartY=-136.75 StartZ=0 EndX=116 EndY=-47.25 EndZ=0
    g1: LineSegment StartX=116 StartY=-47.25 StartZ=0 EndX=-116 EndY=-47.25 EndZ=0
    g2: LineSegment StartX=-116 StartY=-47.25 StartZ=0 EndX=-116 EndY=-136.75 EndZ=0
    g3: LineSegment StartX=-116 StartY=-136.75 StartZ=0 EndX=116 EndY=-136.75 EndZ=0
    g4: GeomPoint [constr] X=0 Y=-92 Z=0
  constraints (13):
    c: Coincident(g0,g1)
    c: Coincident(g1,g2)
    c: Coincident(g2,g3)
    c: Coincident(g3,g0)
    c: Horizontal(g1)
    c: Horizontal(g3)
    c: Vertical(g0)
    c: Vertical(g2)
    c: Symmetric(g1,g0,g4)
    c: PointOnObject(g4,g-2)
    c: DistanceY(g4,g-1) = 92
    c: DistanceX(g1,g0) = 232
    c: DistanceY(g0,g0) = 89.5
FEATURE [PartDesign::Pocket] Pocket036
  AddSubType = 1
  AutoTaperInnerAngle = true
  BaseFeature = -> Pocket034
  CheckUpToFaceLimits = true
  ClaimChildren = false
  Fit = 0
  FitJoin = 0
  InnerFit = 0
  InnerFitJoin = 0
  InvalidShape = false
  Length = 5.5
  Length2 = 100
  Linearize = true
  NewSolid = false
  Profile = -> Sketch078
  Suppress = false
  TaperInnerAngle = 0
  TaperInnerAngleRev = 0
  TreeRank = 321
  Type = 0
  ValidateShape = true
  _ProfileBasedVersion = 1
  _Version = 1
  expr: Length = <<Parameters>>.screen_body_thickness
FEATURE [Sketcher::SketchObject] Sketch079
  ArcFitTolerance = 1e-06
  AttachmentSupport = -> [Pocket035]
  ExternalBSplineMaxDegree = 5
  ExternalBSplineTolerance = 0.0001
  FullyConstrained = false
  InternalTolerance = 1e-06
  InvalidShape = false
  MakeInternals = false
  MapMode = 5
  Placement = pos=(-3.81e-14,-76.8891,76.8891) rot=(1,0,0;0.785398rad)
  Support = -> [Pocket035]
  TreeRank = 322
  ValidateShape = true
  expr: Constraints[10] = <<Parameters>>.screen_position
  expr: Constraints[11] = Spreadsheet.screen_opening_width
  expr: Constraints[12] = Spreadsheet.screen_opening_height
  expr: Constraints[13] = <<Parameters>>.power_switch_diameter
  sketch-geometry (6):
    g0: LineSegment StartX=-116 StartY=-136.75 StartZ=0 EndX=-116 EndY=-47.25 EndZ=0
    g1: LineSegment StartX=-116 StartY=-47.25 StartZ=0 EndX=116 EndY=-47.25 EndZ=0
    g2: LineSegment StartX=116 StartY=-47.25 StartZ=0 EndX=116 EndY=-136.75 EndZ=0
    g3: LineSegment StartX=116 StartY=-136.75 StartZ=0 EndX=-116 EndY=-136.75 EndZ=0
    g4: GeomPoint [constr] X=0 Y=-92 Z=0
    g5: Circle CenterX=142.523 CenterY=-66.2672 CenterZ=0 NormalX=0 NormalY=0 NormalZ=1 AngleXU=0 Radius=9.75
  constraints (14):
    c: Coincident(g0,g1)
    c: Coincident(g1,g2)
    c: Coincident(g2,g3)
    c: Coincident(g3,g0)
    c: Horizontal(g1)
    c: Horizontal(g3)
    c: Vertical(g0)
    c: Vertical(g2)
    c: Symmetric(g1,g0,g4)
    c: PointOnObject(g4,g-2)
    c: DistanceY(g4,g-1) = 92
    c: DistanceX(g0,g1) = 232
    c: DistanceY(g2,g1) = 89.5
    c: Diameter(g5) = 19.5
FEATURE [PartDesign::Pocket] Pocket037
  AddSubType = 1
  AutoTaperInnerAngle = true
  BaseFeature = -> Pocket035
  CheckUpToFaceLimits = true
  ClaimChildren = false
  Fit = 0
  FitJoin = 0
  InnerFit = 0
  InnerFitJoin = 0
  InvalidShape = false
  Length = 5.5
  Length2 = 100
  Linearize = true
  NewSolid = false
  Profile = -> Sketch079
  Suppress = false
  TaperInnerAngle = 0
  TaperInnerAngleRev = 0
  TreeRank = 323
  Type = 0
  ValidateShape = true
  _ProfileBasedVersion = 1
  _Version = 1
  expr: Length = <<Parameters>>.screen_body_thickness
FEATURE [PartDesign::Fillet] Fillet018
  AddSubType = 0
  Base = -> Pocket037 [Edge108,Edge115,Edge121,Edge14]
  BaseFeature = -> Pocket037
  InvalidShape = false
  NewSolid = false
  Radius = 3
  SupportTransform = false
  Suppress = false
  TreeRank = 324
  ValidateShape = true
  expr: Radius = <<Parameters>>.thickness
FEATURE [Sketcher::SketchObject] Sketch084
  ArcFitTolerance = 1e-06
  AttachmentSupport = -> [Pocket036]
  ExternalBSplineMaxDegree = 5
  ExternalBSplineTolerance = 0.0001
  FullyConstrained = true
  InternalTolerance = 1e-06
  InvalidShape = false
  MakeInternals = false
  MapMode = 5
  Placement = pos=(-3.81e-14,-76.8891,76.8891) rot=(1,0,0;0.785398rad)
  Support = -> [Pocket036]
  TreeRank = 343
  ValidateShape = true
  expr: Constraints[10] = <<Parameters>>.screen_opening_width + 2 * <<Parameters>>.screen_relief_width
  expr: Constraints[11] = <<Parameters>>.screen_opening_height + 2 * <<Parameters>>.screen_relief_width
  expr: Constraints[12] = <<Parameters>>.screen_position
  sketch-geometry (5):
    g0: LineSegment StartX=117.5 StartY=-138.25 StartZ=0 EndX=117.5 EndY=-45.75 EndZ=0
    g1: LineSegment StartX=117.5 StartY=-45.75 StartZ=0 EndX=-117.5 EndY=-45.75 EndZ=0
    g2: LineSegment StartX=-117.5 StartY=-45.75 StartZ=0 EndX=-117.5 EndY=-138.25 EndZ=0
    g3: LineSegment StartX=-117.5 StartY=-138.25 StartZ=0 EndX=117.5 EndY=-138.25 EndZ=0
    g4: GeomPoint [constr] X=0 Y=-92 Z=0
  constraints (13):
    c: Coincident(g0,g1)
    c: Coincident(g1,g2)
    c: Coincident(g2,g3)
    c: Coincident(g3,g0)
    c: Horizontal(g1)
    c: Horizontal(g3)
    c: Vertical(g0)
    c: Vertical(g2)
    c: Symmetric(g1,g0,g4)
    c: PointOnObject(g4,g-2)
    c: DistanceX(g1,g0) = 235
    c: DistanceY(g0,g0) = 92.5
    c: DistanceY(g4,g-1) = 92
FEATURE [PartDesign::Pocket] Pocket040
  AddSubType = 1
  AutoTaperInnerAngle = true
  BaseFeature = -> Pocket036
  CheckUpToFaceLimits = true
  ClaimChildren = false
  Fit = 0
  FitJoin = 0
  InnerFit = 0
  InnerFitJoin = 0
  InvalidShape = false
  Length = 2
  Length2 = 100
  Linearize = true
  NewSolid = false
  Profile = -> Sketch084
  Suppress = false
  TaperInnerAngle = 0
  TaperInnerAngleRev = 0
  TreeRank = 344
  Type = 0
  ValidateShape = true
  _ProfileBasedVersion = 1
  _Version = 1
  expr: Length = <<Parameters>>.screen_relief_depth
FEATURE [Sketcher::SketchObject] Sketch085
  ArcFitTolerance = 1e-06
  AttachmentSupport = -> [Fillet018]
  ExternalBSplineMaxDegree = 5
  ExternalBSplineTolerance = 0.0001
  FullyConstrained = true
  InternalTolerance = 1e-06
  InvalidShape = false
  MakeInternals = false
  MapMode = 5
  Placement = pos=(-3.81e-14,-76.8891,76.8891) rot=(1,0,0;0.785398rad)
  Support = -> [Fillet018]
  TreeRank = 345
  ValidateShape = true
  expr: Constraints[10] = <<Parameters>>.screen_opening_height + 2 * <<Parameters>>.screen_relief_width
  expr: Constraints[11] = <<Parameters>>.screen_opening_width + 2 * <<Parameters>>.screen_relief_width
  expr: Constraints[12] = <<Parameters>>.screen_position
  sketch-geometry (5):
    g0: LineSegment StartX=-117.5 StartY=-138.25 StartZ=0 EndX=-117.5 EndY=-45.75 EndZ=0
    g1: LineSegment StartX=-117.5 StartY=-45.75 StartZ=0 EndX=117.5 EndY=-45.75 EndZ=0
    g2: LineSegment StartX=117.5 StartY=-45.75 StartZ=0 EndX=117.5 EndY=-138.25 EndZ=0
    g3: LineSegment StartX=117.5 StartY=-138.25 StartZ=0 EndX=-117.5 EndY=-138.25 EndZ=0
    g4: GeomPoint [constr] X=0 Y=-92 Z=0
  constraints (13):
    c: Coincident(g0,g1)
    c: Coincident(g1,g2)
    c: Coincident(g2,g3)
    c: Coincident(g3,g0)
    c: Horizontal(g1)
    c: Horizontal(g3)
    c: Vertical(g0)
    c: Vertical(g2)
    c: Symmetric(g1,g0,g4)
    c: PointOnObject(g4,g-2)
    c: DistanceY(g2,g1) = 92.5
    c: DistanceX(g0,g1) = 235
    c: DistanceY(g4,g-1) = 92
FEATURE [PartDesign::Pocket] Pocket041
  AddSubType = 1
  AutoTaperInnerAngle = true
  BaseFeature = -> Fillet018
  CheckUpToFaceLimits = true
  ClaimChildren = false
  Fit = 0
  FitJoin = 0
  InnerFit = 0
  InnerFitJoin = 0
  InvalidShape = false
  Length = 2
  Length2 = 100
  Linearize = true
  NewSolid = false
  Profile = -> Sketch085
  Suppress = false
  TaperInnerAngle = 0
  TaperInnerAngleRev = 0
  TreeRank = 346
  Type = 0
  ValidateShape = true
  _ProfileBasedVersion = 1
  _Version = 1
  expr: Length = <<Parameters>>.screen_relief_depth
FEATURE [PartDesign::Fillet] Fillet019
  AddSubType = 0
  Base = -> Pocket040 [Edge32,Edge43,Edge212,Face75,Edge75,Edge85,Edge154,Edge155,Edge70,Edge73]
  BaseFeature = -> Pocket040
  InvalidShape = false
  NewSolid = false
  Radius = 1
  SupportTransform = false
  Suppress = false
  TreeRank = 347
  ValidateShape = true
FEATURE [PartDesign::Body] Body007  label="Bottom-Front-Left (A)"
  AutoGroupSolids = false
  ClaimAllChildren = false
  ExportMode = 0
  Group = -> [Sketch034,Pad015,Sketch035,Pad016,Sketch036,Pad017,Sketch037,Pad018,Sketch038,Pocket018,Sketch039,Pocket019,Sketch040,Pocket020,Sketch041,Pocket021,Sketch042,Pocket022,Fillet011,Sketch071,Pocket034,Sketch078,Pocket036,Sketch084,Pocket040,Fillet019]
  InvalidShape = false
  Origin = -> Origin007
  Tip = -> Fillet019
  TreeRank = 175
  ValidateShape = true
  _ExportChildren = -> [Pad015,Pad016,Pad017,Pad018,Pocket018,Pocket019,Pocket020,Pocket021,Pocket022,Fillet011,Pocket034,Pocket036,Pocket040,Fillet019]
  _GroupVersion = 1
FEATURE [PartDesign::Fillet] Fillet020
  AddSubType = 0
  Base = -> Pocket041 [Edge127,Edge61,Edge5,Edge25,Edge6,Edge73,Edge72,Face19,Face35]
  BaseFeature = -> Pocket041
  InvalidShape = false
  NewSolid = false
  Radius = 1
  SupportTransform = false
  Suppress = false
  TreeRank = 348
  ValidateShape = true
FEATURE [PartDesign::Body] Body011  label="Bottom-Front-Right (A)"
  AutoGroupSolids = false
  ClaimAllChildren = false
  ExportMode = 0
  Group = -> [Pad026,Sketch052,Pad027,Sketch053,Pad028,Sketch054,Pad029,Sketch055,Pocket024,Pocket025,Sketch057,Sketch058,Pocket026,Sketch059,Pocket027,Pocket028,Sketch060,Sketch061,Sketch072,Pocket035,Sketch079,Pocket037,Fillet018,Sketch085,Pocket041,Fillet020]
  InvalidShape = false
  Origin = -> Origin011
  Tip = -> Fillet020
  TreeRank = 212
  ValidateShape = true
  _ExportChildren = -> [Pad026,Pad027,Pad028,Pad029,Pocket024,Pocket025,Pocket026,Pocket027,Pocket028,Pocket035,Pocket037,Fillet018,Pocket041,Fillet020]
  _GroupVersion = 1
FEATURE [Sketcher::SketchObject] Sketch086
  ArcFitTolerance = 1e-06
  AttachmentOffset = pos=(0,0,19) rot=(0,0,1;0rad)
  AttachmentSupport = -> [XY_Plane005]
  ExternalBSplineMaxDegree = 5
  ExternalBSplineTolerance = 0.0001
  FullyConstrained = true
  InternalTolerance = 1e-06
  InvalidShape = false
  MakeInternals = false
  MapMode = 5
  Placement = pos=(0,0,19) rot=(0,0,1;0rad)
  Support = -> [XY_Plane005]
  TreeRank = 349
  ValidateShape = true
  expr: AttachmentOffset.Base.z = <<Parameters>>.motor_shaft_length
  expr: Constraints[10] = <<Parameters>>.station_diameter
  expr: Constraints[23] = <<Parameters>>.station_diameter - 6 * <<Parameters>>.thickness
  expr: Constraints[25] = <<Parameters>>.station_diameter + <<Parameters>>.thickness
  expr: Constraints[27] = <<Parameters>>.station_diameter + <<Parameters>>.thickness
  expr: Constraints[28] = <<Parameters>>.thickness * 4
  expr: Constraints[9] = <<Parameters>>.thickness * 1.5
  sketch-geometry (11):
    g0: LineSegment StartX=-167 StartY=-85 StartZ=0 EndX=-167 EndY=-89.5 EndZ=0
    g1: LineSegment StartX=-167 StartY=-89.5 StartZ=0 EndX=-100 EndY=-89.5 EndZ=0
    g2: LineSegment StartX=-100 StartY=-89.5 StartZ=0 EndX=-100 EndY=-85 EndZ=0
    g3: LineSegment StartX=-100 StartY=-85 StartZ=0 EndX=-167 EndY=-85 EndZ=0
    g4: GeomPoint [constr] X=-133.5 Y=-87.25 Z=0
    g5: LineSegment StartX=-9 StartY=-89.5 StartZ=0 EndX=-9 EndY=-85 EndZ=0
    g6: LineSegment StartX=-9 StartY=-85 StartZ=0 EndX=-76 EndY=-85 EndZ=0
    g7: LineSegment StartX=-76 StartY=-85 StartZ=0 EndX=-76 EndY=-89.5 EndZ=0
    g8: LineSegment StartX=-76 StartY=-89.5 StartZ=0 EndX=-9 EndY=-89.5 EndZ=0
    g9: GeomPoint [constr] X=-42.5 Y=-87.25 Z=0
    g10: LineSegment [constr] StartX=-88 StartY=0 StartZ=0 EndX=-88 EndY=-88 EndZ=0
  constraints (29):
    c: Coincident(g0,g1)
    c: Coincident(g1,g2)
    c: Coincident(g2,g3)
    c: Coincident(g3,g0)
    c: Horizontal(g1)
    c: Horizontal(g3)
    c: Vertical(g0)
    c: Vertical(g2)
    c: Symmetric(g1,g0,g4)
    c: DistanceY(g1,g2) = 4.5
    c: DistanceY(g2,g-1) = 85
    c: Coincident(g5,g6)
    c: Coincident(g6,g7)
    c: Coincident(g7,g8)
    c: Coincident(g8,g5)
    c: Horizontal(g6)
    c: Horizontal(g8)
    c: Vertical(g5)
    c: Vertical(g7)
    c: Symmetric(g6,g5,g9)
    c: Equal(g3,g6)
    c: Equal(g2,g5)
    c: DistanceY(g9,g4) = 0
    c: DistanceX(g0,g1) = 67
    c: PointOnObject(g10,g-1)
    c: DistanceX(g10,g-1) = 88
    c: Symmetric(g4,g9,g10)
    c: DistanceY(g10,g10) = 88
    c: DistanceX(g2,g10) = 12
FEATURE [PartDesign::Pad] Pad037
  AddSubType = 0
  AlongSketchNormal = false
  AutoTaperInnerAngle = true
  BaseFeature = -> Fillet013
  CheckUpToFaceLimits = true
  ClaimChildren = false
  Direction = (0,0,1)
  Fit = 0
  FitJoin = 0
  InnerFit = 0
  InnerFitJoin = 0
  InvalidShape = false
  Length = 3
  Length2 = 100
  Linearize = true
  NewSolid = false
  Profile = -> Sketch086
  Reversed = true
  Suppress = false
  TaperInnerAngle = 0
  TaperInnerAngleRev = 0
  TreeRank = 350
  Type = 0
  ValidateShape = true
  _ProfileBasedVersion = 1
  expr: Length = <<Parameters>>.thickness
FEATURE [PartDesign::Chamfer] Chamfer011
  AddSubType = 0
  Angle = 45
  Base = -> Pad037 [Edge49,Edge45]
  BaseFeature = -> Pad037
  ChamferType = 0
  FlipDirection = false
  InvalidShape = false
  NewSolid = false
  Size = 2.99
  Size2 = 1
  SupportTransform = false
  Suppress = false
  TreeRank = 351
  ValidateShape = true
  expr: Size = <<Parameters>>.thickness - 0.01
FEATURE [Sketcher::SketchObject] Sketch087
  ArcFitTolerance = 1e-06
  AttachmentOffset = pos=(0,0,19) rot=(0,0,1;0rad)
  AttachmentSupport = -> [XY_Plane012]
  ExternalBSplineMaxDegree = 5
  ExternalBSplineTolerance = 0.0001
  FullyConstrained = true
  InternalTolerance = 1e-06
  InvalidShape = false
  MakeInternals = false
  MapMode = 5
  Placement = pos=(0,0,19) rot=(0,0,1;0rad)
  Support = -> [XY_Plane012]
  TreeRank = 349
  ValidateShape = true
  expr: AttachmentOffset.Base.z = <<Parameters>>.motor_shaft_length
  expr: Constraints[10] = <<Parameters>>.station_diameter
  expr: Constraints[23] = <<Parameters>>.station_diameter - 6 * <<Parameters>>.thickness
  expr: Constraints[26] = <<Parameters>>.station_diameter + <<Parameters>>.thickness
  expr: Constraints[27] = <<Parameters>>.thickness * 4
  expr: Constraints[28] = <<Parameters>>.station_diameter + <<Parameters>>.thickness
  expr: Constraints[9] = <<Parameters>>.thickness * 1.5
  sketch-geometry (11):
    g0: LineSegment StartX=9 StartY=-85 StartZ=0 EndX=9 EndY=-89.5 EndZ=0
    g1: LineSegment StartX=9 StartY=-89.5 StartZ=0 EndX=76 EndY=-89.5 EndZ=0
    g2: LineSegment StartX=76 StartY=-89.5 StartZ=0 EndX=76 EndY=-85 EndZ=0
    g3: LineSegment StartX=76 StartY=-85 StartZ=0 EndX=9 EndY=-85 EndZ=0
    g4: GeomPoint [constr] X=42.5 Y=-87.25 Z=0
    g5: LineSegment StartX=167 StartY=-89.5 StartZ=0 EndX=167 EndY=-85 EndZ=0
    g6: LineSegment StartX=167 StartY=-85 StartZ=0 EndX=100 EndY=-85 EndZ=0
    g7: LineSegment StartX=100 StartY=-85 StartZ=0 EndX=100 EndY=-89.5 EndZ=0
    g8: LineSegment StartX=100 StartY=-89.5 StartZ=0 EndX=167 EndY=-89.5 EndZ=0
    g9: GeomPoint [constr] X=133.5 Y=-87.25 Z=0
    g10: LineSegment [constr] StartX=88 StartY=0 StartZ=0 EndX=88 EndY=-88 EndZ=0
  constraints (29):
    c: Coincident(g0,g1)
    c: Coincident(g1,g2)
    c: Coincident(g2,g3)
    c: Coincident(g3,g0)
    c: Horizontal(g1)
    c: Horizontal(g3)
    c: Vertical(g0)
    c: Vertical(g2)
    c: Symmetric(g1,g0,g4)
    c: DistanceY(g1,g2) = 4.5
    c: DistanceY(g2,g-1) = 85
    c: Coincident(g5,g6)
    c: Coincident(g6,g7)
    c: Coincident(g7,g8)
    c: Coincident(g8,g5)
    c: Horizontal(g6)
    c: Horizontal(g8)
    c: Vertical(g5)
    c: Vertical(g7)
    c: Symmetric(g6,g5,g9)
    c: Equal(g3,g6)
    c: Equal(g2,g5)
    c: DistanceY(g9,g4) = 0
    c: DistanceX(g0,g1) = 67
    c: PointOnObject(g10,g-1)
    c: Symmetric(g4,g9,g10)
    c: DistanceY(g10,g10) = 88
    c: DistanceX(g2,g10) = 12
    c: DistanceX(g-1,g10) = 88
FEATURE [PartDesign::Pad] Pad038
  AddSubType = 0
  AlongSketchNormal = false
  AutoTaperInnerAngle = true
  BaseFeature = -> Fillet017
  CheckUpToFaceLimits = true
  ClaimChildren = false
  Direction = (0,0,1)
  Fit = 0
  FitJoin = 0
  InnerFit = 0
  InnerFitJoin = 0
  InvalidShape = false
  Length = 3
  Length2 = 100
  Linearize = true
  NewSolid = false
  Profile = -> Sketch087
  Reversed = true
  Suppress = false
  TaperInnerAngle = 0
  TaperInnerAngleRev = 0
  TreeRank = 352
  Type = 0
  ValidateShape = true
  _ProfileBasedVersion = 1
  expr: Length = <<Parameters>>.thickness
FEATURE [PartDesign::Chamfer] Chamfer012
  AddSubType = 0
  Angle = 45
  Base = -> Pad038 [Edge20,Edge14]
  BaseFeature = -> Pad038
  ChamferType = 0
  FlipDirection = false
  InvalidShape = false
  NewSolid = false
  Size = 2.99
  Size2 = 1
  SupportTransform = false
  Suppress = false
  TreeRank = 353
  ValidateShape = true
  expr: Size = <<Parameters>>.thickness - 0.01
FEATURE [PartDesign::Chamfer] Chamfer013
  AddSubType = 0
  Angle = 45
  Base = -> Chamfer011 [Edge119]
  BaseFeature = -> Chamfer011
  ChamferType = 0
  FlipDirection = false
  InvalidShape = false
  NewSolid = false
  Size = 1
  Size2 = 1
  SupportTransform = false
  Suppress = false
  TreeRank = 354
  ValidateShape = true
FEATURE [PartDesign::Body] Body005  label="Top-Front-Left"
  AutoGroupSolids = false
  ClaimAllChildren = false
  ExportMode = 0
  Group = -> [Sketch028,Pad012,Sketch029,Pocket015,Sketch031,Pad014,Sketch032,Pocket016,Sketch043,Pad019,Sketch044,Pad020,Chamfer007,Chamfer008,Fillet012,Fillet013,Sketch086,Pad037,Chamfer011,Chamfer013]
  InvalidShape = false
  Origin = -> Origin005
  Tip = -> Chamfer013
  TreeRank = 87
  ValidateShape = true
  _ExportChildren = -> [Pad012,Pocket015,Pad014,Pocket016,Pad019,Pad020,Chamfer007,Chamfer008,Fillet012,Fillet013,Pad037,Chamfer011,Chamfer013]
  _GroupVersion = 1
FEATURE [PartDesign::Chamfer] Chamfer014
  AddSubType = 0
  Angle = 45
  Base = -> Chamfer012 [Edge110]
  BaseFeature = -> Chamfer012
  ChamferType = 0
  FlipDirection = false
  InvalidShape = false
  NewSolid = false
  Size = 1
  Size2 = 1
  SupportTransform = false
  Suppress = false
  TreeRank = 355
  ValidateShape = true
FEATURE [PartDesign::Body] Body012  label="Top-Front-Right"
  AutoGroupSolids = false
  ClaimAllChildren = false
  ExportMode = 0
  Group = -> [Pad030,Pocket030,Sketch063,Sketch064,Pad031,Sketch065,Pocket031,Sketch066,Pad032,Pad033,Chamfer009,Chamfer010,Fillet017,Sketch067,Sketch068,Pad038,Chamfer012,Chamfer014,Sketch087]
  InvalidShape = false
  Origin = -> Origin012
  Tip = -> Chamfer014
  TreeRank = 88
  ValidateShape = true
  _ExportChildren = -> [Pad030,Pocket030,Pad031,Pocket031,Pad032,Pad033,Chamfer009,Chamfer010,Fillet017,Pad038,Chamfer012,Chamfer014]
  _GroupVersion = 1
FEATURE [Sketcher::SketchObject] Sketch088
  ArcFitTolerance = 1e-06
  AttachmentSupport = -> [YZ_Plane007]
  ExternalBSplineMaxDegree = 5
  ExternalBSplineTolerance = 0.0001
  FullyConstrained = false
  InternalTolerance = 1e-06
  InvalidShape = false
  MakeInternals = false
  MapMode = 5
  Placement = pos=(0,0,0) rot=(0.57735,0.57735,0.57735;2.0944rad)
  Support = -> [YZ_Plane007]
  TreeRank = 176
  ValidateShape = true
  expr: Constraints[12] = <<Parameters>>.thickness + <<Parameters>>.motor_screw_head_height
  expr: Constraints[13] = <<Parameters>>.motor_height
  expr: Constraints[14] = <<Parameters>>.thickness
  expr: Constraints[18] = <<Parameters>>.screen_body_thickness
  expr: Constraints[19] = (<<Parameters>>.station_diameter + <<Parameters>>.thickness) * 2
  expr: Constraints[20] = <<Parameters>>.screen_angle
  expr: Constraints[21] = <<Parameters>>.thickness
  expr: Constraints[25] = <<Parameters>>.thickness
  expr: Constraints[26] = <<Parameters>>.motor_shaft_length
  expr: Constraints[27] = <<Parameters>>.station_diameter + <<Parameters>>.thickness
  expr: Constraints[29] = <<Parameters>>.screen_overall_height + 2 * <<Parameters>>.thickness
  expr: Constraints[39] = <<Parameters>>.thickness
  sketch-geometry (19):
    g0: LineSegment StartX=0 StartY=-36.25 StartZ=0 EndX=-176 EndY=-36.25 EndZ=0
    g1: LineSegment StartX=0 StartY=-36.25 StartZ=0 EndX=0 EndY=-30 EndZ=0
    g2: LineSegment StartX=0 StartY=-30 StartZ=0 EndX=-94.3947 EndY=-30 EndZ=0
    g3: LineSegment StartX=-176 StartY=-36.25 StartZ=0 EndX=-176 EndY=-22.2218 EndZ=0
    g4: LineSegment StartX=-176 StartY=-22.2218 StartZ=0 EndX=-106.178 EndY=47.5998 EndZ=0
    g5: LineSegment StartX=-173 StartY=-30 StartZ=0 EndX=-173 EndY=-27 EndZ=0
    g6: LineSegment StartX=-173 StartY=-27 StartZ=0 EndX=-102.289 EndY=43.7107 EndZ=0
    g7: LineSegment [constr] StartX=-145.833 StartY=0.16655 StartZ=0 EndX=-149.723 EndY=4.05564 EndZ=0
    g8: LineSegment StartX=-88 StartY=22 StartZ=0 EndX=-96.7893 EndY=22 EndZ=0
    g9: LineSegment StartX=-88 StartY=22 StartZ=0 EndX=-88 EndY=19 EndZ=0
    g10: LineSegment StartX=-102.289 StartY=43.7107 StartZ=0 EndX=-102.289 EndY=19 EndZ=0
    g11: LineSegment StartX=-96.7893 StartY=43.7107 StartZ=0 EndX=-96.7893 EndY=22 EndZ=0
    g12: ArcOfCircle CenterX=-102.289 CenterY=43.7107 CenterZ=0 NormalX=0 NormalY=0 NormalZ=1 AngleXU=0 Radius=5.5 StartAngle=0 EndAngle=2.35619
    g13: LineSegment StartX=-97.3947 StartY=14.1053 StartZ=0 EndX=-97.3947 EndY=-30 EndZ=0
    g14: LineSegment StartX=-94.3947 StartY=14.1053 StartZ=0 EndX=-94.3947 EndY=-30 EndZ=0
    g15: LineSegment StartX=-97.3947 StartY=-30 StartZ=0 EndX=-173 EndY=-30 EndZ=0
    g16: LineSegment StartX=-102.289 StartY=19 StartZ=0 EndX=-97.3947 EndY=14.1053 EndZ=0
    g17: LineSegment StartX=-88 StartY=19 StartZ=0 EndX=-89.5 EndY=19 EndZ=0
    g18: LineSegment StartX=-89.5 StartY=19 StartZ=0 EndX=-94.3947 EndY=14.1053 EndZ=0
  constraints (55):
    c: PointOnObject(g0,g-2)
    c: Horizontal(g0)
    c: Coincident(g1,g0)
    c: PointOnObject(g1,g-2)
    c: Coincident(g2,g1)
    c: Horizontal(g2)
    c: Coincident(g3,g0)
    c: Vertical(g3)
    c: Coincident(g4,g3)
    c: Coincident(g5,g15)
    c: Vertical(g5)
    c: Coincident(g6,g5)
    c: DistanceY(g0,g1) = 6.25
    c: DistanceY(g1,g-1) = 30
    c: DistanceX(g0,g15) = 3
    c: Parallel(g6,g4)
    c: PointOnObject(g7,g6)
    c: Perpendicular(g4,g7)
    c: Distance(g7,g7) = 5.5
    c: DistanceX(g0,g-1) = 176
    c: Angle(g5,g6) = 2.35619
    c: DistanceY(g15,g5) = 3
    c: Horizontal(g8)
    c: Coincident(g9,g8)
    c: Vertical(g9)
    c: DistanceY(g9,g8) = 3
    c: DistanceY(g-1,g9) = 19
    c: DistanceX(g9,g-1) = 88
    c: PointOnObject(g7,g4)
    c: Distance(g6,g5) = 100
    c: Coincident(g10,g6)
    c: Vertical(g10)
    c: Coincident(g11,g8)
    c: Vertical(g11)
    c: Tangent(g4,g12) = 1.5708
    c: Tangent(g11,g12) = 1.5708
    c: Coincident(g12,g6)
    c: Vertical(g13)
    c: Vertical(g14)
    c: DistanceX(g13,g14) = 3
    c: Coincident(g2,g14)
    c: Coincident(g15,g13)
    c: Horizontal(g15)
    c: DistanceY(g13,g2) = 0
    c: Coincident(g16,g13)
    c: Angle(g16,g10) = 2.35619
    c: Coincident(g16,g10)
    c: DistanceY(g13,g14) = 0
    c: DistanceY(g9,g10) = 0
    c: Coincident(g17,g9)
    c: Horizontal(g17)
    c: Coincident(g18,g17)
    c: Coincident(g18,g14)
    c: DistanceX(g17,g9) = 1.5
    c: Angle(g18,g17) = 2.35619
FEATURE [PartDesign::Pad] Pad039
  AddSubType = 0
  AlongSketchNormal = false
  AutoTaperInnerAngle = true
  CheckUpToFaceLimits = true
  ClaimChildren = false
  Direction = (1,-2e-16,3e-16)
  Fit = 0
  FitJoin = 0
  InnerFit = 0
  InnerFitJoin = 0
  InvalidShape = false
  Length = 176
  Length2 = 100
  Linearize = true
  NewSolid = false
  Profile = -> Sketch088
  Reversed = true
  Suppress = false
  TaperInnerAngle = 0
  TaperInnerAngleRev = 0
  TreeRank = 177
  Type = 0
  ValidateShape = true
  _ProfileBasedVersion = 1
  expr: Length = (<<Parameters>>.station_diameter + <<Parameters>>.thickness) * 2
FEATURE [Sketcher::SketchObject] Sketch089
  ArcFitTolerance = 1e-06
  AttachmentSupport = -> [XY_Plane007]
  ExternalBSplineMaxDegree = 5
  ExternalBSplineTolerance = 0.0001
  FullyConstrained = true
  InternalTolerance = 1e-06
  InvalidShape = false
  MakeInternals = false
  MapMode = 5
  Support = -> [XY_Plane007]
  TreeRank = 178
  ValidateShape = true
  expr: Constraints[15] = (<<Parameters>>.station_diameter + <<Parameters>>.thickness) * 2
  expr: Constraints[1] = <<Parameters>>.motor_shaft_mount_diameter / 4
  expr: Constraints[21] = (<<Parameters>>.station_diameter + <<Parameters>>.thickness) * 2
  expr: Constraints[22] = <<Parameters>>.station_diameter / 3
  expr: Constraints[26] = <<Parameters>>.thickness
  expr: Constraints[2] = <<Parameters>>.motor_shaft_mount_diameter / 4
  expr: Constraints[30] = <<Parameters>>.thickness
  expr: Constraints[31] = <<Parameters>>.station_diameter / 3 / 2
  expr: Constraints[32] = <<Parameters>>.motor_shaft_mount_diameter / 4
  expr: Constraints[4] = <<Parameters>>.station_diameter + <<Parameters>>.thickness
  expr: Constraints[5] = <<Parameters>>.station_diameter + <<Parameters>>.thickness
  sketch-geometry (11):
    g0: Circle CenterX=-88 CenterY=-88 CenterZ=0 NormalX=0 NormalY=0 NormalZ=1 AngleXU=0 Radius=6.25
    g1: ArcOfCircle CenterX=-169.75 CenterY=0 CenterZ=0 NormalX=0 NormalY=0 NormalZ=1 AngleXU=0 Radius=6.25 StartAngle=4.16554 EndAngle=6.28319
    g2: ArcOfCircle CenterX=0 CenterY=0 CenterZ=0 NormalX=0 NormalY=0 NormalZ=1 AngleXU=0 Radius=12.5 StartAngle=3.14159 EndAngle=4.71239
    g3: LineSegment StartX=-12.5 StartY=0 StartZ=0 EndX=0 EndY=0 EndZ=0
    g4: LineSegment StartX=0 StartY=0 StartZ=0 EndX=0 EndY=-12.5 EndZ=0
    g5: LineSegment StartX=-176 StartY=0 StartZ=0 EndX=-163.5 EndY=0 EndZ=0
    g6: LineSegment StartX=-176 StartY=0 StartZ=0 EndX=-176 EndY=-176 EndZ=0
    g7: LineSegment StartX=-173 StartY=-5.33854 StartZ=0 EndX=-173 EndY=-159.155 EndZ=0
    g8: ArcOfCircle CenterX=-158.833 CenterY=-159.155 CenterZ=0 NormalX=0 NormalY=0 NormalZ=1 AngleXU=0 Radius=14.1667 StartAngle=3.14159 EndAngle=4.49901
    g9: LineSegment StartX=-176 StartY=-176 StartZ=0 EndX=-161.833 EndY=-176 EndZ=0
    g10: LineSegment StartX=-161.833 StartY=-176 StartZ=0 EndX=-161.833 EndY=-173 EndZ=0
  constraints (33):
    c: Coincident(g2,g-1)
    c: Diameter(g1) = 12.5
    c: Radius(g2) = 12.5
    c: Equal(g1,g0)
    c: DistanceX(g0,g2) = 88
    c: DistanceY(g0,g2) = 88
    c: PointOnObject(g1,g-1)
    c: Coincident(g3,g2)
    c: Coincident(g4,g2)
    c: Vertical(g4)
    c: Horizontal(g3)
    c: Coincident(g2,g4)
    c: Coincident(g2,g3)
    c: Horizontal(g5)
    c: PointOnObject(g1,g5)
    c: DistanceX(g5,g2) = 176
    c: Coincident(g1,g5)
    c: Coincident(g6,g5)
    c: Vertical(g6)
    c: Vertical(g7)
    c: Coincident(g1,g7)
    c: DistanceY(g6,g2) = 176
    c: Diameter(g8) = 28.3333
    c: Coincident(g9,g6)
    c: Horizontal(g9)
    c: Tangent(g7,g8) = -1.5708
    c: DistanceX(g6,g7) = 3
    c: Coincident(g10,g9)
    c: Coincident(g10,g8)
    c: Vertical(g10)
    c: DistanceY(g9,g8) = 3
    c: DistanceX(g6,g9) = 14.1667
    c: DistanceX(g5,g1) = 12.5
FEATURE [PartDesign::Pad] Pad040
  AddSubType = 0
  AlongSketchNormal = false
  AutoTaperInnerAngle = true
  BaseFeature = -> Pad039
  CheckUpToFaceLimits = true
  ClaimChildren = false
  Direction = (0,0,1)
  Fit = 0
  FitJoin = 0
  InnerFit = 0
  InnerFitJoin = 0
  InvalidShape = false
  Length = 30
  Length2 = 100
  Linearize = true
  NewSolid = false
  Profile = -> Sketch089
  Reversed = true
  Suppress = false
  TaperInnerAngle = 0
  TaperInnerAngleRev = 0
  TreeRank = 179
  Type = 0
  ValidateShape = true
  _ProfileBasedVersion = 1
  expr: Length = <<Parameters>>.motor_height
FEATURE [Sketcher::SketchObject] Sketch090
  ArcFitTolerance = 1e-06
  AttachmentSupport = -> [XY_Plane007]
  ExternalBSplineMaxDegree = 5
  ExternalBSplineTolerance = 0.0001
  FullyConstrained = true
  InternalTolerance = 1e-06
  InvalidShape = false
  MakeInternals = false
  MapMode = 5
  Support = -> [XY_Plane007]
  TreeRank = 180
  ValidateShape = true
  expr: Constraints[0] = <<Parameters>>.station_diameter + <<Parameters>>.thickness
  expr: Constraints[1] = <<Parameters>>.station_diameter + <<Parameters>>.thickness
  expr: Constraints[2] = <<Parameters>>.motor_shaft_mount_diameter / 4
  sketch-geometry (2):
    g0: ArcOfCircle CenterX=-88 CenterY=-88 CenterZ=0 NormalX=0 NormalY=0 NormalZ=1 AngleXU=0 Radius=6.25 StartAngle=3.14159 EndAngle=6.28319
    g1: LineSegment StartX=-94.25 StartY=-88 StartZ=0 EndX=-81.75 EndY=-88 EndZ=0
  constraints (7):
    c: DistanceX(g0,g-1) = 88
    c: DistanceY(g0,g-1) = 88
    c: Diameter(g0) = 12.5
    c: Horizontal(g1)
    c: PointOnObject(g0,g1)
    c: Coincident(g0,g1)
    c: Coincident(g0,g1)
FEATURE [PartDesign::Pad] Pad041
  AddSubType = 0
  AlongSketchNormal = false
  AutoTaperInnerAngle = true
  BaseFeature = -> Pad040
  CheckUpToFaceLimits = true
  ClaimChildren = false
  Direction = (0,0,1)
  Fit = 0
  FitJoin = 0
  InnerFit = 0
  InnerFitJoin = 0
  InvalidShape = false
  Length = 19
  Length2 = 100
  Linearize = true
  NewSolid = false
  Profile = -> Sketch090
  Suppress = false
  TaperInnerAngle = 0
  TaperInnerAngleRev = 0
  TreeRank = 181
  Type = 0
  ValidateShape = true
  _ProfileBasedVersion = 1
  expr: Length = <<Parameters>>.motor_shaft_length
FEATURE [Sketcher::SketchObject] Sketch091
  ArcFitTolerance = 1e-06
  AttachmentOffset = pos=(0,0,-176) rot=(0,0,1;0rad)
  AttachmentSupport = -> [YZ_Plane007]
  ExternalBSplineMaxDegree = 5
  ExternalBSplineTolerance = 0.0001
  FullyConstrained = false
  InternalTolerance = 1e-06
  InvalidShape = false
  MakeInternals = false
  MapMode = 5
  Placement = pos=(-176,3.91e-14,-3.91e-14) rot=(0.57735,0.57735,0.57735;2.0944rad)
  Support = -> [YZ_Plane007]
  TreeRank = 182
  ValidateShape = true
  expr: AttachmentOffset.Base.z = -(<<Parameters>>.station_diameter + <<Parameters>>.thickness) * 2
  expr: Constraints[12] = <<Parameters>>.thickness + <<Parameters>>.motor_screw_head_height
  expr: Constraints[13] = <<Parameters>>.motor_height
  expr: Constraints[14] = <<Parameters>>.thickness
  expr: Constraints[15] = <<Parameters>>.thickness
  expr: Constraints[16] = (<<Parameters>>.station_diameter + <<Parameters>>.thickness) * 2
  expr: Constraints[17] = <<Parameters>>.thickness
  expr: Constraints[21] = <<Parameters>>.thickness
  expr: Constraints[22] = <<Parameters>>.motor_shaft_length
  expr: Constraints[23] = <<Parameters>>.station_diameter + <<Parameters>>.thickness
  expr: Constraints[26] = <<Parameters>>.screen_overall_height + 2 * <<Parameters>>.thickness
  expr: Constraints[47] = 180 - <<Parameters>>.screen_angle
  sketch-geometry (19):
    g0: LineSegment [constr] StartX=0 StartY=-36.25 StartZ=0 EndX=-176 EndY=-36.25 EndZ=0
    g1: LineSegment [constr] StartX=0 StartY=-36.25 StartZ=0 EndX=0 EndY=-30 EndZ=0
    g2: LineSegment [constr] StartX=0 StartY=-30 StartZ=0 EndX=-173 EndY=-30 EndZ=0
    g3: LineSegment [constr] StartX=-176 StartY=-36.25 StartZ=0 EndX=-176 EndY=-25.7574 EndZ=0
    g4: LineSegment [constr] StartX=-173 StartY=-30 StartZ=0 EndX=-173 EndY=-27 EndZ=0
    g5: LineSegment [constr] StartX=-145.194 StartY=0.805848 StartZ=0 EndX=-147.315 EndY=2.92717 EndZ=0
    g6: LineSegment StartX=-88 StartY=22 StartZ=0 EndX=-99.2893 EndY=22 EndZ=0
    g7: LineSegment StartX=-88 StartY=22 StartZ=0 EndX=-88 EndY=19 EndZ=0
    g8: LineSegment [constr] StartX=-102.289 StartY=19 StartZ=0 EndX=-88 EndY=19 EndZ=0
    g9: LineSegment [constr] StartX=-102.289 StartY=43.7107 StartZ=0 EndX=-102.289 EndY=19 EndZ=0
    g10: LineSegment StartX=-99.2893 StartY=43.7107 StartZ=0 EndX=-99.2893 EndY=22 EndZ=0
    g11: ArcOfCircle CenterX=-102.289 CenterY=43.7107 CenterZ=0 NormalX=0 NormalY=0 NormalZ=1 AngleXU=0 Radius=3 StartAngle=1e-16 EndAngle=2.35619
    g12: LineSegment [constr] StartX=-176 StartY=-25.7574 StartZ=0 EndX=-150.243 EndY=0 EndZ=0
    g13: LineSegment StartX=-150.243 StartY=0 StartZ=0 EndX=-104.411 EndY=45.832 EndZ=0
    g14: LineSegment [constr] StartX=-173 StartY=-27 StartZ=0 EndX=-146 EndY=0 EndZ=0
    g15: LineSegment [constr] StartX=-146 StartY=0 StartZ=0 EndX=-102.289 EndY=43.7107 EndZ=0
    g16: LineSegment StartX=-150.243 StartY=0 StartZ=0 EndX=-146 EndY=0 EndZ=0
    g17: LineSegment StartX=-146 StartY=0 StartZ=0 EndX=-88 EndY=0 EndZ=0
    g18: LineSegment StartX=-88 StartY=0 StartZ=0 EndX=-88 EndY=19 EndZ=0
  constraints (53):
    c: PointOnObject(g0,g-2)
    c: Horizontal(g0)
    c: Coincident(g1,g0)
    c: PointOnObject(g1,g-2)
    c: Coincident(g2,g1)
    c: Horizontal(g2)
    c: Coincident(g3,g0)
    c: Vertical(g3)
    c: Coincident(g12,g3)
    c: Coincident(g4,g2)
    c: Vertical(g4)
    c: Coincident(g14,g4)
    c: DistanceY(g0,g1) = 6.25
    c: DistanceY(g1,g-1) = 30
    c: DistanceX(g0,g2) = 3
    c: Distance(g5,g5) = 3
    c: DistanceX(g0,g-1) = 176
    c: DistanceY(g2,g4) = 3
    c: Horizontal(g6)
    c: Coincident(g7,g6)
    c: Vertical(g7)
    c: DistanceY(g7,g6) = 3
    c: DistanceY(g-1,g7) = 19
    c: DistanceX(g7,g-1) = 88
    c: Coincident(g8,g7)
    c: Horizontal(g8)
    c: Distance(g15,g4) = 100
    c: Coincident(g9,g15)
    c: Coincident(g9,g8)
    c: Vertical(g9)
    c: Coincident(g10,g6)
    c: Vertical(g10)
    c: Tangent(g13,g11) = 1.5708
    c: Tangent(g10,g11) = 1.5708
    c: Coincident(g11,g15)
    c: Coincident(g12,g13)
    c: Perpendicular(g12,g5)
    c: PointOnObject(g5,g13)
    c: Coincident(g14,g15)
    c: PointOnObject(g5,g14)
    c: Parallel(g14,g12)
    c: Parallel(g15,g12)
    c: Parallel(g14,g13)
    c: Coincident(g16,g12)
    c: Coincident(g16,g14)
    c: Horizontal(g16)
    c: PointOnObject(g12,g-1)
    c: Angle(g-1,g13) = 0.785398
    c: Coincident(g17,g15)
    c: PointOnObject(g17,g-1)
    c: Coincident(g18,g17)
    c: Coincident(g18,g7)
    c: Vertical(g18)
FEATURE [PartDesign::Pad] Pad042
  AddSubType = 0
  AlongSketchNormal = false
  AutoTaperInnerAngle = true
  BaseFeature = -> Pad041
  CheckUpToFaceLimits = true
  ClaimChildren = false
  Direction = (1,-3e-16,3e-16)
  Fit = 0
  FitJoin = 0
  InnerFit = 0
  InnerFitJoin = 0
  InvalidShape = false
  Length = 3
  Length2 = 100
  Linearize = true
  NewSolid = false
  Profile = -> Sketch091
  Suppress = false
  TaperInnerAngle = 0
  TaperInnerAngleRev = 0
  TreeRank = 183
  Type = 0
  ValidateShape = true
  _ProfileBasedVersion = 1
  expr: Length = <<Parameters>>.thickness
FEATURE [Sketcher::SketchObject] Sketch092
  ArcFitTolerance = 1e-06
  ExternalBSplineMaxDegree = 5
  ExternalBSplineTolerance = 0.0001
  FullyConstrained = false
  InternalTolerance = 1e-06
  InvalidShape = false
  MakeInternals = false
  MapMode = 2
  Placement = pos=(-88,-88,0) rot=(0.57735,0.57735,0.57735;0rad)
  TreeRank = 184
  ValidateShape = true
  expr: Placement.Base.x = -(<<Parameters>>.station_diameter + <<Parameters>>.thickness)
  expr: Placement.Base.y = -(<<Parameters>>.station_diameter + <<Parameters>>.thickness)
  expr: Constraints[0] = <<Parameters>>.station_diameter
  expr: Constraints[14] = <<Parameters>>.motor_screw_spacing
  expr: Constraints[29] = <<Parameters>>.motor_screw_shaft_diameter
  expr: Constraints[3] = <<Parameters>>.station_diameter
  sketch-geometry (20):
    g0: Circle [constr] CenterX=-42.5 CenterY=42.5 CenterZ=0 NormalX=0 NormalY=0 NormalZ=1 AngleXU=0 Radius=42.5
    g1: Circle [constr] CenterX=42.5 CenterY=42.5 CenterZ=0 NormalX=0 NormalY=0 NormalZ=1 AngleXU=0 Radius=42.5
    g2: LineSegment [constr] StartX=-29.5 StartY=29.5 StartZ=0 EndX=-29.5 EndY=55.5 EndZ=0
    g3: LineSegment [constr] StartX=-29.5 StartY=55.5 StartZ=0 EndX=-55.5 EndY=55.5 EndZ=0
    g4: LineSegment [constr] StartX=-55.5 StartY=55.5 StartZ=0 EndX=-55.5 EndY=29.5 EndZ=0
    g5: LineSegment [constr] StartX=-55.5 StartY=29.5 StartZ=0 EndX=-29.5 EndY=29.5 EndZ=0
    g6: GeomPoint [constr] X=-42.5 Y=42.5 Z=0
    g7: LineSegment [constr] StartX=55.5 StartY=29.5 StartZ=0 EndX=55.5 EndY=55.5 EndZ=0
    g8: LineSegment [constr] StartX=55.5 StartY=55.5 StartZ=0 EndX=29.5 EndY=55.5 EndZ=0
    g9: LineSegment [constr] StartX=29.5 StartY=55.5 StartZ=0 EndX=29.5 EndY=29.5 EndZ=0
    g10: LineSegment [constr] StartX=29.5 StartY=29.5 StartZ=0 EndX=55.5 EndY=29.5 EndZ=0
    g11: GeomPoint [constr] X=42.5 Y=42.5 Z=0
    g12: Circle CenterX=-55.5 CenterY=55.5 CenterZ=0 NormalX=0 NormalY=0 NormalZ=1 AngleXU=0 Radius=1.75
    g13: Circle CenterX=-29.5 CenterY=55.5 CenterZ=0 NormalX=0 NormalY=0 NormalZ=1 AngleXU=0 Radius=1.75
    g14: Circle CenterX=-29.5 CenterY=29.5 CenterZ=0 NormalX=0 NormalY=0 NormalZ=1 AngleXU=0 Radius=1.75
    g15: Circle CenterX=-55.5 CenterY=29.5 CenterZ=0 NormalX=0 NormalY=0 NormalZ=1 AngleXU=0 Radius=1.75
    g16: Circle CenterX=29.5 CenterY=55.5 CenterZ=0 NormalX=0 NormalY=0 NormalZ=1 AngleXU=0 Radius=1.75
    g17: Circle CenterX=55.5 CenterY=55.5 CenterZ=0 NormalX=0 NormalY=0 NormalZ=1 AngleXU=0 Radius=1.75
    g18: Circle CenterX=55.5 CenterY=29.5 CenterZ=0 NormalX=0 NormalY=0 NormalZ=1 AngleXU=0 Radius=1.75
    g19: Circle CenterX=29.5 CenterY=29.5 CenterZ=0 NormalX=0 NormalY=0 NormalZ=1 AngleXU=0 Radius=1.75
  constraints (44):
    c: Diameter(g0) = 85
    c: Equal(g0,g1)
    c: Symmetric(g0,g1,g-2)
    c: DistanceX(g0,g1) = 85
    c: Coincident(g2,g3)
    c: Coincident(g3,g4)
    c: Coincident(g4,g5)
    c: Coincident(g5,g2)
    c: Horizontal(g3)
    c: Horizontal(g5)
    c: Vertical(g2)
    c: Vertical(g4)
    c: Symmetric(g3,g2,g6)
    c: Coincident(g6,g0)
    c: DistanceX(g3,g2) = 26
    c: Equal(g3,g4)
    c: Coincident(g7,g8)
    c: Coincident(g8,g9)
    c: Coincident(g9,g10)
    c: Coincident(g10,g7)
    c: Horizontal(g8)
    c: Horizontal(g10)
    c: Vertical(g7)
    c: Vertical(g9)
    c: Symmetric(g8,g7,g11)
    c: Coincident(g11,g1)
    c: Equal(g3,g8)
    c: Equal(g3,g9)
    c: Coincident(g12,g3)
    c: Diameter(g12) = 3.5
    c: Coincident(g13,g2)
    c: Coincident(g14,g2)
    c: Coincident(g15,g4)
    c: Coincident(g16,g8)
    c: Coincident(g17,g7)
    c: Coincident(g18,g7)
    c: Coincident(g19,g9)
    c: Equal(g12,g13)
    c: Equal(g12,g15)
    c: Equal(g12,g14)
    c: Equal(g12,g16)
    c: Equal(g16,g17)
    c: Equal(g16,g19)
    c: Equal(g16,g18)
FEATURE [PartDesign::Pocket] Pocket042
  AddSubType = 1
  AutoTaperInnerAngle = true
  BaseFeature = -> Pad042
  CheckUpToFaceLimits = true
  ClaimChildren = false
  Fit = 0
  FitJoin = 0
  InnerFit = 0
  InnerFitJoin = 0
  InvalidShape = false
  Length = 100
  Length2 = 100
  Linearize = true
  NewSolid = false
  Profile = -> Sketch092
  Suppress = false
  TaperInnerAngle = 0
  TaperInnerAngleRev = 0
  TreeRank = 185
  Type = 0
  ValidateShape = true
  _ProfileBasedVersion = 1
  _Version = 1
FEATURE [Sketcher::SketchObject] Sketch093
  ArcFitTolerance = 1e-06
  ExternalBSplineMaxDegree = 5
  ExternalBSplineTolerance = 0.0001
  FullyConstrained = false
  InternalTolerance = 1e-06
  InvalidShape = false
  MakeInternals = false
  MapMode = 2
  Placement = pos=(-88,-88,-36.25) rot=(0.57735,0.57735,0.57735;0rad)
  TreeRank = 186
  ValidateShape = true
  expr: Placement.Base.x = -(<<Parameters>>.station_diameter + <<Parameters>>.thickness)
  expr: Placement.Base.y = -(<<Parameters>>.station_diameter + <<Parameters>>.thickness)
  expr: Placement.Base.z = -(<<Parameters>>.motor_height + <<Parameters>>.thickness + <<Parameters>>.motor_screw_head_height)
  expr: Constraints[0] = <<Parameters>>.station_diameter
  expr: Constraints[14] = <<Parameters>>.motor_screw_spacing
  expr: Constraints[29] = <<Parameters>>.motor_screw_head_diameter
  expr: Constraints[3] = <<Parameters>>.station_diameter
  sketch-geometry (20):
    g0: Circle [constr] CenterX=-42.5 CenterY=42.5 CenterZ=0 NormalX=0 NormalY=0 NormalZ=1 AngleXU=0 Radius=42.5
    g1: Circle [constr] CenterX=42.5 CenterY=42.5 CenterZ=0 NormalX=0 NormalY=0 NormalZ=1 AngleXU=0 Radius=42.5
    g2: LineSegment [constr] StartX=-29.5 StartY=29.5 StartZ=0 EndX=-29.5 EndY=55.5 EndZ=0
    g3: LineSegment [constr] StartX=-29.5 StartY=55.5 StartZ=0 EndX=-55.5 EndY=55.5 EndZ=0
    g4: LineSegment [constr] StartX=-55.5 StartY=55.5 StartZ=0 EndX=-55.5 EndY=29.5 EndZ=0
    g5: LineSegment [constr] StartX=-55.5 StartY=29.5 StartZ=0 EndX=-29.5 EndY=29.5 EndZ=0
    g6: GeomPoint [constr] X=-42.5 Y=42.5 Z=0
    g7: LineSegment [constr] StartX=55.5 StartY=29.5 StartZ=0 EndX=55.5 EndY=55.5 EndZ=0
    g8: LineSegment [constr] StartX=55.5 StartY=55.5 StartZ=0 EndX=29.5 EndY=55.5 EndZ=0
    g9: LineSegment [constr] StartX=29.5 StartY=55.5 StartZ=0 EndX=29.5 EndY=29.5 EndZ=0
    g10: LineSegment [constr] StartX=29.5 StartY=29.5 StartZ=0 EndX=55.5 EndY=29.5 EndZ=0
    g11: GeomPoint [constr] X=42.5 Y=42.5 Z=0
    g12: Circle CenterX=-55.5 CenterY=55.5 CenterZ=0 NormalX=0 NormalY=0 NormalZ=1 AngleXU=0 Radius=3
    g13: Circle CenterX=-29.5 CenterY=55.5 CenterZ=0 NormalX=0 NormalY=0 NormalZ=1 AngleXU=0 Radius=3
    g14: Circle CenterX=-29.5 CenterY=29.5 CenterZ=0 NormalX=0 NormalY=0 NormalZ=1 AngleXU=0 Radius=3
    g15: Circle CenterX=-55.5 CenterY=29.5 CenterZ=0 NormalX=0 NormalY=0 NormalZ=1 AngleXU=0 Radius=3
    g16: Circle CenterX=29.5 CenterY=55.5 CenterZ=0 NormalX=0 NormalY=0 NormalZ=1 AngleXU=0 Radius=3
    g17: Circle CenterX=55.5 CenterY=55.5 CenterZ=0 NormalX=0 NormalY=0 NormalZ=1 AngleXU=0 Radius=3
    g18: Circle CenterX=55.5 CenterY=29.5 CenterZ=0 NormalX=0 NormalY=0 NormalZ=1 AngleXU=0 Radius=3
    g19: Circle CenterX=29.5 CenterY=29.5 CenterZ=0 NormalX=0 NormalY=0 NormalZ=1 AngleXU=0 Radius=3
  constraints (44):
    c: Diameter(g0) = 85
    c: Equal(g0,g1)
    c: Symmetric(g0,g1,g-2)
    c: DistanceX(g0,g1) = 85
    c: Coincident(g2,g3)
    c: Coincident(g3,g4)
    c: Coincident(g4,g5)
    c: Coincident(g5,g2)
    c: Horizontal(g3)
    c: Horizontal(g5)
    c: Vertical(g2)
    c: Vertical(g4)
    c: Symmetric(g3,g2,g6)
    c: Coincident(g6,g0)
    c: DistanceX(g3,g2) = 26
    c: Equal(g3,g4)
    c: Coincident(g7,g8)
    c: Coincident(g8,g9)
    c: Coincident(g9,g10)
    c: Coincident(g10,g7)
    c: Horizontal(g8)
    c: Horizontal(g10)
    c: Vertical(g7)
    c: Vertical(g9)
    c: Symmetric(g8,g7,g11)
    c: Coincident(g11,g1)
    c: Equal(g3,g8)
    c: Equal(g3,g9)
    c: Coincident(g12,g3)
    c: Diameter(g12) = 6
    c: Coincident(g13,g2)
    c: Coincident(g14,g2)
    c: Coincident(g15,g4)
    c: Coincident(g16,g8)
    c: Coincident(g17,g7)
    c: Coincident(g18,g7)
    c: Coincident(g19,g9)
    c: Equal(g12,g13)
    c: Equal(g12,g15)
    c: Equal(g12,g14)
    c: Equal(g12,g16)
    c: Equal(g16,g17)
    c: Equal(g16,g19)
    c: Equal(g16,g18)
FEATURE [PartDesign::Pocket] Pocket043
  AddSubType = 1
  AutoTaperInnerAngle = true
  BaseFeature = -> Pocket042
  CheckUpToFaceLimits = true
  ClaimChildren = false
  Fit = 0
  FitJoin = 0
  InnerFit = 0
  InnerFitJoin = 0
  InvalidShape = false
  Length = 3.25
  Length2 = 100
  Linearize = true
  NewSolid = false
  Profile = -> Sketch093
  Reversed = true
  Suppress = false
  TaperInnerAngle = 0
  TaperInnerAngleRev = 0
  TreeRank = 187
  Type = 0
  ValidateShape = true
  _ProfileBasedVersion = 1
  _Version = 1
  expr: Length = <<Parameters>>.motor_screw_head_height
FEATURE [Sketcher::SketchObject] Sketch094
  ArcFitTolerance = 1e-06
  ExternalBSplineMaxDegree = 5
  ExternalBSplineTolerance = 0.0001
  FullyConstrained = true
  InternalTolerance = 1e-06
  InvalidShape = false
  MakeInternals = false
  MapMode = 2
  Placement = pos=(-88,-88,-30) rot=(0.57735,0.57735,0.57735;0rad)
  TreeRank = 188
  ValidateShape = true
  expr: Placement.Base.x = -(<<Parameters>>.station_diameter + <<Parameters>>.thickness)
  expr: Placement.Base.y = -(<<Parameters>>.station_diameter + <<Parameters>>.thickness)
  expr: Placement.Base.z = -<<Parameters>>.motor_height
  expr: Constraints[14] = <<Parameters>>.thickness * 2
  expr: Constraints[17] = <<Parameters>>.station_diameter + <<Parameters>>.thickness
  expr: Constraints[18] = <<Parameters>>.station_diameter + <<Parameters>>.thickness
  expr: Constraints[19] = (<<Parameters>>.station_diameter + <<Parameters>>.thickness) * 2 - 4 * <<Parameters>>.thickness - <<Parameters>>.motor_shaft_mount_diameter / 2
  sketch-geometry (8):
    g0: LineSegment StartX=88 StartY=69.5 StartZ=0 EndX=82 EndY=69.5 EndZ=0
    g1: LineSegment StartX=82 StartY=69.5 StartZ=0 EndX=82 EndY=-69.5 EndZ=0
    g2: LineSegment StartX=82 StartY=-69.5 StartZ=0 EndX=88 EndY=-69.5 EndZ=0
    g3: LineSegment StartX=88 StartY=-69.5 StartZ=0 EndX=88 EndY=69.5 EndZ=0
    g4: LineSegment StartX=-69.5 StartY=82 StartZ=0 EndX=69.5 EndY=82 EndZ=0
    g5: LineSegment StartX=69.5 StartY=82 StartZ=0 EndX=69.5 EndY=88 EndZ=0
    g6: LineSegment StartX=69.5 StartY=88 StartZ=0 EndX=-69.5 EndY=88 EndZ=0
    g7: LineSegment StartX=-69.5 StartY=88 StartZ=0 EndX=-69.5 EndY=82 EndZ=0
  constraints (22):
    c: Coincident(g0,g1)
    c: Coincident(g1,g2)
    c: Coincident(g2,g3)
    c: Coincident(g3,g0)
    c: Horizontal(g0)
    c: Horizontal(g2)
    c: Vertical(g1)
    c: Coincident(g4,g5)
    c: Coincident(g5,g6)
    c: Coincident(g6,g7)
    c: Coincident(g7,g4)
    c: Horizontal(g6)
    c: Vertical(g5)
    c: Vertical(g7)
    c: DistanceX(g0,g0) = 6
    c: Equal(g0,g5)
    c: Symmetric(g4,g4,g-2)
    c: DistanceX(g-1,g0) = 88
    c: DistanceY(g-1,g6) = 88
    c: DistanceX(g6,g5) = 139
    c: Equal(g6,g3)
    c: Symmetric(g0,g2,g-1)
FEATURE [Sketcher::SketchObject] Sketch095
  ArcFitTolerance = 1e-06
  AttachmentSupport = -> [XY_Plane007]
  ExternalBSplineMaxDegree = 5
  ExternalBSplineTolerance = 0.0001
  FullyConstrained = true
  InternalTolerance = 1e-06
  InvalidShape = false
  MakeInternals = false
  MapMode = 5
  Support = -> [XY_Plane007]
  TreeRank = 190
  ValidateShape = true
  expr: Constraints[15] = <<Parameters>>.station_diameter / 3
  expr: Constraints[16] = (<<Parameters>>.station_diameter + <<Parameters>>.thickness) * 2
  expr: Constraints[21] = (<<Parameters>>.station_diameter + <<Parameters>>.thickness) * 2 * 2
  sketch-geometry (10):
    g0: LineSegment StartX=0 StartY=-176 StartZ=0 EndX=-161.833 EndY=-176 EndZ=0
    g1: LineSegment StartX=-176 StartY=-161.833 StartZ=0 EndX=-176 EndY=0 EndZ=0
    g2: LineSegment StartX=-176 StartY=0 StartZ=0 EndX=0 EndY=0 EndZ=0
    g3: LineSegment StartX=0 StartY=0 StartZ=0 EndX=0 EndY=-176 EndZ=0
    g4: LineSegment StartX=-264 StartY=88 StartZ=0 EndX=88 EndY=88 EndZ=0
    g5: LineSegment StartX=88 StartY=88 StartZ=0 EndX=88 EndY=-264 EndZ=0
    g6: LineSegment StartX=88 StartY=-264 StartZ=0 EndX=-264 EndY=-264 EndZ=0
    g7: LineSegment StartX=-264 StartY=-264 StartZ=0 EndX=-264 EndY=88 EndZ=0
    g8: ArcOfCircle CenterX=-161.833 CenterY=-161.833 CenterZ=0 NormalX=0 NormalY=0 NormalZ=1 AngleXU=0 Radius=14.1667 StartAngle=3.14159 EndAngle=4.71239
    g9: GeomPoint [constr] X=-88 Y=-88 Z=0
  constraints (25):
    c: Coincident(g1,g2)
    c: Coincident(g2,g3)
    c: Coincident(g3,g0)
    c: Horizontal(g0)
    c: Horizontal(g2)
    c: Vertical(g1)
    c: Vertical(g3)
    c: Coincident(g4,g5)
    c: Coincident(g5,g6)
    c: Coincident(g6,g7)
    c: Coincident(g7,g4)
    c: Horizontal(g4)
    c: Horizontal(g6)
    c: Vertical(g5)
    c: Vertical(g7)
    c: Diameter(g8) = 28.3333
    c: DistanceX(g1,g2) = 176
    c: Equal(g2,g3)
    c: Coincident(g2,g-1)
    c: Tangent(g8,g0) = 1.5708
    c: Tangent(g8,g1) = 1.5708
    c: DistanceX(g4,g4) = 352
    c: Equal(g4,g5)
    c: Symmetric(g1,g0,g9)
    c: Symmetric(g5,g4,g9)
FEATURE [PartDesign::Pocket] Pocket045
  AddSubType = 1
  AutoTaperInnerAngle = true
  BaseFeature = -> Pocket043
  CheckUpToFaceLimits = true
  ClaimChildren = false
  Fit = 0
  FitJoin = 0
  InnerFit = 0
  InnerFitJoin = 0
  InvalidShape = false
  Length = 100
  Length2 = 100
  Linearize = true
  NewSolid = false
  Profile = -> Sketch095
  Suppress = false
  TaperInnerAngle = 0
  TaperInnerAngleRev = 0
  TreeRank = 191
  Type = 4
  ValidateShape = true
  _ProfileBasedVersion = 1
  _Version = 1
FEATURE [Sketcher::SketchObject] Sketch096
  ArcFitTolerance = 1e-06
  AttachmentSupport = -> [YZ_Plane007]
  ExternalBSplineMaxDegree = 5
  ExternalBSplineTolerance = 0.0001
  FullyConstrained = false
  InternalTolerance = 1e-06
  InvalidShape = false
  MakeInternals = false
  MapMode = 5
  Placement = pos=(0,0,0) rot=(0.57735,0.57735,0.57735;2.0944rad)
  Support = -> [YZ_Plane007]
  TreeRank = 192
  ValidateShape = true
  expr: Constraints[12] = <<Parameters>>.thickness + <<Parameters>>.motor_screw_head_height
  expr: Constraints[13] = <<Parameters>>.motor_height
  expr: Constraints[14] = <<Parameters>>.thickness
  expr: Constraints[18] = <<Parameters>>.screen_body_thickness
  expr: Constraints[19] = (<<Parameters>>.station_diameter + <<Parameters>>.thickness) * 2
  expr: Constraints[20] = <<Parameters>>.screen_angle
  expr: Constraints[21] = <<Parameters>>.thickness
  expr: Constraints[25] = <<Parameters>>.thickness
  expr: Constraints[26] = <<Parameters>>.motor_shaft_length
  expr: Constraints[27] = <<Parameters>>.station_diameter + <<Parameters>>.thickness
  expr: Constraints[31] = <<Parameters>>.screen_overall_height + 2 * <<Parameters>>.thickness
  expr: Constraints[47] = 10 * <<Parameters>>.thickness
  sketch-geometry (17):
    g0: LineSegment [constr] StartX=0 StartY=-36.25 StartZ=0 EndX=-176 EndY=-36.25 EndZ=0
    g1: LineSegment [constr] StartX=0 StartY=-36.25 StartZ=0 EndX=0 EndY=-30 EndZ=0
    g2: LineSegment [constr] StartX=0 StartY=-30 StartZ=0 EndX=-173 EndY=-30 EndZ=0
    g3: LineSegment [constr] StartX=-176 StartY=-36.25 StartZ=0 EndX=-176 EndY=-22.2218 EndZ=0
    g4: LineSegment StartX=-176 StartY=-22.2218 StartZ=0 EndX=-106.178 EndY=47.5998 EndZ=0
    g5: LineSegment [constr] StartX=-173 StartY=-30 StartZ=0 EndX=-173 EndY=-27 EndZ=0
    g6: LineSegment [constr] StartX=-173 StartY=-27 StartZ=0 EndX=-102.289 EndY=43.7107 EndZ=0
    g7: LineSegment [constr] StartX=-145.874 StartY=0.12624 StartZ=0 EndX=-149.763 EndY=4.01533 EndZ=0
    g8: LineSegment [constr] StartX=-88 StartY=22 StartZ=0 EndX=-96.7893 EndY=22 EndZ=0
    g9: LineSegment [constr] StartX=-88 StartY=22 StartZ=0 EndX=-88 EndY=19 EndZ=0
    g10: LineSegment [constr] StartX=-102.289 StartY=19 StartZ=0 EndX=-88 EndY=19 EndZ=0
    g11: LineSegment [constr] StartX=-102.289 StartY=43.7107 StartZ=0 EndX=-102.289 EndY=19 EndZ=0
    g12: LineSegment [constr] StartX=-96.7893 StartY=43.7107 StartZ=0 EndX=-96.7893 EndY=22 EndZ=0
    g13: ArcOfCircle [constr] CenterX=-102.289 CenterY=43.7107 CenterZ=0 NormalX=0 NormalY=0 NormalZ=1 AngleXU=0 Radius=5.5 StartAngle=-1.4149e-12 EndAngle=2.35619
    g14: LineSegment StartX=-176 StartY=-22.2218 StartZ=0 EndX=-197.213 EndY=-1.00862 EndZ=0
    g15: LineSegment StartX=-106.178 StartY=47.5998 StartZ=0 EndX=-127.392 EndY=68.813 EndZ=0
    g16: LineSegment StartX=-127.392 StartY=68.813 StartZ=0 EndX=-197.213 EndY=-1.00862 EndZ=0
  constraints (48):
    c: PointOnObject(g0,g-2)
    c: Horizontal(g0)
    c: Coincident(g1,g0)
    c: PointOnObject(g1,g-2)
    c: Coincident(g2,g1)
    c: Horizontal(g2)
    c: Coincident(g3,g0)
    c: Vertical(g3)
    c: Coincident(g4,g3)
    c: Coincident(g5,g2)
    c: Vertical(g5)
    c: Coincident(g6,g5)
    c: DistanceY(g0,g1) = 6.25
    c: DistanceY(g1,g-1) = 30
    c: DistanceX(g0,g2) = 3
    c: Parallel(g6,g4)
    c: PointOnObject(g7,g6)
    c: Perpendicular(g4,g7)
    c: Distance(g7,g7) = 5.5
    c: DistanceX(g0,g-1) = 176
    c: Angle(g5,g6) = 2.35619
    c: DistanceY(g2,g5) = 3
    c: Horizontal(g8)
    c: Coincident(g9,g8)
    c: Vertical(g9)
    c: DistanceY(g9,g8) = 3
    c: DistanceY(g-1,g9) = 19
    c: DistanceX(g9,g-1) = 88
    c: PointOnObject(g7,g4)
    c: Coincident(g10,g9)
    c: Horizontal(g10)
    c: Distance(g6,g5) = 100
    c: Coincident(g11,g6)
    c: Coincident(g11,g10)
    c: Vertical(g11)
    c: Coincident(g12,g8)
    c: Vertical(g12)
    c: Tangent(g4,g13) = 1.5708
    c: Tangent(g12,g13) = 1.5708
    c: Coincident(g13,g6)
    c: Coincident(g14,g3)
    c: Coincident(g15,g4)
    c: Coincident(g16,g14)
    c: Parallel(g15,g14)
    c: Parallel(g4,g16)
    c: Coincident(g15,g16)
    c: Perpendicular(g14,g4)
    c: Distance(g4,g14) = 30
FEATURE [PartDesign::Pocket] Pocket046
  AddSubType = 1
  AutoTaperInnerAngle = true
  BaseFeature = -> Pocket045
  CheckUpToFaceLimits = true
  ClaimChildren = false
  Fit = 0
  FitJoin = 0
  InnerFit = 0
  InnerFitJoin = 0
  InvalidShape = false
  Length = 500
  Length2 = 100
  Linearize = true
  NewSolid = false
  Profile = -> Sketch096
  Suppress = false
  TaperInnerAngle = 0
  TaperInnerAngleRev = 0
  TreeRank = 193
  Type = 0
  ValidateShape = true
  _ProfileBasedVersion = 1
  _Version = 1
FEATURE [Sketcher::SketchObject] Sketch097
  ArcFitTolerance = 1e-06
  ExternalBSplineMaxDegree = 5
  ExternalBSplineTolerance = 0.0001
  FullyConstrained = true
  InternalTolerance = 1e-06
  InvalidShape = false
  MakeInternals = false
  MapMode = 5
  Placement = pos=(-176,0,0) rot=(0.57735,-0.57735,-0.57735;2.0944rad)
  TreeRank = 294
  ValidateShape = true
  expr: Constraints[0] = <<Parameters>>.fan_screw_hole_diameter
  expr: Constraints[12] = <<Parameters>>.fan_diameter
  expr: Constraints[13] = <<Parameters>>.station_diameter * 1.25 + <<Parameters>>.thickness
  expr: Constraints[14] = <<Parameters>>.fan_diameter / 2 - <<Parameters>>.thickness
  expr: Constraints[4] = <<Parameters>>.fan_screw_distance
  expr: Constraints[6] = <<Parameters>>.fan_screw_distance
  expr: Constraints[9] = 0
  sketch-geometry (6):
    g0: GeomPoint [constr] X=109.25 Y=-11 Z=0
    g1: Circle CenterX=95.25 CenterY=3 CenterZ=0 NormalX=0 NormalY=0 NormalZ=1 AngleXU=0 Radius=1.3
    g2: Circle CenterX=123.25 CenterY=3 CenterZ=0 NormalX=0 NormalY=0 NormalZ=1 AngleXU=0 Radius=1.3
    g3: Circle CenterX=95.25 CenterY=-25 CenterZ=0 NormalX=0 NormalY=0 NormalZ=1 AngleXU=0 Radius=1.3
    g4: Circle CenterX=123.25 CenterY=-25 CenterZ=0 NormalX=0 NormalY=0 NormalZ=1 AngleXU=0 Radius=1.3
    g5: Circle CenterX=109.25 CenterY=-11 CenterZ=0 NormalX=0 NormalY=0 NormalZ=1 AngleXU=0 Radius=14
  constraints (15):
    c: Diameter(g1) = 2.6
    c: Equal(g1,g2)
    c: Equal(g1,g3)
    c: Equal(g1,g4)
    c: DistanceY(g4,g2) = 28
    c: DistanceX(g2,g4) = 0
    c: DistanceX(g3,g4) = 28
    c: DistanceX(g3,g1) = 0
    c: DistanceY(g3,g4) = 0
    c: DistanceY(g1,g2) = 0
    c: Symmetric(g2,g3,g0)
    c: Coincident(g5,g0)
    c: Diameter(g5) = 28
    c: DistanceX(g-1,g5) = 109.25
    c: DistanceY(g5,g-1) = 11
FEATURE [PartDesign::Pocket] Pocket047
  AddSubType = 1
  AutoTaperInnerAngle = true
  BaseFeature = -> Pocket046
  CheckUpToFaceLimits = true
  ClaimChildren = false
  Fit = 0
  FitJoin = 0
  InnerFit = 0
  InnerFitJoin = 0
  InvalidShape = false
  Length = 3
  Length2 = 100
  Linearize = true
  NewSolid = false
  Profile = -> Sketch097
  Suppress = false
  TaperInnerAngle = 0
  TaperInnerAngleRev = 0
  TreeRank = 295
  Type = 0
  ValidateShape = true
  _ProfileBasedVersion = 1
  _Version = 1
  expr: Length = <<Parameters>>.thickness
FEATURE [Sketcher::SketchObject] Sketch098
  ArcFitTolerance = 1e-06
  AttachmentSupport = -> [Pocket047]
  ExternalBSplineMaxDegree = 5
  ExternalBSplineTolerance = 0.0001
  FullyConstrained = true
  InternalTolerance = 1e-06
  InvalidShape = false
  MakeInternals = false
  MapMode = 5
  Placement = pos=(-3.81e-14,-76.8891,76.8891) rot=(1,0,0;0.785398rad)
  Support = -> [Pocket047]
  TreeRank = 320
  ValidateShape = true
  expr: Constraints[10] = <<Parameters>>.screen_position
  expr: Constraints[11] = Spreadsheet.screen_opening_width
  expr: Constraints[12] = Spreadsheet.screen_opening_height
  sketch-geometry (5):
    g0: LineSegment StartX=116 StartY=-136.75 StartZ=0 EndX=116 EndY=-47.25 EndZ=0
    g1: LineSegment StartX=116 StartY=-47.25 StartZ=0 EndX=-116 EndY=-47.25 EndZ=0
    g2: LineSegment StartX=-116 StartY=-47.25 StartZ=0 EndX=-116 EndY=-136.75 EndZ=0
    g3: LineSegment StartX=-116 StartY=-136.75 StartZ=0 EndX=116 EndY=-136.75 EndZ=0
    g4: GeomPoint [constr] X=0 Y=-92 Z=0
  constraints (13):
    c: Coincident(g0,g1)
    c: Coincident(g1,g2)
    c: Coincident(g2,g3)
    c: Coincident(g3,g0)
    c: Horizontal(g1)
    c: Horizontal(g3)
    c: Vertical(g0)
    c: Vertical(g2)
    c: Symmetric(g1,g0,g4)
    c: PointOnObject(g4,g-2)
    c: DistanceY(g4,g-1) = 92
    c: DistanceX(g1,g0) = 232
    c: DistanceY(g0,g0) = 89.5
FEATURE [PartDesign::Pocket] Pocket048
  AddSubType = 1
  AutoTaperInnerAngle = true
  BaseFeature = -> Pocket047
  CheckUpToFaceLimits = true
  ClaimChildren = false
  Fit = 0
  FitJoin = 0
  InnerFit = 0
  InnerFitJoin = 0
  InvalidShape = false
  Length = 5.5
  Length2 = 100
  Linearize = true
  NewSolid = false
  Profile = -> Sketch098
  Suppress = false
  TaperInnerAngle = 0
  TaperInnerAngleRev = 0
  TreeRank = 321
  Type = 0
  ValidateShape = true
  _ProfileBasedVersion = 1
  _Version = 1
  expr: Length = <<Parameters>>.screen_body_thickness
FEATURE [Sketcher::SketchObject] Sketch099
  ArcFitTolerance = 1e-06
  AttachmentSupport = -> [Pocket048]
  ExternalBSplineMaxDegree = 5
  ExternalBSplineTolerance = 0.0001
  FullyConstrained = true
  InternalTolerance = 1e-06
  InvalidShape = false
  MakeInternals = false
  MapMode = 5
  Placement = pos=(-3.81e-14,-76.8891,76.8891) rot=(1,0,0;0.785398rad)
  Support = -> [Pocket048]
  TreeRank = 343
  ValidateShape = true
  expr: Constraints[10] = <<Parameters>>.screen_opening_width + 2 * <<Parameters>>.screen_relief_width
  expr: Constraints[11] = <<Parameters>>.screen_opening_height + 2 * <<Parameters>>.screen_relief_width
  expr: Constraints[12] = <<Parameters>>.screen_position
  sketch-geometry (5):
    g0: LineSegment StartX=117.5 StartY=-138.25 StartZ=0 EndX=117.5 EndY=-45.75 EndZ=0
    g1: LineSegment StartX=117.5 StartY=-45.75 StartZ=0 EndX=-117.5 EndY=-45.75 EndZ=0
    g2: LineSegment StartX=-117.5 StartY=-45.75 StartZ=0 EndX=-117.5 EndY=-138.25 EndZ=0
    g3: LineSegment StartX=-117.5 StartY=-138.25 StartZ=0 EndX=117.5 EndY=-138.25 EndZ=0
    g4: GeomPoint [constr] X=0 Y=-92 Z=0
  constraints (13):
    c: Coincident(g0,g1)
    c: Coincident(g1,g2)
    c: Coincident(g2,g3)
    c: Coincident(g3,g0)
    c: Horizontal(g1)
    c: Horizontal(g3)
    c: Vertical(g0)
    c: Vertical(g2)
    c: Symmetric(g1,g0,g4)
    c: PointOnObject(g4,g-2)
    c: DistanceX(g1,g0) = 235
    c: DistanceY(g0,g0) = 92.5
    c: DistanceY(g4,g-1) = 92
FEATURE [PartDesign::Pocket] Pocket049
  AddSubType = 1
  AutoTaperInnerAngle = true
  BaseFeature = -> Pocket048
  CheckUpToFaceLimits = true
  ClaimChildren = false
  Fit = 0
  FitJoin = 0
  InnerFit = 0
  InnerFitJoin = 0
  InvalidShape = false
  Length = 2
  Length2 = 100
  Linearize = true
  NewSolid = false
  Profile = -> Sketch099
  Suppress = false
  TaperInnerAngle = 0
  TaperInnerAngleRev = 0
  TreeRank = 344
  Type = 0
  ValidateShape = true
  _ProfileBasedVersion = 1
  _Version = 1
  expr: Length = <<Parameters>>.screen_relief_depth
FEATURE [PartDesign::Pocket] Pocket044
  AddSubType = 1
  AutoTaperInnerAngle = true
  BaseFeature = -> Pocket049
  CheckUpToFaceLimits = true
  ClaimChildren = false
  Fit = 0
  FitJoin = 0
  InnerFit = 0
  InnerFitJoin = 0
  InvalidShape = false
  Length = 1
  Length2 = 10
  Linearize = true
  NewSolid = false
  Profile = -> Sketch094
  Suppress = false
  TaperInnerAngle = 0
  TaperInnerAngleRev = 0
  TreeRank = 189
  Type = 4
  ValidateShape = true
  _ProfileBasedVersion = 1
  _Version = 1
  expr: Length = <<Parameters>>.lap_join_thickness
FEATURE [Sketcher::SketchObject] Sketch100
  ArcFitTolerance = 1e-06
  AttachmentOffset = pos=(0,0,88) rot=(0,0,1;0rad)
  AttachmentSupport = -> [XZ_Plane015]
  ExternalBSplineMaxDegree = 5
  ExternalBSplineTolerance = 0.0001
  FullyConstrained = true
  InternalTolerance = 1e-06
  InvalidShape = false
  MakeInternals = false
  MapMode = 5
  Placement = pos=(0,-88,1.95e-14) rot=(1,0,0;1.5708rad)
  Support = -> [XZ_Plane015]
  TreeRank = 370
  ValidateShape = true
  expr: AttachmentOffset.Base.z = <<Parameters>>.station_diameter + <<Parameters>>.thickness
  expr: Constraints[101] = (<<Parameters>>.motor_height - <<Parameters>>.motor_shaft_length) / 2
  expr: Constraints[102] = (<<Parameters>>.motor_height - <<Parameters>>.motor_shaft_length) / 2
  expr: Constraints[103] = (<<Parameters>>.motor_height - <<Parameters>>.motor_shaft_length) / 2
  expr: Constraints[104] = <<Parameters>>.station_diameter * 2 + <<Parameters>>.thickness
  expr: Constraints[105] = <<Parameters>>.station_diameter / 3 * 2 - <<Parameters>>.thickness
  expr: Constraints[106] = <<Parameters>>.station_diameter / 3 * 2
  expr: Constraints[26] = <<Parameters>>.motor_height + <<Parameters>>.motor_shaft_length - 2 * <<Parameters>>.thickness
  expr: Constraints[28] = (<<Parameters>>.motor_height - <<Parameters>>.motor_shaft_length) / 2
  sketch-geometry (41):
    g0: LineSegment StartX=0 StartY=16 StartZ=0 EndX=-15.2028 EndY=9.7028 EndZ=0
    g1: LineSegment StartX=-15.2028 StartY=9.7028 StartZ=0 EndX=-21.5 EndY=-5.5 EndZ=0
    g2: LineSegment StartX=-21.5 StartY=-5.5 StartZ=0 EndX=-15.2028 EndY=-20.7028 EndZ=0
    g3: LineSegment StartX=-15.2028 StartY=-20.7028 StartZ=0 EndX=0 EndY=-27 EndZ=0
    g4: LineSegment StartX=0 StartY=-27 StartZ=0 EndX=15.2028 EndY=-20.7028 EndZ=0
    g5: LineSegment StartX=15.2028 StartY=-20.7028 StartZ=0 EndX=21.5 EndY=-5.5 EndZ=0
    g6: LineSegment StartX=21.5 StartY=-5.5 StartZ=0 EndX=15.2028 EndY=9.7028 EndZ=0
    g7: LineSegment StartX=15.2028 StartY=9.7028 StartZ=0 EndX=0 EndY=16 EndZ=0
    g8: Circle [constr] CenterX=-7e-16 CenterY=-5.5 CenterZ=0 NormalX=0 NormalY=0 NormalZ=1 AngleXU=0 Radius=21.5
    g9: LineSegment [constr] StartX=0 StartY=16 StartZ=0 EndX=0 EndY=-27 EndZ=0
    g10: LineSegment StartX=-56.6667 StartY=16 StartZ=0 EndX=-75.2862 EndY=5.25 EndZ=0
    g11: LineSegment StartX=-75.2862 StartY=5.25 StartZ=0 EndX=-75.2862 EndY=-16.25 EndZ=0
    g12: LineSegment StartX=-75.2862 StartY=-16.25 StartZ=0 EndX=-56.6667 EndY=-27 EndZ=0
    g13: LineSegment StartX=-56.6667 StartY=-27 StartZ=0 EndX=-38.0471 EndY=-16.25 EndZ=0
    g14: LineSegment StartX=-38.0471 StartY=-16.25 StartZ=0 EndX=-56.6667 EndY=-27 EndZ=0
    g15: LineSegment StartX=-56.6667 StartY=-27 StartZ=0 EndX=-38.0471 EndY=-16.25 EndZ=0
    g16: LineSegment StartX=-38.0471 StartY=-16.25 StartZ=0 EndX=-38.0471 EndY=5.25 EndZ=0
    g17: LineSegment StartX=-38.0471 StartY=5.25 StartZ=0 EndX=-56.6667 EndY=16 EndZ=0
    g18: Circle [constr] CenterX=-56.6667 CenterY=-5.5 CenterZ=0 NormalX=0 NormalY=0 NormalZ=1 AngleXU=0 Radius=21.5
    g19: LineSegment StartX=-134.536 StartY=9.7028 StartZ=0 EndX=-140.833 EndY=-5.5 EndZ=0
    g20: LineSegment StartX=-140.833 StartY=-5.5 StartZ=0 EndX=-134.536 EndY=-20.7028 EndZ=0
    g21: LineSegment StartX=-134.536 StartY=-20.7028 StartZ=0 EndX=-119.333 EndY=-27 EndZ=0
    g22: LineSegment StartX=-119.333 StartY=-27 StartZ=0 EndX=-104.131 EndY=-20.7028 EndZ=0
    g23: LineSegment StartX=-104.131 StartY=-20.7028 StartZ=0 EndX=-97.8333 EndY=-5.5 EndZ=0
    g24: LineSegment StartX=-97.8333 StartY=-5.5 StartZ=0 EndX=-104.131 EndY=9.7028 EndZ=0
    g25: LineSegment StartX=-104.131 StartY=9.7028 StartZ=0 EndX=-119.333 EndY=16 EndZ=0
    g26: LineSegment StartX=-119.333 StartY=16 StartZ=0 EndX=-134.536 EndY=9.7028 EndZ=0
    g27: Circle [constr] CenterX=-119.333 CenterY=-5.5 CenterZ=0 NormalX=0 NormalY=0 NormalZ=1 AngleXU=0 Radius=21.5
    g28: LineSegment [constr] StartX=-173 StartY=16 StartZ=0 EndX=-188.203 EndY=9.7028 EndZ=0
    g29: LineSegment [constr] StartX=-188.203 StartY=9.7028 StartZ=0 EndX=-194.5 EndY=-5.5 EndZ=0
    g30: LineSegment [constr] StartX=-194.5 StartY=-5.5 StartZ=0 EndX=-188.203 EndY=-20.7028 EndZ=0
    g31: LineSegment [constr] StartX=-188.203 StartY=-20.7028 StartZ=0 EndX=-173 EndY=-27 EndZ=0
    g32: LineSegment StartX=-173 StartY=-27 StartZ=0 EndX=-157.797 EndY=-20.7028 EndZ=0
    g33: LineSegment StartX=-157.797 StartY=-20.7028 StartZ=0 EndX=-151.5 EndY=-5.5 EndZ=0
    g34: LineSegment StartX=-151.5 StartY=-5.5 StartZ=0 EndX=-157.797 EndY=9.7028 EndZ=0
    g35: LineSegment StartX=-157.797 StartY=9.7028 StartZ=0 EndX=-173 EndY=16 EndZ=0
    g36: Circle [constr] CenterX=-173 CenterY=-5.5 CenterZ=0 NormalX=0 NormalY=0 NormalZ=1 AngleXU=0 Radius=21.5
    g37: LineSegment [constr] StartX=-38.0471 StartY=5.25 StartZ=0 EndX=-38.0471 EndY=-16.25 EndZ=0
    g38: LineSegment [constr] StartX=-119.333 StartY=16 StartZ=0 EndX=-119.333 EndY=-27 EndZ=0
    g39: LineSegment StartX=-173 StartY=16 StartZ=0 EndX=-173 EndY=-27 EndZ=0
    g40: LineSegment [constr] StartX=-56.6667 StartY=16 StartZ=0 EndX=-56.6667 EndY=-27 EndZ=0
  constraints (95):
    c: Coincident(g0,g1)
    c: Coincident(g1,g2)
    c: Coincident(g2,g3)
    c: Coincident(g3,g4)
    c: Coincident(g4,g5)
    c: Coincident(g5,g6)
    c: Coincident(g6,g7)
    c: Coincident(g7,g0)
    c: Equal(g0, g1-g7) x7
    c: PointOnObject(g0,g8)
    c: PointOnObject(g1,g8)
    c: PointOnObject(g2,g8)
    c: PointOnObject(g3,g8)
    c: PointOnObject(g4,g8)
    c: PointOnObject(g5,g8)
    c: PointOnObject(g6,g8)
    c: PointOnObject(g7,g8)
    c: Coincident(g9,g0)
    c: Coincident(g9,g3)
    c: Vertical(g9)
    c: Diameter(g8) = 43
    c: PointOnObject(g0,g-2)
    c: DistanceY(g8,g-1) = 5.5
    c: Coincident(g10,g11)
    c: Coincident(g11,g12)
    c: Coincident(g12,g13)
    c: Coincident(g13,g14)
    c: Coincident(g14,g15)
    c: Coincident(g15,g16)
    c: Coincident(g16,g17)
    c: Coincident(g17,g10)
    c: Equal(g10, g11-g17) x7
    c: PointOnObject(g10,g18)
    c: PointOnObject(g11,g18)
    c: PointOnObject(g12,g18)
    c: PointOnObject(g13,g18)
    c: PointOnObject(g14,g18)
    c: PointOnObject(g15,g18)
    c: PointOnObject(g16,g18)
    c: PointOnObject(g17,g18)
    c: Coincident(g19,g20)
    c: Coincident(g20,g21)
    c: Coincident(g21,g22)
    c: Coincident(g22,g23)
    c: Coincident(g23,g24)
    c: Coincident(g24,g25)
    c: Coincident(g25,g26)
    c: Coincident(g26,g19)
    c: Equal(g19, g20-g26) x7
    c: PointOnObject(g19,g27)
    c: PointOnObject(g20,g27)
    c: PointOnObject(g21,g27)
    c: PointOnObject(g22,g27)
    c: PointOnObject(g23,g27)
    c: PointOnObject(g24,g27)
    c: PointOnObject(g25,g27)
    c: PointOnObject(g26,g27)
    c: Coincident(g28,g29)
    c: Coincident(g29,g30)
    c: Coincident(g30,g31)
    c: Coincident(g31,g32)
    c: Coincident(g32,g33)
    c: Coincident(g33,g34)
    c: Coincident(g34,g35)
    c: Coincident(g35,g28)
    c: Equal(g28, g29-g35) x7
    c: PointOnObject(g28,g36)
    c: PointOnObject(g29,g36)
    c: PointOnObject(g30,g36)
    c: PointOnObject(g31,g36)
    c: PointOnObject(g32,g36)
    c: PointOnObject(g33,g36)
    c: PointOnObject(g34,g36)
    c: PointOnObject(g35,g36)
    c: Equal(g8,g18)
    c: Equal(g8,g27)
    c: Equal(g8,g36)
    c: DistanceY(g18,g-1) = 5.5
    c: DistanceY(g27,g-1) = 5.5
    c: DistanceY(g36,g-1) = 5.5
    c: DistanceX(g36,g-1) = 173
    c: DistanceX(g36,g27) = 53.6667
    c: DistanceX(g18,g8) = 56.6667
    c: PointOnObject(g37,g18)
    c: Coincident(g37,g13)
    c: Coincident(g38,g25)
    c: Coincident(g38,g21)
    c: Coincident(g39,g28)
    c: Coincident(g39,g31)
    c: Vertical(g39)
    c: Vertical(g38)
    c: Vertical(g37)
    c: Coincident(g40,g10)
    c: Vertical(g40)
    c: Coincident(g40,g12)
FEATURE [PartDesign::Pocket] Pocket050
  AddSubType = 1
  AutoTaperInnerAngle = true
  BaseFeature = -> Pocket044
  CheckUpToFaceLimits = true
  ClaimChildren = false
  Fit = 0
  FitJoin = 0
  InnerFit = 0
  InnerFitJoin = 0
  InvalidShape = false
  Length = 20
  Length2 = 100
  Linearize = true
  NewSolid = false
  Profile = -> Sketch100
  Reversed = true
  Suppress = false
  TaperInnerAngle = 0
  TaperInnerAngleRev = 0
  TreeRank = 371
  Type = 0
  ValidateShape = true
  _ProfileBasedVersion = 1
  _Version = 1
FEATURE [PartDesign::Fillet] Fillet021
  AddSubType = 0
  Base = -> Pocket050 [Edge209,Edge248,Edge245]
  BaseFeature = -> Pocket050
  InvalidShape = false
  NewSolid = false
  Radius = 3
  SupportTransform = false
  Suppress = false
  TreeRank = 372
  ValidateShape = true
  expr: Radius = <<Parameters>>.thickness
FEATURE [PartDesign::Fillet] Fillet022
  AddSubType = 0
  Base = -> Fillet021 [Edge11,Edge9,Edge7,Edge73,Edge78,Edge68,Edge5,Edge61,Edge19,Edge106,Edge21,Edge110,Edge23,Edge114,Edge17,Edge100,Edge15,Edge98,Edge25,Edge118,Edge26,Edge121,Edge24,Edge117,Edge22,Edge113,Edge20,Edge109,Edge127,Edge30,Edge125,Edge29,Edge123,Edge28,Edge103,Edge18,Edge86,Edge124,Edge87,Edge104,+17 more]
  BaseFeature = -> Fillet021
  InvalidShape = false
  NewSolid = false
  Radius = 1
  SupportTransform = false
  Suppress = false
  TreeRank = 373
  ValidateShape = true
FEATURE [PartDesign::Body] Body015  label="Bottom-Front-Left (B)"
  AutoGroupSolids = false
  ClaimAllChildren = false
  ExportMode = 0
  Group = -> [Sketch088,Pad039,Sketch089,Pad040,Sketch090,Pad041,Sketch091,Pad042,Sketch092,Pocket042,Sketch093,Pocket043,Sketch094,Sketch095,Pocket045,Sketch096,Pocket046,Sketch097,Pocket047,Sketch098,Pocket048,Sketch099,Pocket049,Pocket044,Sketch100,Pocket050,Fillet021,Fillet022]
  InvalidShape = false
  Origin = -> Origin015
  Tip = -> Fillet022
  TreeRank = 213
  ValidateShape = true
  _ExportChildren = -> [Pad039,Pad040,Pad041,Pad042,Pocket042,Pocket043,Pocket045,Pocket046,Pocket047,Pocket048,Pocket049,Pocket044,Pocket050,Fillet021,Fillet022]
  _GroupVersion = 1
FEATURE [Sketcher::SketchObject] Sketch101
  ArcFitTolerance = 1e-06
  AttachmentSupport = -> [YZ_Plane011]
  ExternalBSplineMaxDegree = 5
  ExternalBSplineTolerance = 0.0001
  FullyConstrained = false
  InternalTolerance = 1e-06
  InvalidShape = false
  MakeInternals = false
  MapMode = 5
  Placement = pos=(0,0,0) rot=(0.57735,0.57735,0.57735;2.0944rad)
  Support = -> [YZ_Plane011]
  TreeRank = 176
  ValidateShape = true
  expr: Constraints[12] = <<Parameters>>.thickness + <<Parameters>>.motor_screw_head_height
  expr: Constraints[13] = <<Parameters>>.motor_height
  expr: Constraints[14] = <<Parameters>>.thickness
  expr: Constraints[18] = <<Parameters>>.screen_body_thickness
  expr: Constraints[19] = (<<Parameters>>.station_diameter + <<Parameters>>.thickness) * 2
  expr: Constraints[20] = <<Parameters>>.screen_angle
  expr: Constraints[21] = <<Parameters>>.thickness
  expr: Constraints[25] = <<Parameters>>.thickness
  expr: Constraints[26] = <<Parameters>>.motor_shaft_length
  expr: Constraints[27] = <<Parameters>>.station_diameter + <<Parameters>>.thickness
  expr: Constraints[29] = <<Parameters>>.screen_overall_height + 2 * <<Parameters>>.thickness
  expr: Constraints[39] = <<Parameters>>.thickness
  sketch-geometry (19):
    g0: LineSegment StartX=0 StartY=-36.25 StartZ=0 EndX=-176 EndY=-36.25 EndZ=0
    g1: LineSegment StartX=0 StartY=-36.25 StartZ=0 EndX=0 EndY=-30 EndZ=0
    g2: LineSegment StartX=0 StartY=-30 StartZ=0 EndX=-94.3947 EndY=-30 EndZ=0
    g3: LineSegment StartX=-176 StartY=-36.25 StartZ=0 EndX=-176 EndY=-22.2218 EndZ=0
    g4: LineSegment StartX=-176 StartY=-22.2218 StartZ=0 EndX=-106.178 EndY=47.5998 EndZ=0
    g5: LineSegment StartX=-173 StartY=-30 StartZ=0 EndX=-173 EndY=-27 EndZ=0
    g6: LineSegment StartX=-173 StartY=-27 StartZ=0 EndX=-102.289 EndY=43.7107 EndZ=0
    g7: LineSegment [constr] StartX=-145.835 StartY=0.16482 StartZ=0 EndX=-149.724 EndY=4.05391 EndZ=0
    g8: LineSegment StartX=-88 StartY=22 StartZ=0 EndX=-96.7893 EndY=22 EndZ=0
    g9: LineSegment StartX=-88 StartY=22 StartZ=0 EndX=-88 EndY=19 EndZ=0
    g10: LineSegment StartX=-102.289 StartY=43.7107 StartZ=0 EndX=-102.289 EndY=19 EndZ=0
    g11: LineSegment StartX=-96.7893 StartY=43.7107 StartZ=0 EndX=-96.7893 EndY=22 EndZ=0
    g12: ArcOfCircle CenterX=-102.289 CenterY=43.7107 CenterZ=0 NormalX=0 NormalY=0 NormalZ=1 AngleXU=0 Radius=5.5 StartAngle=0 EndAngle=2.35619
    g13: LineSegment StartX=-97.3947 StartY=-30 StartZ=0 EndX=-97.3947 EndY=14.1053 EndZ=0
    g14: LineSegment StartX=-94.3947 StartY=-30 StartZ=0 EndX=-94.3947 EndY=14.1053 EndZ=0
    g15: LineSegment StartX=-97.3947 StartY=-30 StartZ=0 EndX=-173 EndY=-30 EndZ=0
    g16: LineSegment StartX=-88 StartY=19 StartZ=0 EndX=-89.5 EndY=19 EndZ=0
    g17: LineSegment StartX=-102.289 StartY=19 StartZ=0 EndX=-97.3947 EndY=14.1053 EndZ=0
    g18: LineSegment StartX=-94.3947 StartY=14.1053 StartZ=0 EndX=-89.5 EndY=19 EndZ=0
  constraints (55):
    c: PointOnObject(g0,g-2)
    c: Horizontal(g0)
    c: Coincident(g1,g0)
    c: PointOnObject(g1,g-2)
    c: Coincident(g2,g1)
    c: Horizontal(g2)
    c: Coincident(g3,g0)
    c: Vertical(g3)
    c: Coincident(g4,g3)
    c: Coincident(g5,g15)
    c: Vertical(g5)
    c: Coincident(g6,g5)
    c: DistanceY(g0,g1) = 6.25
    c: DistanceY(g1,g-1) = 30
    c: DistanceX(g0,g15) = 3
    c: Parallel(g6,g4)
    c: PointOnObject(g7,g6)
    c: Perpendicular(g4,g7)
    c: Distance(g7,g7) = 5.5
    c: DistanceX(g0,g-1) = 176
    c: Angle(g5,g6) = 2.35619
    c: DistanceY(g15,g5) = 3
    c: Horizontal(g8)
    c: Coincident(g9,g8)
    c: Vertical(g9)
    c: DistanceY(g9,g8) = 3
    c: DistanceY(g-1,g9) = 19
    c: DistanceX(g9,g-1) = 88
    c: PointOnObject(g7,g4)
    c: Distance(g6,g5) = 100
    c: Coincident(g10,g6)
    c: Vertical(g10)
    c: Coincident(g11,g8)
    c: Vertical(g11)
    c: Tangent(g4,g12) = 1.5708
    c: Tangent(g11,g12) = 1.5708
    c: Coincident(g12,g6)
    c: Vertical(g13)
    c: Vertical(g14)
    c: DistanceX(g13,g14) = 3
    c: Coincident(g2,g14)
    c: Coincident(g15,g13)
    c: Horizontal(g15)
    c: DistanceY(g13,g14) = 0
    c: Coincident(g16,g9)
    c: Horizontal(g16)
    c: DistanceX(g16,g9) = 1.5
    c: Coincident(g17,g10)
    c: Coincident(g17,g13)
    c: Coincident(g18,g14)
    c: Coincident(g18,g16)
    c: DistanceY(g14,g13) = 0
    c: Angle(g17,g10) = 2.35619
    c: Angle(g18,g16) = 2.35619
    c: DistanceY(g16,g10) = 0
FEATURE [PartDesign::Pad] Pad043
  AddSubType = 0
  AlongSketchNormal = false
  AutoTaperInnerAngle = true
  CheckUpToFaceLimits = true
  ClaimChildren = false
  Direction = (1,-2e-16,3e-16)
  Fit = 0
  FitJoin = 0
  InnerFit = 0
  InnerFitJoin = 0
  InvalidShape = false
  Length = 176
  Length2 = 100
  Linearize = true
  NewSolid = false
  Profile = -> Sketch101
  Suppress = false
  TaperInnerAngle = 0
  TaperInnerAngleRev = 0
  TreeRank = 259
  Type = 0
  ValidateShape = true
  _ProfileBasedVersion = 1
  expr: Length = (<<Parameters>>.station_diameter + <<Parameters>>.thickness) * 2
FEATURE [Sketcher::SketchObject] Sketch102
  ArcFitTolerance = 1e-06
  AttachmentSupport = -> [XY_Plane011]
  ExternalBSplineMaxDegree = 5
  ExternalBSplineTolerance = 0.0001
  FullyConstrained = true
  InternalTolerance = 1e-06
  InvalidShape = false
  MakeInternals = false
  MapMode = 5
  Support = -> [XY_Plane011]
  TreeRank = 178
  ValidateShape = true
  expr: Constraints[12] = <<Parameters>>.motor_shaft_mount_diameter / 4
  expr: Constraints[19] = <<Parameters>>.motor_shaft_mount_diameter / 4
  expr: Constraints[1] = <<Parameters>>.motor_shaft_mount_diameter / 4
  expr: Constraints[20] = <<Parameters>>.thickness
  expr: Constraints[21] = (<<Parameters>>.station_diameter + <<Parameters>>.thickness) * 2
  expr: Constraints[22] = <<Parameters>>.station_diameter / 3
  expr: Constraints[23] = (<<Parameters>>.station_diameter + <<Parameters>>.thickness) * 2
  expr: Constraints[28] = <<Parameters>>.thickness
  expr: Constraints[29] = <<Parameters>>.station_diameter / 3 / 2
  expr: Constraints[2] = <<Parameters>>.station_diameter + <<Parameters>>.thickness
  expr: Constraints[32] = <<Parameters>>.motor_shaft_mount_diameter / 4
  expr: Constraints[7] = <<Parameters>>.station_diameter + <<Parameters>>.thickness
  sketch-geometry (11):
    g0: Circle CenterX=88 CenterY=-88 CenterZ=0 NormalX=0 NormalY=0 NormalZ=1 AngleXU=0 Radius=6.25
    g1: ArcOfCircle CenterX=0 CenterY=0 CenterZ=0 NormalX=0 NormalY=0 NormalZ=1 AngleXU=0 Radius=12.5 StartAngle=4.71239 EndAngle=6.28319
    g2: LineSegment StartX=0 StartY=-12.5 StartZ=0 EndX=0 EndY=0 EndZ=0
    g3: LineSegment StartX=0 StartY=0 StartZ=0 EndX=12.5 EndY=0 EndZ=0
    g4: LineSegment StartX=176 StartY=0 StartZ=0 EndX=176 EndY=-176 EndZ=0
    g5: ArcOfCircle CenterX=169.75 CenterY=0 CenterZ=0 NormalX=0 NormalY=0 NormalZ=1 AngleXU=0 Radius=6.25 StartAngle=3.14159 EndAngle=5.25924
    g6: LineSegment StartX=163.5 StartY=0 StartZ=0 EndX=176 EndY=0 EndZ=0
    g7: LineSegment StartX=173 StartY=-5.33854 StartZ=0 EndX=173 EndY=-159.155 EndZ=0
    g8: ArcOfCircle CenterX=158.833 CenterY=-159.155 CenterZ=0 NormalX=0 NormalY=0 NormalZ=1 AngleXU=0 Radius=14.1667 StartAngle=4.92577 EndAngle=6.28319
    g9: LineSegment StartX=176 StartY=-176 StartZ=0 EndX=161.833 EndY=-176 EndZ=0
    g10: LineSegment StartX=161.833 StartY=-176 StartZ=0 EndX=161.833 EndY=-173 EndZ=0
  constraints (33):
    c: Coincident(g1,g-1)
    c: Radius(g1) = 12.5
    c: DistanceY(g0,g1) = 88
    c: Coincident(g2,g1)
    c: Coincident(g3,g1)
    c: Coincident(g1,g3)
    c: Coincident(g1,g2)
    c: DistanceX(g1,g0) = 88
    c: PointOnObject(g1,g-1)
    c: Vertical(g2)
    c: PointOnObject(g4,g-1)
    c: Vertical(g4)
    c: Diameter(g5) = 12.5
    c: Horizontal(g6)
    c: PointOnObject(g5,g6)
    c: Coincident(g6,g4)
    c: Coincident(g5,g6)
    c: Vertical(g7)
    c: Coincident(g5,g7)
    c: DistanceX(g5,g4) = 12.5
    c: DistanceX(g5,g4) = 3
    c: DistanceX(g1,g4) = 176
    c: Diameter(g8) = 28.3333
    c: DistanceY(g4,g4) = 176
    c: Coincident(g9,g4)
    c: Horizontal(g9)
    c: Coincident(g10,g9)
    c: Vertical(g10)
    c: DistanceY(g9,g10) = 3
    c: DistanceX(g9,g4) = 14.1667
    c: Tangent(g8,g7) = 1.5708
    c: Coincident(g8,g10)
    c: Diameter(g0) = 12.5
FEATURE [PartDesign::Pad] Pad044
  AddSubType = 0
  AlongSketchNormal = false
  AutoTaperInnerAngle = true
  BaseFeature = -> Pad043
  CheckUpToFaceLimits = true
  ClaimChildren = false
  Direction = (0,0,1)
  Fit = 0
  FitJoin = 0
  InnerFit = 0
  InnerFitJoin = 0
  InvalidShape = false
  Length = 30
  Length2 = 100
  Linearize = true
  NewSolid = false
  Profile = -> Sketch102
  Reversed = true
  Suppress = false
  TaperInnerAngle = 0
  TaperInnerAngleRev = 0
  TreeRank = 260
  Type = 0
  ValidateShape = true
  _ProfileBasedVersion = 1
  expr: Length = <<Parameters>>.motor_height
FEATURE [Sketcher::SketchObject] Sketch103
  ArcFitTolerance = 1e-06
  AttachmentSupport = -> [XY_Plane011]
  ExternalBSplineMaxDegree = 5
  ExternalBSplineTolerance = 0.0001
  FullyConstrained = true
  InternalTolerance = 1e-06
  InvalidShape = false
  MakeInternals = false
  MapMode = 5
  Support = -> [XY_Plane011]
  TreeRank = 180
  ValidateShape = true
  expr: Constraints[0] = <<Parameters>>.station_diameter + <<Parameters>>.thickness
  expr: Constraints[1] = <<Parameters>>.motor_shaft_mount_diameter / 4
  expr: Constraints[6] = <<Parameters>>.station_diameter + <<Parameters>>.thickness
  sketch-geometry (2):
    g0: ArcOfCircle CenterX=88 CenterY=-88 CenterZ=0 NormalX=0 NormalY=0 NormalZ=1 AngleXU=0 Radius=6.25 StartAngle=3.14159 EndAngle=6.28319
    g1: LineSegment StartX=81.75 StartY=-88 StartZ=0 EndX=94.25 EndY=-88 EndZ=0
  constraints (7):
    c: DistanceY(g0,g-1) = 88
    c: Diameter(g0) = 12.5
    c: Horizontal(g1)
    c: PointOnObject(g0,g1)
    c: Coincident(g0,g1)
    c: Coincident(g0,g1)
    c: DistanceX(g-1,g0) = 88
FEATURE [PartDesign::Pad] Pad045
  AddSubType = 0
  AlongSketchNormal = false
  AutoTaperInnerAngle = true
  BaseFeature = -> Pad044
  CheckUpToFaceLimits = true
  ClaimChildren = false
  Direction = (0,0,1)
  Fit = 0
  FitJoin = 0
  InnerFit = 0
  InnerFitJoin = 0
  InvalidShape = false
  Length = 19
  Length2 = 100
  Linearize = true
  NewSolid = false
  Profile = -> Sketch103
  Suppress = false
  TaperInnerAngle = 0
  TaperInnerAngleRev = 0
  TreeRank = 261
  Type = 0
  ValidateShape = true
  _ProfileBasedVersion = 1
  expr: Length = <<Parameters>>.motor_shaft_length
FEATURE [Sketcher::SketchObject] Sketch104
  ArcFitTolerance = 1e-06
  AttachmentOffset = pos=(0,0,176) rot=(0,0,1;0rad)
  AttachmentSupport = -> [YZ_Plane011]
  ExternalBSplineMaxDegree = 5
  ExternalBSplineTolerance = 0.0001
  FullyConstrained = false
  InternalTolerance = 1e-06
  InvalidShape = false
  MakeInternals = false
  MapMode = 5
  Placement = pos=(176,-3.91e-14,3.91e-14) rot=(0.57735,0.57735,0.57735;2.0944rad)
  Support = -> [YZ_Plane011]
  TreeRank = 182
  ValidateShape = true
  expr: AttachmentOffset.Base.z = (<<Parameters>>.station_diameter + <<Parameters>>.thickness) * 2
  expr: Constraints[12] = <<Parameters>>.thickness + <<Parameters>>.motor_screw_head_height
  expr: Constraints[13] = <<Parameters>>.motor_height
  expr: Constraints[14] = <<Parameters>>.thickness
  expr: Constraints[15] = <<Parameters>>.thickness
  expr: Constraints[16] = (<<Parameters>>.station_diameter + <<Parameters>>.thickness) * 2
  expr: Constraints[17] = <<Parameters>>.thickness
  expr: Constraints[21] = <<Parameters>>.thickness
  expr: Constraints[22] = <<Parameters>>.motor_shaft_length
  expr: Constraints[23] = <<Parameters>>.station_diameter + <<Parameters>>.thickness
  expr: Constraints[26] = <<Parameters>>.screen_overall_height + 2 * <<Parameters>>.thickness
  expr: Constraints[47] = 180 - <<Parameters>>.screen_angle
  sketch-geometry (19):
    g0: LineSegment [constr] StartX=0 StartY=-36.25 StartZ=0 EndX=-176 EndY=-36.25 EndZ=0
    g1: LineSegment [constr] StartX=0 StartY=-36.25 StartZ=0 EndX=0 EndY=-30 EndZ=0
    g2: LineSegment [constr] StartX=0 StartY=-30 StartZ=0 EndX=-173 EndY=-30 EndZ=0
    g3: LineSegment [constr] StartX=-176 StartY=-36.25 StartZ=0 EndX=-176 EndY=-25.7574 EndZ=0
    g4: LineSegment [constr] StartX=-173 StartY=-30 StartZ=0 EndX=-173 EndY=-27 EndZ=0
    g5: LineSegment [constr] StartX=-145.194 StartY=0.805848 StartZ=0 EndX=-147.315 EndY=2.92717 EndZ=0
    g6: LineSegment StartX=-88 StartY=22 StartZ=0 EndX=-99.2893 EndY=22 EndZ=0
    g7: LineSegment StartX=-88 StartY=22 StartZ=0 EndX=-88 EndY=19 EndZ=0
    g8: LineSegment [constr] StartX=-102.289 StartY=19 StartZ=0 EndX=-88 EndY=19 EndZ=0
    g9: LineSegment [constr] StartX=-102.289 StartY=43.7107 StartZ=0 EndX=-102.289 EndY=19 EndZ=0
    g10: LineSegment StartX=-99.2893 StartY=43.7107 StartZ=0 EndX=-99.2893 EndY=22 EndZ=0
    g11: ArcOfCircle CenterX=-102.289 CenterY=43.7107 CenterZ=0 NormalX=0 NormalY=0 NormalZ=1 AngleXU=0 Radius=3 StartAngle=1e-16 EndAngle=2.35619
    g12: LineSegment [constr] StartX=-176 StartY=-25.7574 StartZ=0 EndX=-150.243 EndY=0 EndZ=0
    g13: LineSegment StartX=-150.243 StartY=0 StartZ=0 EndX=-104.411 EndY=45.832 EndZ=0
    g14: LineSegment [constr] StartX=-173 StartY=-27 StartZ=0 EndX=-146 EndY=0 EndZ=0
    g15: LineSegment [constr] StartX=-146 StartY=0 StartZ=0 EndX=-102.289 EndY=43.7107 EndZ=0
    g16: LineSegment StartX=-150.243 StartY=0 StartZ=0 EndX=-146 EndY=0 EndZ=0
    g17: LineSegment StartX=-146 StartY=0 StartZ=0 EndX=-88 EndY=0 EndZ=0
    g18: LineSegment StartX=-88 StartY=0 StartZ=0 EndX=-88 EndY=19 EndZ=0
  constraints (53):
    c: PointOnObject(g0,g-2)
    c: Horizontal(g0)
    c: Coincident(g1,g0)
    c: PointOnObject(g1,g-2)
    c: Coincident(g2,g1)
    c: Horizontal(g2)
    c: Coincident(g3,g0)
    c: Vertical(g3)
    c: Coincident(g12,g3)
    c: Coincident(g4,g2)
    c: Vertical(g4)
    c: Coincident(g14,g4)
    c: DistanceY(g0,g1) = 6.25
    c: DistanceY(g1,g-1) = 30
    c: DistanceX(g0,g2) = 3
    c: Distance(g5,g5) = 3
    c: DistanceX(g0,g-1) = 176
    c: DistanceY(g2,g4) = 3
    c: Horizontal(g6)
    c: Coincident(g7,g6)
    c: Vertical(g7)
    c: DistanceY(g7,g6) = 3
    c: DistanceY(g-1,g7) = 19
    c: DistanceX(g7,g-1) = 88
    c: Coincident(g8,g7)
    c: Horizontal(g8)
    c: Distance(g15,g4) = 100
    c: Coincident(g9,g15)
    c: Coincident(g9,g8)
    c: Vertical(g9)
    c: Coincident(g10,g6)
    c: Vertical(g10)
    c: Tangent(g13,g11) = 1.5708
    c: Tangent(g10,g11) = 1.5708
    c: Coincident(g11,g15)
    c: Coincident(g12,g13)
    c: Perpendicular(g12,g5)
    c: PointOnObject(g5,g13)
    c: Coincident(g14,g15)
    c: PointOnObject(g5,g14)
    c: Parallel(g14,g12)
    c: Parallel(g15,g12)
    c: Parallel(g14,g13)
    c: Coincident(g16,g12)
    c: Coincident(g16,g14)
    c: Horizontal(g16)
    c: PointOnObject(g12,g-1)
    c: Angle(g-1,g13) = 0.785398
    c: Coincident(g17,g15)
    c: PointOnObject(g17,g-1)
    c: Coincident(g18,g17)
    c: Coincident(g18,g7)
    c: Vertical(g18)
FEATURE [PartDesign::Pad] Pad046
  AddSubType = 0
  AlongSketchNormal = false
  AutoTaperInnerAngle = true
  BaseFeature = -> Pad045
  CheckUpToFaceLimits = true
  ClaimChildren = false
  Direction = (1,-3e-16,3e-16)
  Fit = 0
  FitJoin = 0
  InnerFit = 0
  InnerFitJoin = 0
  InvalidShape = false
  Length = 3
  Length2 = 100
  Linearize = true
  NewSolid = false
  Profile = -> Sketch104
  Reversed = true
  Suppress = false
  TaperInnerAngle = 0
  TaperInnerAngleRev = 0
  TreeRank = 262
  Type = 0
  ValidateShape = true
  _ProfileBasedVersion = 1
  expr: Length = <<Parameters>>.thickness
FEATURE [Sketcher::SketchObject] Sketch105
  ArcFitTolerance = 1e-06
  ExternalBSplineMaxDegree = 5
  ExternalBSplineTolerance = 0.0001
  FullyConstrained = false
  InternalTolerance = 1e-06
  InvalidShape = false
  MakeInternals = false
  MapMode = 2
  Placement = pos=(88,-88,0) rot=(0.57735,0.57735,0.57735;0rad)
  TreeRank = 184
  ValidateShape = true
  expr: Placement.Base.x = <<Parameters>>.station_diameter + <<Parameters>>.thickness
  expr: Placement.Base.y = -(<<Parameters>>.station_diameter + <<Parameters>>.thickness)
  expr: Constraints[0] = <<Parameters>>.station_diameter
  expr: Constraints[14] = <<Parameters>>.motor_screw_spacing
  expr: Constraints[29] = <<Parameters>>.motor_screw_shaft_diameter
  expr: Constraints[3] = <<Parameters>>.station_diameter
  sketch-geometry (20):
    g0: Circle [constr] CenterX=-42.5 CenterY=42.5 CenterZ=0 NormalX=0 NormalY=0 NormalZ=1 AngleXU=0 Radius=42.5
    g1: Circle [constr] CenterX=42.5 CenterY=42.5 CenterZ=0 NormalX=0 NormalY=0 NormalZ=1 AngleXU=0 Radius=42.5
    g2: LineSegment [constr] StartX=-29.5 StartY=29.5 StartZ=0 EndX=-29.5 EndY=55.5 EndZ=0
    g3: LineSegment [constr] StartX=-29.5 StartY=55.5 StartZ=0 EndX=-55.5 EndY=55.5 EndZ=0
    g4: LineSegment [constr] StartX=-55.5 StartY=55.5 StartZ=0 EndX=-55.5 EndY=29.5 EndZ=0
    g5: LineSegment [constr] StartX=-55.5 StartY=29.5 StartZ=0 EndX=-29.5 EndY=29.5 EndZ=0
    g6: GeomPoint [constr] X=-42.5 Y=42.5 Z=0
    g7: LineSegment [constr] StartX=55.5 StartY=29.5 StartZ=0 EndX=55.5 EndY=55.5 EndZ=0
    g8: LineSegment [constr] StartX=55.5 StartY=55.5 StartZ=0 EndX=29.5 EndY=55.5 EndZ=0
    g9: LineSegment [constr] StartX=29.5 StartY=55.5 StartZ=0 EndX=29.5 EndY=29.5 EndZ=0
    g10: LineSegment [constr] StartX=29.5 StartY=29.5 StartZ=0 EndX=55.5 EndY=29.5 EndZ=0
    g11: GeomPoint [constr] X=42.5 Y=42.5 Z=0
    g12: Circle CenterX=-55.5 CenterY=55.5 CenterZ=0 NormalX=0 NormalY=0 NormalZ=1 AngleXU=0 Radius=1.75
    g13: Circle CenterX=-29.5 CenterY=55.5 CenterZ=0 NormalX=0 NormalY=0 NormalZ=1 AngleXU=0 Radius=1.75
    g14: Circle CenterX=-29.5 CenterY=29.5 CenterZ=0 NormalX=0 NormalY=0 NormalZ=1 AngleXU=0 Radius=1.75
    g15: Circle CenterX=-55.5 CenterY=29.5 CenterZ=0 NormalX=0 NormalY=0 NormalZ=1 AngleXU=0 Radius=1.75
    g16: Circle CenterX=29.5 CenterY=55.5 CenterZ=0 NormalX=0 NormalY=0 NormalZ=1 AngleXU=0 Radius=1.75
    g17: Circle CenterX=55.5 CenterY=55.5 CenterZ=0 NormalX=0 NormalY=0 NormalZ=1 AngleXU=0 Radius=1.75
    g18: Circle CenterX=55.5 CenterY=29.5 CenterZ=0 NormalX=0 NormalY=0 NormalZ=1 AngleXU=0 Radius=1.75
    g19: Circle CenterX=29.5 CenterY=29.5 CenterZ=0 NormalX=0 NormalY=0 NormalZ=1 AngleXU=0 Radius=1.75
  constraints (44):
    c: Diameter(g0) = 85
    c: Equal(g0,g1)
    c: Symmetric(g0,g1,g-2)
    c: DistanceX(g0,g1) = 85
    c: Coincident(g2,g3)
    c: Coincident(g3,g4)
    c: Coincident(g4,g5)
    c: Coincident(g5,g2)
    c: Horizontal(g3)
    c: Horizontal(g5)
    c: Vertical(g2)
    c: Vertical(g4)
    c: Symmetric(g3,g2,g6)
    c: Coincident(g6,g0)
    c: DistanceX(g3,g2) = 26
    c: Equal(g3,g4)
    c: Coincident(g7,g8)
    c: Coincident(g8,g9)
    c: Coincident(g9,g10)
    c: Coincident(g10,g7)
    c: Horizontal(g8)
    c: Horizontal(g10)
    c: Vertical(g7)
    c: Vertical(g9)
    c: Symmetric(g8,g7,g11)
    c: Coincident(g11,g1)
    c: Equal(g3,g8)
    c: Equal(g3,g9)
    c: Coincident(g12,g3)
    c: Diameter(g12) = 3.5
    c: Coincident(g13,g2)
    c: Coincident(g14,g2)
    c: Coincident(g15,g4)
    c: Coincident(g16,g8)
    c: Coincident(g17,g7)
    c: Coincident(g18,g7)
    c: Coincident(g19,g9)
    c: Equal(g12,g13)
    c: Equal(g12,g15)
    c: Equal(g12,g14)
    c: Equal(g12,g16)
    c: Equal(g16,g17)
    c: Equal(g16,g19)
    c: Equal(g16,g18)
FEATURE [PartDesign::Pocket] Pocket051
  AddSubType = 1
  AutoTaperInnerAngle = true
  BaseFeature = -> Pad046
  CheckUpToFaceLimits = true
  ClaimChildren = false
  Fit = 0
  FitJoin = 0
  InnerFit = 0
  InnerFitJoin = 0
  InvalidShape = false
  Length = 100
  Length2 = 100
  Linearize = true
  NewSolid = false
  Profile = -> Sketch105
  Suppress = false
  TaperInnerAngle = 0
  TaperInnerAngleRev = 0
  TreeRank = 264
  Type = 0
  ValidateShape = true
  _ProfileBasedVersion = 1
  _Version = 1
FEATURE [Sketcher::SketchObject] Sketch106
  ArcFitTolerance = 1e-06
  ExternalBSplineMaxDegree = 5
  ExternalBSplineTolerance = 0.0001
  FullyConstrained = false
  InternalTolerance = 1e-06
  InvalidShape = false
  MakeInternals = false
  MapMode = 2
  Placement = pos=(88,-88,-36.25) rot=(0.57735,0.57735,0.57735;0rad)
  TreeRank = 186
  ValidateShape = true
  expr: Placement.Base.x = <<Parameters>>.station_diameter + <<Parameters>>.thickness
  expr: Placement.Base.y = -(<<Parameters>>.station_diameter + <<Parameters>>.thickness)
  expr: Placement.Base.z = -(<<Parameters>>.motor_height + <<Parameters>>.thickness + <<Parameters>>.motor_screw_head_height)
  expr: Constraints[0] = <<Parameters>>.station_diameter
  expr: Constraints[14] = <<Parameters>>.motor_screw_spacing
  expr: Constraints[29] = <<Parameters>>.motor_screw_head_diameter
  expr: Constraints[3] = <<Parameters>>.station_diameter
  sketch-geometry (20):
    g0: Circle [constr] CenterX=-42.5 CenterY=42.5 CenterZ=0 NormalX=0 NormalY=0 NormalZ=1 AngleXU=0 Radius=42.5
    g1: Circle [constr] CenterX=42.5 CenterY=42.5 CenterZ=0 NormalX=0 NormalY=0 NormalZ=1 AngleXU=0 Radius=42.5
    g2: LineSegment [constr] StartX=-29.5 StartY=29.5 StartZ=0 EndX=-29.5 EndY=55.5 EndZ=0
    g3: LineSegment [constr] StartX=-29.5 StartY=55.5 StartZ=0 EndX=-55.5 EndY=55.5 EndZ=0
    g4: LineSegment [constr] StartX=-55.5 StartY=55.5 StartZ=0 EndX=-55.5 EndY=29.5 EndZ=0
    g5: LineSegment [constr] StartX=-55.5 StartY=29.5 StartZ=0 EndX=-29.5 EndY=29.5 EndZ=0
    g6: GeomPoint [constr] X=-42.5 Y=42.5 Z=0
    g7: LineSegment [constr] StartX=55.5 StartY=29.5 StartZ=0 EndX=55.5 EndY=55.5 EndZ=0
    g8: LineSegment [constr] StartX=55.5 StartY=55.5 StartZ=0 EndX=29.5 EndY=55.5 EndZ=0
    g9: LineSegment [constr] StartX=29.5 StartY=55.5 StartZ=0 EndX=29.5 EndY=29.5 EndZ=0
    g10: LineSegment [constr] StartX=29.5 StartY=29.5 StartZ=0 EndX=55.5 EndY=29.5 EndZ=0
    g11: GeomPoint [constr] X=42.5 Y=42.5 Z=0
    g12: Circle CenterX=-55.5 CenterY=55.5 CenterZ=0 NormalX=0 NormalY=0 NormalZ=1 AngleXU=0 Radius=3
    g13: Circle CenterX=-29.5 CenterY=55.5 CenterZ=0 NormalX=0 NormalY=0 NormalZ=1 AngleXU=0 Radius=3
    g14: Circle CenterX=-29.5 CenterY=29.5 CenterZ=0 NormalX=0 NormalY=0 NormalZ=1 AngleXU=0 Radius=3
    g15: Circle CenterX=-55.5 CenterY=29.5 CenterZ=0 NormalX=0 NormalY=0 NormalZ=1 AngleXU=0 Radius=3
    g16: Circle CenterX=29.5 CenterY=55.5 CenterZ=0 NormalX=0 NormalY=0 NormalZ=1 AngleXU=0 Radius=3
    g17: Circle CenterX=55.5 CenterY=55.5 CenterZ=0 NormalX=0 NormalY=0 NormalZ=1 AngleXU=0 Radius=3
    g18: Circle CenterX=55.5 CenterY=29.5 CenterZ=0 NormalX=0 NormalY=0 NormalZ=1 AngleXU=0 Radius=3
    g19: Circle CenterX=29.5 CenterY=29.5 CenterZ=0 NormalX=0 NormalY=0 NormalZ=1 AngleXU=0 Radius=3
  constraints (44):
    c: Diameter(g0) = 85
    c: Equal(g0,g1)
    c: Symmetric(g0,g1,g-2)
    c: DistanceX(g0,g1) = 85
    c: Coincident(g2,g3)
    c: Coincident(g3,g4)
    c: Coincident(g4,g5)
    c: Coincident(g5,g2)
    c: Horizontal(g3)
    c: Horizontal(g5)
    c: Vertical(g2)
    c: Vertical(g4)
    c: Symmetric(g3,g2,g6)
    c: Coincident(g6,g0)
    c: DistanceX(g3,g2) = 26
    c: Equal(g3,g4)
    c: Coincident(g7,g8)
    c: Coincident(g8,g9)
    c: Coincident(g9,g10)
    c: Coincident(g10,g7)
    c: Horizontal(g8)
    c: Horizontal(g10)
    c: Vertical(g7)
    c: Vertical(g9)
    c: Symmetric(g8,g7,g11)
    c: Coincident(g11,g1)
    c: Equal(g3,g8)
    c: Equal(g3,g9)
    c: Coincident(g12,g3)
    c: Diameter(g12) = 6
    c: Coincident(g13,g2)
    c: Coincident(g14,g2)
    c: Coincident(g15,g4)
    c: Coincident(g16,g8)
    c: Coincident(g17,g7)
    c: Coincident(g18,g7)
    c: Coincident(g19,g9)
    c: Equal(g12,g13)
    c: Equal(g12,g15)
    c: Equal(g12,g14)
    c: Equal(g12,g16)
    c: Equal(g16,g17)
    c: Equal(g16,g19)
    c: Equal(g16,g18)
FEATURE [PartDesign::Pocket] Pocket052
  AddSubType = 1
  AutoTaperInnerAngle = true
  BaseFeature = -> Pocket051
  CheckUpToFaceLimits = true
  ClaimChildren = false
  Fit = 0
  FitJoin = 0
  InnerFit = 0
  InnerFitJoin = 0
  InvalidShape = false
  Length = 3.25
  Length2 = 100
  Linearize = true
  NewSolid = false
  Profile = -> Sketch106
  Reversed = true
  Suppress = false
  TaperInnerAngle = 0
  TaperInnerAngleRev = 0
  TreeRank = 265
  Type = 0
  ValidateShape = true
  _ProfileBasedVersion = 1
  _Version = 1
  expr: Length = <<Parameters>>.motor_screw_head_height
FEATURE [Sketcher::SketchObject] Sketch107
  ArcFitTolerance = 1e-06
  ExternalBSplineMaxDegree = 5
  ExternalBSplineTolerance = 0.0001
  FullyConstrained = true
  InternalTolerance = 1e-06
  InvalidShape = false
  MakeInternals = false
  MapMode = 2
  Placement = pos=(88,-88,-30) rot=(0.57735,0.57735,0.57735;0rad)
  TreeRank = 188
  ValidateShape = true
  expr: Placement.Base.x = <<Parameters>>.station_diameter + <<Parameters>>.thickness
  expr: Placement.Base.y = -(<<Parameters>>.station_diameter + <<Parameters>>.thickness)
  expr: Placement.Base.z = -<<Parameters>>.motor_height
  expr: Constraints[14] = <<Parameters>>.thickness * 2
  expr: Constraints[17] = <<Parameters>>.station_diameter + <<Parameters>>.thickness
  expr: Constraints[18] = (<<Parameters>>.station_diameter + <<Parameters>>.thickness) * 2 - 4 * <<Parameters>>.thickness - <<Parameters>>.motor_shaft_mount_diameter / 2
  expr: Constraints[21] = <<Parameters>>.station_diameter + <<Parameters>>.thickness
  sketch-geometry (8):
    g0: LineSegment StartX=-82 StartY=69.5 StartZ=0 EndX=-88 EndY=69.5 EndZ=0
    g1: LineSegment StartX=-88 StartY=69.5 StartZ=0 EndX=-88 EndY=-69.5 EndZ=0
    g2: LineSegment StartX=-88 StartY=-69.5 StartZ=0 EndX=-82 EndY=-69.5 EndZ=0
    g3: LineSegment StartX=-82 StartY=-69.5 StartZ=0 EndX=-82 EndY=69.5 EndZ=0
    g4: LineSegment StartX=-69.5 StartY=82 StartZ=0 EndX=69.5 EndY=82 EndZ=0
    g5: LineSegment StartX=69.5 StartY=82 StartZ=0 EndX=69.5 EndY=88 EndZ=0
    g6: LineSegment StartX=69.5 StartY=88 StartZ=0 EndX=-69.5 EndY=88 EndZ=0
    g7: LineSegment StartX=-69.5 StartY=88 StartZ=0 EndX=-69.5 EndY=82 EndZ=0
  constraints (22):
    c: Coincident(g0,g1)
    c: Coincident(g1,g2)
    c: Coincident(g2,g3)
    c: Coincident(g3,g0)
    c: Horizontal(g0)
    c: Horizontal(g2)
    c: Vertical(g1)
    c: Coincident(g4,g5)
    c: Coincident(g5,g6)
    c: Coincident(g6,g7)
    c: Coincident(g7,g4)
    c: Horizontal(g6)
    c: Vertical(g5)
    c: Vertical(g7)
    c: DistanceX(g0,g0) = 6
    c: Equal(g0,g5)
    c: Symmetric(g4,g4,g-2)
    c: DistanceY(g-1,g6) = 88
    c: DistanceX(g6,g5) = 139
    c: Equal(g6,g3)
    c: Symmetric(g0,g2,g-1)
    c: DistanceX(g0,g-1) = 88
FEATURE [Sketcher::SketchObject] Sketch108
  ArcFitTolerance = 1e-06
  AttachmentSupport = -> [XY_Plane011]
  ExternalBSplineMaxDegree = 5
  ExternalBSplineTolerance = 0.0001
  FullyConstrained = true
  InternalTolerance = 1e-06
  InvalidShape = false
  MakeInternals = false
  MapMode = 5
  Support = -> [XY_Plane011]
  TreeRank = 190
  ValidateShape = true
  expr: Constraints[18] = <<Parameters>>.station_diameter / 3
  expr: Constraints[21] = (<<Parameters>>.station_diameter + <<Parameters>>.thickness) * 2
  expr: Constraints[8] = (<<Parameters>>.station_diameter + <<Parameters>>.thickness) * 2 * 2
  sketch-geometry (10):
    g0: LineSegment StartX=-88 StartY=88 StartZ=0 EndX=264 EndY=88 EndZ=0
    g1: LineSegment StartX=264 StartY=88 StartZ=0 EndX=264 EndY=-264 EndZ=0
    g2: LineSegment StartX=264 StartY=-264 StartZ=0 EndX=-88 EndY=-264 EndZ=0
    g3: LineSegment StartX=-88 StartY=-264 StartZ=0 EndX=-88 EndY=88 EndZ=0
    g4: LineSegment StartX=176 StartY=-161.833 StartZ=0 EndX=176 EndY=0 EndZ=0
    g5: LineSegment StartX=176 StartY=0 StartZ=0 EndX=0 EndY=0 EndZ=0
    g6: LineSegment StartX=0 StartY=0 StartZ=0 EndX=0 EndY=-176 EndZ=0
    g7: LineSegment StartX=0 StartY=-176 StartZ=0 EndX=161.833 EndY=-176 EndZ=0
    g8: GeomPoint [constr] X=88 Y=-88 Z=0
    g9: ArcOfCircle CenterX=161.833 CenterY=-161.833 CenterZ=0 NormalX=0 NormalY=0 NormalZ=1 AngleXU=0 Radius=14.1667 StartAngle=4.71239 EndAngle=6.28319
  constraints (25):
    c: Coincident(g0,g1)
    c: Coincident(g1,g2)
    c: Coincident(g2,g3)
    c: Coincident(g3,g0)
    c: Horizontal(g0)
    c: Horizontal(g2)
    c: Vertical(g1)
    c: Vertical(g3)
    c: DistanceX(g0,g0) = 352
    c: Equal(g0,g1)
    c: Coincident(g4,g5)
    c: Coincident(g5,g6)
    c: Coincident(g6,g7)
    c: Horizontal(g5)
    c: Horizontal(g7)
    c: Vertical(g4)
    c: Vertical(g6)
    c: Equal(g5,g6)
    c: Diameter(g9) = 28.3333
    c: Symmetric(g0,g1,g8)
    c: Coincident(g5,g-1)
    c: DistanceX(g5,g4) = 176
    c: Symmetric(g6,g4,g8)
    c: Tangent(g9,g4) = -1.5708
    c: Tangent(g9,g7) = -1.5708
FEATURE [PartDesign::Pocket] Pocket054
  AddSubType = 1
  AutoTaperInnerAngle = true
  BaseFeature = -> Pocket052
  CheckUpToFaceLimits = true
  ClaimChildren = false
  Fit = 0
  FitJoin = 0
  InnerFit = 0
  InnerFitJoin = 0
  InvalidShape = false
  Length = 100
  Length2 = 100
  Linearize = true
  NewSolid = false
  Profile = -> Sketch108
  Suppress = false
  TaperInnerAngle = 0
  TaperInnerAngleRev = 0
  TreeRank = 269
  Type = 4
  ValidateShape = true
  _ProfileBasedVersion = 1
  _Version = 1
FEATURE [Sketcher::SketchObject] Sketch109
  ArcFitTolerance = 1e-06
  AttachmentSupport = -> [YZ_Plane011]
  ExternalBSplineMaxDegree = 5
  ExternalBSplineTolerance = 0.0001
  FullyConstrained = false
  InternalTolerance = 1e-06
  InvalidShape = false
  MakeInternals = false
  MapMode = 5
  Placement = pos=(0,0,0) rot=(0.57735,0.57735,0.57735;2.0944rad)
  Support = -> [YZ_Plane011]
  TreeRank = 192
  ValidateShape = true
  expr: Constraints[12] = <<Parameters>>.thickness + <<Parameters>>.motor_screw_head_height
  expr: Constraints[13] = <<Parameters>>.motor_height
  expr: Constraints[14] = <<Parameters>>.thickness
  expr: Constraints[18] = <<Parameters>>.screen_body_thickness
  expr: Constraints[19] = (<<Parameters>>.station_diameter + <<Parameters>>.thickness) * 2
  expr: Constraints[20] = <<Parameters>>.screen_angle
  expr: Constraints[21] = <<Parameters>>.thickness
  expr: Constraints[25] = <<Parameters>>.thickness
  expr: Constraints[26] = <<Parameters>>.motor_shaft_length
  expr: Constraints[27] = <<Parameters>>.station_diameter + <<Parameters>>.thickness
  expr: Constraints[31] = <<Parameters>>.screen_overall_height + 2 * <<Parameters>>.thickness
  expr: Constraints[47] = 10 * <<Parameters>>.thickness
  sketch-geometry (17):
    g0: LineSegment [constr] StartX=0 StartY=-36.25 StartZ=0 EndX=-176 EndY=-36.25 EndZ=0
    g1: LineSegment [constr] StartX=0 StartY=-36.25 StartZ=0 EndX=0 EndY=-30 EndZ=0
    g2: LineSegment [constr] StartX=0 StartY=-30 StartZ=0 EndX=-173 EndY=-30 EndZ=0
    g3: LineSegment [constr] StartX=-176 StartY=-36.25 StartZ=0 EndX=-176 EndY=-22.2218 EndZ=0
    g4: LineSegment StartX=-176 StartY=-22.2218 StartZ=0 EndX=-106.178 EndY=47.5998 EndZ=0
    g5: LineSegment [constr] StartX=-173 StartY=-30 StartZ=0 EndX=-173 EndY=-27 EndZ=0
    g6: LineSegment [constr] StartX=-173 StartY=-27 StartZ=0 EndX=-102.289 EndY=43.7107 EndZ=0
    g7: LineSegment [constr] StartX=-145.874 StartY=0.12624 StartZ=0 EndX=-149.763 EndY=4.01533 EndZ=0
    g8: LineSegment [constr] StartX=-88 StartY=22 StartZ=0 EndX=-96.7893 EndY=22 EndZ=0
    g9: LineSegment [constr] StartX=-88 StartY=22 StartZ=0 EndX=-88 EndY=19 EndZ=0
    g10: LineSegment [constr] StartX=-102.289 StartY=19 StartZ=0 EndX=-88 EndY=19 EndZ=0
    g11: LineSegment [constr] StartX=-102.289 StartY=43.7107 StartZ=0 EndX=-102.289 EndY=19 EndZ=0
    g12: LineSegment [constr] StartX=-96.7893 StartY=43.7107 StartZ=0 EndX=-96.7893 EndY=22 EndZ=0
    g13: ArcOfCircle [constr] CenterX=-102.289 CenterY=43.7107 CenterZ=0 NormalX=0 NormalY=0 NormalZ=1 AngleXU=0 Radius=5.5 StartAngle=-1.4149e-12 EndAngle=2.35619
    g14: LineSegment StartX=-176 StartY=-22.2218 StartZ=0 EndX=-197.213 EndY=-1.00862 EndZ=0
    g15: LineSegment StartX=-106.178 StartY=47.5998 StartZ=0 EndX=-127.392 EndY=68.813 EndZ=0
    g16: LineSegment StartX=-127.392 StartY=68.813 StartZ=0 EndX=-197.213 EndY=-1.00862 EndZ=0
  constraints (48):
    c: PointOnObject(g0,g-2)
    c: Horizontal(g0)
    c: Coincident(g1,g0)
    c: PointOnObject(g1,g-2)
    c: Coincident(g2,g1)
    c: Horizontal(g2)
    c: Coincident(g3,g0)
    c: Vertical(g3)
    c: Coincident(g4,g3)
    c: Coincident(g5,g2)
    c: Vertical(g5)
    c: Coincident(g6,g5)
    c: DistanceY(g0,g1) = 6.25
    c: DistanceY(g1,g-1) = 30
    c: DistanceX(g0,g2) = 3
    c: Parallel(g6,g4)
    c: PointOnObject(g7,g6)
    c: Perpendicular(g4,g7)
    c: Distance(g7,g7) = 5.5
    c: DistanceX(g0,g-1) = 176
    c: Angle(g5,g6) = 2.35619
    c: DistanceY(g2,g5) = 3
    c: Horizontal(g8)
    c: Coincident(g9,g8)
    c: Vertical(g9)
    c: DistanceY(g9,g8) = 3
    c: DistanceY(g-1,g9) = 19
    c: DistanceX(g9,g-1) = 88
    c: PointOnObject(g7,g4)
    c: Coincident(g10,g9)
    c: Horizontal(g10)
    c: Distance(g6,g5) = 100
    c: Coincident(g11,g6)
    c: Coincident(g11,g10)
    c: Vertical(g11)
    c: Coincident(g12,g8)
    c: Vertical(g12)
    c: Tangent(g4,g13) = 1.5708
    c: Tangent(g12,g13) = 1.5708
    c: Coincident(g13,g6)
    c: Coincident(g14,g3)
    c: Coincident(g15,g4)
    c: Coincident(g16,g14)
    c: Parallel(g15,g14)
    c: Parallel(g4,g16)
    c: Coincident(g15,g16)
    c: Perpendicular(g14,g4)
    c: Distance(g4,g14) = 30
FEATURE [PartDesign::Pocket] Pocket055
  AddSubType = 1
  AutoTaperInnerAngle = true
  BaseFeature = -> Pocket054
  CheckUpToFaceLimits = true
  ClaimChildren = false
  Fit = 0
  FitJoin = 0
  InnerFit = 0
  InnerFitJoin = 0
  InvalidShape = false
  Length = 500
  Length2 = 100
  Linearize = true
  NewSolid = false
  Profile = -> Sketch109
  Reversed = true
  Suppress = false
  TaperInnerAngle = 0
  TaperInnerAngleRev = 0
  TreeRank = 268
  Type = 0
  ValidateShape = true
  _ProfileBasedVersion = 1
  _Version = 1
FEATURE [Sketcher::SketchObject] Sketch110
  ArcFitTolerance = 1e-06
  ExternalBSplineMaxDegree = 5
  ExternalBSplineTolerance = 0.0001
  FullyConstrained = true
  InternalTolerance = 1e-06
  InvalidShape = false
  MakeInternals = false
  MapMode = 5
  Placement = pos=(176,0,0) rot=(0.57735,0.57735,0.57735;2.0944rad)
  TreeRank = 296
  ValidateShape = true
  expr: Constraints[0] = <<Parameters>>.fan_screw_hole_diameter
  expr: Constraints[12] = <<Parameters>>.fan_diameter
  expr: Constraints[13] = <<Parameters>>.fan_diameter / 2 - <<Parameters>>.thickness
  expr: Constraints[14] = <<Parameters>>.station_diameter * 1.25 + <<Parameters>>.thickness
  expr: Constraints[4] = <<Parameters>>.fan_screw_distance
  expr: Constraints[6] = <<Parameters>>.fan_screw_distance
  expr: Constraints[9] = 0
  sketch-geometry (6):
    g0: GeomPoint [constr] X=-109.25 Y=-11 Z=0
    g1: Circle CenterX=-123.25 CenterY=3 CenterZ=0 NormalX=0 NormalY=0 NormalZ=1 AngleXU=0 Radius=1.3
    g2: Circle CenterX=-95.25 CenterY=3 CenterZ=0 NormalX=0 NormalY=0 NormalZ=1 AngleXU=0 Radius=1.3
    g3: Circle CenterX=-123.25 CenterY=-25 CenterZ=0 NormalX=0 NormalY=0 NormalZ=1 AngleXU=0 Radius=1.3
    g4: Circle CenterX=-95.25 CenterY=-25 CenterZ=0 NormalX=0 NormalY=0 NormalZ=1 AngleXU=0 Radius=1.3
    g5: Circle CenterX=-109.25 CenterY=-11 CenterZ=0 NormalX=0 NormalY=0 NormalZ=1 AngleXU=0 Radius=14
  constraints (15):
    c: Diameter(g1) = 2.6
    c: Equal(g1,g2)
    c: Equal(g1,g3)
    c: Equal(g1,g4)
    c: DistanceY(g4,g2) = 28
    c: DistanceX(g2,g4) = 0
    c: DistanceX(g3,g4) = 28
    c: DistanceX(g3,g1) = 0
    c: DistanceY(g3,g4) = 0
    c: DistanceY(g1,g2) = 0
    c: Symmetric(g2,g3,g0)
    c: Coincident(g5,g0)
    c: Diameter(g5) = 28
    c: DistanceY(g5,g-1) = 11
    c: DistanceX(g5,g-1) = 109.25
FEATURE [PartDesign::Pocket] Pocket056
  AddSubType = 1
  AutoTaperInnerAngle = true
  BaseFeature = -> Pocket055
  CheckUpToFaceLimits = true
  ClaimChildren = false
  Fit = 0
  FitJoin = 0
  InnerFit = 0
  InnerFitJoin = 0
  InvalidShape = false
  Length = 3
  Length2 = 100
  Linearize = true
  NewSolid = false
  Profile = -> Sketch110
  Suppress = false
  TaperInnerAngle = 0
  TaperInnerAngleRev = 0
  TreeRank = 297
  Type = 0
  ValidateShape = true
  _ProfileBasedVersion = 1
  _Version = 1
  expr: Length = <<Parameters>>.thickness
FEATURE [Sketcher::SketchObject] Sketch111
  ArcFitTolerance = 1e-06
  AttachmentSupport = -> [Pocket056]
  ExternalBSplineMaxDegree = 5
  ExternalBSplineTolerance = 0.0001
  FullyConstrained = false
  InternalTolerance = 1e-06
  InvalidShape = false
  MakeInternals = false
  MapMode = 5
  Placement = pos=(-3.81e-14,-76.8891,76.8891) rot=(1,0,0;0.785398rad)
  Support = -> [Pocket056]
  TreeRank = 322
  ValidateShape = true
  expr: Constraints[10] = <<Parameters>>.screen_position
  expr: Constraints[11] = Spreadsheet.screen_opening_width
  expr: Constraints[12] = Spreadsheet.screen_opening_height
  expr: Constraints[13] = <<Parameters>>.power_switch_diameter
  sketch-geometry (6):
    g0: LineSegment StartX=-116 StartY=-136.75 StartZ=0 EndX=-116 EndY=-47.25 EndZ=0
    g1: LineSegment StartX=-116 StartY=-47.25 StartZ=0 EndX=116 EndY=-47.25 EndZ=0
    g2: LineSegment StartX=116 StartY=-47.25 StartZ=0 EndX=116 EndY=-136.75 EndZ=0
    g3: LineSegment StartX=116 StartY=-136.75 StartZ=0 EndX=-116 EndY=-136.75 EndZ=0
    g4: GeomPoint [constr] X=0 Y=-92 Z=0
    g5: Circle CenterX=142.523 CenterY=-66.2672 CenterZ=0 NormalX=0 NormalY=0 NormalZ=1 AngleXU=0 Radius=9.75
  constraints (14):
    c: Coincident(g0,g1)
    c: Coincident(g1,g2)
    c: Coincident(g2,g3)
    c: Coincident(g3,g0)
    c: Horizontal(g1)
    c: Horizontal(g3)
    c: Vertical(g0)
    c: Vertical(g2)
    c: Symmetric(g1,g0,g4)
    c: PointOnObject(g4,g-2)
    c: DistanceY(g4,g-1) = 92
    c: DistanceX(g0,g1) = 232
    c: DistanceY(g2,g1) = 89.5
    c: Diameter(g5) = 19.5
FEATURE [PartDesign::Pocket] Pocket057
  AddSubType = 1
  AutoTaperInnerAngle = true
  BaseFeature = -> Pocket056
  CheckUpToFaceLimits = true
  ClaimChildren = false
  Fit = 0
  FitJoin = 0
  InnerFit = 0
  InnerFitJoin = 0
  InvalidShape = false
  Length = 5.5
  Length2 = 100
  Linearize = true
  NewSolid = false
  Profile = -> Sketch111
  Suppress = false
  TaperInnerAngle = 0
  TaperInnerAngleRev = 0
  TreeRank = 323
  Type = 0
  ValidateShape = true
  _ProfileBasedVersion = 1
  _Version = 1
  expr: Length = <<Parameters>>.screen_body_thickness
FEATURE [Sketcher::SketchObject] Sketch112
  ArcFitTolerance = 1e-06
  ExternalBSplineMaxDegree = 5
  ExternalBSplineTolerance = 0.0001
  FullyConstrained = true
  InternalTolerance = 1e-06
  InvalidShape = false
  MakeInternals = false
  MapMode = 5
  Placement = pos=(-3.84e-14,-76.8891,76.8891) rot=(1,0,0;0.785398rad)
  TreeRank = 345
  ValidateShape = true
  expr: Constraints[10] = <<Parameters>>.screen_opening_height + 2 * <<Parameters>>.screen_relief_width
  expr: Constraints[11] = <<Parameters>>.screen_opening_width + 2 * <<Parameters>>.screen_relief_width
  expr: Constraints[12] = <<Parameters>>.screen_position
  sketch-geometry (5):
    g0: LineSegment StartX=-117.5 StartY=-138.25 StartZ=0 EndX=-117.5 EndY=-45.75 EndZ=0
    g1: LineSegment StartX=-117.5 StartY=-45.75 StartZ=0 EndX=117.5 EndY=-45.75 EndZ=0
    g2: LineSegment StartX=117.5 StartY=-45.75 StartZ=0 EndX=117.5 EndY=-138.25 EndZ=0
    g3: LineSegment StartX=117.5 StartY=-138.25 StartZ=0 EndX=-117.5 EndY=-138.25 EndZ=0
    g4: GeomPoint [constr] X=0 Y=-92 Z=0
  constraints (13):
    c: Coincident(g0,g1)
    c: Coincident(g1,g2)
    c: Coincident(g2,g3)
    c: Coincident(g3,g0)
    c: Horizontal(g1)
    c: Horizontal(g3)
    c: Vertical(g0)
    c: Vertical(g2)
    c: Symmetric(g1,g0,g4)
    c: PointOnObject(g4,g-2)
    c: DistanceY(g2,g1) = 92.5
    c: DistanceX(g0,g1) = 235
    c: DistanceY(g4,g-1) = 92
FEATURE [PartDesign::Pocket] Pocket058
  AddSubType = 1
  AutoTaperInnerAngle = true
  BaseFeature = -> Pocket057
  CheckUpToFaceLimits = true
  ClaimChildren = false
  Fit = 0
  FitJoin = 0
  InnerFit = 0
  InnerFitJoin = 0
  InvalidShape = false
  Length = 2
  Length2 = 100
  Linearize = true
  NewSolid = false
  Profile = -> Sketch112
  Suppress = false
  TaperInnerAngle = 0
  TaperInnerAngleRev = 0
  TreeRank = 346
  Type = 0
  ValidateShape = true
  _ProfileBasedVersion = 1
  _Version = 1
  expr: Length = <<Parameters>>.screen_relief_depth
FEATURE [PartDesign::Pocket] Pocket053
  AddSubType = 1
  AutoTaperInnerAngle = true
  BaseFeature = -> Pocket058
  CheckUpToFaceLimits = true
  ClaimChildren = false
  Fit = 0
  FitJoin = 0
  InnerFit = 0
  InnerFitJoin = 0
  InvalidShape = false
  Length = 1
  Length2 = 10
  Linearize = true
  NewSolid = false
  Profile = -> Sketch107
  Suppress = false
  TaperInnerAngle = 0
  TaperInnerAngleRev = 0
  TreeRank = 266
  Type = 4
  ValidateShape = true
  _ProfileBasedVersion = 1
  _Version = 1
  expr: Length = <<Parameters>>.lap_join_thickness
FEATURE [Sketcher::SketchObject] Sketch113
  ArcFitTolerance = 1e-06
  AttachmentOffset = pos=(0,0,88) rot=(0,0,1;0rad)
  AttachmentSupport = -> [XZ_Plane016]
  ExternalBSplineMaxDegree = 5
  ExternalBSplineTolerance = 0.0001
  FullyConstrained = true
  InternalTolerance = 1e-06
  InvalidShape = false
  MakeInternals = false
  MapMode = 5
  Placement = pos=(0,-88,1.95e-14) rot=(1,0,0;1.5708rad)
  Support = -> [XZ_Plane016]
  TreeRank = 375
  ValidateShape = true
  expr: AttachmentOffset.Base.z = <<Parameters>>.station_diameter + <<Parameters>>.thickness
  expr: Constraints[100] = (<<Parameters>>.motor_height - <<Parameters>>.motor_shaft_length) / 2
  expr: Constraints[101] = <<Parameters>>.station_diameter * 2 + <<Parameters>>.thickness
  expr: Constraints[102] = <<Parameters>>.station_diameter / 3 * 2
  expr: Constraints[103] = <<Parameters>>.station_diameter / 3 * 2 - <<Parameters>>.thickness
  expr: Constraints[92] = <<Parameters>>.motor_height + <<Parameters>>.motor_shaft_length - 2 * <<Parameters>>.thickness
  expr: Constraints[97] = (<<Parameters>>.motor_height - <<Parameters>>.motor_shaft_length) / 2
  expr: Constraints[98] = (<<Parameters>>.motor_height - <<Parameters>>.motor_shaft_length) / 2
  expr: Constraints[99] = (<<Parameters>>.motor_height - <<Parameters>>.motor_shaft_length) / 2
  sketch-geometry (39):
    g0: LineSegment StartX=0 StartY=16 StartZ=0 EndX=-15.2028 EndY=9.7028 EndZ=0
    g1: LineSegment StartX=-15.2028 StartY=9.7028 StartZ=0 EndX=-21.5 EndY=-5.5 EndZ=0
    g2: LineSegment StartX=-21.5 StartY=-5.5 StartZ=0 EndX=-15.2028 EndY=-20.7028 EndZ=0
    g3: LineSegment StartX=-15.2028 StartY=-20.7028 StartZ=0 EndX=0 EndY=-27 EndZ=0
    g4: LineSegment StartX=6e-16 StartY=-27 StartZ=0 EndX=15.2028 EndY=-20.7028 EndZ=0
    g5: LineSegment StartX=15.2028 StartY=-20.7028 StartZ=0 EndX=21.5 EndY=-5.5 EndZ=0
    g6: LineSegment StartX=21.5 StartY=-5.5 StartZ=0 EndX=15.2028 EndY=9.7028 EndZ=0
    g7: LineSegment StartX=15.2028 StartY=9.7028 StartZ=0 EndX=0 EndY=16 EndZ=0
    g8: Circle [constr] CenterX=0 CenterY=-5.5 CenterZ=0 NormalX=0 NormalY=0 NormalZ=1 AngleXU=0 Radius=21.5
    g9: LineSegment StartX=56.6667 StartY=16 StartZ=0 EndX=41.4639 EndY=9.7028 EndZ=0
    g10: LineSegment StartX=41.4639 StartY=9.7028 StartZ=0 EndX=35.1667 EndY=-5.5 EndZ=0
    g11: LineSegment StartX=35.1667 StartY=-5.5 StartZ=0 EndX=41.4639 EndY=-20.7028 EndZ=0
    g12: LineSegment StartX=41.4639 StartY=-20.7028 StartZ=0 EndX=56.6667 EndY=-27 EndZ=0
    g13: LineSegment StartX=56.6667 StartY=-27 StartZ=0 EndX=71.8695 EndY=-20.7028 EndZ=0
    g14: LineSegment StartX=71.8695 StartY=-20.7028 StartZ=0 EndX=78.1667 EndY=-5.5 EndZ=0
    g15: LineSegment StartX=78.1667 StartY=-5.5 StartZ=0 EndX=71.8695 EndY=9.7028 EndZ=0
    g16: LineSegment StartX=71.8695 StartY=9.7028 StartZ=0 EndX=56.6667 EndY=16 EndZ=0
    g17: Circle [constr] CenterX=56.6667 CenterY=-5.5 CenterZ=0 NormalX=0 NormalY=0 NormalZ=1 AngleXU=0 Radius=21.5
    g18: LineSegment StartX=119.333 StartY=16 StartZ=0 EndX=104.131 EndY=9.7028 EndZ=0
    g19: LineSegment StartX=104.131 StartY=9.7028 StartZ=0 EndX=97.8333 EndY=-5.5 EndZ=0
    g20: LineSegment StartX=97.8333 StartY=-5.5 StartZ=0 EndX=104.131 EndY=-20.7028 EndZ=0
    g21: LineSegment StartX=104.131 StartY=-20.7028 StartZ=0 EndX=119.333 EndY=-27 EndZ=0
    g22: LineSegment StartX=119.333 StartY=-27 StartZ=0 EndX=134.536 EndY=-20.7028 EndZ=0
    g23: LineSegment StartX=134.536 StartY=-20.7028 StartZ=0 EndX=140.833 EndY=-5.5 EndZ=0
    g24: LineSegment StartX=140.833 StartY=-5.5 StartZ=0 EndX=134.536 EndY=9.7028 EndZ=0
    g25: LineSegment StartX=134.536 StartY=9.7028 StartZ=0 EndX=119.333 EndY=16 EndZ=0
    g26: Circle [constr] CenterX=119.333 CenterY=-5.5 CenterZ=0 NormalX=0 NormalY=0 NormalZ=1 AngleXU=0 Radius=21.5
    g27: LineSegment [constr] StartX=188.203 StartY=9.7028 StartZ=0 EndX=173 EndY=16 EndZ=0
    g28: LineSegment StartX=173 StartY=16 StartZ=0 EndX=157.797 EndY=9.7028 EndZ=0
    g29: LineSegment StartX=157.797 StartY=9.7028 StartZ=0 EndX=151.5 EndY=-5.5 EndZ=0
    g30: LineSegment StartX=151.5 StartY=-5.5 StartZ=0 EndX=157.797 EndY=-20.7028 EndZ=0
    g31: LineSegment StartX=157.797 StartY=-20.7028 StartZ=0 EndX=173 EndY=-27 EndZ=0
    g32: LineSegment [constr] StartX=173 StartY=-27 StartZ=0 EndX=188.203 EndY=-20.7028 EndZ=0
    g33: LineSegment [constr] StartX=188.203 StartY=-20.7028 StartZ=0 EndX=194.5 EndY=-5.5 EndZ=0
    g34: LineSegment [constr] StartX=194.5 StartY=-5.5 StartZ=0 EndX=188.203 EndY=9.7028 EndZ=0
    g35: Circle [constr] CenterX=173 CenterY=-5.5 CenterZ=0 NormalX=0 NormalY=0 NormalZ=1 AngleXU=0 Radius=21.5
    g36: LineSegment StartX=173 StartY=16 StartZ=0 EndX=173 EndY=-27 EndZ=0
    g37: LineSegment [constr] StartX=119.333 StartY=16 StartZ=0 EndX=119.333 EndY=-27 EndZ=0
    g38: LineSegment [constr] StartX=56.6667 StartY=16 StartZ=0 EndX=56.6667 EndY=-27 EndZ=0
  constraints (90):
    c: Coincident(g0,g1)
    c: Coincident(g1,g2)
    c: Coincident(g2,g3)
    c: Coincident(g3,g4)
    c: Coincident(g4,g5)
    c: Coincident(g5,g6)
    c: Coincident(g6,g7)
    c: Coincident(g7,g0)
    c: Equal(g0, g1-g7) x7
    c: PointOnObject(g0,g8)
    c: PointOnObject(g1,g8)
    c: PointOnObject(g2,g8)
    c: PointOnObject(g3,g8)
    c: PointOnObject(g4,g8)
    c: PointOnObject(g5,g8)
    c: PointOnObject(g6,g8)
    c: PointOnObject(g7,g8)
    c: Coincident(g9,g10)
    c: Coincident(g10,g11)
    c: Coincident(g11,g12)
    c: Coincident(g12,g13)
    c: Coincident(g13,g14)
    c: Coincident(g14,g15)
    c: Coincident(g15,g16)
    c: Coincident(g16,g9)
    c: Equal(g9, g10-g16) x7
    c: PointOnObject(g9,g17)
    c: PointOnObject(g10,g17)
    c: PointOnObject(g11,g17)
    c: PointOnObject(g12,g17)
    c: PointOnObject(g13,g17)
    c: PointOnObject(g14,g17)
    c: PointOnObject(g15,g17)
    c: PointOnObject(g16,g17)
    c: Coincident(g18,g19)
    c: Coincident(g19,g20)
    c: Coincident(g20,g21)
    c: Coincident(g21,g22)
    c: Coincident(g22,g23)
    c: Coincident(g23,g24)
    c: Coincident(g24,g25)
    c: Coincident(g25,g18)
    c: Equal(g18, g19-g25) x7
    c: PointOnObject(g18,g26)
    c: PointOnObject(g19,g26)
    c: PointOnObject(g20,g26)
    c: PointOnObject(g21,g26)
    c: PointOnObject(g22,g26)
    c: PointOnObject(g23,g26)
    c: PointOnObject(g24,g26)
    c: PointOnObject(g25,g26)
    c: Coincident(g27,g28)
    c: Coincident(g28,g29)
    c: Coincident(g29,g30)
    c: Coincident(g30,g31)
    c: Coincident(g31,g32)
    c: Coincident(g32,g33)
    c: Coincident(g33,g34)
    c: Coincident(g34,g27)
    c: Equal(g27, g28-g34) x7
    c: PointOnObject(g27,g35)
    c: PointOnObject(g28,g35)
    c: PointOnObject(g29,g35)
    c: PointOnObject(g30,g35)
    c: PointOnObject(g31,g35)
    c: PointOnObject(g32,g35)
    c: PointOnObject(g33,g35)
    c: PointOnObject(g34,g35)
    c: Diameter(g8) = 43
    c: Equal(g8,g17)
    c: Equal(g8,g26)
    c: Equal(g8,g35)
    c: PointOnObject(g8,g-2)
    c: DistanceY(g8,g-1) = 5.5
    c: DistanceY(g17,g-1) = 5.5
    c: DistanceY(g26,g-1) = 5.5
    c: DistanceY(g35,g-1) = 5.5
    c: DistanceX(g-1,g35) = 173
    c: DistanceX(g8,g17) = 56.6667
    c: DistanceX(g26,g35) = 53.6667
    c: Coincident(g36,g27)
    c: Coincident(g36,g31)
    c: Coincident(g37,g18)
    c: Coincident(g37,g21)
    c: Coincident(g38,g9)
    c: Coincident(g38,g12)
    c: PointOnObject(g0,g-2)
    c: Vertical(g38)
    c: Vertical(g37)
    c: Vertical(g36)
FEATURE [PartDesign::Pocket] Pocket059
  AddSubType = 1
  AutoTaperInnerAngle = true
  BaseFeature = -> Pocket053
  CheckUpToFaceLimits = true
  ClaimChildren = false
  Fit = 0
  FitJoin = 0
  InnerFit = 0
  InnerFitJoin = 0
  InvalidShape = false
  Length = 20
  Length2 = 100
  Linearize = true
  NewSolid = false
  Profile = -> Sketch113
  Reversed = true
  Suppress = false
  TaperInnerAngle = 0
  TaperInnerAngleRev = 0
  TreeRank = 388
  Type = 0
  ValidateShape = true
  _ProfileBasedVersion = 1
  _Version = 1
FEATURE [PartDesign::Fillet] Fillet023
  AddSubType = 0
  Base = -> Pocket059 [Edge88,Edge77,Edge83]
  BaseFeature = -> Pocket059
  InvalidShape = false
  NewSolid = false
  Radius = 3
  SupportTransform = false
  Suppress = false
  TreeRank = 389
  ValidateShape = true
  expr: Radius = <<Parameters>>.thickness
FEATURE [PartDesign::Fillet] Fillet024
  AddSubType = 0
  Base = -> Fillet023 [Edge132,Edge215,Edge130,Edge214,Edge134,Edge216,Edge136,Edge217,Edge138,Edge218,Edge140,Edge219,Edge126,Edge212,Edge128,Edge213,Edge116,Edge234,Edge118,Edge235,Edge120,Edge236,Edge122,Edge237,Edge275,Edge276,Edge285,Edge306,Edge290,Edge286,Edge135,Edge225,Edge224,Edge137,Edge139,Edge223,Edge141,Edge222,Edge143,Edge221,+31 more]
  BaseFeature = -> Fillet023
  InvalidShape = false
  NewSolid = false
  Radius = 1
  SupportTransform = false
  Suppress = false
  TreeRank = 390
  ValidateShape = true
FEATURE [PartDesign::Body] Body016  label="Bottom-Front-Right (B)"
  AutoGroupSolids = false
  ClaimAllChildren = false
  ExportMode = 0
  Group = -> [Pad043,Sketch101,Pad044,Sketch102,Pad045,Sketch103,Pad046,Sketch104,Pocket051,Pocket052,Sketch105,Sketch106,Sketch107,Pocket054,Pocket055,Sketch108,Sketch109,Sketch110,Pocket056,Sketch111,Pocket057,Sketch112,Pocket058,Pocket053,Sketch113,Pocket059,Fillet023,Fillet024]
  InvalidShape = false
  Origin = -> Origin016
  Tip = -> Fillet024
  TreeRank = 214
  ValidateShape = true
  _ExportChildren = -> [Pad043,Pad044,Pad045,Pad046,Pocket051,Pocket052,Pocket054,Pocket055,Pocket056,Pocket057,Pocket058,Pocket053,Pocket059,Fillet023,Fillet024]
  _GroupVersion = 1
FEATURE [Sketcher::SketchObject] Sketch114
  ArcFitTolerance = 1e-06
  AttachmentSupport = -> [XY_Plane017]
  ExternalBSplineMaxDegree = 5
  ExternalBSplineTolerance = 0.0001
  FullyConstrained = true
  InternalTolerance = 1e-06
  InvalidShape = false
  MakeInternals = false
  MapMode = 5
  Support = -> [XY_Plane017]
  TreeRank = 401
  ValidateShape = true
  sketch-geometry (5):
    g0: ArcOfCircle CenterX=0 CenterY=0 CenterZ=0 NormalX=0 NormalY=0 NormalZ=1 AngleXU=0 Radius=6 StartAngle=3.14159 EndAngle=6.28319
    g1: Circle CenterX=0 CenterY=0 CenterZ=0 NormalX=0 NormalY=0 NormalZ=1 AngleXU=0 Radius=1.375
    g2: LineSegment StartX=-6 StartY=-7e-16 StartZ=0 EndX=-6 EndY=14 EndZ=0
    g3: LineSegment StartX=6 StartY=0 StartZ=0 EndX=6 EndY=14 EndZ=0
    g4: LineSegment StartX=-6 StartY=14 StartZ=0 EndX=6 EndY=14 EndZ=0
  constraints (12):
    c: Coincident(g0,g-1)
    c: Coincident(g1,g0)
    c: Diameter(g0) = 12
    c: Diameter(g1) = 2.75
    c: Vertical(g2)
    c: Vertical(g3)
    c: Coincident(g4,g2)
    c: Coincident(g4,g3)
    c: Horizontal(g4)
    c: Tangent(g0,g3) = -1.5708
    c: Tangent(g0,g2) = 1.5708
    c: DistanceY(g0,g3) = 14
FEATURE [PartDesign::Pad] Pad047
  AddSubType = 0
  AlongSketchNormal = false
  AutoTaperInnerAngle = true
  CheckUpToFaceLimits = true
  ClaimChildren = false
  Direction = (0,0,1)
  Fit = 0
  FitJoin = 0
  InnerFit = 0
  InnerFitJoin = 0
  InvalidShape = false
  Length = 7
  Length2 = 100
  Linearize = true
  NewSolid = false
  Profile = -> Sketch114
  Suppress = false
  TaperInnerAngle = 0
  TaperInnerAngleRev = 0
  TreeRank = 402
  Type = 0
  ValidateShape = true
  _ProfileBasedVersion = 1
FEATURE [Sketcher::SketchObject] Sketch115
  ArcFitTolerance = 1e-06
  AttachmentSupport = -> [YZ_Plane017]
  ExternalBSplineMaxDegree = 5
  ExternalBSplineTolerance = 0.0001
  FullyConstrained = false
  InternalTolerance = 1e-06
  InvalidShape = false
  MakeInternals = false
  MapMode = 5
  Placement = pos=(0,0,0) rot=(0.57735,0.57735,0.57735;2.0944rad)
  Support = -> [YZ_Plane017]
  TreeRank = 403
  ValidateShape = true
  sketch-geometry (3):
    g0: LineSegment StartX=0 StartY=7 StartZ=0 EndX=14 EndY=2 EndZ=0
    g1: LineSegment StartX=14 StartY=2 StartZ=0 EndX=14 EndY=15.2295 EndZ=0
    g2: LineSegment StartX=0 StartY=7 StartZ=0 EndX=14 EndY=15.2295 EndZ=0
  constraints (8):
    c: PointOnObject(g0,g-2)
    c: DistanceY(g-1,g0) = 7
    c: DistanceX(g-1,g0) = 14
    c: DistanceY(g-1,g0) = 2
    c: Coincident(g1,g0)
    c: Vertical(g1)
    c: Coincident(g2,g0)
    c: Coincident(g2,g1)
FEATURE [PartDesign::Pocket] Pocket060
  AddSubType = 1
  AutoTaperInnerAngle = true
  BaseFeature = -> Pad047
  CheckUpToFaceLimits = true
  ClaimChildren = false
  Fit = 0
  FitJoin = 0
  InnerFit = 0
  InnerFitJoin = 0
  InvalidShape = false
  Length = 100
  Length2 = 100
  Linearize = true
  NewSolid = false
  Profile = -> Sketch115
  Suppress = false
  TaperInnerAngle = 0
  TaperInnerAngleRev = 0
  TreeRank = 404
  Type = 4
  ValidateShape = true
  _ProfileBasedVersion = 1
  _Version = 1
FEATURE [Sketcher::SketchObject] Sketch116
  ArcFitTolerance = 1e-06
  AttachmentSupport = -> [XY_Plane017]
  ExternalBSplineMaxDegree = 5
  ExternalBSplineTolerance = 0.0001
  FullyConstrained = true
  InternalTolerance = 1e-06
  InvalidShape = false
  MakeInternals = false
  MapMode = 5
  Support = -> [XY_Plane017]
  TreeRank = 405
  ValidateShape = true
  sketch-geometry (1):
    g0: Circle CenterX=0 CenterY=0 CenterZ=0 NormalX=0 NormalY=0 NormalZ=1 AngleXU=0 Radius=3.125
  constraints (2):
    c: Coincident(g0,g-1)
    c: Diameter(g0) = 6.25
FEATURE [PartDesign::Pocket] Pocket061
  AddSubType = 1
  AutoTaperInnerAngle = true
  BaseFeature = -> Pocket060
  CheckUpToFaceLimits = true
  ClaimChildren = false
  Fit = 0
  FitJoin = 0
  InnerFit = 0
  InnerFitJoin = 0
  InvalidShape = false
  Length = 4.5
  Length2 = 100
  Linearize = true
  NewSolid = false
  Profile = -> Sketch116
  Reversed = true
  Suppress = false
  TaperInnerAngle = 0
  TaperInnerAngleRev = 0
  TreeRank = 406
  Type = 0
  ValidateShape = true
  _ProfileBasedVersion = 1
  _Version = 1
FEATURE [Sketcher::SketchObject] Sketch117
  ArcFitTolerance = 1e-06
  AttachmentSupport = -> [XY_Plane017]
  ExternalBSplineMaxDegree = 5
  ExternalBSplineTolerance = 0.0001
  FullyConstrained = true
  InternalTolerance = 1e-06
  InvalidShape = false
  MakeInternals = false
  MapMode = 5
  Support = -> [XY_Plane017]
  TreeRank = 407
  ValidateShape = true
  sketch-geometry (4):
    g0: LineSegment StartX=-6 StartY=14 StartZ=0 EndX=6 EndY=14 EndZ=0
    g1: LineSegment StartX=6 StartY=14 StartZ=0 EndX=6 EndY=6.5 EndZ=0
    g2: LineSegment StartX=6 StartY=6.5 StartZ=0 EndX=-6 EndY=6.5 EndZ=0
    g3: LineSegment StartX=-6 StartY=6.5 StartZ=0 EndX=-6 EndY=14 EndZ=0
  constraints (11):
    c: Coincident(g0,g1)
    c: Coincident(g1,g2)
    c: Coincident(g2,g3)
    c: Coincident(g3,g0)
    c: Horizontal(g2)
    c: Vertical(g1)
    c: Vertical(g3)
    c: DistanceX(g0,g0) = 12
    c: Symmetric(g0,g0,g-2)
    c: DistanceY(g-1,g1) = 6.5
    c: DistanceY(g-1,g0) = 14
FEATURE [PartDesign::Pad] Pad048
  AddSubType = 0
  AlongSketchNormal = false
  AutoTaperInnerAngle = true
  BaseFeature = -> Pocket061
  CheckUpToFaceLimits = true
  ClaimChildren = false
  Direction = (0,0,1)
  Fit = 0
  FitJoin = 0
  InnerFit = 0
  InnerFitJoin = 0
  InvalidShape = false
  Length = 2.5
  Length2 = 100
  Linearize = true
  NewSolid = false
  Profile = -> Sketch117
  Reversed = true
  Suppress = false
  TaperInnerAngle = 0
  TaperInnerAngleRev = 0
  TreeRank = 408
  Type = 0
  ValidateShape = true
  _ProfileBasedVersion = 1
FEATURE [PartDesign::Fillet] Fillet025
  AddSubType = 0
  Base = -> Pad048 [Edge23]
  BaseFeature = -> Pad048
  InvalidShape = false
  NewSolid = false
  Radius = 2.49
  SupportTransform = false
  Suppress = false
  TreeRank = 409
  ValidateShape = true
FEATURE [PartDesign::Body] Body017  label="Screen Clips"
  AutoGroupSolids = false
  ClaimAllChildren = false
  ExportMode = 0
  Group = -> [Sketch114,Pad047,Sketch115,Pocket060,Sketch116,Pocket061,Sketch117,Pad048,Fillet025]
  InvalidShape = false
  Origin = -> Origin017
  Tip = -> Fillet025
  TreeRank = 30
  ValidateShape = true
  _ExportChildren = -> [Pad047,Pocket060,Pocket061,Pad048,Fillet025]
  _GroupVersion = 1
FEATURE [Sketcher::SketchObject] Sketch118
  ArcFitTolerance = 1e-06
  AttachmentSupport = -> [XZ_Plane018]
  ExternalBSplineMaxDegree = 5
  ExternalBSplineTolerance = 0.0001
  FullyConstrained = true
  InternalTolerance = 1e-06
  InvalidShape = false
  MakeInternals = false
  MapMode = 5
  Placement = pos=(0,0,0) rot=(1,0,0;1.5708rad)
  Support = -> [XZ_Plane018]
  TreeRank = 420
  ValidateShape = true
  expr: Constraints[0] = <<Parameters>>.motor_shaft_mount_diameter / 2 - 2
  expr: Constraints[12] = <<Parameters>>.magnet_thickness + <<Parameters>>.thickness
  expr: Constraints[13] = (<<Parameters>>.motor_shaft_length + <<Parameters>>.magnet_diameter) / 2
  expr: Constraints[1] = <<Parameters>>.motor_shaft_length + <<Parameters>>.thickness - 2
  expr: Constraints[21] = <<Parameters>>.motor_shaft_diameter / 2 + <<Parameters>>.thickness
  sketch-geometry (8):
    g0: GeomPoint [constr] X=-23 Y=-3.8046 Z=0
    g1: GeomPoint [constr] X=-5.5 Y=-20 Z=0
    g2: ArcOfCircle CenterX=-23 CenterY=-21.3571 CenterZ=0 NormalX=0 NormalY=0 NormalZ=1 AngleXU=0 Radius=17.5525 StartAngle=0.0773961 EndAngle=1.5708
    g3: LineSegment StartX=-23 StartY=-3.8046 StartZ=0 EndX=-23 EndY=0 EndZ=0
    g4: LineSegment StartX=-23 StartY=0 StartZ=0 EndX=0 EndY=0 EndZ=0
    g5: LineSegment [constr] StartX=-14.5 StartY=0 StartZ=0 EndX=-14.5 EndY=-6 EndZ=0
    g6: LineSegment StartX=-5.5 StartY=-20 StartZ=0 EndX=0 EndY=-20 EndZ=0
    g7: LineSegment StartX=0 StartY=0 StartZ=0 EndX=0 EndY=-20 EndZ=0
  constraints (22):
    c: DistanceX(g0,g-1) = 23
    c: DistanceY(g1,g-1) = 20
    c: Coincident(g2,g1)
    c: Coincident(g2,g0)
    c: DistanceX(g2,g0) = 0
    c: Coincident(g3,g2)
    c: PointOnObject(g3,g-1)
    c: Vertical(g3)
    c: Coincident(g4,g3)
    c: PointOnObject(g4,g-1)
    c: PointOnObject(g5,g4)
    c: Vertical(g5)
    c: DistanceY(g5,g5) = 6
    c: DistanceX(g5,g-1) = 14.5
    c: PointOnObject(g5,g2)
    c: Coincident(g6,g2)
    c: PointOnObject(g6,g-2)
    c: Horizontal(g6)
    c: Coincident(g7,g6)
    c: Vertical(g7)
    c: Coincident(g4,g7)
    c: DistanceX(g2,g4) = 5.5
FEATURE [PartDesign::Revolution] Revolution001
  AddSubType = 0
  Angle = 360
  Axis = (0,-2e-16,1)
  Base = (0,0,0)
  ClaimChildren = false
  Fit = 0
  FitJoin = 0
  InnerFit = 0
  InnerFitJoin = 0
  InvalidShape = false
  Linearize = true
  NewSolid = false
  Profile = -> Sketch118
  ReferenceAxis = -> Sketch118 [V_Axis]
  Suppress = false
  TreeRank = 421
  ValidateShape = true
  _ProfileBasedVersion = 1
FEATURE [Sketcher::SketchObject] Sketch119
  ArcFitTolerance = 1e-06
  AttachmentSupport = -> [XY_Plane018]
  ExternalBSplineMaxDegree = 5
  ExternalBSplineTolerance = 0.0001
  FullyConstrained = true
  InternalTolerance = 1e-06
  InvalidShape = false
  MakeInternals = false
  MapMode = 5
  Support = -> [XY_Plane018]
  TreeRank = 422
  ValidateShape = true
  expr: Constraints[4] = (<<Parameters>>.motor_shaft_diameter + <<Parameters>>.clearance) / 2
  expr: Constraints[7] = <<Parameters>>.motor_shaft_flat_diameter
  sketch-geometry (3):
    g0: ArcOfCircle CenterX=0 CenterY=0 CenterZ=0 NormalX=0 NormalY=0 NormalZ=1 AngleXU=0 Radius=2.7 StartAngle=2.41186 EndAngle=7.01291
    g1: LineSegment StartX=-2.01246 StartY=1.8 StartZ=0 EndX=2.01246 EndY=1.8 EndZ=0
    g2: GeomPoint [constr] X=0 Y=-2.7 Z=0
  constraints (8):
    c: Coincident(g0,g-1)
    c: Horizontal(g1)
    c: Coincident(g0,g1)
    c: Coincident(g0,g1)
    c: Radius(g0) = 2.7
    c: PointOnObject(g2,g0)
    c: PointOnObject(g2,g-2)
    c: DistanceY(g2,g0) = 4.5
FEATURE [PartDesign::Pocket] Pocket062
  AddSubType = 1
  AutoTaperInnerAngle = true
  BaseFeature = -> Revolution001
  CheckUpToFaceLimits = true
  ClaimChildren = false
  Fit = 0
  FitJoin = 0
  InnerFit = 0
  InnerFitJoin = 0
  InvalidShape = false
  Length = 100
  Length2 = 100
  Linearize = true
  NewSolid = false
  Profile = -> Sketch119
  Suppress = false
  TaperInnerAngle = 0
  TaperInnerAngleRev = 0
  TreeRank = 423
  Type = 0
  ValidateShape = true
  _ProfileBasedVersion = 1
  _Version = 1
FEATURE [Sketcher::SketchObject] Sketch120
  ArcFitTolerance = 1e-06
  AttachmentSupport = -> [XY_Plane018]
  ExternalBSplineMaxDegree = 5
  ExternalBSplineTolerance = 0.0001
  FullyConstrained = true
  InternalTolerance = 1e-06
  InvalidShape = false
  MakeInternals = false
  MapMode = 5
  Support = -> [XY_Plane018]
  TreeRank = 424
  ValidateShape = true
  expr: Constraints[3] = <<Parameters>>.magnet_diameter + <<Parameters>>.clearance
  expr: Constraints[4] = <<Parameters>>.stir_bar_length
  sketch-geometry (2):
    g0: Circle CenterX=-14 CenterY=0 CenterZ=0 NormalX=0 NormalY=0 NormalZ=1 AngleXU=0 Radius=5.2
    g1: Circle CenterX=14 CenterY=0 CenterZ=0 NormalX=0 NormalY=0 NormalZ=1 AngleXU=0 Radius=5.2
  constraints (5):
    c: PointOnObject(g0,g-1)
    c: Equal(g0,g1)
    c: Symmetric(g0,g1,g-1)
    c: Diameter(g0) = 10.4
    c: DistanceX(g0,g1) = 28
FEATURE [PartDesign::Pocket] Pocket063
  AddSubType = 1
  AutoTaperInnerAngle = true
  BaseFeature = -> Pocket062
  CheckUpToFaceLimits = true
  ClaimChildren = false
  Fit = 0
  FitJoin = 0
  InnerFit = 0
  InnerFitJoin = 0
  InvalidShape = false
  Length = 3.2
  Length2 = 100
  Linearize = true
  NewSolid = false
  Profile = -> Sketch120
  Suppress = false
  TaperInnerAngle = 0
  TaperInnerAngleRev = 0
  TreeRank = 425
  Type = 0
  ValidateShape = true
  _ProfileBasedVersion = 1
  _Version = 1
  expr: Length = <<Parameters>>.magnet_thickness + <<Parameters>>.clearance / 2
FEATURE [PartDesign::Fillet] Fillet026
  AddSubType = 0
  Base = -> Pocket063 [Edge1,Edge3,Edge7,Edge4,Edge5]
  BaseFeature = -> Pocket063
  InvalidShape = false
  NewSolid = false
  Radius = 1
  SupportTransform = false
  Suppress = false
  TreeRank = 426
  ValidateShape = true
FEATURE [PartDesign::Body] Body018  label="Motor Shaft Mount"
  AutoGroupSolids = false
  ClaimAllChildren = false
  ExportMode = 0
  Group = -> [Sketch118,Revolution001,Sketch119,Pocket062,Sketch120,Pocket063,Fillet026]
  InvalidShape = false
  Origin = -> Origin018
  Tip = -> Fillet026
  TreeRank = 29
  ValidateShape = true
  _ExportChildren = -> [Revolution001,Pocket062,Pocket063,Fillet026]
  _GroupVersion = 1
FEATURE [Sketcher::SketchObject] Sketch121
  ArcFitTolerance = 1e-06
  AttachmentSupport = -> [XY_Plane]
  ExternalBSplineMaxDegree = 5
  ExternalBSplineTolerance = 0.0001
  FullyConstrained = true
  InternalTolerance = 1e-06
  InvalidShape = false
  MakeInternals = false
  MapMode = 5
  Support = -> [XY_Plane]
  TreeRank = 157
  ValidateShape = true
  expr: Constraints[10] = <same value as first occurrence — deduplicated (x4 in doc)>
  expr: Constraints[11] = <<Parameters>>.thickness * 4 - 2 * <<Parameters>>.clearance
  sketch-geometry (5):
    g0: LineSegment StartX=5.6 StartY=-69.1 StartZ=0 EndX=5.6 EndY=69.1 EndZ=0
    g1: LineSegment StartX=5.6 StartY=69.1 StartZ=0 EndX=-5.6 EndY=69.1 EndZ=0
    g2: LineSegment StartX=-5.6 StartY=69.1 StartZ=0 EndX=-5.6 EndY=-69.1 EndZ=0
    g3: LineSegment StartX=-5.6 StartY=-69.1 StartZ=0 EndX=5.6 EndY=-69.1 EndZ=0
    g4: GeomPoint [constr] X=0 Y=0 Z=0
  constraints (12):
    c: Coincident(g0,g1)
    c: Coincident(g1,g2)
    c: Coincident(g2,g3)
    c: Coincident(g3,g0)
    c: Horizontal(g1)
    c: Horizontal(g3)
    c: Vertical(g0)
    c: Vertical(g2)
    c: Symmetric(g1,g0,g4)
    c: Coincident(g4,g-1)
    c: DistanceY(g0,g0) = 138.2
    c: DistanceX(g1,g0) = 11.2
FEATURE [PartDesign::Pad] Pad049
  AddSubType = 0
  AlongSketchNormal = false
  AutoTaperInnerAngle = true
  CheckUpToFaceLimits = true
  ClaimChildren = false
  Direction = (0,0,1)
  Fit = 0
  FitJoin = 0
  InnerFit = 0
  InnerFitJoin = 0
  InvalidShape = false
  Length = 1
  Length2 = 100
  Linearize = true
  NewSolid = false
  Profile = -> Sketch121
  Reversed = true
  Suppress = false
  TaperInnerAngle = 0
  TaperInnerAngleRev = 0
  TreeRank = 437
  Type = 0
  ValidateShape = true
  _ProfileBasedVersion = 1
  expr: Length = <<Parameters>>.lap_join_thickness
FEATURE [Sketcher::SketchObject] Sketch
  ArcFitTolerance = 1e-06
  AttachmentSupport = -> [XY_Plane]
  ExternalBSplineMaxDegree = 5
  ExternalBSplineTolerance = 0.0001
  FullyConstrained = true
  InternalTolerance = 1e-06
  InvalidShape = false
  MakeInternals = false
  MapMode = 5
  Support = -> [XY_Plane]
  TreeRank = 438
  ValidateShape = true
  expr: Constraints[12] = ((<<Parameters>>.station_diameter + <<Parameters>>.thickness) * 2 - 4 * <<Parameters>>.thickness - <<Parameters>>.motor_shaft_mount_diameter / 2 - 2 * <<Parameters>>.clearance) / 2
  sketch-geometry (5):
    g0: LineSegment StartX=26.5 StartY=3.1 StartZ=0 EndX=26.5 EndY=69.1 EndZ=0
    g1: LineSegment StartX=26.5 StartY=69.1 StartZ=0 EndX=-26.5 EndY=69.1 EndZ=0
    g2: LineSegment StartX=-26.5 StartY=69.1 StartZ=0 EndX=-26.5 EndY=3.1 EndZ=0
    g3: LineSegment StartX=-26.5 StartY=3.1 StartZ=0 EndX=26.5 EndY=3.1 EndZ=0
    g4: GeomPoint [constr] X=0 Y=36.1 Z=0
  constraints (13):
    c: Coincident(g0,g1)
    c: Coincident(g1,g2)
    c: Coincident(g2,g3)
    c: Coincident(g3,g0)
    c: Horizontal(g1)
    c: Horizontal(g3)
    c: Vertical(g0)
    c: Vertical(g2)
    c: Symmetric(g1,g0,g4)
    c: PointOnObject(g4,g-2)
    c: DistanceX(g1,g0) = 53
    c: DistanceY(g0,g0) = 66
    c: DistanceY(g-1,g0) = 69.1
FEATURE [PartDesign::Pad] Pad
  AddSubType = 0
  AlongSketchNormal = false
  AutoTaperInnerAngle = true
  BaseFeature = -> Pad049
  CheckUpToFaceLimits = true
  ClaimChildren = false
  Direction = (0,0,1)
  Fit = 0
  FitJoin = 0
  InnerFit = 0
  InnerFitJoin = 0
  InvalidShape = false
  Length = 8
  Length2 = 100
  Linearize = true
  NewSolid = false
  Profile = -> Sketch
  Suppress = false
  TaperInnerAngle = 0
  TaperInnerAngleRev = 0
  TreeRank = 439
  Type = 0
  ValidateShape = true
  _ProfileBasedVersion = 1
FEATURE [Sketcher::SketchObject] Sketch122
  ArcFitTolerance = 1e-06
  AttachmentSupport = -> [XY_Plane]
  ExternalBSplineMaxDegree = 5
  ExternalBSplineTolerance = 0.0001
  FullyConstrained = false
  InternalTolerance = 1e-06
  InvalidShape = false
  MakeInternals = false
  MapMode = 5
  Support = -> [XY_Plane]
  TreeRank = 440
  ValidateShape = true
  sketch-geometry (2):
    g0: Circle CenterX=9.5 CenterY=64.8205 CenterZ=0 NormalX=0 NormalY=0 NormalZ=1 AngleXU=0 Radius=1.87072
    g1: Circle CenterX=9.5 CenterY=8.32048 CenterZ=0 NormalX=0 NormalY=0 NormalZ=1 AngleXU=0 Radius=1.87072
  constraints (4):
    c: Equal(g0,g1)
    c: DistanceX(g1,g0) = 0
    c: DistanceY(g1,g0) = 56.5
    c: DistanceX(g-1,g1) = 9.5
FEATURE [PartDesign::Hole] Hole001
  AddSubType = 1
  BaseFeature = -> Pad
  ClaimChildren = false
  CustomThreadClearance = 0
  Depth = 25
  DepthType = 0
  Diameter = 2.52
  DrillForDepth = false
  DrillPoint = 1
  DrillPointAngle = 118
  Fit = 0
  FitJoin = 0
  HoleCutCountersinkAngle = 90
  HoleCutCustomValues = false
  HoleCutDepth = 0
  HoleCutDiameter = 6.1
  HoleCutType = 0
  InnerFit = 0
  InnerFitJoin = 0
  InvalidShape = false
  Linearize = true
  ModelThread = true
  NewSolid = false
  Profile = -> Sketch122
  Reversed = true
  Suppress = false
  Tapered = false
  TaperedAngle = 90
  ThreadClass = 0
  ThreadDepth = 25
  ThreadDepthType = 0
  ThreadDirection = 0
  ThreadFit = 0
  ThreadSize = 9
  ThreadType = 1
  Threaded = true
  TreeRank = 441
  UseCustomThreadClearance = false
  ValidateShape = true
  _ProfileBasedVersion = 1
FEATURE [PartDesign::Fillet] Fillet
  AddSubType = 0
  Base = -> Hole001 [Edge1,Edge6,Edge34,Edge33,Edge29,Edge30,Edge2,Edge9,Edge37,Edge32,Edge59,Edge36]
  BaseFeature = -> Hole001
  InvalidShape = false
  NewSolid = false
  Radius = 1
  SupportTransform = false
  Suppress = false
  TreeRank = 442
  ValidateShape = true
FEATURE [PartDesign::Body] Body  label="Buck Converter Glue-in Mount"
  AutoGroupSolids = false
  ClaimAllChildren = false
  ExportMode = 0
  Group = -> [Pad049,Sketch121,Sketch,Pad,Sketch122,Hole001,Fillet]
  InvalidShape = false
  Origin = -> Origin
  Tip = -> Fillet
  TreeRank = 34
  ValidateShape = true
  _ExportChildren = -> [Pad049,Pad,Hole001,Fillet]
  _GroupVersion = 1
FEATURE [Sketcher::SketchObject] Sketch123
  ArcFitTolerance = 1e-06
  AttachmentSupport = -> [XY_Plane019]
  ExternalBSplineMaxDegree = 5
  ExternalBSplineTolerance = 0.0001
  FullyConstrained = true
  InternalTolerance = 1e-06
  InvalidShape = false
  MakeInternals = false
  MapMode = 5
  Support = -> [XY_Plane019]
  TreeRank = 157
  ValidateShape = true
  expr: Constraints[10] = <same value as first occurrence — deduplicated (x4 in doc)>
  expr: Constraints[11] = <<Parameters>>.thickness * 4 - 2 * <<Parameters>>.clearance
  sketch-geometry (5):
    g0: LineSegment StartX=5.6 StartY=-69.1 StartZ=0 EndX=5.6 EndY=69.1 EndZ=0
    g1: LineSegment StartX=5.6 StartY=69.1 StartZ=0 EndX=-5.6 EndY=69.1 EndZ=0
    g2: LineSegment StartX=-5.6 StartY=69.1 StartZ=0 EndX=-5.6 EndY=-69.1 EndZ=0
    g3: LineSegment StartX=-5.6 StartY=-69.1 StartZ=0 EndX=5.6 EndY=-69.1 EndZ=0
    g4: GeomPoint [constr] X=0 Y=0 Z=0
  constraints (12):
    c: Coincident(g0,g1)
    c: Coincident(g1,g2)
    c: Coincident(g2,g3)
    c: Coincident(g3,g0)
    c: Horizontal(g1)
    c: Horizontal(g3)
    c: Vertical(g0)
    c: Vertical(g2)
    c: Symmetric(g1,g0,g4)
    c: Coincident(g4,g-1)
    c: DistanceY(g0,g0) = 138.2
    c: DistanceX(g1,g0) = 11.2
FEATURE [PartDesign::Pad] Pad050
  AddSubType = 0
  AlongSketchNormal = false
  AutoTaperInnerAngle = true
  CheckUpToFaceLimits = true
  ClaimChildren = false
  Direction = (0,0,1)
  Fit = 0
  FitJoin = 0
  InnerFit = 0
  InnerFitJoin = 0
  InvalidShape = false
  Length = 1
  Length2 = 100
  Linearize = true
  NewSolid = false
  Profile = -> Sketch123
  Reversed = true
  Suppress = false
  TaperInnerAngle = 0
  TaperInnerAngleRev = 0
  TreeRank = 452
  Type = 0
  ValidateShape = true
  _ProfileBasedVersion = 1
  expr: Length = <<Parameters>>.lap_join_thickness
FEATURE [Sketcher::SketchObject] Sketch124
  ArcFitTolerance = 1e-06
  AttachmentSupport = -> [XY_Plane019]
  ExternalBSplineMaxDegree = 5
  ExternalBSplineTolerance = 0.0001
  FullyConstrained = true
  InternalTolerance = 1e-06
  InvalidShape = false
  MakeInternals = false
  MapMode = 5
  Support = -> [XY_Plane019]
  TreeRank = 453
  ValidateShape = true
  expr: Constraints[10] = Spreadsheet.pcb_length
  expr: Constraints[11] = Spreadsheet.pcb_width
  sketch-geometry (6):
    g0: LineSegment StartX=25 StartY=-52.5 StartZ=0 EndX=25 EndY=52.5 EndZ=0
    g1: LineSegment StartX=25 StartY=52.5 StartZ=0 EndX=-25 EndY=52.5 EndZ=0
    g2: LineSegment StartX=-25 StartY=52.5 StartZ=0 EndX=-25 EndY=-52.5 EndZ=0
    g3: LineSegment StartX=-25 StartY=-52.5 StartZ=0 EndX=25 EndY=-52.5 EndZ=0
    g4: GeomPoint [constr] X=0 Y=0 Z=0
    g5: GeomPoint [constr] X=0 Y=0 Z=0
  constraints (13):
    c: Coincident(g0,g1)
    c: Coincident(g1,g2)
    c: Coincident(g2,g3)
    c: Coincident(g3,g0)
    c: Horizontal(g1)
    c: Horizontal(g3)
    c: Vertical(g0)
    c: Vertical(g2)
    c: Symmetric(g1,g0,g4)
    c: Coincident(g4,g-1)
    c: DistanceX(g1,g0) = 50
    c: DistanceY(g0,g0) = 105
    c: Coincident(g5,g4)
FEATURE [PartDesign::Pad] Pad051
  AddSubType = 0
  AlongSketchNormal = false
  AutoTaperInnerAngle = true
  BaseFeature = -> Pad050
  CheckUpToFaceLimits = true
  ClaimChildren = false
  Direction = (0,0,1)
  Fit = 0
  FitJoin = 0
  InnerFit = 0
  InnerFitJoin = 0
  InvalidShape = false
  Length = 7
  Length2 = 100
  Linearize = true
  NewSolid = false
  Profile = -> Sketch124
  Suppress = false
  TaperInnerAngle = 0
  TaperInnerAngleRev = 0
  TreeRank = 454
  Type = 0
  ValidateShape = true
  _ProfileBasedVersion = 1
FEATURE [PartDesign::Fillet] Fillet027
  AddSubType = 0
  Base = -> Pad051 [Edge22,Edge23,Edge26,Edge27,Edge10,Edge2,Edge1,Edge7]
  BaseFeature = -> Pad051
  InvalidShape = false
  NewSolid = false
  Radius = 1
  SupportTransform = false
  Suppress = false
  TreeRank = 455
  ValidateShape = true
FEATURE [Sketcher::SketchObject] Sketch125
  ArcFitTolerance = 1e-06
  AttachmentSupport = -> [XY_Plane020]
  ExternalBSplineMaxDegree = 5
  ExternalBSplineTolerance = 0.0001
  FullyConstrained = true
  InternalTolerance = 1e-06
  InvalidShape = false
  MakeInternals = false
  MapMode = 5
  Support = -> [XY_Plane020]
  TreeRank = 466
  ValidateShape = true
  expr: Constraints[11] = <<Parameters>>.motor_width
  expr: Constraints[23] = <<Parameters>>.motor_screw_spacing
  expr: Constraints[31] = <<Parameters>>.motor_screw_shaft_diameter
  sketch-geometry (14):
    g0: LineSegment StartX=17.5 StartY=-17.5 StartZ=0 EndX=17.5 EndY=17.5 EndZ=0
    g1: LineSegment StartX=17.5 StartY=17.5 StartZ=0 EndX=-17.5 EndY=17.5 EndZ=0
    g2: LineSegment StartX=-17.5 StartY=17.5 StartZ=0 EndX=-17.5 EndY=-17.5 EndZ=0
    g3: LineSegment StartX=-17.5 StartY=-17.5 StartZ=0 EndX=17.5 EndY=-17.5 EndZ=0
    g4: GeomPoint [constr] X=1e-16 Y=0 Z=0
    g5: LineSegment [constr] StartX=13 StartY=-13 StartZ=0 EndX=13 EndY=13 EndZ=0
    g6: LineSegment [constr] StartX=13 StartY=13 StartZ=0 EndX=-13 EndY=13 EndZ=0
    g7: LineSegment [constr] StartX=-13 StartY=13 StartZ=0 EndX=-13 EndY=-13 EndZ=0
    g8: LineSegment [constr] StartX=-13 StartY=-13 StartZ=0 EndX=13 EndY=-13 EndZ=0
    g9: GeomPoint [constr] X=1e-16 Y=0 Z=0
    g10: Circle CenterX=-13 CenterY=13 CenterZ=0 NormalX=0 NormalY=0 NormalZ=1 AngleXU=0 Radius=1.75
    g11: Circle CenterX=13 CenterY=13 CenterZ=0 NormalX=0 NormalY=0 NormalZ=1 AngleXU=0 Radius=1.75
    g12: Circle CenterX=13 CenterY=-13 CenterZ=0 NormalX=0 NormalY=0 NormalZ=1 AngleXU=0 Radius=1.75
    g13: Circle CenterX=-13 CenterY=-13 CenterZ=0 NormalX=0 NormalY=0 NormalZ=1 AngleXU=0 Radius=1.75
  constraints (32):
    c: Coincident(g0,g1)
    c: Coincident(g1,g2)
    c: Coincident(g2,g3)
    c: Coincident(g3,g0)
    c: Horizontal(g1)
    c: Horizontal(g3)
    c: Vertical(g0)
    c: Vertical(g2)
    c: Symmetric(g1,g0,g4)
    c: Coincident(g4,g-1)
    c: Equal(g1,g0)
    c: DistanceX(g1,g0) = 35
    c: Coincident(g5,g6)
    c: Coincident(g6,g7)
    c: Coincident(g7,g8)
    c: Coincident(g8,g5)
    c: Horizontal(g6)
    c: Horizontal(g8)
    c: Vertical(g5)
    c: Vertical(g7)
    c: Symmetric(g6,g5,g9)
    c: Coincident(g9,g4)
    c: Equal(g6,g5)
    c: DistanceX(g6,g5) = 26
    c: Coincident(g10,g6)
    c: Coincident(g11,g5)
    c: Coincident(g12,g5)
    c: Coincident(g13,g7)
    c: Equal(g10,g11)
    c: Equal(g10,g12)
    c: Equal(g10,g13)
    c: Diameter(g10) = 3.5
FEATURE [PartDesign::Pad] Pad052
  AddSubType = 0
  AlongSketchNormal = false
  AutoTaperInnerAngle = true
  CheckUpToFaceLimits = true
  ClaimChildren = false
  Direction = (0,0,1)
  Fit = 0
  FitJoin = 0
  InnerFit = 0
  InnerFitJoin = 0
  InvalidShape = false
  Length = 7.845
  Length2 = 100
  Linearize = true
  NewSolid = false
  Profile = -> Sketch125
  Suppress = false
  TaperInnerAngle = 0
  TaperInnerAngleRev = 0
  TreeRank = 467
  Type = 0
  ValidateShape = true
  _ProfileBasedVersion = 1
FEATURE [PartDesign::Fillet] Fillet028
  AddSubType = 0
  Base = -> Pad052 [Edge1,Edge8,Edge2,Edge5]
  BaseFeature = -> Pad052
  InvalidShape = false
  NewSolid = false
  Radius = 5
  SupportTransform = false
  Suppress = false
  TreeRank = 468
  ValidateShape = true
FEATURE [PartDesign::Body] Body020  label="Motor Spacer"
  AutoGroupSolids = false
  ClaimAllChildren = false
  ExportMode = 0
  Group = -> [Sketch125,Pad052,Fillet028]
  InvalidShape = false
  Origin = -> Origin020
  Tip = -> Fillet028
  TreeRank = 465
  ValidateShape = true
  _ExportChildren = -> [Pad052,Fillet028]
  _GroupVersion = 1
FEATURE [Sketcher::SketchObject] Sketch126
  ArcFitTolerance = 1e-06
  AttachmentSupport = -> [XY_Plane019]
  ExternalBSplineMaxDegree = 5
  ExternalBSplineTolerance = 0.0001
  FullyConstrained = true
  InternalTolerance = 1e-06
  InvalidShape = false
  MakeInternals = false
  MapMode = 5
  Support = -> [XY_Plane019]
  TreeRank = 469
  ValidateShape = true
  expr: Constraints[10] = <<Parameters>>.pcb_h_screw
  expr: Constraints[11] = <<Parameters>>.pcb_v_screw
  sketch-geometry (9):
    g0: LineSegment [constr] StartX=21 StartY=-48.5 StartZ=0 EndX=21 EndY=48.5 EndZ=0
    g1: LineSegment [constr] StartX=21 StartY=48.5 StartZ=0 EndX=-21 EndY=48.5 EndZ=0
    g2: LineSegment [constr] StartX=-21 StartY=48.5 StartZ=0 EndX=-21 EndY=-48.5 EndZ=0
    g3: LineSegment [constr] StartX=-21 StartY=-48.5 StartZ=0 EndX=21 EndY=-48.5 EndZ=0
    g4: GeomPoint [constr] X=0 Y=0 Z=0
    g5: Circle CenterX=-21 CenterY=48.5 CenterZ=0 NormalX=0 NormalY=0 NormalZ=1 AngleXU=0 Radius=1.5
    g6: Circle CenterX=21 CenterY=48.5 CenterZ=0 NormalX=0 NormalY=0 NormalZ=1 AngleXU=0 Radius=1.5
    g7: Circle CenterX=-21 CenterY=-48.5 CenterZ=0 NormalX=0 NormalY=0 NormalZ=1 AngleXU=0 Radius=1.5
    g8: Circle CenterX=21 CenterY=-48.5 CenterZ=0 NormalX=0 NormalY=0 NormalZ=1 AngleXU=0 Radius=1.5
  constraints (20):
    c: Coincident(g0,g1)
    c: Coincident(g1,g2)
    c: Coincident(g2,g3)
    c: Coincident(g3,g0)
    c: Horizontal(g1)
    c: Horizontal(g3)
    c: Vertical(g0)
    c: Vertical(g2)
    c: Symmetric(g1,g0,g4)
    c: Coincident(g4,g-1)
    c: DistanceY(g0,g0) = 97
    c: DistanceX(g2,g0) = 42
    c: Coincident(g5,g1)
    c: Coincident(g6,g0)
    c: Coincident(g7,g2)
    c: Coincident(g8,g0)
    c: Equal(g5,g6)
    c: Equal(g5,g7)
    c: Equal(g5,g8)
    c: Diameter(g5) = 3
FEATURE [PartDesign::Hole] Hole002
  AddSubType = 1
  BaseFeature = -> Fillet027
  ClaimChildren = false
  CustomThreadClearance = 0
  Depth = 25
  DepthType = 0
  Diameter = 2.52
  DrillForDepth = false
  DrillPoint = 1
  DrillPointAngle = 118
  Fit = 0
  FitJoin = 0
  HoleCutCountersinkAngle = 90
  HoleCutCustomValues = false
  HoleCutDepth = 0
  HoleCutDiameter = 6.1
  HoleCutType = 0
  InnerFit = 0
  InnerFitJoin = 0
  InvalidShape = false
  Linearize = true
  ModelThread = true
  NewSolid = false
  Profile = -> Sketch126
  Reversed = true
  Suppress = false
  Tapered = false
  TaperedAngle = 90
  ThreadClass = 0
  ThreadDepth = 25
  ThreadDepthType = 0
  ThreadDirection = 0
  ThreadFit = 0
  ThreadSize = 9
  ThreadType = 1
  Threaded = true
  TreeRank = 470
  UseCustomThreadClearance = false
  ValidateShape = true
  _ProfileBasedVersion = 1
FEATURE [PartDesign::Body] Body019  label="Perf Board Glue-in Mount"
  AutoGroupSolids = false
  ClaimAllChildren = false
  ExportMode = 0
  Group = -> [Pad050,Sketch123,Sketch124,Pad051,Fillet027,Sketch126,Hole002]
  InvalidShape = false
  Origin = -> Origin019
  Tip = -> Hole002
  TreeRank = 35
  ValidateShape = true
  _ExportChildren = -> [Pad050,Pad051,Fillet027,Hole002]
  _GroupVersion = 1
